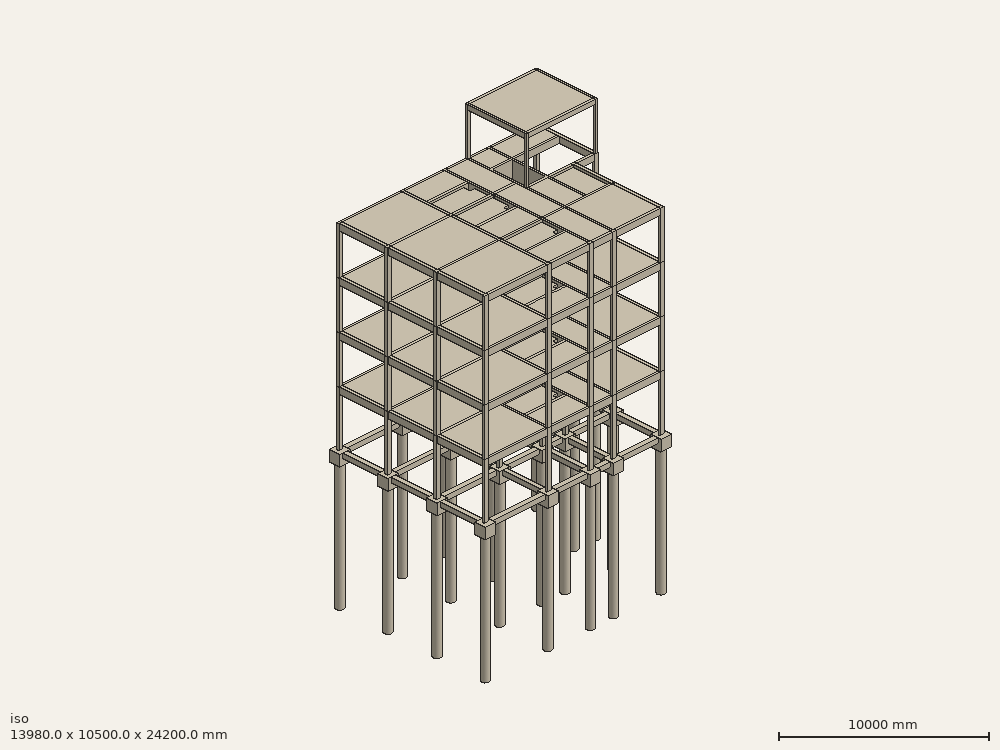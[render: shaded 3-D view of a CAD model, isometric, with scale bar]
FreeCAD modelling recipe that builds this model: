
FCSTD DOCUMENT  (FreeCAD 0.19R24276 (Git))
Label: 2021-02-09 Piloto estructural Metodo 2
License: All rights reserved
objects: Part::FeaturePython×395, Part::Part2DObjectPython×33, App::FeaturePython×28, App::GeometryPython×26, App::DocumentObjectGroup×7, TechDraw::DrawSVGTemplate×3, TechDraw::DrawPage×3, TechDraw::DrawViewAnnotation×2, TechDraw::DrawViewArch×2, Spreadsheet::Sheet×1, App::MaterialObjectPython×1, App::DocumentObjectGroupPython×1, TechDraw::DrawViewPart×1
note: 456 computed .brp shape members not serialized (recipe doc carries the construction recipe); baked Part::Feature solids carry a one-line shape summary decoded from their .brp

FEATURE [Part::FeaturePython] Axis  label="Vertical"  # WARN: FeaturePython — macro-defined, semantics opaque (R4)
  Angles = [0,0,0,0,0,0,0]
  Distances = [1930,4230,2850,1550,1450,1770,1430]
  Length = 11000
  Placement = pos=(0,-500,0) rot=(0,0,1;0rad)
FEATURE [Part::FeaturePython] Axis002  label="Horizontal larga"  # WARN: FeaturePython — macro-defined, semantics opaque (R4)
  Angles = [0,0,0,0,0,0]
  Distances = [100,3250,2620,670,1730,1530]
  Length = 32000
  Placement = pos=(31000,1.077e-12,0) rot=(0,0,1;1.5708rad)
FEATURE [Part::Part2DObjectPython] Rectangle001  label="Lote"  # Draft 2D object (typed FeaturePython)
  Area = 0
  ChamferSize = 0
  Columns = 1
  FilletRadius = 0
  Height = 10000
  Length = 30000
  MakeFace = false
  Rows = 1
FEATURE [Part::Part2DObjectPython] Rectangle002  # Draft 2D object (typed FeaturePython)
  Area = 0
  ChamferSize = 0
  Columns = 1
  FilletRadius = 0
  Height = 700
  Length = 700
  MakeFace = false
  Placement = pos=(14860,9550,0) rot=(0,0,1;0rad)
  Rows = 1
  expr: Height = <<Estructura>>.CabAncho
  expr: Length = <<Estructura>>.CabAncho
FEATURE [Part::Part2DObjectPython] Circle  # Draft 2D object (typed FeaturePython)
  Area = 0
  FirstAngle = 0
  LastAngle = 0
  MakeFace = false
  Placement = pos=(15210,9900,0) rot=(0,0,1;0rad)
  Radius = 250
  expr: Radius = <<Estructura>>.PilRad
FEATURE [Part::FeaturePython] Beam001  # Arch/BIM 7 (typed FeaturePython)
  Chamfer = 0
  DentHeight = 0
  DentLength = 0
  Height = 300
  HorizontalArea = 1059000
  IfcData = attributes={"GlobalId": {"name": "GlobalId", "type": "IfcGloballyUniqueId", "is_enum": false, "enum_values": []}, "Description": {"... (+498 chars omitted),+1 more (map truncated)
  IfcType = 7
  Length = 3530
  MoveBase = false
  MoveWithHost = false
  PerimeterLength = 7660
  Placement = pos=(2280,6490,-800) rot=(0,0,1;0rad)
  PredefinedType = 0
  Tag = VR (30x30)
  VerticalArea = 2298000
  Width = 300
FEATURE [Part::FeaturePython] Structure041  label="Beam002"  # Arch/BIM 7 (typed FeaturePython)
  FaceMaker = 0
  Height = 300
  HorizontalArea = 768000
  IfcData = attributes={"GlobalId": {"name": "GlobalId", "type": "IfcGloballyUniqueId", "is_enum": false, "enum_values": []}, "Description": {"... (+498 chars omitted),+1 more (map truncated)
  IfcType = 7
  Length = 2560
  MoveBase = false
  MoveWithHost = false
  Nodes = (2) [(1.2326e-31,-1.51582e-15,5.55112e-16),(2560,-1.51582e-15,5.55112e-16)]
  NodesOffset = 0
  Normal = (0,0,0)
  PerimeterLength = 5720
  Placement = pos=(1930,9550,-650) rot=(0,0,-1;1.5708rad)
  PredefinedType = 0
  Tag = VR (30x30)
  VerticalArea = 1.716e+06
  Width = 300
  expr: Height = <<Estructura>>.VRAlto
  expr: Width = <<Estructura>>.VRAncho
FEATURE [Part::FeaturePython] Structure042  label="Beam003"  # Arch/BIM 7 (typed FeaturePython)
  FaceMaker = 0
  Height = 300
  HorizontalArea = 777000
  IfcData = attributes={"GlobalId": {"name": "GlobalId", "type": "IfcGloballyUniqueId", "is_enum": false, "enum_values": []}, "Description": {"... (+498 chars omitted),+1 more (map truncated)
  IfcType = 7
  Length = 2590
  MoveBase = false
  MoveWithHost = false
  Nodes = (2) [(1.2326e-31,-1.51582e-15,5.55112e-16),(2590,-1.51582e-15,5.55112e-16)]
  NodesOffset = 0
  Normal = (0,0,0)
  PerimeterLength = 5780
  Placement = pos=(1930,6290,-650) rot=(0,0,-1;1.5708rad)
  PredefinedType = 0
  Tag = VR (30x30)
  VerticalArea = 1.734e+06
  Width = 300
FEATURE [Part::FeaturePython] Structure043  label="Beam004"  # Arch/BIM 7 (typed FeaturePython)
  FaceMaker = 0
  Height = 300
  HorizontalArea = 765000
  IfcData = attributes={"GlobalId": {"name": "GlobalId", "type": "IfcGloballyUniqueId", "is_enum": false, "enum_values": []}, "Description": {"... (+498 chars omitted),+1 more (map truncated)
  IfcType = 7
  Length = 2550
  MoveBase = false
  MoveWithHost = false
  Nodes = (2) [(1.2326e-31,-1.51582e-15,5.55112e-16),(2550,-1.51582e-15,5.55112e-16)]
  NodesOffset = 0
  Normal = (0,0,0)
  PerimeterLength = 5700
  Placement = pos=(1930,3000,-650) rot=(0,0,-1;1.5708rad)
  PredefinedType = 0
  Tag = VR (30x30)
  VerticalArea = 1.71e+06
  Width = 300
FEATURE [Part::FeaturePython] Structure044  label="Beam005"  # Arch/BIM 7 (typed FeaturePython)
  FaceMaker = 0
  Height = 300
  HorizontalArea = 768000
  IfcData = attributes={"GlobalId": {"name": "GlobalId", "type": "IfcGloballyUniqueId", "is_enum": false, "enum_values": []}, "Description": {"... (+498 chars omitted),+1 more (map truncated)
  IfcType = 7
  Length = 2560
  MoveBase = false
  MoveWithHost = false
  Nodes = (2) [(1.2326e-31,-1.51582e-15,5.55112e-16),(2560,-1.51582e-15,5.55112e-16)]
  NodesOffset = 0
  Normal = (0,0,0)
  PerimeterLength = 5720
  Placement = pos=(6160.36,9550,-650) rot=(0,0,-1;1.5708rad)
  PredefinedType = 0
  Tag = VR (30x30)
  VerticalArea = 1.716e+06
  Width = 300
FEATURE [Part::FeaturePython] Structure045  label="Beam006"  # Arch/BIM 7 (typed FeaturePython)
  FaceMaker = 0
  Height = 300
  HorizontalArea = 777000
  IfcData = attributes={"GlobalId": {"name": "GlobalId", "type": "IfcGloballyUniqueId", "is_enum": false, "enum_values": []}, "Description": {"... (+498 chars omitted),+1 more (map truncated)
  IfcType = 7
  Length = 2590
  MoveBase = false
  MoveWithHost = false
  Nodes = (2) [(1.2326e-31,-1.51582e-15,5.55112e-16),(2590,-1.51582e-15,5.55112e-16)]
  NodesOffset = 0
  Normal = (0,0,0)
  PerimeterLength = 5780
  Placement = pos=(6160.36,6290,-650) rot=(0,0,-1;1.5708rad)
  PredefinedType = 0
  Tag = VR (30x30)
  VerticalArea = 1.734e+06
  Width = 300
FEATURE [Part::FeaturePython] Structure046  label="Beam007"  # Arch/BIM 7 (typed FeaturePython)
  FaceMaker = 0
  Height = 300
  HorizontalArea = 765000
  IfcData = attributes={"GlobalId": {"name": "GlobalId", "type": "IfcGloballyUniqueId", "is_enum": false, "enum_values": []}, "Description": {"... (+498 chars omitted),+1 more (map truncated)
  IfcType = 7
  Length = 2550
  MoveBase = false
  MoveWithHost = false
  Nodes = (2) [(1.2326e-31,-1.51582e-15,5.55112e-16),(2550,-1.51582e-15,5.55112e-16)]
  NodesOffset = 0
  Normal = (0,0,0)
  PerimeterLength = 5700
  Placement = pos=(6160.36,3000,-650) rot=(0,0,-1;1.5708rad)
  PredefinedType = 0
  Tag = VR (30x30)
  VerticalArea = 1.71e+06
  Width = 300
FEATURE [Part::FeaturePython] Structure048  label="Beam009"  # Arch/BIM 7 (typed FeaturePython)
  FaceMaker = 0
  Height = 300
  HorizontalArea = 777000
  IfcData = attributes={"GlobalId": {"name": "GlobalId", "type": "IfcGloballyUniqueId", "is_enum": false, "enum_values": []}, "Description": {"... (+498 chars omitted),+1 more (map truncated)
  IfcType = 7
  Length = 2590
  MoveBase = false
  MoveWithHost = false
  Nodes = (2) [(1.2326e-31,-1.51582e-15,5.55112e-16),(2590,-1.51582e-15,5.55112e-16)]
  NodesOffset = 0
  Normal = (0,0,0)
  PerimeterLength = 5780
  Placement = pos=(9010.18,6290,-650) rot=(0,0,-1;1.5708rad)
  PredefinedType = 0
  Tag = VR (30x30)
  VerticalArea = 1.734e+06
  Width = 300
FEATURE [Part::FeaturePython] Structure049  label="Beam010"  # Arch/BIM 7 (typed FeaturePython)
  FaceMaker = 0
  Height = 300
  HorizontalArea = 765000
  IfcData = attributes={"GlobalId": {"name": "GlobalId", "type": "IfcGloballyUniqueId", "is_enum": false, "enum_values": []}, "Description": {"... (+498 chars omitted),+1 more (map truncated)
  IfcType = 7
  Length = 2550
  MoveBase = false
  MoveWithHost = false
  Nodes = (2) [(1.2326e-31,-1.51582e-15,5.55112e-16),(2550,-1.51582e-15,5.55112e-16)]
  NodesOffset = 0
  Normal = (0,0,0)
  PerimeterLength = 5700
  Placement = pos=(9010.18,3000,-650) rot=(0,0,-1;1.5708rad)
  PredefinedType = 0
  Tag = VR (30x30)
  VerticalArea = 1.71e+06
  Width = 300
FEATURE [Part::FeaturePython] Structure053  label="Beam014"  # Arch/BIM 7 (typed FeaturePython)
  FaceMaker = 0
  Height = 300
  HorizontalArea = 765000
  IfcData = attributes={"GlobalId": {"name": "GlobalId", "type": "IfcGloballyUniqueId", "is_enum": false, "enum_values": []}, "Description": {"... (+498 chars omitted),+1 more (map truncated)
  IfcType = 7
  Length = 2550
  MoveBase = false
  MoveWithHost = false
  Nodes = (2) [(1.2326e-31,-1.51582e-15,5.55112e-16),(2550,-1.51582e-15,5.55112e-16)]
  NodesOffset = 0
  Normal = (0,0,0)
  PerimeterLength = 5700
  Placement = pos=(13778.3,3000,-650) rot=(0,0,-1;1.5708rad)
  PredefinedType = 0
  Tag = VR (30x30)
  VerticalArea = 1.71e+06
  Width = 300
FEATURE [Part::FeaturePython] Structure056  label="Beam017"  # Arch/BIM 7 (typed FeaturePython)
  FaceMaker = 0
  Height = 300
  HorizontalArea = 765000
  IfcData = attributes={"GlobalId": {"name": "GlobalId", "type": "IfcGloballyUniqueId", "is_enum": false, "enum_values": []}, "Description": {"... (+498 chars omitted),+1 more (map truncated)
  IfcType = 7
  Length = 2550
  MoveBase = false
  MoveWithHost = false
  Nodes = (2) [(1.2326e-31,-1.51582e-15,5.55112e-16),(2550,-1.51582e-15,5.55112e-16)]
  NodesOffset = 0
  Normal = (0,0,0)
  PerimeterLength = 5700
  Placement = pos=(10560,3000,-650) rot=(0,0,-1;1.5708rad)
  PredefinedType = 0
  Tag = VR (30x30)
  VerticalArea = 1.71e+06
  Width = 300
FEATURE [Part::FeaturePython] Structure059  label="Beam020"  # Arch/BIM 7 (typed FeaturePython)
  FaceMaker = 0
  Height = 300
  HorizontalArea = 645000
  IfcData = attributes={"GlobalId": {"name": "GlobalId", "type": "IfcGloballyUniqueId", "is_enum": false, "enum_values": []}, "Description": {"... (+498 chars omitted),+1 more (map truncated)
  IfcType = 7
  Length = 2150
  MoveBase = false
  MoveWithHost = false
  Nodes = (2) [(1.2326e-31,-1.51582e-15,5.55112e-16),(2150,-1.51582e-15,5.55112e-16)]
  NodesOffset = 0
  Normal = (0,0,0)
  PerimeterLength = 4900
  Placement = pos=(6510,9900,-650) rot=(0,0,1;0rad)
  PredefinedType = 0
  Tag = VR (30x30)
  VerticalArea = 1.47e+06
  Width = 300
FEATURE [Part::FeaturePython] Structure060  label="Beam021"  # Arch/BIM 7 (typed FeaturePython)
  FaceMaker = 0
  Height = 300
  HorizontalArea = 690000
  IfcData = attributes={"GlobalId": {"name": "GlobalId", "type": "IfcGloballyUniqueId", "is_enum": false, "enum_values": []}, "Description": {"... (+498 chars omitted),+1 more (map truncated)
  IfcType = 7
  Length = 2300
  MoveBase = false
  MoveWithHost = false
  Nodes = (2) [(1.2326e-31,-1.51582e-15,5.55112e-16),(2300,-1.51582e-15,5.55112e-16)]
  NodesOffset = 0
  Normal = (0,0,0)
  PerimeterLength = 5200
  Placement = pos=(9360,9900,-650) rot=(0,0,1;0rad)
  PredefinedType = 0
  Tag = VR (30x30)
  VerticalArea = 1.56e+06
  Width = 300
FEATURE [Part::FeaturePython] Structure061  label="Beam022"  # Arch/BIM 7 (typed FeaturePython)
  FaceMaker = 0
  Height = 300
  HorizontalArea = 750000
  IfcData = attributes={"GlobalId": {"name": "GlobalId", "type": "IfcGloballyUniqueId", "is_enum": false, "enum_values": []}, "Description": {"... (+498 chars omitted),+1 more (map truncated)
  IfcType = 7
  Length = 2500
  MoveBase = false
  MoveWithHost = false
  Nodes = (2) [(1.2326e-31,-1.51582e-15,5.55112e-16),(2500,-1.51582e-15,5.55112e-16)]
  NodesOffset = 0
  Normal = (0,0,0)
  PerimeterLength = 5600
  Placement = pos=(12360,9900,-650) rot=(0,0,1;0rad)
  PredefinedType = 0
  Tag = VR (30x30)
  VerticalArea = 1680000
  Width = 300
FEATURE [Part::FeaturePython] Structure064  label="Beam025"  # Arch/BIM 7 (typed FeaturePython)
  FaceMaker = 0
  Height = 300
  HorizontalArea = 645000
  IfcData = attributes={"GlobalId": {"name": "GlobalId", "type": "IfcGloballyUniqueId", "is_enum": false, "enum_values": []}, "Description": {"... (+498 chars omitted),+1 more (map truncated)
  IfcType = 7
  Length = 2150
  MoveBase = false
  MoveWithHost = false
  Nodes = (2) [(1.2326e-31,-1.51582e-15,5.55112e-16),(2150,-1.51582e-15,5.55112e-16)]
  NodesOffset = 0
  Normal = (0,0,0)
  PerimeterLength = 4900
  Placement = pos=(6510,6640,-650) rot=(0,0,1;0rad)
  PredefinedType = 0
  Tag = VR (30x30)
  VerticalArea = 1.47e+06
  Width = 300
FEATURE [Part::FeaturePython] Structure065  label="Beam026"  # Arch/BIM 7 (typed FeaturePython)
  FaceMaker = 0
  Height = 300
  HorizontalArea = 768000
  IfcData = attributes={"GlobalId": {"name": "GlobalId", "type": "IfcGloballyUniqueId", "is_enum": false, "enum_values": []}, "Description": {"... (+498 chars omitted),+1 more (map truncated)
  IfcType = 7
  Length = 2560
  MoveBase = false
  MoveWithHost = false
  Nodes = (2) [(1.2326e-31,-1.51582e-15,5.55112e-16),(2560,-1.51582e-15,5.55112e-16)]
  NodesOffset = 0
  Normal = (0,0,0)
  PerimeterLength = 5720
  Placement = pos=(9010,6990,-650) rot=(0,0,1;1.5708rad)
  PredefinedType = 0
  Tag = VR (30x30)
  VerticalArea = 1.716e+06
  Width = 300
FEATURE [Part::FeaturePython] Structure066  label="Beam027"  # Arch/BIM 7 (typed FeaturePython)
  FaceMaker = 0
  Height = 300
  HorizontalArea = 1.059e+06
  IfcData = attributes={"GlobalId": {"name": "GlobalId", "type": "IfcGloballyUniqueId", "is_enum": false, "enum_values": []}, "Description": {"... (+498 chars omitted),+1 more (map truncated)
  IfcType = 7
  Length = 3530
  MoveBase = false
  MoveWithHost = false
  Nodes = (2) [(1.2326e-31,-1.51582e-15,5.55112e-16),(3530,-1.51582e-15,5.55112e-16)]
  NodesOffset = 0
  Normal = (0,0,0)
  PerimeterLength = 7660
  Placement = pos=(2280,3350,-650) rot=(0,0,1;0rad)
  PredefinedType = 0
  Tag = VR (30x30)
  VerticalArea = 2.298e+06
  Width = 300
FEATURE [Part::FeaturePython] Structure067  label="Beam028"  # Arch/BIM 7 (typed FeaturePython)
  FaceMaker = 0
  Height = 300
  HorizontalArea = 645000
  IfcData = attributes={"GlobalId": {"name": "GlobalId", "type": "IfcGloballyUniqueId", "is_enum": false, "enum_values": []}, "Description": {"... (+498 chars omitted),+1 more (map truncated)
  IfcType = 7
  Length = 2150
  MoveBase = false
  MoveWithHost = false
  Nodes = (2) [(1.2326e-31,-1.51582e-15,5.55112e-16),(2150,-1.51582e-15,5.55112e-16)]
  NodesOffset = 0
  Normal = (0,0,0)
  PerimeterLength = 4900
  Placement = pos=(6510,3350,-650) rot=(0,0,1;0rad)
  PredefinedType = 0
  Tag = VR (30x30)
  VerticalArea = 1.47e+06
  Width = 300
FEATURE [Part::FeaturePython] Structure068  label="Beam029"  # Arch/BIM 7 (typed FeaturePython)
  FaceMaker = 0
  Height = 300
  HorizontalArea = 1.059e+06
  IfcData = attributes={"GlobalId": {"name": "GlobalId", "type": "IfcGloballyUniqueId", "is_enum": false, "enum_values": []}, "Description": {"... (+498 chars omitted),+1 more (map truncated)
  IfcType = 7
  Length = 3530
  MoveBase = false
  MoveWithHost = false
  Nodes = (2) [(1.2326e-31,-1.51582e-15,5.55112e-16),(3530,-1.51582e-15,5.55112e-16)]
  NodesOffset = 0
  Normal = (0,0,0)
  PerimeterLength = 7660
  Placement = pos=(2280,100,-650) rot=(0,0,1;0rad)
  PredefinedType = 0
  Tag = VR (30x30)
  VerticalArea = 2.298e+06
  Width = 300
FEATURE [Part::FeaturePython] Structure069  label="Beam030"  # Arch/BIM 7 (typed FeaturePython)
  FaceMaker = 0
  Height = 300
  HorizontalArea = 645000
  IfcData = attributes={"GlobalId": {"name": "GlobalId", "type": "IfcGloballyUniqueId", "is_enum": false, "enum_values": []}, "Description": {"... (+498 chars omitted),+1 more (map truncated)
  IfcType = 7
  Length = 2150
  MoveBase = false
  MoveWithHost = false
  Nodes = (2) [(1.2326e-31,-1.51582e-15,5.55112e-16),(2150,-1.51582e-15,5.55112e-16)]
  NodesOffset = 0
  Normal = (0,0,0)
  PerimeterLength = 4900
  Placement = pos=(6510,100,-650) rot=(0,0,1;0rad)
  PredefinedType = 0
  Tag = VR (30x30)
  VerticalArea = 1.47e+06
  Width = 300
FEATURE [Part::FeaturePython] Structure070  label="Beam031"  # Arch/BIM 7 (typed FeaturePython)
  FaceMaker = 0
  Height = 300
  HorizontalArea = 255000
  IfcData = attributes={"GlobalId": {"name": "GlobalId", "type": "IfcGloballyUniqueId", "is_enum": false, "enum_values": []}, "Description": {"... (+498 chars omitted),+1 more (map truncated)
  IfcType = 7
  Length = 850
  MoveBase = false
  MoveWithHost = false
  Nodes = (2) [(1.2326e-31,-1.51582e-15,5.55112e-16),(850,-1.51582e-15,5.55112e-16)]
  NodesOffset = 0
  Normal = (0,0,0)
  PerimeterLength = 2300
  Placement = pos=(9360,100,-650) rot=(0,0,1;0rad)
  PredefinedType = 0
  Tag = VR (30x30)
  VerticalArea = 690000
  Width = 300
FEATURE [Part::FeaturePython] Structure071  label="Beam032"  # Arch/BIM 7 (typed FeaturePython)
  FaceMaker = 0
  Height = 300
  HorizontalArea = 756000
  IfcData = attributes={"GlobalId": {"name": "GlobalId", "type": "IfcGloballyUniqueId", "is_enum": false, "enum_values": []}, "Description": {"... (+498 chars omitted),+1 more (map truncated)
  IfcType = 7
  Length = 2520
  MoveBase = false
  MoveWithHost = false
  Nodes = (2) [(1.2326e-31,-1.51582e-15,5.55112e-16),(2520,-1.51582e-15,5.55112e-16)]
  NodesOffset = 0
  Normal = (0,0,0)
  PerimeterLength = 5640
  Placement = pos=(10910,100,-650) rot=(0,0,1;0rad)
  PredefinedType = 0
  Tag = VR (30x30)
  VerticalArea = 1.692e+06
  Width = 300
FEATURE [Part::FeaturePython] Structure072  label="Beam033"  # Arch/BIM 7 (typed FeaturePython)
  FaceMaker = 0
  Height = 300
  HorizontalArea = 255000
  IfcData = attributes={"GlobalId": {"name": "GlobalId", "type": "IfcGloballyUniqueId", "is_enum": false, "enum_values": []}, "Description": {"... (+498 chars omitted),+1 more (map truncated)
  IfcType = 7
  Length = 850
  MoveBase = false
  MoveWithHost = false
  Nodes = (2) [(1.2326e-31,-1.51582e-15,5.55112e-16),(850,-1.51582e-15,5.55112e-16)]
  NodesOffset = 0
  Normal = (0,0,0)
  PerimeterLength = 2300
  Placement = pos=(9360,3350,-650) rot=(0,0,1;0rad)
  PredefinedType = 0
  Tag = VR (30x30)
  VerticalArea = 690000
  Width = 300
FEATURE [Part::FeaturePython] Structure073  label="Beam034"  # Arch/BIM 7 (typed FeaturePython)
  FaceMaker = 0
  Height = 300
  HorizontalArea = 756000
  IfcData = attributes={"GlobalId": {"name": "GlobalId", "type": "IfcGloballyUniqueId", "is_enum": false, "enum_values": []}, "Description": {"... (+498 chars omitted),+1 more (map truncated)
  IfcType = 7
  Length = 2520
  MoveBase = false
  MoveWithHost = false
  Nodes = (2) [(1.2326e-31,-1.51582e-15,5.55112e-16),(2520,-1.51582e-15,5.55112e-16)]
  NodesOffset = 0
  Normal = (0,0,0)
  PerimeterLength = 5640
  Placement = pos=(10910,3350,-650) rot=(0,0,1;0rad)
  PredefinedType = 0
  Tag = VR (30x30)
  VerticalArea = 1.692e+06
  Width = 300
FEATURE [Part::FeaturePython] Structure074  label="Beam035"  # Arch/BIM 7 (typed FeaturePython)
  FaceMaker = 0
  Height = 300
  HorizontalArea = 969000
  IfcData = attributes={"GlobalId": {"name": "GlobalId", "type": "IfcGloballyUniqueId", "is_enum": false, "enum_values": []}, "Description": {"... (+498 chars omitted),+1 more (map truncated)
  IfcType = 7
  Length = 3230
  MoveBase = false
  MoveWithHost = false
  Nodes = (2) [(1.2326e-31,-1.51582e-15,5.55112e-16),(3230,-1.51582e-15,5.55112e-16)]
  NodesOffset = 0
  Normal = (0,0,0)
  PerimeterLength = 7060
  Placement = pos=(15210,9550,-650) rot=(0,0,-1;1.5708rad)
  PredefinedType = 0
  Tag = VR (30x30)
  VerticalArea = 2.118e+06
  Width = 300
FEATURE [Part::FeaturePython] Structure075  label="Beam036"  # Arch/BIM 7 (typed FeaturePython)
  FaceMaker = 0
  Height = 300
  HorizontalArea = 576000
  IfcData = attributes={"GlobalId": {"name": "GlobalId", "type": "IfcGloballyUniqueId", "is_enum": false, "enum_values": []}, "Description": {"... (+498 chars omitted),+1 more (map truncated)
  IfcType = 7
  Length = 1920
  MoveBase = false
  MoveWithHost = false
  Nodes = (2) [(1.2326e-31,-1.51582e-15,5.55112e-16),(1920,-1.51582e-15,5.55112e-16)]
  NodesOffset = 0
  Normal = (0,0,0)
  PerimeterLength = 4440
  Placement = pos=(13780,3700,-650) rot=(0,0,1;1.5708rad)
  PredefinedType = 0
  Tag = VR (30x30)
  VerticalArea = 1332000
  Width = 300
FEATURE [Part::FeaturePython] Structure076  label="Beam037"  # Arch/BIM 7 (typed FeaturePython)
  FaceMaker = 0
  Height = 300
  HorizontalArea = 219000
  IfcData = attributes={"GlobalId": {"name": "GlobalId", "type": "IfcGloballyUniqueId", "is_enum": false, "enum_values": []}, "Description": {"... (+498 chars omitted),+1 more (map truncated)
  IfcType = 7
  Length = 730
  MoveBase = false
  MoveWithHost = false
  Nodes = (2) [(1.2326e-31,-1.51582e-15,5.55112e-16),(730,-1.51582e-15,5.55112e-16)]
  NodesOffset = 0
  Normal = (0,0,0)
  PerimeterLength = 2060
  Placement = pos=(14130,5970,-650) rot=(0,0,1;0rad)
  PredefinedType = 0
  Tag = VR (30x30)
  VerticalArea = 618000
  Width = 300
FEATURE [Part::FeaturePython] Structure077  label="Beam038"  # Arch/BIM 7 (typed FeaturePython)
  FaceMaker = 0
  Height = 300
  HorizontalArea = 681000
  IfcData = attributes={"GlobalId": {"name": "GlobalId", "type": "IfcGloballyUniqueId", "is_enum": false, "enum_values": []}, "Description": {"... (+498 chars omitted),+1 more (map truncated)
  IfcType = 7
  Length = 2270
  MoveBase = false
  MoveWithHost = false
  Nodes = (2) [(1.2326e-31,-1.51582e-15,5.55112e-16),(2270,-1.51582e-15,5.55112e-16)]
  NodesOffset = 0
  Normal = (0,0,0)
  PerimeterLength = 5140
  Placement = pos=(10560,3700,-650) rot=(0,0,1;1.5708rad)
  PredefinedType = 0
  Tag = VR (30x30)
  VerticalArea = 1.542e+06
  Width = 300
FEATURE [Part::FeaturePython] Structure078  label="Beam039"  # Arch/BIM 7 (typed FeaturePython)
  FaceMaker = 0
  Height = 300
  HorizontalArea = 414000
  IfcData = attributes={"GlobalId": {"name": "GlobalId", "type": "IfcGloballyUniqueId", "is_enum": false, "enum_values": []}, "Description": {"... (+498 chars omitted),+1 more (map truncated)
  IfcType = 7
  Length = 1380
  MoveBase = false
  MoveWithHost = false
  Nodes = (2) [(1.2326e-31,-1.51582e-15,5.55112e-16),(1380,-1.51582e-15,5.55112e-16)]
  NodesOffset = 0
  Normal = (0,0,0)
  PerimeterLength = 3360
  Placement = pos=(10560,9750,-650) rot=(0,0,-1;1.5708rad)
  PredefinedType = 0
  Tag = VR (30x30)
  VerticalArea = 1008000
  Width = 300
FEATURE [Part::FeaturePython] Structure079  label="Beam040"  # Arch/BIM 7 (typed FeaturePython)
  FaceMaker = 0
  Height = 300
  HorizontalArea = 354000
  IfcData = attributes={"GlobalId": {"name": "GlobalId", "type": "IfcGloballyUniqueId", "is_enum": false, "enum_values": []}, "Description": {"... (+498 chars omitted),+1 more (map truncated)
  IfcType = 7
  Length = 1180
  MoveBase = false
  MoveWithHost = false
  Nodes = (2) [(1.2326e-31,-1.51582e-15,5.55112e-16),(1180,-1.51582e-15,5.55112e-16)]
  NodesOffset = 0
  Normal = (0,0,0)
  PerimeterLength = 2960
  Placement = pos=(12010,9550,-650) rot=(0,0,-1;1.5708rad)
  PredefinedType = 0
  Tag = VR (30x30)
  VerticalArea = 888000
  Width = 300
FEATURE [Part::FeaturePython] Structure080  label="Beam041"  # Arch/BIM 7 (typed FeaturePython)
  FaceMaker = 0
  Height = 300
  HorizontalArea = 426000
  IfcData = attributes={"GlobalId": {"name": "GlobalId", "type": "IfcGloballyUniqueId", "is_enum": false, "enum_values": []}, "Description": {"... (+498 chars omitted),+1 more (map truncated)
  IfcType = 7
  Length = 1420
  MoveBase = false
  MoveWithHost = false
  Nodes = (2) [(1.2326e-31,-1.51582e-15,5.55112e-16),(1420,-1.51582e-15,5.55112e-16)]
  NodesOffset = 0
  Normal = (0,0,0)
  PerimeterLength = 3440
  Placement = pos=(13430,5970,-650) rot=(0,0,1;3.14159rad)
  PredefinedType = 0
  Tag = VR (30x30)
  VerticalArea = 1.032e+06
  Width = 300
FEATURE [Part::Part2DObjectPython] Rectangle  # Draft 2D object (typed FeaturePython)
  Area = 0
  ChamferSize = 0
  Columns = 1
  FilletRadius = 0
  Height = 2550
  Length = 1600
  MakeFace = false
  Placement = pos=(10485,5895,0) rot=(0,0,1;0rad)
  Rows = 1
FEATURE [Spreadsheet::Sheet] Spreadsheet  label="Estructura"
  cells = A1=MODELO ESTRUCTURAL; A2=Descripcion; B2=Alias; C2=Valor; D2=Unidad; A3=Cabezal Ancho; B3=CabAncho; C3(CabAncho)=700; D3=mm; A4=Cabezal Espesor; B4=CabEsp; C4(CabEsp)=700; D4=mm; A5=Pilote Radio; B5=PilRad; C5(PilRad)=250; D5=mm; A6=Pilote Profundidad; B6=PilProf; C6(PilProf)=8000; D6=mm; A7=Viga Riostra Ancho; B7=VRAncho; C7(VRAncho)=300; D7=mm; A8=Viga Riostra Alto; B8=VRAlto; C8(VRAlto)=300; D8=mm
FEATURE [Part::FeaturePython] Beam  # Arch/BIM 7 (typed FeaturePython)
  Chamfer = 0
  DentHeight = 0
  DentLength = 0
  Height = 300
  HorizontalArea = 1059000
  IfcData = attributes={"GlobalId": {"name": "GlobalId", "type": "IfcGloballyUniqueId", "is_enum": false, "enum_values": []}, "Description": {"... (+498 chars omitted),+1 more (map truncated)
  IfcType = 7
  Length = 3530
  MoveBase = false
  MoveWithHost = false
  PerimeterLength = 7660
  Placement = pos=(2280,9750,-800) rot=(0,0,1;0rad)
  PredefinedType = 0
  Tag = VR (30x30)
  VerticalArea = 2298000
  Width = 300
FEATURE [Part::Part2DObjectPython] Rectangle003  # Draft 2D object (typed FeaturePython)
  Area = 0
  ChamferSize = 0
  Columns = 1
  FilletRadius = 0
  Height = 2550
  Length = 1600
  MakeFace = false
  Placement = pos=(10485,5895,0) rot=(0,0,1;0rad)
  Rows = 1
FEATURE [Part::FeaturePython] Structure142  label="V15x40 V133"  # Arch/BIM 7 (typed FeaturePython)
  FaceMaker = 0
  Height = 400
  HorizontalArea = 597000
  IfcData = attributes={"GlobalId": {"name": "GlobalId", "type": "IfcGloballyUniqueId", "is_enum": false, "enum_values": []}, "Description": {"... (+475 chars omitted),+1 more (map truncated)
  IfcType = 7
  Length = 3980
  MoveBase = false
  MoveWithHost = false
  Nodes = (2) [(-1.72563e-31,-1.42109e-15,-7.77156e-16),(3980,-1.42109e-15,-7.77156e-16)]
  NodesOffset = 0
  Normal = (0,0,0)
  PerimeterLength = 8260
  Placement = pos=(2055,9900,5800) rot=(0,0,1;0rad)
  PredefinedType = 0
  VerticalArea = 3.304e+06
  Width = 150
FEATURE [Part::FeaturePython] Structure143  label="V15x40 V134"  # Arch/BIM 7 (typed FeaturePython)
  FaceMaker = 0
  Height = 400
  HorizontalArea = 390000
  IfcData = attributes={"GlobalId": {"name": "GlobalId", "type": "IfcGloballyUniqueId", "is_enum": false, "enum_values": []}, "Description": {"... (+475 chars omitted),+1 more (map truncated)
  IfcType = 7
  Length = 2600
  MoveBase = false
  MoveWithHost = false
  Nodes = (2) [(-1.72563e-31,-1.42109e-15,-7.77156e-16),(2600,-1.42109e-15,-7.77156e-16)]
  NodesOffset = 0
  Normal = (0,0,0)
  PerimeterLength = 5500
  Placement = pos=(6285,9900,5800) rot=(0,0,1;0rad)
  PredefinedType = 0
  VerticalArea = 2200000
  Width = 150
FEATURE [Part::FeaturePython] Structure144  label="V15x40 V135"  # Arch/BIM 7 (typed FeaturePython)
  FaceMaker = 0
  Height = 400
  HorizontalArea = 412500
  IfcData = attributes={"GlobalId": {"name": "GlobalId", "type": "IfcGloballyUniqueId", "is_enum": false, "enum_values": []}, "Description": {"... (+475 chars omitted),+1 more (map truncated)
  IfcType = 7
  Length = 2750
  MoveBase = false
  MoveWithHost = false
  Nodes = (2) [(-1.72563e-31,-1.42109e-15,-7.77156e-16),(2750,-1.42109e-15,-7.77156e-16)]
  NodesOffset = 0
  Normal = (0,0,0)
  PerimeterLength = 5800
  Placement = pos=(9135,9900,5800) rot=(0,0,1;0rad)
  PredefinedType = 0
  VerticalArea = 2320000
  Width = 150
FEATURE [Part::FeaturePython] Structure145  label="V15x40 V136"  # Arch/BIM 7 (typed FeaturePython)
  FaceMaker = 0
  Height = 400
  HorizontalArea = 442500
  IfcData = attributes={"GlobalId": {"name": "GlobalId", "type": "IfcGloballyUniqueId", "is_enum": false, "enum_values": []}, "Description": {"... (+475 chars omitted),+1 more (map truncated)
  IfcType = 7
  Length = 2950
  MoveBase = false
  MoveWithHost = false
  Nodes = (2) [(-1.72563e-31,-1.42109e-15,-7.77156e-16),(2950,-1.42109e-15,-7.77156e-16)]
  NodesOffset = 0
  Normal = (0,0,0)
  PerimeterLength = 6200
  Placement = pos=(12135,9900,5800) rot=(0,0,1;0rad)
  PredefinedType = 0
  VerticalArea = 2.48e+06
  Width = 150
FEATURE [Part::FeaturePython] Structure146  label="V15x40 V137"  # Arch/BIM 7 (typed FeaturePython)
  FaceMaker = 0
  Height = 400
  HorizontalArea = 453750
  IfcData = attributes={"GlobalId": {"name": "GlobalId", "type": "IfcGloballyUniqueId", "is_enum": false, "enum_values": []}, "Description": {"... (+475 chars omitted),+1 more (map truncated)
  IfcType = 7
  Length = 3025
  MoveBase = false
  MoveWithHost = false
  Nodes = (2) [(-1.72563e-31,-1.42109e-15,-7.77156e-16),(3025,-1.42109e-15,-7.77156e-16)]
  NodesOffset = 0
  Normal = (0,0,0)
  PerimeterLength = 6350
  Placement = pos=(12085,8370,5800) rot=(0,0,1;0rad)
  PredefinedType = 0
  VerticalArea = 2.54e+06
  Width = 150
FEATURE [Part::FeaturePython] Structure147  label="V15x40 V138"  # Arch/BIM 7 (typed FeaturePython)
  FaceMaker = 0
  Height = 400
  HorizontalArea = 597000
  IfcData = attributes={"GlobalId": {"name": "GlobalId", "type": "IfcGloballyUniqueId", "is_enum": false, "enum_values": []}, "Description": {"... (+475 chars omitted),+1 more (map truncated)
  IfcType = 7
  Length = 3980
  MoveBase = false
  MoveWithHost = false
  Nodes = (2) [(-1.72563e-31,-1.42109e-15,-7.77156e-16),(3980,-1.42109e-15,-7.77156e-16)]
  NodesOffset = 0
  Normal = (0,0,0)
  PerimeterLength = 8260
  Placement = pos=(2055,6640,5800) rot=(0,0,1;0rad)
  PredefinedType = 0
  VerticalArea = 3.304e+06
  Width = 150
FEATURE [Part::FeaturePython] Structure148  label="V15x40 V139"  # Arch/BIM 7 (typed FeaturePython)
  FaceMaker = 0
  Height = 400
  HorizontalArea = 397500
  IfcData = attributes={"GlobalId": {"name": "GlobalId", "type": "IfcGloballyUniqueId", "is_enum": false, "enum_values": []}, "Description": {"... (+475 chars omitted),+1 more (map truncated)
  IfcType = 7
  Length = 2650
  MoveBase = false
  MoveWithHost = false
  Nodes = (2) [(-1.72563e-31,-1.42109e-15,-7.77156e-16),(2650,-1.42109e-15,-7.77156e-16)]
  NodesOffset = 0
  Normal = (0,0,0)
  PerimeterLength = 5600
  Placement = pos=(6285,6640,5800) rot=(0,0,1;0rad)
  PredefinedType = 0
  VerticalArea = 2240000
  Width = 150
FEATURE [Part::FeaturePython] Structure149  label="V15x40 V140"  # Arch/BIM 7 (typed FeaturePython)
  FaceMaker = 0
  Height = 400
  HorizontalArea = 210000
  IfcData = attributes={"GlobalId": {"name": "GlobalId", "type": "IfcGloballyUniqueId", "is_enum": false, "enum_values": []}, "Description": {"... (+475 chars omitted),+1 more (map truncated)
  IfcType = 7
  Length = 1400
  MoveBase = false
  MoveWithHost = false
  Nodes = (2) [(-1.72563e-31,-1.42109e-15,-7.77156e-16),(1400,-1.42109e-15,-7.77156e-16)]
  NodesOffset = 0
  Normal = (0,0,0)
  PerimeterLength = 3100
  Placement = pos=(9085,6640,5800) rot=(0,0,1;0rad)
  PredefinedType = 0
  VerticalArea = 1240000
  Width = 150
FEATURE [Part::FeaturePython] Structure150  label="V15x40 V141"  # Arch/BIM 7 (typed FeaturePython)
  FaceMaker = 0
  Height = 400
  HorizontalArea = 235500
  IfcData = attributes={"GlobalId": {"name": "GlobalId", "type": "IfcGloballyUniqueId", "is_enum": false, "enum_values": []}, "Description": {"... (+475 chars omitted),+1 more (map truncated)
  IfcType = 7
  Length = 1570
  MoveBase = false
  MoveWithHost = false
  Nodes = (2) [(-1.72563e-31,-1.42109e-15,-7.77156e-16),(1570,-1.42109e-15,-7.77156e-16)]
  NodesOffset = 0
  Normal = (0,0,0)
  PerimeterLength = 3440
  Placement = pos=(13655,5970,5800) rot=(0,0,1;3.14159rad)
  PredefinedType = 0
  VerticalArea = 1.376e+06
  Width = 150
FEATURE [Part::FeaturePython] Structure151  label="V15x40 V142"  # Arch/BIM 7 (typed FeaturePython)
  FaceMaker = 0
  Height = 400
  HorizontalArea = 177000
  IfcData = attributes={"GlobalId": {"name": "GlobalId", "type": "IfcGloballyUniqueId", "is_enum": false, "enum_values": []}, "Description": {"... (+475 chars omitted),+1 more (map truncated)
  IfcType = 7
  Length = 1180
  MoveBase = false
  MoveWithHost = false
  Nodes = (2) [(-1.72563e-31,-1.42109e-15,-7.77156e-16),(1180,-1.42109e-15,-7.77156e-16)]
  NodesOffset = 0
  Normal = (0,0,0)
  PerimeterLength = 2660
  Placement = pos=(13905,5970,5800) rot=(0,0,1;0rad)
  PredefinedType = 0
  VerticalArea = 1064000
  Width = 150
FEATURE [Part::FeaturePython] Structure152  label="V15x40 V143"  # Arch/BIM 7 (typed FeaturePython)
  FaceMaker = 0
  Height = 400
  HorizontalArea = 597000
  IfcData = attributes={"GlobalId": {"name": "GlobalId", "type": "IfcGloballyUniqueId", "is_enum": false, "enum_values": []}, "Description": {"... (+475 chars omitted),+1 more (map truncated)
  IfcType = 7
  Length = 3980
  MoveBase = false
  MoveWithHost = false
  Nodes = (2) [(-1.72563e-31,-1.42109e-15,-7.77156e-16),(3980,-1.42109e-15,-7.77156e-16)]
  NodesOffset = 0
  Normal = (0,0,0)
  PerimeterLength = 8260
  Placement = pos=(2055,3350,5800) rot=(0,0,1;0rad)
  PredefinedType = 0
  VerticalArea = 3.304e+06
  Width = 150
FEATURE [Part::FeaturePython] Structure153  label="V15x40 V144"  # Arch/BIM 7 (typed FeaturePython)
  FaceMaker = 0
  Height = 400
  HorizontalArea = 397500
  IfcData = attributes={"GlobalId": {"name": "GlobalId", "type": "IfcGloballyUniqueId", "is_enum": false, "enum_values": []}, "Description": {"... (+475 chars omitted),+1 more (map truncated)
  IfcType = 7
  Length = 2650
  MoveBase = false
  MoveWithHost = false
  Nodes = (2) [(-1.72563e-31,-1.42109e-15,-7.77156e-16),(2650,-1.42109e-15,-7.77156e-16)]
  NodesOffset = 0
  Normal = (0,0,0)
  PerimeterLength = 5600
  Placement = pos=(6285,3350,5800) rot=(0,0,1;0rad)
  PredefinedType = 0
  VerticalArea = 2240000
  Width = 150
FEATURE [Part::FeaturePython] Structure154  label="V15x40 V145"  # Arch/BIM 7 (typed FeaturePython)
  FaceMaker = 0
  Height = 400
  HorizontalArea = 210000
  IfcData = attributes={"GlobalId": {"name": "GlobalId", "type": "IfcGloballyUniqueId", "is_enum": false, "enum_values": []}, "Description": {"... (+475 chars omitted),+1 more (map truncated)
  IfcType = 7
  Length = 1400
  MoveBase = false
  MoveWithHost = false
  Nodes = (2) [(-1.72563e-31,-1.42109e-15,-7.77156e-16),(1400,-1.42109e-15,-7.77156e-16)]
  NodesOffset = 0
  Normal = (0,0,0)
  PerimeterLength = 3100
  Placement = pos=(9085,3350,5800) rot=(0,0,1;0rad)
  PredefinedType = 0
  VerticalArea = 1240000
  Width = 150
FEATURE [Part::FeaturePython] Structure155  label="V15x40 V146"  # Arch/BIM 7 (typed FeaturePython)
  FaceMaker = 0
  Height = 400
  HorizontalArea = 460500
  IfcData = attributes={"GlobalId": {"name": "GlobalId", "type": "IfcGloballyUniqueId", "is_enum": false, "enum_values": []}, "Description": {"... (+475 chars omitted),+1 more (map truncated)
  IfcType = 7
  Length = 3070
  MoveBase = false
  MoveWithHost = false
  Nodes = (2) [(-1.72563e-31,-1.42109e-15,-7.77156e-16),(3070,-1.42109e-15,-7.77156e-16)]
  NodesOffset = 0
  Normal = (0,0,0)
  PerimeterLength = 6440
  Placement = pos=(10635,3350,5800) rot=(0,0,1;0rad)
  PredefinedType = 0
  VerticalArea = 2.576e+06
  Width = 150
FEATURE [Part::FeaturePython] Structure156  label="V15x40 V147"  # Arch/BIM 7 (typed FeaturePython)
  FaceMaker = 0
  Height = 400
  HorizontalArea = 597000
  IfcData = attributes={"GlobalId": {"name": "GlobalId", "type": "IfcGloballyUniqueId", "is_enum": false, "enum_values": []}, "Description": {"... (+475 chars omitted),+1 more (map truncated)
  IfcType = 7
  Length = 3980
  MoveBase = false
  MoveWithHost = false
  Nodes = (2) [(-1.72563e-31,-1.42109e-15,-7.77156e-16),(3980,-1.42109e-15,-7.77156e-16)]
  NodesOffset = 0
  Normal = (0,0,0)
  PerimeterLength = 8260
  Placement = pos=(2055,100,5800) rot=(0,0,1;0rad)
  PredefinedType = 0
  VerticalArea = 3.304e+06
  Width = 150
FEATURE [Part::FeaturePython] Structure157  label="V15x40 V148"  # Arch/BIM 7 (typed FeaturePython)
  FaceMaker = 0
  Height = 400
  HorizontalArea = 390000
  IfcData = attributes={"GlobalId": {"name": "GlobalId", "type": "IfcGloballyUniqueId", "is_enum": false, "enum_values": []}, "Description": {"... (+475 chars omitted),+1 more (map truncated)
  IfcType = 7
  Length = 2600
  MoveBase = false
  MoveWithHost = false
  Nodes = (2) [(-1.72563e-31,-1.42109e-15,-7.77156e-16),(2600,-1.42109e-15,-7.77156e-16)]
  NodesOffset = 0
  Normal = (0,0,0)
  PerimeterLength = 5500
  Placement = pos=(6285,100,5800) rot=(0,0,1;0rad)
  PredefinedType = 0
  VerticalArea = 2200000
  Width = 150
FEATURE [Part::FeaturePython] Structure158  label="V15x40 V149"  # Arch/BIM 7 (typed FeaturePython)
  FaceMaker = 0
  Height = 400
  HorizontalArea = 195000
  IfcData = attributes={"GlobalId": {"name": "GlobalId", "type": "IfcGloballyUniqueId", "is_enum": false, "enum_values": []}, "Description": {"... (+475 chars omitted),+1 more (map truncated)
  IfcType = 7
  Length = 1300
  MoveBase = false
  MoveWithHost = false
  Nodes = (2) [(-1.72563e-31,-1.42109e-15,-7.77156e-16),(1300,-1.42109e-15,-7.77156e-16)]
  NodesOffset = 0
  Normal = (0,0,0)
  PerimeterLength = 2900
  Placement = pos=(9135,100,5800) rot=(0,0,1;0rad)
  PredefinedType = 0
  VerticalArea = 1160000
  Width = 150
FEATURE [Part::FeaturePython] Structure159  label="V15x40 V150"  # Arch/BIM 7 (typed FeaturePython)
  FaceMaker = 0
  Height = 400
  HorizontalArea = 445500
  IfcData = attributes={"GlobalId": {"name": "GlobalId", "type": "IfcGloballyUniqueId", "is_enum": false, "enum_values": []}, "Description": {"... (+475 chars omitted),+1 more (map truncated)
  IfcType = 7
  Length = 2970
  MoveBase = false
  MoveWithHost = false
  Nodes = (2) [(-1.72563e-31,-1.42109e-15,-7.77156e-16),(2970,-1.42109e-15,-7.77156e-16)]
  NodesOffset = 0
  Normal = (0,0,0)
  PerimeterLength = 6240
  Placement = pos=(10685,100,5800) rot=(0,0,1;0rad)
  PredefinedType = 0
  VerticalArea = 2.496e+06
  Width = 150
FEATURE [Part::FeaturePython] Structure160  label="V15x40 V151"  # Arch/BIM 7 (typed FeaturePython)
  FaceMaker = 0
  Height = 400
  HorizontalArea = 465000
  IfcData = attributes={"GlobalId": {"name": "GlobalId", "type": "IfcGloballyUniqueId", "is_enum": false, "enum_values": []}, "Description": {"... (+475 chars omitted),+1 more (map truncated)
  IfcType = 7
  Length = 3100
  MoveBase = false
  MoveWithHost = false
  Nodes = (2) [(-1.72563e-31,-1.42109e-15,-7.77156e-16),(3100,-1.42109e-15,-7.77156e-16)]
  NodesOffset = 0
  Normal = (0,0,0)
  PerimeterLength = 6500
  Placement = pos=(6160,3275,5800) rot=(0,0,-1;1.5708rad)
  PredefinedType = 0
  VerticalArea = 2.6e+06
  Width = 150
FEATURE [Part::FeaturePython] Structure161  label="V15x40 V152"  # Arch/BIM 7 (typed FeaturePython)
  FaceMaker = 0
  Height = 400
  HorizontalArea = 471000
  IfcData = attributes={"GlobalId": {"name": "GlobalId", "type": "IfcGloballyUniqueId", "is_enum": false, "enum_values": []}, "Description": {"... (+475 chars omitted),+1 more (map truncated)
  IfcType = 7
  Length = 3140
  MoveBase = false
  MoveWithHost = false
  Nodes = (2) [(-1.72563e-31,-1.42109e-15,-7.77156e-16),(3140,-1.42109e-15,-7.77156e-16)]
  NodesOffset = 0
  Normal = (0,0,0)
  PerimeterLength = 6580
  Placement = pos=(6160,6565,5800) rot=(0,0,-1;1.5708rad)
  PredefinedType = 0
  VerticalArea = 2.632e+06
  Width = 150
FEATURE [Part::FeaturePython] Structure162  label="V15x40 V153"  # Arch/BIM 7 (typed FeaturePython)
  FaceMaker = 0
  Height = 400
  HorizontalArea = 466500
  IfcData = attributes={"GlobalId": {"name": "GlobalId", "type": "IfcGloballyUniqueId", "is_enum": false, "enum_values": []}, "Description": {"... (+475 chars omitted),+1 more (map truncated)
  IfcType = 7
  Length = 3110
  MoveBase = false
  MoveWithHost = false
  Nodes = (2) [(-1.72563e-31,-1.42109e-15,-7.77156e-16),(3110,-1.42109e-15,-7.77156e-16)]
  NodesOffset = 0
  Normal = (0,0,0)
  PerimeterLength = 6520
  Placement = pos=(6160,9825,5800) rot=(0,0,-1;1.5708rad)
  PredefinedType = 0
  VerticalArea = 2.608e+06
  Width = 150
FEATURE [Part::FeaturePython] Structure163  label="V15x40 V154"  # Arch/BIM 7 (typed FeaturePython)
  FaceMaker = 0
  Height = 400
  HorizontalArea = 457500
  IfcData = attributes={"GlobalId": {"name": "GlobalId", "type": "IfcGloballyUniqueId", "is_enum": false, "enum_values": []}, "Description": {"... (+475 chars omitted),+1 more (map truncated)
  IfcType = 7
  Length = 3050
  MoveBase = false
  MoveWithHost = false
  Nodes = (2) [(-1.72563e-31,-1.42109e-15,-7.77156e-16),(3050,-1.42109e-15,-7.77156e-16)]
  NodesOffset = 0
  Normal = (0,0,0)
  PerimeterLength = 6400
  Placement = pos=(9010,3225,5800) rot=(0,0,-1;1.5708rad)
  PredefinedType = 0
  VerticalArea = 2.56e+06
  Width = 150
FEATURE [Part::FeaturePython] Structure164  label="V15x40 V155"  # Arch/BIM 7 (typed FeaturePython)
  FaceMaker = 0
  Height = 400
  HorizontalArea = 456000
  IfcData = attributes={"GlobalId": {"name": "GlobalId", "type": "IfcGloballyUniqueId", "is_enum": false, "enum_values": []}, "Description": {"... (+475 chars omitted),+1 more (map truncated)
  IfcType = 7
  Length = 3040
  MoveBase = false
  MoveWithHost = false
  Nodes = (2) [(-1.72563e-31,-1.42109e-15,-7.77156e-16),(3040,-1.42109e-15,-7.77156e-16)]
  NodesOffset = 0
  Normal = (0,0,0)
  PerimeterLength = 6380
  Placement = pos=(9010,6515,5800) rot=(0,0,-1;1.5708rad)
  PredefinedType = 0
  VerticalArea = 2.552e+06
  Width = 150
FEATURE [Part::FeaturePython] Structure165  label="V15x40 V156"  # Arch/BIM 7 (typed FeaturePython)
  FaceMaker = 0
  Height = 400
  HorizontalArea = 459000
  IfcData = attributes={"GlobalId": {"name": "GlobalId", "type": "IfcGloballyUniqueId", "is_enum": false, "enum_values": []}, "Description": {"... (+475 chars omitted),+1 more (map truncated)
  IfcType = 7
  Length = 3060
  MoveBase = false
  MoveWithHost = false
  Nodes = (2) [(-1.72563e-31,-1.42109e-15,-7.77156e-16),(3060,-1.42109e-15,-7.77156e-16)]
  NodesOffset = 0
  Normal = (0,0,0)
  PerimeterLength = 6420
  Placement = pos=(9010,9825,5800) rot=(0,0,-1;1.5708rad)
  PredefinedType = 0
  VerticalArea = 2.568e+06
  Width = 150
FEATURE [Part::FeaturePython] Structure166  label="V15x40 V157"  # Arch/BIM 7 (typed FeaturePython)
  FaceMaker = 0
  Height = 400
  HorizontalArea = 457500
  IfcData = attributes={"GlobalId": {"name": "GlobalId", "type": "IfcGloballyUniqueId", "is_enum": false, "enum_values": []}, "Description": {"... (+475 chars omitted),+1 more (map truncated)
  IfcType = 7
  Length = 3050
  MoveBase = false
  MoveWithHost = false
  Nodes = (2) [(-1.72563e-31,-1.42109e-15,-7.77156e-16),(3050,-1.42109e-15,-7.77156e-16)]
  NodesOffset = 0
  Normal = (0,0,0)
  PerimeterLength = 6400
  Placement = pos=(10560,3225,5800) rot=(0,0,-1;1.5708rad)
  PredefinedType = 0
  VerticalArea = 2.56e+06
  Width = 150
FEATURE [Part::FeaturePython] Structure167  label="V15x40 V158"  # Arch/BIM 7 (typed FeaturePython)
  FaceMaker = 0
  Height = 400
  HorizontalArea = 363000
  IfcData = attributes={"GlobalId": {"name": "GlobalId", "type": "IfcGloballyUniqueId", "is_enum": false, "enum_values": []}, "Description": {"... (+475 chars omitted),+1 more (map truncated)
  IfcType = 7
  Length = 2420
  MoveBase = false
  MoveWithHost = false
  Nodes = (2) [(-1.72563e-31,-1.42109e-15,-7.77156e-16),(2420,-1.42109e-15,-7.77156e-16)]
  NodesOffset = 0
  Normal = (0,0,0)
  PerimeterLength = 5140
  Placement = pos=(10560,3475,5800) rot=(0,0,1;1.5708rad)
  PredefinedType = 0
  VerticalArea = 2056000
  Width = 150
FEATURE [Part::FeaturePython] Structure168  label="V15x40 V159"  # Arch/BIM 7 (typed FeaturePython)
  FaceMaker = 0
  Height = 400
  HorizontalArea = 207000
  IfcData = attributes={"GlobalId": {"name": "GlobalId", "type": "IfcGloballyUniqueId", "is_enum": false, "enum_values": []}, "Description": {"... (+475 chars omitted),+1 more (map truncated)
  IfcType = 7
  Length = 1380
  MoveBase = false
  MoveWithHost = false
  Nodes = (2) [(-1.72563e-31,-1.42109e-15,-7.77156e-16),(1380,-1.42109e-15,-7.77156e-16)]
  NodesOffset = 0
  Normal = (0,0,0)
  PerimeterLength = 3060
  Placement = pos=(10560,8445,5800) rot=(0,0,1;1.5708rad)
  PredefinedType = 0
  VerticalArea = 1224000
  Width = 150
FEATURE [Part::FeaturePython] Structure169  label="V15x40 V160"  # Arch/BIM 7 (typed FeaturePython)
  FaceMaker = 0
  Height = 400
  HorizontalArea = 207000
  IfcData = attributes={"GlobalId": {"name": "GlobalId", "type": "IfcGloballyUniqueId", "is_enum": false, "enum_values": []}, "Description": {"... (+475 chars omitted),+1 more (map truncated)
  IfcType = 7
  Length = 1380
  MoveBase = false
  MoveWithHost = false
  Nodes = (2) [(-1.72563e-31,-1.42109e-15,-7.77156e-16),(1380,-1.42109e-15,-7.77156e-16)]
  NodesOffset = 0
  Normal = (0,0,0)
  PerimeterLength = 3060
  Placement = pos=(12010,9825,5800) rot=(0,0,-1;1.5708rad)
  PredefinedType = 0
  VerticalArea = 1224000
  Width = 150
FEATURE [Part::FeaturePython] Structure170  label="V20x40 V136"  # Arch/BIM 7 (typed FeaturePython)
  FaceMaker = 0
  Height = 400
  HorizontalArea = 615000
  IfcData = attributes={"GlobalId": {"name": "GlobalId", "type": "IfcGloballyUniqueId", "is_enum": false, "enum_values": []}, "Description": {"... (+475 chars omitted),+1 more (map truncated)
  IfcType = 7
  Length = 3075
  MoveBase = false
  MoveWithHost = false
  Nodes = (2) [(-1.72563e-31,0,-7.77156e-16),(3075,0,-7.77156e-16)]
  NodesOffset = 0
  Normal = (0,0,0)
  PerimeterLength = 6550
  Placement = pos=(1930,3250,5800) rot=(0,0,-1;1.5708rad)
  PredefinedType = 0
  VerticalArea = 2.62e+06
  Width = 200
FEATURE [Part::FeaturePython] Structure171  label="V20x40 V137"  # Arch/BIM 7 (typed FeaturePython)
  FaceMaker = 0
  Height = 400
  HorizontalArea = 618000
  IfcData = attributes={"GlobalId": {"name": "GlobalId", "type": "IfcGloballyUniqueId", "is_enum": false, "enum_values": []}, "Description": {"... (+475 chars omitted),+1 more (map truncated)
  IfcType = 7
  Length = 3090
  MoveBase = false
  MoveWithHost = false
  Nodes = (2) [(-1.72563e-31,0,-7.77156e-16),(3090,0,-7.77156e-16)]
  NodesOffset = 0
  Normal = (0,0,0)
  PerimeterLength = 6580
  Placement = pos=(1930,6540,5800) rot=(0,0,-1;1.5708rad)
  PredefinedType = 0
  VerticalArea = 2.632e+06
  Width = 200
FEATURE [Part::FeaturePython] Structure172  label="V20x40 V138"  # Arch/BIM 7 (typed FeaturePython)
  FaceMaker = 0
  Height = 400
  HorizontalArea = 617000
  IfcData = attributes={"GlobalId": {"name": "GlobalId", "type": "IfcGloballyUniqueId", "is_enum": false, "enum_values": []}, "Description": {"... (+475 chars omitted),+1 more (map truncated)
  IfcType = 7
  Length = 3085
  MoveBase = false
  MoveWithHost = false
  Nodes = (2) [(-1.72563e-31,0,-7.77156e-16),(3085,0,-7.77156e-16)]
  NodesOffset = 0
  Normal = (0,0,0)
  PerimeterLength = 6570
  Placement = pos=(1930,9825,5800) rot=(0,0,-1;1.5708rad)
  PredefinedType = 0
  VerticalArea = 2.628e+06
  Width = 200
FEATURE [Part::FeaturePython] Structure173  label="V20x40 V139"  # Arch/BIM 7 (typed FeaturePython)
  FaceMaker = 0
  Height = 400
  HorizontalArea = 635000
  IfcData = attributes={"GlobalId": {"name": "GlobalId", "type": "IfcGloballyUniqueId", "is_enum": false, "enum_values": []}, "Description": {"... (+475 chars omitted),+1 more (map truncated)
  IfcType = 7
  Length = 3175
  MoveBase = false
  MoveWithHost = false
  Nodes = (2) [(-1.72563e-31,0,-7.77156e-16),(3175,0,-7.77156e-16)]
  NodesOffset = 0
  Normal = (0,0,0)
  PerimeterLength = 6750
  Placement = pos=(13780,175,5800) rot=(0,0,1;1.5708rad)
  PredefinedType = 0
  VerticalArea = 2.7e+06
  Width = 200
FEATURE [Part::FeaturePython] Structure174  label="V20x40 V140"  # Arch/BIM 7 (typed FeaturePython)
  FaceMaker = 0
  Height = 400
  HorizontalArea = 509000
  IfcData = attributes={"GlobalId": {"name": "GlobalId", "type": "IfcGloballyUniqueId", "is_enum": false, "enum_values": []}, "Description": {"... (+475 chars omitted),+1 more (map truncated)
  IfcType = 7
  Length = 2545
  MoveBase = false
  MoveWithHost = false
  Nodes = (2) [(-1.72563e-31,0,-7.77156e-16),(2545,0,-7.77156e-16)]
  NodesOffset = 0
  Normal = (0,0,0)
  PerimeterLength = 5490
  Placement = pos=(13780,3350,5800) rot=(0,0,1;1.5708rad)
  PredefinedType = 0
  VerticalArea = 2196000
  Width = 200
FEATURE [Part::FeaturePython] Structure175  label="V20x40 V141"  # Arch/BIM 7 (typed FeaturePython)
  FaceMaker = 0
  Height = 400
  HorizontalArea = 756000
  IfcData = attributes={"GlobalId": {"name": "GlobalId", "type": "IfcGloballyUniqueId", "is_enum": false, "enum_values": []}, "Description": {"... (+475 chars omitted),+1 more (map truncated)
  IfcType = 7
  Length = 3780
  MoveBase = false
  MoveWithHost = false
  Nodes = (2) [(-1.72563e-31,0,-7.77156e-16),(3780,0,-7.77156e-16)]
  NodesOffset = 0
  Normal = (0,0,0)
  PerimeterLength = 7960
  Placement = pos=(15210,6045,5800) rot=(0,0,1;1.5708rad)
  PredefinedType = 0
  VerticalArea = 3.184e+06
  Width = 200
FEATURE [Part::FeaturePython] Structure176  label="25x15 C026"  # Arch/BIM 24 (typed FeaturePython)
  FaceMaker = 0
  Height = 3000
  HorizontalArea = 37500
  IfcData = attributes={"GlobalId": {"name": "GlobalId", "type": "IfcGloballyUniqueId", "is_enum": false, "enum_values": []}, "Description": {"... (+438 chars omitted),+1 more (map truncated)
  IfcType = 24
  Length = 250
  MoveBase = false
  MoveWithHost = false
  Nodes = (2) [(-1.05471e-15,1.36424e-15,0),(-1.05471e-15,1.36424e-15,3000)]
  NodesOffset = 0
  Normal = (0,0,0)
  PerimeterLength = 800
  Placement = pos=(1930,9900,3000) rot=(0,0,1;0rad)
  PredefinedType = 0
  VerticalArea = 2400000
  Width = 150
FEATURE [Part::FeaturePython] Structure177  label="25x15 C027"  # Arch/BIM 172 (typed FeaturePython)
  FaceMaker = 0
  Height = 3000
  HorizontalArea = 37500
  IfcData = attributes={"GlobalId": {"name": "GlobalId", "type": "IfcGloballyUniqueId", "is_enum": false, "enum_values": []}, "Description": {"... (+484 chars omitted),+1 more (map truncated)
  IfcType = 172
  Length = 250
  MoveBase = false
  MoveWithHost = false
  Nodes = (2) [(-1.05471e-15,1.36424e-15,0),(-1.05471e-15,1.36424e-15,3000)]
  NodesOffset = 0
  Normal = (0,0,0)
  PerimeterLength = 800
  Placement = pos=(1930,100,3000) rot=(0,0,1;0rad)
  PredefinedType = 0
  VerticalArea = 2400000
  Width = 150
FEATURE [Part::FeaturePython] Structure178  label="25x20 C008"  # Arch/BIM 24 (typed FeaturePython)
  FaceMaker = 0
  Height = 3000
  HorizontalArea = 50000
  IfcData = attributes={"GlobalId": {"name": "GlobalId", "type": "IfcGloballyUniqueId", "is_enum": false, "enum_values": []}, "Description": {"... (+438 chars omitted),+1 more (map truncated)
  IfcType = 24
  Length = 250
  MoveBase = false
  MoveWithHost = false
  Nodes = (2) [(-1.05471e-15,-1.81899e-15,0),(-1.05471e-15,-1.81899e-15,3000)]
  NodesOffset = 0
  Normal = (0,0,0)
  PerimeterLength = 900
  Placement = pos=(1930,6640,3000) rot=(0,0,1;0rad)
  PredefinedType = 0
  VerticalArea = 2700000
  Width = 200
FEATURE [Part::FeaturePython] Structure180  label="25x15 C028"  # Arch/BIM 24 (typed FeaturePython)
  FaceMaker = 0
  Height = 3000
  HorizontalArea = 37500
  IfcData = attributes={"GlobalId": {"name": "GlobalId", "type": "IfcGloballyUniqueId", "is_enum": false, "enum_values": []}, "Description": {"... (+438 chars omitted),+1 more (map truncated)
  IfcType = 24
  Length = 250
  MoveBase = false
  MoveWithHost = false
  Nodes = (2) [(-1.05471e-15,1.36424e-15,0),(-1.05471e-15,1.36424e-15,3000)]
  NodesOffset = 0
  Normal = (0,0,0)
  PerimeterLength = 800
  Placement = pos=(6160,6640,3000) rot=(0,0,1;0rad)
  PredefinedType = 0
  VerticalArea = 2400000
  Width = 150
FEATURE [Part::FeaturePython] Structure181  label="25x15 C029"  # Arch/BIM 24 (typed FeaturePython)
  FaceMaker = 0
  Height = 3000
  HorizontalArea = 37500
  IfcData = attributes={"GlobalId": {"name": "GlobalId", "type": "IfcGloballyUniqueId", "is_enum": false, "enum_values": []}, "Description": {"... (+438 chars omitted),+1 more (map truncated)
  IfcType = 24
  Length = 250
  MoveBase = false
  MoveWithHost = false
  Nodes = (2) [(-1.05471e-15,1.36424e-15,0),(-1.05471e-15,1.36424e-15,3000)]
  NodesOffset = 0
  Normal = (0,0,0)
  PerimeterLength = 800
  Placement = pos=(6160,3350,3000) rot=(0,0,1;0rad)
  PredefinedType = 0
  VerticalArea = 2400000
  Width = 150
FEATURE [Part::FeaturePython] Structure182  label="25x15 C030"  # Arch/BIM 24 (typed FeaturePython)
  FaceMaker = 0
  Height = 3000
  HorizontalArea = 37500
  IfcData = attributes={"GlobalId": {"name": "GlobalId", "type": "IfcGloballyUniqueId", "is_enum": false, "enum_values": []}, "Description": {"... (+438 chars omitted),+1 more (map truncated)
  IfcType = 24
  Length = 250
  MoveBase = false
  MoveWithHost = false
  Nodes = (2) [(-1.05471e-15,1.36424e-15,0),(-1.05471e-15,1.36424e-15,3000)]
  NodesOffset = 0
  Normal = (0,0,0)
  PerimeterLength = 800
  Placement = pos=(6160,100,3000) rot=(0,0,1;0rad)
  PredefinedType = 0
  VerticalArea = 2400000
  Width = 150
FEATURE [Part::FeaturePython] Structure183  label="25x15 C031"  # Arch/BIM 24 (typed FeaturePython)
  FaceMaker = 0
  Height = 3000
  HorizontalArea = 37500
  IfcData = attributes={"GlobalId": {"name": "GlobalId", "type": "IfcGloballyUniqueId", "is_enum": false, "enum_values": []}, "Description": {"... (+438 chars omitted),+1 more (map truncated)
  IfcType = 24
  Length = 250
  MoveBase = false
  MoveWithHost = false
  Nodes = (2) [(-1.05471e-15,1.36424e-15,0),(-1.05471e-15,1.36424e-15,3000)]
  NodesOffset = 0
  Normal = (0,0,0)
  PerimeterLength = 800
  Placement = pos=(9010,100,3000) rot=(0,0,1;0rad)
  PredefinedType = 0
  VerticalArea = 2400000
  Width = 150
FEATURE [Part::FeaturePython] Structure184  label="25x15 C032"  # Arch/BIM 24 (typed FeaturePython)
  FaceMaker = 0
  Height = 3000
  HorizontalArea = 37500
  IfcData = attributes={"GlobalId": {"name": "GlobalId", "type": "IfcGloballyUniqueId", "is_enum": false, "enum_values": []}, "Description": {"... (+438 chars omitted),+1 more (map truncated)
  IfcType = 24
  Length = 250
  MoveBase = false
  MoveWithHost = false
  Nodes = (2) [(-1.05471e-15,1.36424e-15,0),(-1.05471e-15,1.36424e-15,3000)]
  NodesOffset = 0
  Normal = (0,0,0)
  PerimeterLength = 800
  Placement = pos=(10560,100,3000) rot=(0,0,1;0rad)
  PredefinedType = 0
  VerticalArea = 2400000
  Width = 150
FEATURE [Part::FeaturePython] Structure185  label="25x15 C033"  # Arch/BIM 24 (typed FeaturePython)
  FaceMaker = 0
  Height = 3000
  HorizontalArea = 37500
  IfcData = attributes={"GlobalId": {"name": "GlobalId", "type": "IfcGloballyUniqueId", "is_enum": false, "enum_values": []}, "Description": {"... (+438 chars omitted),+1 more (map truncated)
  IfcType = 24
  Length = 250
  MoveBase = false
  MoveWithHost = false
  Nodes = (2) [(-1.05471e-15,1.36424e-15,0),(-1.05471e-15,1.36424e-15,3000)]
  NodesOffset = 0
  Normal = (0,0,0)
  PerimeterLength = 800
  Placement = pos=(13780,100,3000) rot=(0,0,1;0rad)
  PredefinedType = 0
  VerticalArea = 2400000
  Width = 150
FEATURE [Part::FeaturePython] Structure186  label="25x15 C034"  # Arch/BIM 24 (typed FeaturePython)
  FaceMaker = 0
  Height = 3000
  HorizontalArea = 37500
  IfcData = attributes={"GlobalId": {"name": "GlobalId", "type": "IfcGloballyUniqueId", "is_enum": false, "enum_values": []}, "Description": {"... (+438 chars omitted),+1 more (map truncated)
  IfcType = 24
  Length = 250
  MoveBase = false
  MoveWithHost = false
  Nodes = (2) [(-1.05471e-15,1.36424e-15,0),(-1.05471e-15,1.36424e-15,3000)]
  NodesOffset = 0
  Normal = (0,0,0)
  PerimeterLength = 800
  Placement = pos=(15210,5970,3000) rot=(0,0,1;0rad)
  PredefinedType = 0
  VerticalArea = 2400000
  Width = 150
FEATURE [Part::FeaturePython] Structure187  label="25x15 C035"  # Arch/BIM 24 (typed FeaturePython)
  FaceMaker = 0
  Height = 3000
  HorizontalArea = 37500
  IfcData = attributes={"GlobalId": {"name": "GlobalId", "type": "IfcGloballyUniqueId", "is_enum": false, "enum_values": []}, "Description": {"... (+438 chars omitted),+1 more (map truncated)
  IfcType = 24
  Length = 250
  MoveBase = false
  MoveWithHost = false
  Nodes = (2) [(-1.05471e-15,1.36424e-15,0),(-1.05471e-15,1.36424e-15,3000)]
  NodesOffset = 0
  Normal = (0,0,0)
  PerimeterLength = 800
  Placement = pos=(13780,5970,3000) rot=(0,0,1;0rad)
  PredefinedType = 0
  VerticalArea = 2400000
  Width = 150
FEATURE [Part::FeaturePython] Structure188  label="25x15 C036"  # Arch/BIM 172 (typed FeaturePython)
  FaceMaker = 0
  Height = 3000
  HorizontalArea = 37500
  IfcData = attributes={"GlobalId": {"name": "GlobalId", "type": "IfcGloballyUniqueId", "is_enum": false, "enum_values": []}, "Description": {"... (+484 chars omitted),+1 more (map truncated)
  IfcType = 172
  Length = 250
  MoveBase = false
  MoveWithHost = false
  Nodes = (2) [(-1.05471e-15,1.36424e-15,0),(-1.05471e-15,1.36424e-15,3000)]
  NodesOffset = 0
  Normal = (0,0,0)
  PerimeterLength = 800
  Placement = pos=(1930,9900,3000) rot=(0,0,1;0rad)
  PredefinedType = 0
  VerticalArea = 2400000
  Width = 150
FEATURE [Part::FeaturePython] Structure189  label="25x15 C037"  # Arch/BIM 172 (typed FeaturePython)
  FaceMaker = 0
  Height = 3000
  HorizontalArea = 37500
  IfcData = attributes={"GlobalId": {"name": "GlobalId", "type": "IfcGloballyUniqueId", "is_enum": false, "enum_values": []}, "Description": {"... (+484 chars omitted),+1 more (map truncated)
  IfcType = 172
  Length = 250
  MoveBase = false
  MoveWithHost = false
  Nodes = (2) [(-1.05471e-15,1.36424e-15,0),(-1.05471e-15,1.36424e-15,3000)]
  NodesOffset = 0
  Normal = (0,0,0)
  PerimeterLength = 800
  Placement = pos=(9010,6640,3000) rot=(0,0,1;1.5708rad)
  PredefinedType = 0
  VerticalArea = 2400000
  Width = 150
FEATURE [Part::FeaturePython] Structure190  label="25x15 C038"  # Arch/BIM 172 (typed FeaturePython)
  FaceMaker = 0
  Height = 3000
  HorizontalArea = 37500
  IfcData = attributes={"GlobalId": {"name": "GlobalId", "type": "IfcGloballyUniqueId", "is_enum": false, "enum_values": []}, "Description": {"... (+484 chars omitted),+1 more (map truncated)
  IfcType = 172
  Length = 250
  MoveBase = false
  MoveWithHost = false
  Nodes = (2) [(-1.05471e-15,1.36424e-15,0),(-1.05471e-15,1.36424e-15,3000)]
  NodesOffset = 0
  Normal = (0,0,0)
  PerimeterLength = 800
  Placement = pos=(9010,3350,3000) rot=(0,0,1;1.5708rad)
  PredefinedType = 0
  VerticalArea = 2400000
  Width = 150
FEATURE [Part::FeaturePython] Structure191  label="25x15 C039"  # Arch/BIM 172 (typed FeaturePython)
  FaceMaker = 0
  Height = 3000
  HorizontalArea = 37500
  IfcData = attributes={"GlobalId": {"name": "GlobalId", "type": "IfcGloballyUniqueId", "is_enum": false, "enum_values": []}, "Description": {"... (+484 chars omitted),+1 more (map truncated)
  IfcType = 172
  Length = 250
  MoveBase = false
  MoveWithHost = false
  Nodes = (2) [(-1.05471e-15,1.36424e-15,0),(-1.05471e-15,1.36424e-15,3000)]
  NodesOffset = 0
  Normal = (0,0,0)
  PerimeterLength = 800
  Placement = pos=(10560,3350,3000) rot=(0,0,1;1.5708rad)
  PredefinedType = 0
  VerticalArea = 2400000
  Width = 150
FEATURE [Part::FeaturePython] Structure192  label="25x15 C040"  # Arch/BIM 172 (typed FeaturePython)
  FaceMaker = 0
  Height = 3000
  HorizontalArea = 37500
  IfcData = attributes={"GlobalId": {"name": "GlobalId", "type": "IfcGloballyUniqueId", "is_enum": false, "enum_values": []}, "Description": {"... (+484 chars omitted),+1 more (map truncated)
  IfcType = 172
  Length = 250
  MoveBase = false
  MoveWithHost = false
  Nodes = (2) [(-1.05471e-15,1.36424e-15,0),(-1.05471e-15,1.36424e-15,3000)]
  NodesOffset = 0
  Normal = (0,0,0)
  PerimeterLength = 800
  Placement = pos=(13780,3350,3000) rot=(0,0,1;1.5708rad)
  PredefinedType = 0
  VerticalArea = 2400000
  Width = 150
FEATURE [Part::FeaturePython] Structure193  label="25x15 C041"  # Arch/BIM 172 (typed FeaturePython)
  FaceMaker = 0
  Height = 3000
  HorizontalArea = 37500
  IfcData = attributes={"GlobalId": {"name": "GlobalId", "type": "IfcGloballyUniqueId", "is_enum": false, "enum_values": []}, "Description": {"... (+484 chars omitted),+1 more (map truncated)
  IfcType = 172
  Length = 250
  MoveBase = false
  MoveWithHost = false
  Nodes = (2) [(-1.05471e-15,1.36424e-15,0),(-1.05471e-15,1.36424e-15,3000)]
  NodesOffset = 0
  Normal = (0,0,0)
  PerimeterLength = 800
  Placement = pos=(9010,9900,3000) rot=(0,0,1;0rad)
  PredefinedType = 0
  VerticalArea = 2400000
  Width = 150
FEATURE [Part::FeaturePython] Structure194  label="25x15 C042"  # Arch/BIM 172 (typed FeaturePython)
  FaceMaker = 0
  Height = 3000
  HorizontalArea = 37500
  IfcData = attributes={"GlobalId": {"name": "GlobalId", "type": "IfcGloballyUniqueId", "is_enum": false, "enum_values": []}, "Description": {"... (+484 chars omitted),+1 more (map truncated)
  IfcType = 172
  Length = 250
  MoveBase = false
  MoveWithHost = false
  Nodes = (2) [(-1.05471e-15,1.36424e-15,0),(-1.05471e-15,1.36424e-15,3000)]
  NodesOffset = 0
  Normal = (0,0,0)
  PerimeterLength = 800
  Placement = pos=(6160,9900,3000) rot=(0,0,1;0rad)
  PredefinedType = 0
  VerticalArea = 2400000
  Width = 150
FEATURE [Part::FeaturePython] Structure195  label="25x15 C043"  # Arch/BIM 172 (typed FeaturePython)
  FaceMaker = 0
  Height = 3000
  HorizontalArea = 37500
  IfcData = attributes={"GlobalId": {"name": "GlobalId", "type": "IfcGloballyUniqueId", "is_enum": false, "enum_values": []}, "Description": {"... (+484 chars omitted),+1 more (map truncated)
  IfcType = 172
  Length = 250
  MoveBase = false
  MoveWithHost = false
  Nodes = (2) [(-1.05471e-15,1.36424e-15,0),(-1.05471e-15,1.36424e-15,3000)]
  NodesOffset = 0
  Normal = (0,0,0)
  PerimeterLength = 800
  Placement = pos=(12010,9900,3000) rot=(0,0,1;0rad)
  PredefinedType = 0
  VerticalArea = 2400000
  Width = 150
FEATURE [Part::FeaturePython] Structure196  label="25x15 C044"  # Arch/BIM 172 (typed FeaturePython)
  FaceMaker = 0
  Height = 3000
  HorizontalArea = 37500
  IfcData = attributes={"GlobalId": {"name": "GlobalId", "type": "IfcGloballyUniqueId", "is_enum": false, "enum_values": []}, "Description": {"... (+484 chars omitted),+1 more (map truncated)
  IfcType = 172
  Length = 250
  MoveBase = false
  MoveWithHost = false
  Nodes = (2) [(-1.05471e-15,1.36424e-15,0),(-1.05471e-15,1.36424e-15,3000)]
  NodesOffset = 0
  Normal = (0,0,0)
  PerimeterLength = 800
  Placement = pos=(15210,9900,3000) rot=(0,0,1;0rad)
  PredefinedType = 0
  VerticalArea = 2400000
  Width = 150
FEATURE [Part::FeaturePython] Structure179  label="25x20 C009"  # Arch/BIM 172 (typed FeaturePython)
  FaceMaker = 0
  Height = 3000
  HorizontalArea = 50000
  IfcData = attributes={"GlobalId": {"name": "GlobalId", "type": "IfcGloballyUniqueId", "is_enum": false, "enum_values": []}, "Description": {"... (+484 chars omitted),+1 more (map truncated)
  IfcType = 172
  Length = 250
  MoveBase = false
  MoveWithHost = false
  Nodes = (2) [(-1.05471e-15,-1.81899e-15,0),(-1.05471e-15,-1.81899e-15,3000)]
  NodesOffset = 0
  Normal = (0,0,0)
  PerimeterLength = 900
  Placement = pos=(1930,3350,3000) rot=(0,0,1;0rad)
  PredefinedType = 0
  VerticalArea = 2700000
  Width = 200
FEATURE [App::GeometryPython] BuildingPart012  label="Columnas P1"  # Arch/BIM 172 (typed FeaturePython)
  Area = 0
  Group = -> [Structure176,Structure177,Structure180,Structure181,Structure182,Structure183,Structure184,Structure185,Structure186,Structure187,Structure188,Structure189,Structure190,Structure191,Structure192,Structure193,Structure194,Structure195,Structure196,Structure178,Structure179]
  Height = 0
  HeightPropagate = true
  IfcData = attributes={"GlobalId": {"name": "GlobalId", "type": "IfcGloballyUniqueId", "is_enum": false, "enum_values": []}, "Description": {"... (+484 chars omitted),+1 more (map truncated)
  IfcType = 172
  LevelOffset = 0
  PredefinedType = 0
FEATURE [Part::FeaturePython] Wall002  label="Tabique Ascensor P1"  # Arch/BIM 166 (typed FeaturePython)
  Align = 1
  Area = 24900000
  Base = -> Rectangle003
  BlockHeight = 0
  BlockLength = 0
  CountBroken = 0
  CountEntire = 0
  Face = 0
  Height = 3000
  HorizontalArea = 1155000
  IfcData = attributes={"GlobalId": {"name": "GlobalId", "type": "IfcGloballyUniqueId", "is_enum": false, "enum_values": []}, "Description": {"... (+533 chars omitted),+1 more (map truncated)
  IfcType = 166
  Joint = 0
  Length = 8300
  MakeBlocks = false
  MoveBase = false
  MoveWithHost = false
  Normal = (0,0,0)
  OffsetFirst = 0
  OffsetSecond = 0
  PerimeterLength = 8300
  Placement = pos=(0,0,3000) rot=(0,0,1;0rad)
  PredefinedType = 0
  VerticalArea = 46200000
  Width = 150
FEATURE [Part::Part2DObjectPython] Rectangle004  # Draft 2D object (typed FeaturePython)
  Area = 12611050
  ChamferSize = 0
  Columns = 1
  FilletRadius = 0
  Height = 3110
  Length = 4055
  MakeFace = true
  Placement = pos=(2030,6715,3000) rot=(0,0,1;0rad)
  Rows = 1
FEATURE [Part::Part2DObjectPython] Rectangle005  # Draft 2D object (typed FeaturePython)
  Area = 12732700
  ChamferSize = 0
  Columns = 1
  FilletRadius = 0
  Height = 3140
  Length = 4055
  MakeFace = true
  Placement = pos=(2030,3425,3000) rot=(0,0,1;0rad)
  Rows = 1
FEATURE [Part::Part2DObjectPython] Rectangle006  # Draft 2D object (typed FeaturePython)
  Area = 1.25705e+07
  ChamferSize = 0
  Columns = 1
  FilletRadius = 0
  Height = 3100
  Length = 4055
  MakeFace = true
  Placement = pos=(2030,175,3000) rot=(0,0,1;0rad)
  Rows = 1
FEATURE [Part::Part2DObjectPython] Rectangle008  # Draft 2D object (typed FeaturePython)
  Area = 4354000
  ChamferSize = 0
  Columns = 1
  FilletRadius = 0
  Height = 3110
  Length = 1400
  MakeFace = true
  Placement = pos=(9085,6715,3000) rot=(0,0,1;0rad)
  Rows = 1
FEATURE [Part::Part2DObjectPython] Rectangle009  # Draft 2D object (typed FeaturePython)
  Area = 1.794e+06
  ChamferSize = 0
  Columns = 1
  FilletRadius = 0
  Height = 1380
  Length = 1300
  MakeFace = true
  Placement = pos=(10635,8445,3000) rot=(0,0,1;0rad)
  Rows = 1
FEATURE [Part::Part2DObjectPython] Rectangle011  # Draft 2D object (typed FeaturePython)
  Area = 4396000
  ChamferSize = 0
  Columns = 1
  FilletRadius = 0
  Height = 3140
  Length = 1400
  MakeFace = true
  Placement = pos=(9085,3425,3000) rot=(0,0,1;0rad)
  Rows = 1
FEATURE [Part::Part2DObjectPython] Rectangle013  # Draft 2D object (typed FeaturePython)
  Area = 4.34e+06
  ChamferSize = 0
  Columns = 1
  FilletRadius = 0
  Height = 3100
  Length = 1400
  MakeFace = true
  Placement = pos=(9085,175,3000) rot=(0,0,1;0rad)
  Rows = 1
FEATURE [Part::Part2DObjectPython] Rectangle014  # Draft 2D object (typed FeaturePython)
  Area = 3928500
  ChamferSize = 0
  Columns = 1
  FilletRadius = 0
  Height = 1455
  Length = 2700
  MakeFace = true
  Placement = pos=(6235,8370,3000) rot=(0,0,1;0rad)
  Rows = 1
FEATURE [Part::Part2DObjectPython] Rectangle015  # Draft 2D object (typed FeaturePython)
  Area = 4.0365e+06
  ChamferSize = 0
  Columns = 1
  FilletRadius = 0
  Height = 1495
  Length = 2700
  MakeFace = true
  Placement = pos=(6235,3425,3000) rot=(0,0,1;0rad)
  Rows = 1
FEATURE [Part::Part2DObjectPython] Rectangle016  # Draft 2D object (typed FeaturePython)
  Area = 3.915e+06
  ChamferSize = 0
  Columns = 1
  FilletRadius = 0
  Height = 1450
  Length = 2700
  MakeFace = true
  Placement = pos=(6235,175,3000) rot=(0,0,1;0rad)
  Rows = 1
FEATURE [Part::Part2DObjectPython] Wire  # Draft 2D object (typed FeaturePython)
  Area = 3.9285e+06
  ChamferSize = 0
  Closed = true
  End = (8935,6715,3000)
  FilletRadius = 0
  Length = 8410
  MakeFace = true
  Placement = pos=(6235,6715,3000) rot=(0,0,1;0rad)
  Points = (6) [(0,0,0),(0,1505,0),(2400,1505,0),(2400,1055,0),(2700,1055,0),(2700,9.09495e-13,0)]
  Start = (6235,6715,3000)
  Subdivisions = 0
FEATURE [Part::Part2DObjectPython] Wire001  # Draft 2D object (typed FeaturePython)
  Area = 3.90134e+06
  ChamferSize = 0
  Closed = true
  End = (6235,5070,3000)
  FilletRadius = 0
  Length = 8389.89
  MakeFace = true
  Placement = pos=(6235,6565,3000) rot=(0,0,1;0rad)
  Points = (6) [(0,0,0),(2700,0,0),(2700,-1044.89,0),(2400,-1044.89,0),(2400,-1494.89,0),(0,-1495,0)]
  Start = (6235,6565,3000)
  Subdivisions = 0
FEATURE [Part::Part2DObjectPython] Wire002  # Draft 2D object (typed FeaturePython)
  Area = 3.91484e+06
  ChamferSize = 0
  Closed = true
  End = (6235,1775,3000)
  FilletRadius = 0
  Length = 8399.89
  MakeFace = true
  Placement = pos=(6235,3275,3000) rot=(0,0,1;0rad)
  Points = (6) [(0,0,0),(2700,-4.54747e-13,0),(2700,-1049.89,0),(2400,-1049.89,0),(2400,-1499.89,0),(0,-1500,0)]
  Start = (6235,3275,3000)
  Subdivisions = 0
FEATURE [Part::Part2DObjectPython] Rectangle017  # Draft 2D object (typed FeaturePython)
  Area = 4174500
  ChamferSize = 0
  Columns = 1
  FilletRadius = 0
  Height = 1380
  Length = 3025
  MakeFace = true
  Placement = pos=(12085,8445,3000) rot=(0,0,1;0rad)
  Rows = 1
FEATURE [Part::Part2DObjectPython] Rectangle018  # Draft 2D object (typed FeaturePython)
  Area = 3.211e+06
  ChamferSize = 0
  Columns = 1
  FilletRadius = 0
  Height = 2470
  Length = 1300
  MakeFace = true
  Placement = pos=(10635,3425,3000) rot=(0,0,1;0rad)
  Rows = 1
FEATURE [Part::Part2DObjectPython] Rectangle019  # Draft 2D object (typed FeaturePython)
  Area = 3.93965e+06
  ChamferSize = 0
  Columns = 1
  FilletRadius = 0
  Height = 2470
  Length = 1595
  MakeFace = true
  Placement = pos=(12085,3425,3000) rot=(0,0,1;0rad)
  Rows = 1
FEATURE [Part::Part2DObjectPython] Rectangle020  # Draft 2D object (typed FeaturePython)
  Area = 9439500
  ChamferSize = 0
  Columns = 1
  FilletRadius = 0
  Height = 3100
  Length = 3045
  MakeFace = true
  Placement = pos=(10635,175,3000) rot=(0,0,1;0rad)
  Rows = 1
FEATURE [Part::FeaturePython] Structure219  label="L118"  # Arch/BIM 172 (typed FeaturePython)
  Base = -> Rectangle004
  FaceMaker = 0
  Height = 150
  HorizontalArea = 12611050
  IfcData = attributes={"GlobalId": {"name": "GlobalId", "type": "IfcGloballyUniqueId", "is_enum": false, "enum_values": []}, "Description": {"... (+484 chars omitted),+1 more (map truncated)
  IfcType = 172
  Length = 0
  MoveBase = false
  MoveWithHost = false
  Nodes = (2) [(4057.5,8270,3000),(4057.5,8270,2850)]
  NodesOffset = 0
  Normal = (0,0,-1)
  PerimeterLength = 14330
  Placement = pos=(0,0,3000) rot=(0,0,1;0rad)
  PredefinedType = 0
  VerticalArea = 2149500
  Width = 150
FEATURE [Part::FeaturePython] Structure220  label="L119"  # Arch/BIM 172 (typed FeaturePython)
  Base = -> Rectangle005
  FaceMaker = 0
  Height = 150
  HorizontalArea = 12732700
  IfcData = attributes={"GlobalId": {"name": "GlobalId", "type": "IfcGloballyUniqueId", "is_enum": false, "enum_values": []}, "Description": {"... (+484 chars omitted),+1 more (map truncated)
  IfcType = 172
  Length = 0
  MoveBase = false
  MoveWithHost = false
  Nodes = (2) [(4057.5,4995,3000),(4057.5,4995,2850)]
  NodesOffset = 0
  Normal = (0,0,-1)
  PerimeterLength = 14390
  Placement = pos=(0,0,3000) rot=(0,0,1;0rad)
  PredefinedType = 0
  VerticalArea = 2158500
  Width = 150
FEATURE [Part::FeaturePython] Structure221  label="L120"  # Arch/BIM 172 (typed FeaturePython)
  Base = -> Rectangle006
  FaceMaker = 0
  Height = 150
  HorizontalArea = 1.25705e+07
  IfcData = attributes={"GlobalId": {"name": "GlobalId", "type": "IfcGloballyUniqueId", "is_enum": false, "enum_values": []}, "Description": {"... (+484 chars omitted),+1 more (map truncated)
  IfcType = 172
  Length = 0
  MoveBase = false
  MoveWithHost = false
  Nodes = (2) [(4057.5,1725,3000),(4057.5,1725,2850)]
  NodesOffset = 0
  Normal = (0,0,-1)
  PerimeterLength = 14310
  Placement = pos=(0,0,3000) rot=(0,0,1;0rad)
  PredefinedType = 0
  VerticalArea = 2146500
  Width = 150
FEATURE [Part::FeaturePython] Structure222  label="V15x40 V102a001"  # Arch/BIM 7 (typed FeaturePython)
  FaceMaker = 0
  Height = 400
  HorizontalArea = 405000
  IfcData = attributes={"GlobalId": {"name": "GlobalId", "type": "IfcGloballyUniqueId", "is_enum": false, "enum_values": []}, "Description": {"... (+475 chars omitted),+1 more (map truncated)
  IfcType = 7
  Length = 2700
  MoveBase = false
  MoveWithHost = false
  Nodes = (2) [(-1.72563e-31,-1.42109e-15,-7.77156e-16),(2700,-1.42109e-15,-7.77156e-16)]
  NodesOffset = 0
  Normal = (0,0,0)
  PerimeterLength = 5700
  Placement = pos=(8935,8295,5800) rot=(0,0,1;3.14159rad)
  PredefinedType = 0
  VerticalArea = 2.28e+06
  Width = 150
FEATURE [Part::FeaturePython] Structure223  label="V15x40 V107a001"  # Arch/BIM 7 (typed FeaturePython)
  FaceMaker = 0
  Height = 400
  HorizontalArea = 405000
  IfcData = attributes={"GlobalId": {"name": "GlobalId", "type": "IfcGloballyUniqueId", "is_enum": false, "enum_values": []}, "Description": {"... (+475 chars omitted),+1 more (map truncated)
  IfcType = 7
  Length = 2700
  MoveBase = false
  MoveWithHost = false
  Nodes = (2) [(-1.72563e-31,-1.42109e-15,-7.77156e-16),(2700,-1.42109e-15,-7.77156e-16)]
  NodesOffset = 0
  Normal = (0,0,0)
  PerimeterLength = 5700
  Placement = pos=(8935,4995,5800) rot=(0,0,1;3.14159rad)
  PredefinedType = 0
  VerticalArea = 2.28e+06
  Width = 150
FEATURE [Part::FeaturePython] Structure224  label="V15x40 V112a001"  # Arch/BIM 7 (typed FeaturePython)
  FaceMaker = 0
  Height = 400
  HorizontalArea = 405000
  IfcData = attributes={"GlobalId": {"name": "GlobalId", "type": "IfcGloballyUniqueId", "is_enum": false, "enum_values": []}, "Description": {"... (+475 chars omitted),+1 more (map truncated)
  IfcType = 7
  Length = 2700
  MoveBase = false
  MoveWithHost = false
  Nodes = (2) [(-1.72563e-31,-1.42109e-15,-7.77156e-16),(2700,-1.42109e-15,-7.77156e-16)]
  NodesOffset = 0
  Normal = (0,0,0)
  PerimeterLength = 5700
  Placement = pos=(8935,1700,5800) rot=(0,0,1;3.14159rad)
  PredefinedType = 0
  VerticalArea = 2.28e+06
  Width = 150
FEATURE [Part::FeaturePython] Structure225  label="V15x40 V130a001"  # Arch/BIM 7 (typed FeaturePython)
  FaceMaker = 0
  Height = 400
  HorizontalArea = 370500
  IfcData = attributes={"GlobalId": {"name": "GlobalId", "type": "IfcGloballyUniqueId", "is_enum": false, "enum_values": []}, "Description": {"... (+475 chars omitted),+1 more (map truncated)
  IfcType = 7
  Length = 2470
  MoveBase = false
  MoveWithHost = false
  Nodes = (2) [(-1.72563e-31,-1.42109e-15,-7.77156e-16),(2470,-1.42109e-15,-7.77156e-16)]
  NodesOffset = 0
  Normal = (0,0,0)
  PerimeterLength = 5240
  Placement = pos=(12010,3425,5800) rot=(0,0,1;1.5708rad)
  PredefinedType = 0
  VerticalArea = 2096000
  Width = 150
FEATURE [App::GeometryPython] BuildingPart011  label="Vigas sobre P1"  # Arch/BIM 172 (typed FeaturePython)
  Area = 0
  Group = -> [Structure222,Structure223,Structure224,Structure225,Structure142,Structure143,Structure144,Structure145,Structure146,Structure147,Structure148,Structure149,Structure150,Structure151,Structure152,Structure153,Structure154,Structure155,Structure156,Structure157,Structure158,Structure159,Structure160,Structure161,Structure162,Structure163,Structure164,Structure165,Structure166,Structure167,+8 more]
  Height = 0
  HeightPropagate = true
  IfcData = attributes={"GlobalId": {"name": "GlobalId", "type": "IfcGloballyUniqueId", "is_enum": false, "enum_values": []}, "Description": {"... (+484 chars omitted),+1 more (map truncated)
  IfcType = 172
  LevelOffset = 0
  PredefinedType = 0
FEATURE [Part::FeaturePython] Structure226  label="L121"  # Arch/BIM 172 (typed FeaturePython)
  Base = -> Rectangle014
  FaceMaker = 0
  Height = 150
  HorizontalArea = 3928500
  IfcData = attributes={"GlobalId": {"name": "GlobalId", "type": "IfcGloballyUniqueId", "is_enum": false, "enum_values": []}, "Description": {"... (+484 chars omitted),+1 more (map truncated)
  IfcType = 172
  Length = 0
  MoveBase = false
  MoveWithHost = false
  Nodes = (2) [(7585,9097.5,3000),(7585,9097.5,2850)]
  NodesOffset = 0
  Normal = (0,0,-1)
  PerimeterLength = 8310
  Placement = pos=(0,0,3000) rot=(0,0,1;0rad)
  PredefinedType = 0
  VerticalArea = 1246500
  Width = 150
FEATURE [Part::FeaturePython] Structure227  label="L122"  # Arch/BIM 172 (typed FeaturePython)
  Base = -> Wire
  FaceMaker = 0
  Height = 150
  HorizontalArea = 3.9285e+06
  IfcData = attributes={"GlobalId": {"name": "GlobalId", "type": "IfcGloballyUniqueId", "is_enum": false, "enum_values": []}, "Description": {"... (+484 chars omitted),+1 more (map truncated)
  IfcType = 172
  Length = 0
  MoveBase = false
  MoveWithHost = false
  Nodes = (2) [(7543.76,7449.37,3000),(7543.76,7449.37,2850)]
  NodesOffset = 0
  Normal = (0,0,-1)
  PerimeterLength = 8410
  Placement = pos=(0,0,2850) rot=(0,0,1;0rad)
  PredefinedType = 0
  VerticalArea = 1261500
  Width = 150
FEATURE [Part::FeaturePython] Structure228  label="L123"  # Arch/BIM 172 (typed FeaturePython)
  Base = -> Wire001
  FaceMaker = 0
  Height = 150
  HorizontalArea = 3.90134e+06
  IfcData = attributes={"GlobalId": {"name": "GlobalId", "type": "IfcGloballyUniqueId", "is_enum": false, "enum_values": []}, "Description": {"... (+484 chars omitted),+1 more (map truncated)
  IfcType = 172
  Length = 0
  MoveBase = false
  MoveWithHost = false
  Nodes = (2) [(7543.46,5835.61,3000),(7543.46,5835.61,2850)]
  NodesOffset = 0
  Normal = (0,0,-1)
  PerimeterLength = 8389.89
  Placement = pos=(0,0,2850) rot=(0,0,1;0rad)
  PredefinedType = 0
  VerticalArea = 1.25848e+06
  Width = 150
FEATURE [Part::FeaturePython] Structure229  label="L124"  # Arch/BIM 172 (typed FeaturePython)
  Base = -> Rectangle015
  FaceMaker = 0
  Height = 150
  HorizontalArea = 4.0365e+06
  IfcData = attributes={"GlobalId": {"name": "GlobalId", "type": "IfcGloballyUniqueId", "is_enum": false, "enum_values": []}, "Description": {"... (+484 chars omitted),+1 more (map truncated)
  IfcType = 172
  Length = 0
  MoveBase = false
  MoveWithHost = false
  Nodes = (2) [(7585,4172.5,3000),(7585,4172.5,2850)]
  NodesOffset = 0
  Normal = (0,0,-1)
  PerimeterLength = 8390
  Placement = pos=(0,0,3000) rot=(0,0,1;0rad)
  PredefinedType = 0
  VerticalArea = 1258500
  Width = 150
FEATURE [Part::FeaturePython] Structure230  label="L125"  # Arch/BIM 172 (typed FeaturePython)
  Base = -> Wire002
  FaceMaker = 0
  Height = 150
  HorizontalArea = 3.91484e+06
  IfcData = attributes={"GlobalId": {"name": "GlobalId", "type": "IfcGloballyUniqueId", "is_enum": false, "enum_values": []}, "Description": {"... (+484 chars omitted),+1 more (map truncated)
  IfcType = 172
  Length = 0
  MoveBase = false
  MoveWithHost = false
  Nodes = (2) [(7543.6,2543.13,3000),(7543.6,2543.13,2850)]
  NodesOffset = 0
  Normal = (0,0,-1)
  PerimeterLength = 8399.89
  Placement = pos=(0,0,2850) rot=(0,0,1;0rad)
  PredefinedType = 0
  VerticalArea = 1.25998e+06
  Width = 150
FEATURE [Part::FeaturePython] Structure231  label="L126"  # Arch/BIM 172 (typed FeaturePython)
  Base = -> Rectangle016
  FaceMaker = 0
  Height = 150
  HorizontalArea = 3.915e+06
  IfcData = attributes={"GlobalId": {"name": "GlobalId", "type": "IfcGloballyUniqueId", "is_enum": false, "enum_values": []}, "Description": {"... (+484 chars omitted),+1 more (map truncated)
  IfcType = 172
  Length = 0
  MoveBase = false
  MoveWithHost = false
  Nodes = (2) [(7585,900,3000),(7585,900,2850)]
  NodesOffset = 0
  Normal = (0,0,-1)
  PerimeterLength = 8300
  Placement = pos=(0,0,3000) rot=(0,0,1;0rad)
  PredefinedType = 0
  VerticalArea = 1.245e+06
  Width = 150
FEATURE [Part::FeaturePython] Structure232  label="L127"  # Arch/BIM 172 (typed FeaturePython)
  Base = -> Rectangle008
  FaceMaker = 0
  Height = 150
  HorizontalArea = 4354000
  IfcData = attributes={"GlobalId": {"name": "GlobalId", "type": "IfcGloballyUniqueId", "is_enum": false, "enum_values": []}, "Description": {"... (+484 chars omitted),+1 more (map truncated)
  IfcType = 172
  Length = 0
  MoveBase = false
  MoveWithHost = false
  Nodes = (2) [(9785,8270,3000),(9785,8270,2850)]
  NodesOffset = 0
  Normal = (0,0,-1)
  PerimeterLength = 9020
  Placement = pos=(0,0,3000) rot=(0,0,1;0rad)
  PredefinedType = 0
  VerticalArea = 1353000
  Width = 150
FEATURE [Part::FeaturePython] Structure233  label="L128"  # Arch/BIM 172 (typed FeaturePython)
  Base = -> Rectangle011
  FaceMaker = 0
  Height = 150
  HorizontalArea = 4396000
  IfcData = attributes={"GlobalId": {"name": "GlobalId", "type": "IfcGloballyUniqueId", "is_enum": false, "enum_values": []}, "Description": {"... (+484 chars omitted),+1 more (map truncated)
  IfcType = 172
  Length = 0
  MoveBase = false
  MoveWithHost = false
  Nodes = (2) [(9785,4995,3000),(9785,4995,2850)]
  NodesOffset = 0
  Normal = (0,0,-1)
  PerimeterLength = 9080
  Placement = pos=(0,0,3000) rot=(0,0,1;0rad)
  PredefinedType = 0
  VerticalArea = 1362000
  Width = 150
FEATURE [Part::FeaturePython] Structure234  label="L129"  # Arch/BIM 172 (typed FeaturePython)
  Base = -> Rectangle013
  FaceMaker = 0
  Height = 150
  HorizontalArea = 4.34e+06
  IfcData = attributes={"GlobalId": {"name": "GlobalId", "type": "IfcGloballyUniqueId", "is_enum": false, "enum_values": []}, "Description": {"... (+484 chars omitted),+1 more (map truncated)
  IfcType = 172
  Length = 0
  MoveBase = false
  MoveWithHost = false
  Nodes = (2) [(9785,1725,3000),(9785,1725,2850)]
  NodesOffset = 0
  Normal = (0,0,-1)
  PerimeterLength = 9000
  Placement = pos=(0,0,3000) rot=(0,0,1;0rad)
  PredefinedType = 0
  VerticalArea = 1350000
  Width = 150
FEATURE [Part::FeaturePython] Structure235  label="L130"  # Arch/BIM 172 (typed FeaturePython)
  Base = -> Rectangle009
  FaceMaker = 0
  Height = 150
  HorizontalArea = 1.794e+06
  IfcData = attributes={"GlobalId": {"name": "GlobalId", "type": "IfcGloballyUniqueId", "is_enum": false, "enum_values": []}, "Description": {"... (+484 chars omitted),+1 more (map truncated)
  IfcType = 172
  Length = 0
  MoveBase = false
  MoveWithHost = false
  Nodes = (2) [(11285,9135,3000),(11285,9135,2850)]
  NodesOffset = 0
  Normal = (0,0,-1)
  PerimeterLength = 5360
  Placement = pos=(0,0,3000) rot=(0,0,1;0rad)
  PredefinedType = 0
  VerticalArea = 804000
  Width = 150
FEATURE [Part::FeaturePython] Structure236  label="L131"  # Arch/BIM 172 (typed FeaturePython)
  Base = -> Rectangle018
  FaceMaker = 0
  Height = 150
  HorizontalArea = 3.211e+06
  IfcData = attributes={"GlobalId": {"name": "GlobalId", "type": "IfcGloballyUniqueId", "is_enum": false, "enum_values": []}, "Description": {"... (+484 chars omitted),+1 more (map truncated)
  IfcType = 172
  Length = 0
  MoveBase = false
  MoveWithHost = false
  Nodes = (2) [(11285,4660,3000),(11285,4660,2850)]
  NodesOffset = 0
  Normal = (0,0,-1)
  PerimeterLength = 7540
  Placement = pos=(0,0,3000) rot=(0,0,1;0rad)
  PredefinedType = 0
  VerticalArea = 1.131e+06
  Width = 150
FEATURE [Part::FeaturePython] Structure237  label="L132"  # Arch/BIM 172 (typed FeaturePython)
  Base = -> Rectangle020
  FaceMaker = 0
  Height = 150
  HorizontalArea = 9439500
  IfcData = attributes={"GlobalId": {"name": "GlobalId", "type": "IfcGloballyUniqueId", "is_enum": false, "enum_values": []}, "Description": {"... (+484 chars omitted),+1 more (map truncated)
  IfcType = 172
  Length = 0
  MoveBase = false
  MoveWithHost = false
  Nodes = (2) [(12157.5,1725,3000),(12157.5,1725,2850)]
  NodesOffset = 0
  Normal = (0,0,-1)
  PerimeterLength = 12290
  Placement = pos=(0,0,3000) rot=(0,0,1;0rad)
  PredefinedType = 0
  VerticalArea = 1843500
  Width = 150
FEATURE [Part::FeaturePython] Structure238  label="L133"  # Arch/BIM 172 (typed FeaturePython)
  Base = -> Rectangle019
  FaceMaker = 0
  Height = 150
  HorizontalArea = 3.93965e+06
  IfcData = attributes={"GlobalId": {"name": "GlobalId", "type": "IfcGloballyUniqueId", "is_enum": false, "enum_values": []}, "Description": {"... (+484 chars omitted),+1 more (map truncated)
  IfcType = 172
  Length = 0
  MoveBase = false
  MoveWithHost = false
  Nodes = (2) [(12882.5,4660,3000),(12882.5,4660,2850)]
  NodesOffset = 0
  Normal = (0,0,-1)
  PerimeterLength = 8130
  Placement = pos=(0,0,2850) rot=(0,0,1;0rad)
  PredefinedType = 0
  VerticalArea = 1.2195e+06
  Width = 150
FEATURE [Part::FeaturePython] Structure239  label="L134"  # Arch/BIM 172 (typed FeaturePython)
  Base = -> Rectangle017
  FaceMaker = 0
  Height = 150
  HorizontalArea = 4174500
  IfcData = attributes={"GlobalId": {"name": "GlobalId", "type": "IfcGloballyUniqueId", "is_enum": false, "enum_values": []}, "Description": {"... (+484 chars omitted),+1 more (map truncated)
  IfcType = 172
  Length = 0
  MoveBase = false
  MoveWithHost = false
  Nodes = (2) [(13597.5,9135,3000),(13597.5,9135,2850)]
  NodesOffset = 0
  Normal = (0,0,-1)
  PerimeterLength = 8810
  Placement = pos=(0,0,3000) rot=(0,0,1;0rad)
  PredefinedType = 0
  VerticalArea = 1321500
  Width = 150
FEATURE [App::GeometryPython] BuildingPart015  label="Losas sobre P1"  # Arch/BIM 172 (typed FeaturePython)
  Area = 0
  Group = -> [Structure219,Structure220,Structure221,Structure226,Structure227,Structure228,Structure229,Structure230,Structure231,Structure232,Structure233,Structure234,Structure235,Structure236,Structure237,Structure238,Structure239]
  Height = 0
  HeightPropagate = true
  IfcData = attributes={"GlobalId": {"name": "GlobalId", "type": "IfcGloballyUniqueId", "is_enum": false, "enum_values": []}, "Description": {"... (+484 chars omitted),+1 more (map truncated)
  IfcType = 172
  LevelOffset = 0
  PredefinedType = 0
FEATURE [App::GeometryPython] BuildingPart003  label="Piso 1"  # Arch/BIM 172 (typed FeaturePython)
  Area = 24900000
  Group = -> [BuildingPart012,BuildingPart015,Wall002,BuildingPart011]
  Height = 0
  HeightPropagate = true
  IfcData = attributes={"GlobalId": {"name": "GlobalId", "type": "IfcGloballyUniqueId", "is_enum": false, "enum_values": []}, "Description": {"... (+484 chars omitted),+1 more (map truncated)
  IfcType = 172
  LevelOffset = 0
  Placement = pos=(0,0,3000) rot=(0,0,1;0rad)
  PredefinedType = 0
FEATURE [Part::FeaturePython] Structure240  label="25x15 C045"  # Arch/BIM 24 (typed FeaturePython)
  FaceMaker = 0
  Height = 3000
  HorizontalArea = 37500
  IfcData = attributes={"GlobalId": {"name": "GlobalId", "type": "IfcGloballyUniqueId", "is_enum": false, "enum_values": []}, "Description": {"... (+438 chars omitted),+1 more (map truncated)
  IfcType = 24
  Length = 250
  MoveBase = false
  MoveWithHost = false
  Nodes = (2) [(-1.05471e-15,1.36424e-15,0),(-1.05471e-15,1.36424e-15,3000)]
  NodesOffset = 0
  Normal = (0,0,0)
  PerimeterLength = 800
  Placement = pos=(1930,9900,6000) rot=(0,0,1;0rad)
  PredefinedType = 0
  VerticalArea = 2400000
  Width = 150
FEATURE [Part::FeaturePython] Structure241  label="25x15 C046"  # Arch/BIM 172 (typed FeaturePython)
  FaceMaker = 0
  Height = 3000
  HorizontalArea = 37500
  IfcData = attributes={"GlobalId": {"name": "GlobalId", "type": "IfcGloballyUniqueId", "is_enum": false, "enum_values": []}, "Description": {"... (+484 chars omitted),+1 more (map truncated)
  IfcType = 172
  Length = 250
  MoveBase = false
  MoveWithHost = false
  Nodes = (2) [(-1.05471e-15,1.36424e-15,0),(-1.05471e-15,1.36424e-15,3000)]
  NodesOffset = 0
  Normal = (0,0,0)
  PerimeterLength = 800
  Placement = pos=(1930,100,6000) rot=(0,0,1;0rad)
  PredefinedType = 0
  VerticalArea = 2400000
  Width = 150
FEATURE [Part::FeaturePython] Structure242  label="25x20 C010"  # Arch/BIM 24 (typed FeaturePython)
  FaceMaker = 0
  Height = 3000
  HorizontalArea = 50000
  IfcData = attributes={"GlobalId": {"name": "GlobalId", "type": "IfcGloballyUniqueId", "is_enum": false, "enum_values": []}, "Description": {"... (+438 chars omitted),+1 more (map truncated)
  IfcType = 24
  Length = 250
  MoveBase = false
  MoveWithHost = false
  Nodes = (2) [(-1.05471e-15,-1.81899e-15,0),(-1.05471e-15,-1.81899e-15,3000)]
  NodesOffset = 0
  Normal = (0,0,0)
  PerimeterLength = 900
  Placement = pos=(1930,6640,6000) rot=(0,0,1;0rad)
  PredefinedType = 0
  VerticalArea = 2700000
  Width = 200
FEATURE [Part::FeaturePython] Structure243  label="25x20 C011"  # Arch/BIM 172 (typed FeaturePython)
  FaceMaker = 0
  Height = 3000
  HorizontalArea = 50000
  IfcData = attributes={"GlobalId": {"name": "GlobalId", "type": "IfcGloballyUniqueId", "is_enum": false, "enum_values": []}, "Description": {"... (+484 chars omitted),+1 more (map truncated)
  IfcType = 172
  Length = 250
  MoveBase = false
  MoveWithHost = false
  Nodes = (2) [(-1.05471e-15,-1.81899e-15,0),(-1.05471e-15,-1.81899e-15,3000)]
  NodesOffset = 0
  Normal = (0,0,0)
  PerimeterLength = 900
  Placement = pos=(1930,3350,6000) rot=(0,0,1;0rad)
  PredefinedType = 0
  VerticalArea = 2700000
  Width = 200
FEATURE [Part::FeaturePython] Structure244  label="25x15 C047"  # Arch/BIM 24 (typed FeaturePython)
  FaceMaker = 0
  Height = 3000
  HorizontalArea = 37500
  IfcData = attributes={"GlobalId": {"name": "GlobalId", "type": "IfcGloballyUniqueId", "is_enum": false, "enum_values": []}, "Description": {"... (+438 chars omitted),+1 more (map truncated)
  IfcType = 24
  Length = 250
  MoveBase = false
  MoveWithHost = false
  Nodes = (2) [(-1.05471e-15,1.36424e-15,0),(-1.05471e-15,1.36424e-15,3000)]
  NodesOffset = 0
  Normal = (0,0,0)
  PerimeterLength = 800
  Placement = pos=(6160,6640,6000) rot=(0,0,1;0rad)
  PredefinedType = 0
  VerticalArea = 2400000
  Width = 150
FEATURE [Part::FeaturePython] Structure245  label="25x15 C048"  # Arch/BIM 24 (typed FeaturePython)
  FaceMaker = 0
  Height = 3000
  HorizontalArea = 37500
  IfcData = attributes={"GlobalId": {"name": "GlobalId", "type": "IfcGloballyUniqueId", "is_enum": false, "enum_values": []}, "Description": {"... (+438 chars omitted),+1 more (map truncated)
  IfcType = 24
  Length = 250
  MoveBase = false
  MoveWithHost = false
  Nodes = (2) [(-1.05471e-15,1.36424e-15,0),(-1.05471e-15,1.36424e-15,3000)]
  NodesOffset = 0
  Normal = (0,0,0)
  PerimeterLength = 800
  Placement = pos=(6160,3350,6000) rot=(0,0,1;0rad)
  PredefinedType = 0
  VerticalArea = 2400000
  Width = 150
FEATURE [Part::FeaturePython] Structure246  label="25x15 C049"  # Arch/BIM 24 (typed FeaturePython)
  FaceMaker = 0
  Height = 3000
  HorizontalArea = 37500
  IfcData = attributes={"GlobalId": {"name": "GlobalId", "type": "IfcGloballyUniqueId", "is_enum": false, "enum_values": []}, "Description": {"... (+438 chars omitted),+1 more (map truncated)
  IfcType = 24
  Length = 250
  MoveBase = false
  MoveWithHost = false
  Nodes = (2) [(-1.05471e-15,1.36424e-15,0),(-1.05471e-15,1.36424e-15,3000)]
  NodesOffset = 0
  Normal = (0,0,0)
  PerimeterLength = 800
  Placement = pos=(6160,100,6000) rot=(0,0,1;0rad)
  PredefinedType = 0
  VerticalArea = 2400000
  Width = 150
FEATURE [Part::FeaturePython] Structure247  label="25x15 C050"  # Arch/BIM 24 (typed FeaturePython)
  FaceMaker = 0
  Height = 3000
  HorizontalArea = 37500
  IfcData = attributes={"GlobalId": {"name": "GlobalId", "type": "IfcGloballyUniqueId", "is_enum": false, "enum_values": []}, "Description": {"... (+438 chars omitted),+1 more (map truncated)
  IfcType = 24
  Length = 250
  MoveBase = false
  MoveWithHost = false
  Nodes = (2) [(-1.05471e-15,1.36424e-15,0),(-1.05471e-15,1.36424e-15,3000)]
  NodesOffset = 0
  Normal = (0,0,0)
  PerimeterLength = 800
  Placement = pos=(9010,100,6000) rot=(0,0,1;0rad)
  PredefinedType = 0
  VerticalArea = 2400000
  Width = 150
FEATURE [Part::FeaturePython] Structure248  label="25x15 C051"  # Arch/BIM 24 (typed FeaturePython)
  FaceMaker = 0
  Height = 3000
  HorizontalArea = 37500
  IfcData = attributes={"GlobalId": {"name": "GlobalId", "type": "IfcGloballyUniqueId", "is_enum": false, "enum_values": []}, "Description": {"... (+438 chars omitted),+1 more (map truncated)
  IfcType = 24
  Length = 250
  MoveBase = false
  MoveWithHost = false
  Nodes = (2) [(-1.05471e-15,1.36424e-15,0),(-1.05471e-15,1.36424e-15,3000)]
  NodesOffset = 0
  Normal = (0,0,0)
  PerimeterLength = 800
  Placement = pos=(10560,100,6000) rot=(0,0,1;0rad)
  PredefinedType = 0
  VerticalArea = 2400000
  Width = 150
FEATURE [Part::FeaturePython] Structure249  label="25x15 C052"  # Arch/BIM 24 (typed FeaturePython)
  FaceMaker = 0
  Height = 3000
  HorizontalArea = 37500
  IfcData = attributes={"GlobalId": {"name": "GlobalId", "type": "IfcGloballyUniqueId", "is_enum": false, "enum_values": []}, "Description": {"... (+438 chars omitted),+1 more (map truncated)
  IfcType = 24
  Length = 250
  MoveBase = false
  MoveWithHost = false
  Nodes = (2) [(-1.05471e-15,1.36424e-15,0),(-1.05471e-15,1.36424e-15,3000)]
  NodesOffset = 0
  Normal = (0,0,0)
  PerimeterLength = 800
  Placement = pos=(13780,100,6000) rot=(0,0,1;0rad)
  PredefinedType = 0
  VerticalArea = 2400000
  Width = 150
FEATURE [Part::FeaturePython] Structure250  label="25x15 C053"  # Arch/BIM 24 (typed FeaturePython)
  FaceMaker = 0
  Height = 3000
  HorizontalArea = 37500
  IfcData = attributes={"GlobalId": {"name": "GlobalId", "type": "IfcGloballyUniqueId", "is_enum": false, "enum_values": []}, "Description": {"... (+438 chars omitted),+1 more (map truncated)
  IfcType = 24
  Length = 250
  MoveBase = false
  MoveWithHost = false
  Nodes = (2) [(-1.05471e-15,1.36424e-15,0),(-1.05471e-15,1.36424e-15,3000)]
  NodesOffset = 0
  Normal = (0,0,0)
  PerimeterLength = 800
  Placement = pos=(15210,5970,6000) rot=(0,0,1;0rad)
  PredefinedType = 0
  VerticalArea = 2400000
  Width = 150
FEATURE [Part::FeaturePython] Structure251  label="25x15 C054"  # Arch/BIM 24 (typed FeaturePython)
  FaceMaker = 0
  Height = 3000
  HorizontalArea = 37500
  IfcData = attributes={"GlobalId": {"name": "GlobalId", "type": "IfcGloballyUniqueId", "is_enum": false, "enum_values": []}, "Description": {"... (+438 chars omitted),+1 more (map truncated)
  IfcType = 24
  Length = 250
  MoveBase = false
  MoveWithHost = false
  Nodes = (2) [(-1.05471e-15,1.36424e-15,0),(-1.05471e-15,1.36424e-15,3000)]
  NodesOffset = 0
  Normal = (0,0,0)
  PerimeterLength = 800
  Placement = pos=(13780,5970,6000) rot=(0,0,1;0rad)
  PredefinedType = 0
  VerticalArea = 2400000
  Width = 150
FEATURE [Part::FeaturePython] Structure252  label="25x15 C055"  # Arch/BIM 172 (typed FeaturePython)
  FaceMaker = 0
  Height = 3000
  HorizontalArea = 37500
  IfcData = attributes={"GlobalId": {"name": "GlobalId", "type": "IfcGloballyUniqueId", "is_enum": false, "enum_values": []}, "Description": {"... (+484 chars omitted),+1 more (map truncated)
  IfcType = 172
  Length = 250
  MoveBase = false
  MoveWithHost = false
  Nodes = (2) [(-1.05471e-15,1.36424e-15,0),(-1.05471e-15,1.36424e-15,3000)]
  NodesOffset = 0
  Normal = (0,0,0)
  PerimeterLength = 800
  Placement = pos=(1930,9900,6000) rot=(0,0,1;0rad)
  PredefinedType = 0
  VerticalArea = 2400000
  Width = 150
FEATURE [Part::FeaturePython] Structure253  label="25x15 C056"  # Arch/BIM 172 (typed FeaturePython)
  FaceMaker = 0
  Height = 3000
  HorizontalArea = 37500
  IfcData = attributes={"GlobalId": {"name": "GlobalId", "type": "IfcGloballyUniqueId", "is_enum": false, "enum_values": []}, "Description": {"... (+484 chars omitted),+1 more (map truncated)
  IfcType = 172
  Length = 250
  MoveBase = false
  MoveWithHost = false
  Nodes = (2) [(-1.05471e-15,1.36424e-15,0),(-1.05471e-15,1.36424e-15,3000)]
  NodesOffset = 0
  Normal = (0,0,0)
  PerimeterLength = 800
  Placement = pos=(9010,6640,6000) rot=(0,0,1;1.5708rad)
  PredefinedType = 0
  VerticalArea = 2400000
  Width = 150
FEATURE [Part::FeaturePython] Structure254  label="25x15 C057"  # Arch/BIM 172 (typed FeaturePython)
  FaceMaker = 0
  Height = 3000
  HorizontalArea = 37500
  IfcData = attributes={"GlobalId": {"name": "GlobalId", "type": "IfcGloballyUniqueId", "is_enum": false, "enum_values": []}, "Description": {"... (+484 chars omitted),+1 more (map truncated)
  IfcType = 172
  Length = 250
  MoveBase = false
  MoveWithHost = false
  Nodes = (2) [(-1.05471e-15,1.36424e-15,0),(-1.05471e-15,1.36424e-15,3000)]
  NodesOffset = 0
  Normal = (0,0,0)
  PerimeterLength = 800
  Placement = pos=(9010,3350,6000) rot=(0,0,1;1.5708rad)
  PredefinedType = 0
  VerticalArea = 2400000
  Width = 150
FEATURE [Part::FeaturePython] Structure255  label="25x15 C058"  # Arch/BIM 172 (typed FeaturePython)
  FaceMaker = 0
  Height = 3000
  HorizontalArea = 37500
  IfcData = attributes={"GlobalId": {"name": "GlobalId", "type": "IfcGloballyUniqueId", "is_enum": false, "enum_values": []}, "Description": {"... (+484 chars omitted),+1 more (map truncated)
  IfcType = 172
  Length = 250
  MoveBase = false
  MoveWithHost = false
  Nodes = (2) [(-1.05471e-15,1.36424e-15,0),(-1.05471e-15,1.36424e-15,3000)]
  NodesOffset = 0
  Normal = (0,0,0)
  PerimeterLength = 800
  Placement = pos=(10560,3350,6000) rot=(0,0,1;1.5708rad)
  PredefinedType = 0
  VerticalArea = 2400000
  Width = 150
FEATURE [Part::FeaturePython] Structure256  label="25x15 C059"  # Arch/BIM 172 (typed FeaturePython)
  FaceMaker = 0
  Height = 3000
  HorizontalArea = 37500
  IfcData = attributes={"GlobalId": {"name": "GlobalId", "type": "IfcGloballyUniqueId", "is_enum": false, "enum_values": []}, "Description": {"... (+484 chars omitted),+1 more (map truncated)
  IfcType = 172
  Length = 250
  MoveBase = false
  MoveWithHost = false
  Nodes = (2) [(-1.05471e-15,1.36424e-15,0),(-1.05471e-15,1.36424e-15,3000)]
  NodesOffset = 0
  Normal = (0,0,0)
  PerimeterLength = 800
  Placement = pos=(13780,3350,6000) rot=(0,0,1;1.5708rad)
  PredefinedType = 0
  VerticalArea = 2400000
  Width = 150
FEATURE [Part::FeaturePython] Structure257  label="25x15 C060"  # Arch/BIM 172 (typed FeaturePython)
  FaceMaker = 0
  Height = 3000
  HorizontalArea = 37500
  IfcData = attributes={"GlobalId": {"name": "GlobalId", "type": "IfcGloballyUniqueId", "is_enum": false, "enum_values": []}, "Description": {"... (+484 chars omitted),+1 more (map truncated)
  IfcType = 172
  Length = 250
  MoveBase = false
  MoveWithHost = false
  Nodes = (2) [(-1.05471e-15,1.36424e-15,0),(-1.05471e-15,1.36424e-15,3000)]
  NodesOffset = 0
  Normal = (0,0,0)
  PerimeterLength = 800
  Placement = pos=(9010,9900,6000) rot=(0,0,1;0rad)
  PredefinedType = 0
  VerticalArea = 2400000
  Width = 150
FEATURE [Part::FeaturePython] Structure258  label="25x15 C061"  # Arch/BIM 172 (typed FeaturePython)
  FaceMaker = 0
  Height = 3000
  HorizontalArea = 37500
  IfcData = attributes={"GlobalId": {"name": "GlobalId", "type": "IfcGloballyUniqueId", "is_enum": false, "enum_values": []}, "Description": {"... (+484 chars omitted),+1 more (map truncated)
  IfcType = 172
  Length = 250
  MoveBase = false
  MoveWithHost = false
  Nodes = (2) [(-1.05471e-15,1.36424e-15,0),(-1.05471e-15,1.36424e-15,3000)]
  NodesOffset = 0
  Normal = (0,0,0)
  PerimeterLength = 800
  Placement = pos=(6160,9900,6000) rot=(0,0,1;0rad)
  PredefinedType = 0
  VerticalArea = 2400000
  Width = 150
FEATURE [Part::FeaturePython] Structure259  label="25x15 C062"  # Arch/BIM 172 (typed FeaturePython)
  FaceMaker = 0
  Height = 3000
  HorizontalArea = 37500
  IfcData = attributes={"GlobalId": {"name": "GlobalId", "type": "IfcGloballyUniqueId", "is_enum": false, "enum_values": []}, "Description": {"... (+484 chars omitted),+1 more (map truncated)
  IfcType = 172
  Length = 250
  MoveBase = false
  MoveWithHost = false
  Nodes = (2) [(-1.05471e-15,1.36424e-15,0),(-1.05471e-15,1.36424e-15,3000)]
  NodesOffset = 0
  Normal = (0,0,0)
  PerimeterLength = 800
  Placement = pos=(12010,9900,6000) rot=(0,0,1;0rad)
  PredefinedType = 0
  VerticalArea = 2400000
  Width = 150
FEATURE [Part::FeaturePython] Structure260  label="25x15 C063"  # Arch/BIM 172 (typed FeaturePython)
  FaceMaker = 0
  Height = 3000
  HorizontalArea = 37500
  IfcData = attributes={"GlobalId": {"name": "GlobalId", "type": "IfcGloballyUniqueId", "is_enum": false, "enum_values": []}, "Description": {"... (+484 chars omitted),+1 more (map truncated)
  IfcType = 172
  Length = 250
  MoveBase = false
  MoveWithHost = false
  Nodes = (2) [(-1.05471e-15,1.36424e-15,0),(-1.05471e-15,1.36424e-15,3000)]
  NodesOffset = 0
  Normal = (0,0,0)
  PerimeterLength = 800
  Placement = pos=(15210,9900,6000) rot=(0,0,1;0rad)
  PredefinedType = 0
  VerticalArea = 2400000
  Width = 150
FEATURE [App::GeometryPython] BuildingPart016  label="Columnas P2"  # Arch/BIM 172 (typed FeaturePython)
  Area = 0
  Group = -> [Structure240,Structure241,Structure244,Structure245,Structure246,Structure247,Structure248,Structure249,Structure250,Structure251,Structure252,Structure253,Structure254,Structure255,Structure256,Structure257,Structure258,Structure259,Structure260,Structure242,Structure243]
  Height = 0
  HeightPropagate = true
  IfcData = attributes={"GlobalId": {"name": "GlobalId", "type": "IfcGloballyUniqueId", "is_enum": false, "enum_values": []}, "Description": {"... (+484 chars omitted),+1 more (map truncated)
  IfcType = 172
  LevelOffset = 0
  PredefinedType = 0
FEATURE [Part::FeaturePython] Wall003  label="Tabique Ascensor P2"  # Arch/BIM 166 (typed FeaturePython)
  Align = 1
  Area = 24900000
  Base = -> Rectangle003
  BlockHeight = 0
  BlockLength = 0
  CountBroken = 0
  CountEntire = 0
  Face = 0
  Height = 3000
  HorizontalArea = 1155000
  IfcData = attributes={"GlobalId": {"name": "GlobalId", "type": "IfcGloballyUniqueId", "is_enum": false, "enum_values": []}, "Description": {"... (+533 chars omitted),+1 more (map truncated)
  IfcType = 166
  Joint = 0
  Length = 8300
  MakeBlocks = false
  MoveBase = false
  MoveWithHost = false
  Normal = (0,0,0)
  OffsetFirst = 0
  OffsetSecond = 0
  PerimeterLength = 8300
  Placement = pos=(0,0,6000) rot=(0,0,1;0rad)
  PredefinedType = 0
  VerticalArea = 46200000
  Width = 150
FEATURE [Part::FeaturePython] Structure261  label="V15x40 V161"  # Arch/BIM 7 (typed FeaturePython)
  FaceMaker = 0
  Height = 400
  HorizontalArea = 597000
  IfcData = attributes={"GlobalId": {"name": "GlobalId", "type": "IfcGloballyUniqueId", "is_enum": false, "enum_values": []}, "Description": {"... (+475 chars omitted),+1 more (map truncated)
  IfcType = 7
  Length = 3980
  MoveBase = false
  MoveWithHost = false
  Nodes = (2) [(-1.72563e-31,-1.42109e-15,-7.77156e-16),(3980,-1.42109e-15,-7.77156e-16)]
  NodesOffset = 0
  Normal = (0,0,0)
  PerimeterLength = 8260
  Placement = pos=(2055,9900,8800) rot=(0,0,1;0rad)
  PredefinedType = 0
  VerticalArea = 3.304e+06
  Width = 150
FEATURE [Part::FeaturePython] Structure262  label="V15x40 V162"  # Arch/BIM 7 (typed FeaturePython)
  FaceMaker = 0
  Height = 400
  HorizontalArea = 390000
  IfcData = attributes={"GlobalId": {"name": "GlobalId", "type": "IfcGloballyUniqueId", "is_enum": false, "enum_values": []}, "Description": {"... (+475 chars omitted),+1 more (map truncated)
  IfcType = 7
  Length = 2600
  MoveBase = false
  MoveWithHost = false
  Nodes = (2) [(-1.72563e-31,-1.42109e-15,-7.77156e-16),(2600,-1.42109e-15,-7.77156e-16)]
  NodesOffset = 0
  Normal = (0,0,0)
  PerimeterLength = 5500
  Placement = pos=(6285,9900,8800) rot=(0,0,1;0rad)
  PredefinedType = 0
  VerticalArea = 2200000
  Width = 150
FEATURE [Part::FeaturePython] Structure263  label="V15x40 V163"  # Arch/BIM 7 (typed FeaturePython)
  FaceMaker = 0
  Height = 400
  HorizontalArea = 412500
  IfcData = attributes={"GlobalId": {"name": "GlobalId", "type": "IfcGloballyUniqueId", "is_enum": false, "enum_values": []}, "Description": {"... (+475 chars omitted),+1 more (map truncated)
  IfcType = 7
  Length = 2750
  MoveBase = false
  MoveWithHost = false
  Nodes = (2) [(-1.72563e-31,-1.42109e-15,-7.77156e-16),(2750,-1.42109e-15,-7.77156e-16)]
  NodesOffset = 0
  Normal = (0,0,0)
  PerimeterLength = 5800
  Placement = pos=(9135,9900,8800) rot=(0,0,1;0rad)
  PredefinedType = 0
  VerticalArea = 2320000
  Width = 150
FEATURE [Part::FeaturePython] Structure264  label="V15x40 V164"  # Arch/BIM 7 (typed FeaturePython)
  FaceMaker = 0
  Height = 400
  HorizontalArea = 442500
  IfcData = attributes={"GlobalId": {"name": "GlobalId", "type": "IfcGloballyUniqueId", "is_enum": false, "enum_values": []}, "Description": {"... (+475 chars omitted),+1 more (map truncated)
  IfcType = 7
  Length = 2950
  MoveBase = false
  MoveWithHost = false
  Nodes = (2) [(-1.72563e-31,-1.42109e-15,-7.77156e-16),(2950,-1.42109e-15,-7.77156e-16)]
  NodesOffset = 0
  Normal = (0,0,0)
  PerimeterLength = 6200
  Placement = pos=(12135,9900,8800) rot=(0,0,1;0rad)
  PredefinedType = 0
  VerticalArea = 2.48e+06
  Width = 150
FEATURE [Part::FeaturePython] Structure265  label="V15x40 V165"  # Arch/BIM 7 (typed FeaturePython)
  FaceMaker = 0
  Height = 400
  HorizontalArea = 453750
  IfcData = attributes={"GlobalId": {"name": "GlobalId", "type": "IfcGloballyUniqueId", "is_enum": false, "enum_values": []}, "Description": {"... (+475 chars omitted),+1 more (map truncated)
  IfcType = 7
  Length = 3025
  MoveBase = false
  MoveWithHost = false
  Nodes = (2) [(-1.72563e-31,-1.42109e-15,-7.77156e-16),(3025,-1.42109e-15,-7.77156e-16)]
  NodesOffset = 0
  Normal = (0,0,0)
  PerimeterLength = 6350
  Placement = pos=(12085,8370,8800) rot=(0,0,1;0rad)
  PredefinedType = 0
  VerticalArea = 2.54e+06
  Width = 150
FEATURE [Part::FeaturePython] Structure266  label="V15x40 V166"  # Arch/BIM 7 (typed FeaturePython)
  FaceMaker = 0
  Height = 400
  HorizontalArea = 597000
  IfcData = attributes={"GlobalId": {"name": "GlobalId", "type": "IfcGloballyUniqueId", "is_enum": false, "enum_values": []}, "Description": {"... (+475 chars omitted),+1 more (map truncated)
  IfcType = 7
  Length = 3980
  MoveBase = false
  MoveWithHost = false
  Nodes = (2) [(-1.72563e-31,-1.42109e-15,-7.77156e-16),(3980,-1.42109e-15,-7.77156e-16)]
  NodesOffset = 0
  Normal = (0,0,0)
  PerimeterLength = 8260
  Placement = pos=(2055,6640,8800) rot=(0,0,1;0rad)
  PredefinedType = 0
  VerticalArea = 3.304e+06
  Width = 150
FEATURE [Part::FeaturePython] Structure267  label="V15x40 V167"  # Arch/BIM 7 (typed FeaturePython)
  FaceMaker = 0
  Height = 400
  HorizontalArea = 397500
  IfcData = attributes={"GlobalId": {"name": "GlobalId", "type": "IfcGloballyUniqueId", "is_enum": false, "enum_values": []}, "Description": {"... (+475 chars omitted),+1 more (map truncated)
  IfcType = 7
  Length = 2650
  MoveBase = false
  MoveWithHost = false
  Nodes = (2) [(-1.72563e-31,-1.42109e-15,-7.77156e-16),(2650,-1.42109e-15,-7.77156e-16)]
  NodesOffset = 0
  Normal = (0,0,0)
  PerimeterLength = 5600
  Placement = pos=(6285,6640,8800) rot=(0,0,1;0rad)
  PredefinedType = 0
  VerticalArea = 2240000
  Width = 150
FEATURE [Part::FeaturePython] Structure268  label="V15x40 V168"  # Arch/BIM 7 (typed FeaturePython)
  FaceMaker = 0
  Height = 400
  HorizontalArea = 210000
  IfcData = attributes={"GlobalId": {"name": "GlobalId", "type": "IfcGloballyUniqueId", "is_enum": false, "enum_values": []}, "Description": {"... (+475 chars omitted),+1 more (map truncated)
  IfcType = 7
  Length = 1400
  MoveBase = false
  MoveWithHost = false
  Nodes = (2) [(-1.72563e-31,-1.42109e-15,-7.77156e-16),(1400,-1.42109e-15,-7.77156e-16)]
  NodesOffset = 0
  Normal = (0,0,0)
  PerimeterLength = 3100
  Placement = pos=(9085,6640,8800) rot=(0,0,1;0rad)
  PredefinedType = 0
  VerticalArea = 1240000
  Width = 150
FEATURE [Part::FeaturePython] Structure269  label="V15x40 V169"  # Arch/BIM 7 (typed FeaturePython)
  FaceMaker = 0
  Height = 400
  HorizontalArea = 235500
  IfcData = attributes={"GlobalId": {"name": "GlobalId", "type": "IfcGloballyUniqueId", "is_enum": false, "enum_values": []}, "Description": {"... (+475 chars omitted),+1 more (map truncated)
  IfcType = 7
  Length = 1570
  MoveBase = false
  MoveWithHost = false
  Nodes = (2) [(-1.72563e-31,-1.42109e-15,-7.77156e-16),(1570,-1.42109e-15,-7.77156e-16)]
  NodesOffset = 0
  Normal = (0,0,0)
  PerimeterLength = 3440
  Placement = pos=(13655,5970,8800) rot=(0,0,1;3.14159rad)
  PredefinedType = 0
  VerticalArea = 1.376e+06
  Width = 150
FEATURE [Part::FeaturePython] Structure270  label="V15x40 V170"  # Arch/BIM 7 (typed FeaturePython)
  FaceMaker = 0
  Height = 400
  HorizontalArea = 177000
  IfcData = attributes={"GlobalId": {"name": "GlobalId", "type": "IfcGloballyUniqueId", "is_enum": false, "enum_values": []}, "Description": {"... (+475 chars omitted),+1 more (map truncated)
  IfcType = 7
  Length = 1180
  MoveBase = false
  MoveWithHost = false
  Nodes = (2) [(-1.72563e-31,-1.42109e-15,-7.77156e-16),(1180,-1.42109e-15,-7.77156e-16)]
  NodesOffset = 0
  Normal = (0,0,0)
  PerimeterLength = 2660
  Placement = pos=(13905,5970,8800) rot=(0,0,1;0rad)
  PredefinedType = 0
  VerticalArea = 1064000
  Width = 150
FEATURE [Part::FeaturePython] Structure271  label="V15x40 V171"  # Arch/BIM 7 (typed FeaturePython)
  FaceMaker = 0
  Height = 400
  HorizontalArea = 597000
  IfcData = attributes={"GlobalId": {"name": "GlobalId", "type": "IfcGloballyUniqueId", "is_enum": false, "enum_values": []}, "Description": {"... (+475 chars omitted),+1 more (map truncated)
  IfcType = 7
  Length = 3980
  MoveBase = false
  MoveWithHost = false
  Nodes = (2) [(-1.72563e-31,-1.42109e-15,-7.77156e-16),(3980,-1.42109e-15,-7.77156e-16)]
  NodesOffset = 0
  Normal = (0,0,0)
  PerimeterLength = 8260
  Placement = pos=(2055,3350,8800) rot=(0,0,1;0rad)
  PredefinedType = 0
  VerticalArea = 3.304e+06
  Width = 150
FEATURE [Part::FeaturePython] Structure272  label="V15x40 V172"  # Arch/BIM 7 (typed FeaturePython)
  FaceMaker = 0
  Height = 400
  HorizontalArea = 397500
  IfcData = attributes={"GlobalId": {"name": "GlobalId", "type": "IfcGloballyUniqueId", "is_enum": false, "enum_values": []}, "Description": {"... (+475 chars omitted),+1 more (map truncated)
  IfcType = 7
  Length = 2650
  MoveBase = false
  MoveWithHost = false
  Nodes = (2) [(-1.72563e-31,-1.42109e-15,-7.77156e-16),(2650,-1.42109e-15,-7.77156e-16)]
  NodesOffset = 0
  Normal = (0,0,0)
  PerimeterLength = 5600
  Placement = pos=(6285,3350,8800) rot=(0,0,1;0rad)
  PredefinedType = 0
  VerticalArea = 2240000
  Width = 150
FEATURE [Part::FeaturePython] Structure273  label="V15x40 V173"  # Arch/BIM 7 (typed FeaturePython)
  FaceMaker = 0
  Height = 400
  HorizontalArea = 210000
  IfcData = attributes={"GlobalId": {"name": "GlobalId", "type": "IfcGloballyUniqueId", "is_enum": false, "enum_values": []}, "Description": {"... (+475 chars omitted),+1 more (map truncated)
  IfcType = 7
  Length = 1400
  MoveBase = false
  MoveWithHost = false
  Nodes = (2) [(-1.72563e-31,-1.42109e-15,-7.77156e-16),(1400,-1.42109e-15,-7.77156e-16)]
  NodesOffset = 0
  Normal = (0,0,0)
  PerimeterLength = 3100
  Placement = pos=(9085,3350,8800) rot=(0,0,1;0rad)
  PredefinedType = 0
  VerticalArea = 1240000
  Width = 150
FEATURE [Part::FeaturePython] Structure274  label="V15x40 V174"  # Arch/BIM 7 (typed FeaturePython)
  FaceMaker = 0
  Height = 400
  HorizontalArea = 460500
  IfcData = attributes={"GlobalId": {"name": "GlobalId", "type": "IfcGloballyUniqueId", "is_enum": false, "enum_values": []}, "Description": {"... (+475 chars omitted),+1 more (map truncated)
  IfcType = 7
  Length = 3070
  MoveBase = false
  MoveWithHost = false
  Nodes = (2) [(-1.72563e-31,-1.42109e-15,-7.77156e-16),(3070,-1.42109e-15,-7.77156e-16)]
  NodesOffset = 0
  Normal = (0,0,0)
  PerimeterLength = 6440
  Placement = pos=(10635,3350,8800) rot=(0,0,1;0rad)
  PredefinedType = 0
  VerticalArea = 2.576e+06
  Width = 150
FEATURE [Part::FeaturePython] Structure275  label="V15x40 V175"  # Arch/BIM 7 (typed FeaturePython)
  FaceMaker = 0
  Height = 400
  HorizontalArea = 597000
  IfcData = attributes={"GlobalId": {"name": "GlobalId", "type": "IfcGloballyUniqueId", "is_enum": false, "enum_values": []}, "Description": {"... (+475 chars omitted),+1 more (map truncated)
  IfcType = 7
  Length = 3980
  MoveBase = false
  MoveWithHost = false
  Nodes = (2) [(-1.72563e-31,-1.42109e-15,-7.77156e-16),(3980,-1.42109e-15,-7.77156e-16)]
  NodesOffset = 0
  Normal = (0,0,0)
  PerimeterLength = 8260
  Placement = pos=(2055,100,8800) rot=(0,0,1;0rad)
  PredefinedType = 0
  VerticalArea = 3.304e+06
  Width = 150
FEATURE [Part::FeaturePython] Structure276  label="V15x40 V176"  # Arch/BIM 7 (typed FeaturePython)
  FaceMaker = 0
  Height = 400
  HorizontalArea = 390000
  IfcData = attributes={"GlobalId": {"name": "GlobalId", "type": "IfcGloballyUniqueId", "is_enum": false, "enum_values": []}, "Description": {"... (+475 chars omitted),+1 more (map truncated)
  IfcType = 7
  Length = 2600
  MoveBase = false
  MoveWithHost = false
  Nodes = (2) [(-1.72563e-31,-1.42109e-15,-7.77156e-16),(2600,-1.42109e-15,-7.77156e-16)]
  NodesOffset = 0
  Normal = (0,0,0)
  PerimeterLength = 5500
  Placement = pos=(6285,100,8800) rot=(0,0,1;0rad)
  PredefinedType = 0
  VerticalArea = 2200000
  Width = 150
FEATURE [Part::FeaturePython] Structure277  label="V15x40 V177"  # Arch/BIM 7 (typed FeaturePython)
  FaceMaker = 0
  Height = 400
  HorizontalArea = 195000
  IfcData = attributes={"GlobalId": {"name": "GlobalId", "type": "IfcGloballyUniqueId", "is_enum": false, "enum_values": []}, "Description": {"... (+475 chars omitted),+1 more (map truncated)
  IfcType = 7
  Length = 1300
  MoveBase = false
  MoveWithHost = false
  Nodes = (2) [(-1.72563e-31,-1.42109e-15,-7.77156e-16),(1300,-1.42109e-15,-7.77156e-16)]
  NodesOffset = 0
  Normal = (0,0,0)
  PerimeterLength = 2900
  Placement = pos=(9135,100,8800) rot=(0,0,1;0rad)
  PredefinedType = 0
  VerticalArea = 1160000
  Width = 150
FEATURE [Part::FeaturePython] Structure278  label="V15x40 V178"  # Arch/BIM 7 (typed FeaturePython)
  FaceMaker = 0
  Height = 400
  HorizontalArea = 445500
  IfcData = attributes={"GlobalId": {"name": "GlobalId", "type": "IfcGloballyUniqueId", "is_enum": false, "enum_values": []}, "Description": {"... (+475 chars omitted),+1 more (map truncated)
  IfcType = 7
  Length = 2970
  MoveBase = false
  MoveWithHost = false
  Nodes = (2) [(-1.72563e-31,-1.42109e-15,-7.77156e-16),(2970,-1.42109e-15,-7.77156e-16)]
  NodesOffset = 0
  Normal = (0,0,0)
  PerimeterLength = 6240
  Placement = pos=(10685,100,8800) rot=(0,0,1;0rad)
  PredefinedType = 0
  VerticalArea = 2.496e+06
  Width = 150
FEATURE [Part::FeaturePython] Structure279  label="V15x40 V179"  # Arch/BIM 7 (typed FeaturePython)
  FaceMaker = 0
  Height = 400
  HorizontalArea = 465000
  IfcData = attributes={"GlobalId": {"name": "GlobalId", "type": "IfcGloballyUniqueId", "is_enum": false, "enum_values": []}, "Description": {"... (+475 chars omitted),+1 more (map truncated)
  IfcType = 7
  Length = 3100
  MoveBase = false
  MoveWithHost = false
  Nodes = (2) [(-1.72563e-31,-1.42109e-15,-7.77156e-16),(3100,-1.42109e-15,-7.77156e-16)]
  NodesOffset = 0
  Normal = (0,0,0)
  PerimeterLength = 6500
  Placement = pos=(6160,3275,8800) rot=(0,0,-1;1.5708rad)
  PredefinedType = 0
  VerticalArea = 2.6e+06
  Width = 150
FEATURE [Part::FeaturePython] Structure280  label="V15x40 V180"  # Arch/BIM 7 (typed FeaturePython)
  FaceMaker = 0
  Height = 400
  HorizontalArea = 471000
  IfcData = attributes={"GlobalId": {"name": "GlobalId", "type": "IfcGloballyUniqueId", "is_enum": false, "enum_values": []}, "Description": {"... (+475 chars omitted),+1 more (map truncated)
  IfcType = 7
  Length = 3140
  MoveBase = false
  MoveWithHost = false
  Nodes = (2) [(-1.72563e-31,-1.42109e-15,-7.77156e-16),(3140,-1.42109e-15,-7.77156e-16)]
  NodesOffset = 0
  Normal = (0,0,0)
  PerimeterLength = 6580
  Placement = pos=(6160,6565,8800) rot=(0,0,-1;1.5708rad)
  PredefinedType = 0
  VerticalArea = 2.632e+06
  Width = 150
FEATURE [Part::FeaturePython] Structure281  label="V15x40 V181"  # Arch/BIM 7 (typed FeaturePython)
  FaceMaker = 0
  Height = 400
  HorizontalArea = 466500
  IfcData = attributes={"GlobalId": {"name": "GlobalId", "type": "IfcGloballyUniqueId", "is_enum": false, "enum_values": []}, "Description": {"... (+475 chars omitted),+1 more (map truncated)
  IfcType = 7
  Length = 3110
  MoveBase = false
  MoveWithHost = false
  Nodes = (2) [(-1.72563e-31,-1.42109e-15,-7.77156e-16),(3110,-1.42109e-15,-7.77156e-16)]
  NodesOffset = 0
  Normal = (0,0,0)
  PerimeterLength = 6520
  Placement = pos=(6160,9825,8800) rot=(0,0,-1;1.5708rad)
  PredefinedType = 0
  VerticalArea = 2.608e+06
  Width = 150
FEATURE [Part::FeaturePython] Structure282  label="V15x40 V182"  # Arch/BIM 7 (typed FeaturePython)
  FaceMaker = 0
  Height = 400
  HorizontalArea = 457500
  IfcData = attributes={"GlobalId": {"name": "GlobalId", "type": "IfcGloballyUniqueId", "is_enum": false, "enum_values": []}, "Description": {"... (+475 chars omitted),+1 more (map truncated)
  IfcType = 7
  Length = 3050
  MoveBase = false
  MoveWithHost = false
  Nodes = (2) [(-1.72563e-31,-1.42109e-15,-7.77156e-16),(3050,-1.42109e-15,-7.77156e-16)]
  NodesOffset = 0
  Normal = (0,0,0)
  PerimeterLength = 6400
  Placement = pos=(9010,3225,8800) rot=(0,0,-1;1.5708rad)
  PredefinedType = 0
  VerticalArea = 2.56e+06
  Width = 150
FEATURE [Part::FeaturePython] Structure283  label="V15x40 V183"  # Arch/BIM 7 (typed FeaturePython)
  FaceMaker = 0
  Height = 400
  HorizontalArea = 456000
  IfcData = attributes={"GlobalId": {"name": "GlobalId", "type": "IfcGloballyUniqueId", "is_enum": false, "enum_values": []}, "Description": {"... (+475 chars omitted),+1 more (map truncated)
  IfcType = 7
  Length = 3040
  MoveBase = false
  MoveWithHost = false
  Nodes = (2) [(-1.72563e-31,-1.42109e-15,-7.77156e-16),(3040,-1.42109e-15,-7.77156e-16)]
  NodesOffset = 0
  Normal = (0,0,0)
  PerimeterLength = 6380
  Placement = pos=(9010,6515,8800) rot=(0,0,-1;1.5708rad)
  PredefinedType = 0
  VerticalArea = 2.552e+06
  Width = 150
FEATURE [Part::FeaturePython] Structure284  label="V15x40 V184"  # Arch/BIM 7 (typed FeaturePython)
  FaceMaker = 0
  Height = 400
  HorizontalArea = 459000
  IfcData = attributes={"GlobalId": {"name": "GlobalId", "type": "IfcGloballyUniqueId", "is_enum": false, "enum_values": []}, "Description": {"... (+475 chars omitted),+1 more (map truncated)
  IfcType = 7
  Length = 3060
  MoveBase = false
  MoveWithHost = false
  Nodes = (2) [(-1.72563e-31,-1.42109e-15,-7.77156e-16),(3060,-1.42109e-15,-7.77156e-16)]
  NodesOffset = 0
  Normal = (0,0,0)
  PerimeterLength = 6420
  Placement = pos=(9010,9825,8800) rot=(0,0,-1;1.5708rad)
  PredefinedType = 0
  VerticalArea = 2.568e+06
  Width = 150
FEATURE [Part::FeaturePython] Structure285  label="V15x40 V185"  # Arch/BIM 7 (typed FeaturePython)
  FaceMaker = 0
  Height = 400
  HorizontalArea = 457500
  IfcData = attributes={"GlobalId": {"name": "GlobalId", "type": "IfcGloballyUniqueId", "is_enum": false, "enum_values": []}, "Description": {"... (+475 chars omitted),+1 more (map truncated)
  IfcType = 7
  Length = 3050
  MoveBase = false
  MoveWithHost = false
  Nodes = (2) [(-1.72563e-31,-1.42109e-15,-7.77156e-16),(3050,-1.42109e-15,-7.77156e-16)]
  NodesOffset = 0
  Normal = (0,0,0)
  PerimeterLength = 6400
  Placement = pos=(10560,3225,8800) rot=(0,0,-1;1.5708rad)
  PredefinedType = 0
  VerticalArea = 2.56e+06
  Width = 150
FEATURE [Part::FeaturePython] Structure286  label="V15x40 V186"  # Arch/BIM 7 (typed FeaturePython)
  FaceMaker = 0
  Height = 400
  HorizontalArea = 363000
  IfcData = attributes={"GlobalId": {"name": "GlobalId", "type": "IfcGloballyUniqueId", "is_enum": false, "enum_values": []}, "Description": {"... (+475 chars omitted),+1 more (map truncated)
  IfcType = 7
  Length = 2420
  MoveBase = false
  MoveWithHost = false
  Nodes = (2) [(-1.72563e-31,-1.42109e-15,-7.77156e-16),(2420,-1.42109e-15,-7.77156e-16)]
  NodesOffset = 0
  Normal = (0,0,0)
  PerimeterLength = 5140
  Placement = pos=(10560,3475,8800) rot=(0,0,1;1.5708rad)
  PredefinedType = 0
  VerticalArea = 2056000
  Width = 150
FEATURE [Part::FeaturePython] Structure287  label="V15x40 V187"  # Arch/BIM 7 (typed FeaturePython)
  FaceMaker = 0
  Height = 400
  HorizontalArea = 207000
  IfcData = attributes={"GlobalId": {"name": "GlobalId", "type": "IfcGloballyUniqueId", "is_enum": false, "enum_values": []}, "Description": {"... (+475 chars omitted),+1 more (map truncated)
  IfcType = 7
  Length = 1380
  MoveBase = false
  MoveWithHost = false
  Nodes = (2) [(-1.72563e-31,-1.42109e-15,-7.77156e-16),(1380,-1.42109e-15,-7.77156e-16)]
  NodesOffset = 0
  Normal = (0,0,0)
  PerimeterLength = 3060
  Placement = pos=(10560,8445,8800) rot=(0,0,1;1.5708rad)
  PredefinedType = 0
  VerticalArea = 1224000
  Width = 150
FEATURE [Part::FeaturePython] Structure288  label="V15x40 V188"  # Arch/BIM 7 (typed FeaturePython)
  FaceMaker = 0
  Height = 400
  HorizontalArea = 207000
  IfcData = attributes={"GlobalId": {"name": "GlobalId", "type": "IfcGloballyUniqueId", "is_enum": false, "enum_values": []}, "Description": {"... (+475 chars omitted),+1 more (map truncated)
  IfcType = 7
  Length = 1380
  MoveBase = false
  MoveWithHost = false
  Nodes = (2) [(-1.72563e-31,-1.42109e-15,-7.77156e-16),(1380,-1.42109e-15,-7.77156e-16)]
  NodesOffset = 0
  Normal = (0,0,0)
  PerimeterLength = 3060
  Placement = pos=(12010,9825,8800) rot=(0,0,-1;1.5708rad)
  PredefinedType = 0
  VerticalArea = 1224000
  Width = 150
FEATURE [Part::FeaturePython] Structure289  label="V20x40 V142"  # Arch/BIM 7 (typed FeaturePython)
  FaceMaker = 0
  Height = 400
  HorizontalArea = 615000
  IfcData = attributes={"GlobalId": {"name": "GlobalId", "type": "IfcGloballyUniqueId", "is_enum": false, "enum_values": []}, "Description": {"... (+475 chars omitted),+1 more (map truncated)
  IfcType = 7
  Length = 3075
  MoveBase = false
  MoveWithHost = false
  Nodes = (2) [(-1.72563e-31,0,-7.77156e-16),(3075,0,-7.77156e-16)]
  NodesOffset = 0
  Normal = (0,0,0)
  PerimeterLength = 6550
  Placement = pos=(1930,3250,8800) rot=(0,0,-1;1.5708rad)
  PredefinedType = 0
  VerticalArea = 2.62e+06
  Width = 200
FEATURE [Part::FeaturePython] Structure290  label="V20x40 V143"  # Arch/BIM 7 (typed FeaturePython)
  FaceMaker = 0
  Height = 400
  HorizontalArea = 618000
  IfcData = attributes={"GlobalId": {"name": "GlobalId", "type": "IfcGloballyUniqueId", "is_enum": false, "enum_values": []}, "Description": {"... (+475 chars omitted),+1 more (map truncated)
  IfcType = 7
  Length = 3090
  MoveBase = false
  MoveWithHost = false
  Nodes = (2) [(-1.72563e-31,0,-7.77156e-16),(3090,0,-7.77156e-16)]
  NodesOffset = 0
  Normal = (0,0,0)
  PerimeterLength = 6580
  Placement = pos=(1930,6540,8800) rot=(0,0,-1;1.5708rad)
  PredefinedType = 0
  VerticalArea = 2.632e+06
  Width = 200
FEATURE [Part::FeaturePython] Structure291  label="V20x40 V144"  # Arch/BIM 7 (typed FeaturePython)
  FaceMaker = 0
  Height = 400
  HorizontalArea = 617000
  IfcData = attributes={"GlobalId": {"name": "GlobalId", "type": "IfcGloballyUniqueId", "is_enum": false, "enum_values": []}, "Description": {"... (+475 chars omitted),+1 more (map truncated)
  IfcType = 7
  Length = 3085
  MoveBase = false
  MoveWithHost = false
  Nodes = (2) [(-1.72563e-31,0,-7.77156e-16),(3085,0,-7.77156e-16)]
  NodesOffset = 0
  Normal = (0,0,0)
  PerimeterLength = 6570
  Placement = pos=(1930,9825,8800) rot=(0,0,-1;1.5708rad)
  PredefinedType = 0
  VerticalArea = 2.628e+06
  Width = 200
FEATURE [Part::FeaturePython] Structure292  label="V20x40 V145"  # Arch/BIM 7 (typed FeaturePython)
  FaceMaker = 0
  Height = 400
  HorizontalArea = 635000
  IfcData = attributes={"GlobalId": {"name": "GlobalId", "type": "IfcGloballyUniqueId", "is_enum": false, "enum_values": []}, "Description": {"... (+475 chars omitted),+1 more (map truncated)
  IfcType = 7
  Length = 3175
  MoveBase = false
  MoveWithHost = false
  Nodes = (2) [(-1.72563e-31,0,-7.77156e-16),(3175,0,-7.77156e-16)]
  NodesOffset = 0
  Normal = (0,0,0)
  PerimeterLength = 6750
  Placement = pos=(13780,175,8800) rot=(0,0,1;1.5708rad)
  PredefinedType = 0
  VerticalArea = 2.7e+06
  Width = 200
FEATURE [Part::FeaturePython] Structure293  label="V20x40 V146"  # Arch/BIM 7 (typed FeaturePython)
  FaceMaker = 0
  Height = 400
  HorizontalArea = 509000
  IfcData = attributes={"GlobalId": {"name": "GlobalId", "type": "IfcGloballyUniqueId", "is_enum": false, "enum_values": []}, "Description": {"... (+475 chars omitted),+1 more (map truncated)
  IfcType = 7
  Length = 2545
  MoveBase = false
  MoveWithHost = false
  Nodes = (2) [(-1.72563e-31,0,-7.77156e-16),(2545,0,-7.77156e-16)]
  NodesOffset = 0
  Normal = (0,0,0)
  PerimeterLength = 5490
  Placement = pos=(13780,3350,8800) rot=(0,0,1;1.5708rad)
  PredefinedType = 0
  VerticalArea = 2196000
  Width = 200
FEATURE [Part::FeaturePython] Structure294  label="V20x40 V147"  # Arch/BIM 7 (typed FeaturePython)
  FaceMaker = 0
  Height = 400
  HorizontalArea = 756000
  IfcData = attributes={"GlobalId": {"name": "GlobalId", "type": "IfcGloballyUniqueId", "is_enum": false, "enum_values": []}, "Description": {"... (+475 chars omitted),+1 more (map truncated)
  IfcType = 7
  Length = 3780
  MoveBase = false
  MoveWithHost = false
  Nodes = (2) [(-1.72563e-31,0,-7.77156e-16),(3780,0,-7.77156e-16)]
  NodesOffset = 0
  Normal = (0,0,0)
  PerimeterLength = 7960
  Placement = pos=(15210,6045,8800) rot=(0,0,1;1.5708rad)
  PredefinedType = 0
  VerticalArea = 3.184e+06
  Width = 200
FEATURE [Part::FeaturePython] Structure295  label="L135"  # Arch/BIM 172 (typed FeaturePython)
  Base = -> Rectangle004
  FaceMaker = 0
  Height = 150
  HorizontalArea = 12611050
  IfcData = attributes={"GlobalId": {"name": "GlobalId", "type": "IfcGloballyUniqueId", "is_enum": false, "enum_values": []}, "Description": {"... (+484 chars omitted),+1 more (map truncated)
  IfcType = 172
  Length = 0
  MoveBase = false
  MoveWithHost = false
  Nodes = (2) [(4057.5,8270,3000),(4057.5,8270,2850)]
  NodesOffset = 0
  Normal = (0,0,-1)
  PerimeterLength = 14330
  Placement = pos=(0,0,6000) rot=(0,0,1;0rad)
  PredefinedType = 0
  VerticalArea = 2149500
  Width = 150
FEATURE [Part::FeaturePython] Structure296  label="L136"  # Arch/BIM 172 (typed FeaturePython)
  Base = -> Rectangle005
  FaceMaker = 0
  Height = 150
  HorizontalArea = 12732700
  IfcData = attributes={"GlobalId": {"name": "GlobalId", "type": "IfcGloballyUniqueId", "is_enum": false, "enum_values": []}, "Description": {"... (+484 chars omitted),+1 more (map truncated)
  IfcType = 172
  Length = 0
  MoveBase = false
  MoveWithHost = false
  Nodes = (2) [(4057.5,4995,3000),(4057.5,4995,2850)]
  NodesOffset = 0
  Normal = (0,0,-1)
  PerimeterLength = 14390
  Placement = pos=(0,0,6000) rot=(0,0,1;0rad)
  PredefinedType = 0
  VerticalArea = 2158500
  Width = 150
FEATURE [Part::FeaturePython] Structure297  label="L137"  # Arch/BIM 172 (typed FeaturePython)
  Base = -> Rectangle006
  FaceMaker = 0
  Height = 150
  HorizontalArea = 1.25705e+07
  IfcData = attributes={"GlobalId": {"name": "GlobalId", "type": "IfcGloballyUniqueId", "is_enum": false, "enum_values": []}, "Description": {"... (+484 chars omitted),+1 more (map truncated)
  IfcType = 172
  Length = 0
  MoveBase = false
  MoveWithHost = false
  Nodes = (2) [(4057.5,1725,3000),(4057.5,1725,2850)]
  NodesOffset = 0
  Normal = (0,0,-1)
  PerimeterLength = 14310
  Placement = pos=(0,0,6000) rot=(0,0,1;0rad)
  PredefinedType = 0
  VerticalArea = 2146500
  Width = 150
FEATURE [Part::FeaturePython] Structure298  label="V15x40 V102a002"  # Arch/BIM 7 (typed FeaturePython)
  FaceMaker = 0
  Height = 400
  HorizontalArea = 405000
  IfcData = attributes={"GlobalId": {"name": "GlobalId", "type": "IfcGloballyUniqueId", "is_enum": false, "enum_values": []}, "Description": {"... (+475 chars omitted),+1 more (map truncated)
  IfcType = 7
  Length = 2700
  MoveBase = false
  MoveWithHost = false
  Nodes = (2) [(-1.72563e-31,-1.42109e-15,-7.77156e-16),(2700,-1.42109e-15,-7.77156e-16)]
  NodesOffset = 0
  Normal = (0,0,0)
  PerimeterLength = 5700
  Placement = pos=(8935,8295,8800) rot=(0,0,1;3.14159rad)
  PredefinedType = 0
  VerticalArea = 2.28e+06
  Width = 150
FEATURE [Part::FeaturePython] Structure299  label="V15x40 V107a002"  # Arch/BIM 7 (typed FeaturePython)
  FaceMaker = 0
  Height = 400
  HorizontalArea = 405000
  IfcData = attributes={"GlobalId": {"name": "GlobalId", "type": "IfcGloballyUniqueId", "is_enum": false, "enum_values": []}, "Description": {"... (+475 chars omitted),+1 more (map truncated)
  IfcType = 7
  Length = 2700
  MoveBase = false
  MoveWithHost = false
  Nodes = (2) [(-1.72563e-31,-1.42109e-15,-7.77156e-16),(2700,-1.42109e-15,-7.77156e-16)]
  NodesOffset = 0
  Normal = (0,0,0)
  PerimeterLength = 5700
  Placement = pos=(8935,4995,8800) rot=(0,0,1;3.14159rad)
  PredefinedType = 0
  VerticalArea = 2.28e+06
  Width = 150
FEATURE [Part::FeaturePython] Structure300  label="V15x40 V112a002"  # Arch/BIM 7 (typed FeaturePython)
  FaceMaker = 0
  Height = 400
  HorizontalArea = 405000
  IfcData = attributes={"GlobalId": {"name": "GlobalId", "type": "IfcGloballyUniqueId", "is_enum": false, "enum_values": []}, "Description": {"... (+475 chars omitted),+1 more (map truncated)
  IfcType = 7
  Length = 2700
  MoveBase = false
  MoveWithHost = false
  Nodes = (2) [(-1.72563e-31,-1.42109e-15,-7.77156e-16),(2700,-1.42109e-15,-7.77156e-16)]
  NodesOffset = 0
  Normal = (0,0,0)
  PerimeterLength = 5700
  Placement = pos=(8935,1700,8800) rot=(0,0,1;3.14159rad)
  PredefinedType = 0
  VerticalArea = 2.28e+06
  Width = 150
FEATURE [Part::FeaturePython] Structure301  label="V15x40 V130a002"  # Arch/BIM 7 (typed FeaturePython)
  FaceMaker = 0
  Height = 400
  HorizontalArea = 370500
  IfcData = attributes={"GlobalId": {"name": "GlobalId", "type": "IfcGloballyUniqueId", "is_enum": false, "enum_values": []}, "Description": {"... (+475 chars omitted),+1 more (map truncated)
  IfcType = 7
  Length = 2470
  MoveBase = false
  MoveWithHost = false
  Nodes = (2) [(-1.72563e-31,-1.42109e-15,-7.77156e-16),(2470,-1.42109e-15,-7.77156e-16)]
  NodesOffset = 0
  Normal = (0,0,0)
  PerimeterLength = 5240
  Placement = pos=(12010,3425,8800) rot=(0,0,1;1.5708rad)
  PredefinedType = 0
  VerticalArea = 2096000
  Width = 150
FEATURE [App::GeometryPython] BuildingPart017  label="Vigas sobre P2"  # Arch/BIM 172 (typed FeaturePython)
  Area = 0
  Group = -> [Structure298,Structure299,Structure300,Structure301,Structure261,Structure262,Structure263,Structure264,Structure265,Structure266,Structure267,Structure268,Structure269,Structure270,Structure271,Structure272,Structure273,Structure274,Structure275,Structure276,Structure277,Structure278,Structure279,Structure280,Structure281,Structure282,Structure283,Structure284,Structure285,Structure286,+8 more]
  Height = 0
  HeightPropagate = true
  IfcData = attributes={"GlobalId": {"name": "GlobalId", "type": "IfcGloballyUniqueId", "is_enum": false, "enum_values": []}, "Description": {"... (+484 chars omitted),+1 more (map truncated)
  IfcType = 172
  LevelOffset = 0
  PredefinedType = 0
FEATURE [Part::FeaturePython] Structure302  label="L138"  # Arch/BIM 172 (typed FeaturePython)
  Base = -> Rectangle014
  FaceMaker = 0
  Height = 150
  HorizontalArea = 3928500
  IfcData = attributes={"GlobalId": {"name": "GlobalId", "type": "IfcGloballyUniqueId", "is_enum": false, "enum_values": []}, "Description": {"... (+484 chars omitted),+1 more (map truncated)
  IfcType = 172
  Length = 0
  MoveBase = false
  MoveWithHost = false
  Nodes = (2) [(7585,9097.5,3000),(7585,9097.5,2850)]
  NodesOffset = 0
  Normal = (0,0,-1)
  PerimeterLength = 8310
  Placement = pos=(0,0,6000) rot=(0,0,1;0rad)
  PredefinedType = 0
  VerticalArea = 1246500
  Width = 150
FEATURE [Part::FeaturePython] Structure303  label="L139"  # Arch/BIM 172 (typed FeaturePython)
  Base = -> Wire
  FaceMaker = 0
  Height = 150
  HorizontalArea = 3.9285e+06
  IfcData = attributes={"GlobalId": {"name": "GlobalId", "type": "IfcGloballyUniqueId", "is_enum": false, "enum_values": []}, "Description": {"... (+484 chars omitted),+1 more (map truncated)
  IfcType = 172
  Length = 0
  MoveBase = false
  MoveWithHost = false
  Nodes = (2) [(7543.76,7449.37,3000),(7543.76,7449.37,2850)]
  NodesOffset = 0
  Normal = (0,0,-1)
  PerimeterLength = 8410
  Placement = pos=(0,0,5850) rot=(0,0,1;0rad)
  PredefinedType = 0
  VerticalArea = 1261500
  Width = 150
FEATURE [Part::FeaturePython] Structure304  label="L140"  # Arch/BIM 172 (typed FeaturePython)
  Base = -> Wire001
  FaceMaker = 0
  Height = 150
  HorizontalArea = 3.90134e+06
  IfcData = attributes={"GlobalId": {"name": "GlobalId", "type": "IfcGloballyUniqueId", "is_enum": false, "enum_values": []}, "Description": {"... (+484 chars omitted),+1 more (map truncated)
  IfcType = 172
  Length = 0
  MoveBase = false
  MoveWithHost = false
  Nodes = (2) [(7543.46,5835.61,3000),(7543.46,5835.61,2850)]
  NodesOffset = 0
  Normal = (0,0,-1)
  PerimeterLength = 8389.89
  Placement = pos=(0,0,5850) rot=(0,0,1;0rad)
  PredefinedType = 0
  VerticalArea = 1.25848e+06
  Width = 150
FEATURE [Part::FeaturePython] Structure305  label="L141"  # Arch/BIM 172 (typed FeaturePython)
  Base = -> Rectangle015
  FaceMaker = 0
  Height = 150
  HorizontalArea = 4.0365e+06
  IfcData = attributes={"GlobalId": {"name": "GlobalId", "type": "IfcGloballyUniqueId", "is_enum": false, "enum_values": []}, "Description": {"... (+484 chars omitted),+1 more (map truncated)
  IfcType = 172
  Length = 0
  MoveBase = false
  MoveWithHost = false
  Nodes = (2) [(7585,4172.5,3000),(7585,4172.5,2850)]
  NodesOffset = 0
  Normal = (0,0,-1)
  PerimeterLength = 8390
  Placement = pos=(0,0,6000) rot=(0,0,1;0rad)
  PredefinedType = 0
  VerticalArea = 1258500
  Width = 150
FEATURE [Part::FeaturePython] Structure306  label="L142"  # Arch/BIM 172 (typed FeaturePython)
  Base = -> Wire002
  FaceMaker = 0
  Height = 150
  HorizontalArea = 3.91484e+06
  IfcData = attributes={"GlobalId": {"name": "GlobalId", "type": "IfcGloballyUniqueId", "is_enum": false, "enum_values": []}, "Description": {"... (+484 chars omitted),+1 more (map truncated)
  IfcType = 172
  Length = 0
  MoveBase = false
  MoveWithHost = false
  Nodes = (2) [(7543.6,2543.13,3000),(7543.6,2543.13,2850)]
  NodesOffset = 0
  Normal = (0,0,-1)
  PerimeterLength = 8399.89
  Placement = pos=(0,0,5850) rot=(0,0,1;0rad)
  PredefinedType = 0
  VerticalArea = 1.25998e+06
  Width = 150
FEATURE [Part::FeaturePython] Structure307  label="L143"  # Arch/BIM 172 (typed FeaturePython)
  Base = -> Rectangle016
  FaceMaker = 0
  Height = 150
  HorizontalArea = 3.915e+06
  IfcData = attributes={"GlobalId": {"name": "GlobalId", "type": "IfcGloballyUniqueId", "is_enum": false, "enum_values": []}, "Description": {"... (+484 chars omitted),+1 more (map truncated)
  IfcType = 172
  Length = 0
  MoveBase = false
  MoveWithHost = false
  Nodes = (2) [(7585,900,3000),(7585,900,2850)]
  NodesOffset = 0
  Normal = (0,0,-1)
  PerimeterLength = 8300
  Placement = pos=(0,0,6000) rot=(0,0,1;0rad)
  PredefinedType = 0
  VerticalArea = 1.245e+06
  Width = 150
FEATURE [Part::FeaturePython] Structure308  label="L144"  # Arch/BIM 172 (typed FeaturePython)
  Base = -> Rectangle008
  FaceMaker = 0
  Height = 150
  HorizontalArea = 4354000
  IfcData = attributes={"GlobalId": {"name": "GlobalId", "type": "IfcGloballyUniqueId", "is_enum": false, "enum_values": []}, "Description": {"... (+484 chars omitted),+1 more (map truncated)
  IfcType = 172
  Length = 0
  MoveBase = false
  MoveWithHost = false
  Nodes = (2) [(9785,8270,3000),(9785,8270,2850)]
  NodesOffset = 0
  Normal = (0,0,-1)
  PerimeterLength = 9020
  Placement = pos=(0,0,6000) rot=(0,0,1;0rad)
  PredefinedType = 0
  VerticalArea = 1353000
  Width = 150
FEATURE [Part::FeaturePython] Structure309  label="L145"  # Arch/BIM 172 (typed FeaturePython)
  Base = -> Rectangle011
  FaceMaker = 0
  Height = 150
  HorizontalArea = 4396000
  IfcData = attributes={"GlobalId": {"name": "GlobalId", "type": "IfcGloballyUniqueId", "is_enum": false, "enum_values": []}, "Description": {"... (+484 chars omitted),+1 more (map truncated)
  IfcType = 172
  Length = 0
  MoveBase = false
  MoveWithHost = false
  Nodes = (2) [(9785,4995,3000),(9785,4995,2850)]
  NodesOffset = 0
  Normal = (0,0,-1)
  PerimeterLength = 9080
  Placement = pos=(0,0,6000) rot=(0,0,1;0rad)
  PredefinedType = 0
  VerticalArea = 1362000
  Width = 150
FEATURE [Part::FeaturePython] Structure310  label="L146"  # Arch/BIM 172 (typed FeaturePython)
  Base = -> Rectangle013
  FaceMaker = 0
  Height = 150
  HorizontalArea = 4.34e+06
  IfcData = attributes={"GlobalId": {"name": "GlobalId", "type": "IfcGloballyUniqueId", "is_enum": false, "enum_values": []}, "Description": {"... (+484 chars omitted),+1 more (map truncated)
  IfcType = 172
  Length = 0
  MoveBase = false
  MoveWithHost = false
  Nodes = (2) [(9785,1725,3000),(9785,1725,2850)]
  NodesOffset = 0
  Normal = (0,0,-1)
  PerimeterLength = 9000
  Placement = pos=(0,0,6000) rot=(0,0,1;0rad)
  PredefinedType = 0
  VerticalArea = 1350000
  Width = 150
FEATURE [Part::FeaturePython] Structure311  label="L147"  # Arch/BIM 172 (typed FeaturePython)
  Base = -> Rectangle009
  FaceMaker = 0
  Height = 150
  HorizontalArea = 1.794e+06
  IfcData = attributes={"GlobalId": {"name": "GlobalId", "type": "IfcGloballyUniqueId", "is_enum": false, "enum_values": []}, "Description": {"... (+484 chars omitted),+1 more (map truncated)
  IfcType = 172
  Length = 0
  MoveBase = false
  MoveWithHost = false
  Nodes = (2) [(11285,9135,3000),(11285,9135,2850)]
  NodesOffset = 0
  Normal = (0,0,-1)
  PerimeterLength = 5360
  Placement = pos=(0,0,6000) rot=(0,0,1;0rad)
  PredefinedType = 0
  VerticalArea = 804000
  Width = 150
FEATURE [Part::FeaturePython] Structure312  label="L148"  # Arch/BIM 172 (typed FeaturePython)
  Base = -> Rectangle018
  FaceMaker = 0
  Height = 150
  HorizontalArea = 3.211e+06
  IfcData = attributes={"GlobalId": {"name": "GlobalId", "type": "IfcGloballyUniqueId", "is_enum": false, "enum_values": []}, "Description": {"... (+484 chars omitted),+1 more (map truncated)
  IfcType = 172
  Length = 0
  MoveBase = false
  MoveWithHost = false
  Nodes = (2) [(11285,4660,3000),(11285,4660,2850)]
  NodesOffset = 0
  Normal = (0,0,-1)
  PerimeterLength = 7540
  Placement = pos=(0,0,6000) rot=(0,0,1;0rad)
  PredefinedType = 0
  VerticalArea = 1.131e+06
  Width = 150
FEATURE [Part::FeaturePython] Structure313  label="L149"  # Arch/BIM 172 (typed FeaturePython)
  Base = -> Rectangle020
  FaceMaker = 0
  Height = 150
  HorizontalArea = 9439500
  IfcData = attributes={"GlobalId": {"name": "GlobalId", "type": "IfcGloballyUniqueId", "is_enum": false, "enum_values": []}, "Description": {"... (+484 chars omitted),+1 more (map truncated)
  IfcType = 172
  Length = 0
  MoveBase = false
  MoveWithHost = false
  Nodes = (2) [(12157.5,1725,3000),(12157.5,1725,2850)]
  NodesOffset = 0
  Normal = (0,0,-1)
  PerimeterLength = 12290
  Placement = pos=(0,0,6000) rot=(0,0,1;0rad)
  PredefinedType = 0
  VerticalArea = 1843500
  Width = 150
FEATURE [Part::FeaturePython] Structure314  label="L150"  # Arch/BIM 172 (typed FeaturePython)
  Base = -> Rectangle019
  FaceMaker = 0
  Height = 150
  HorizontalArea = 3.93965e+06
  IfcData = attributes={"GlobalId": {"name": "GlobalId", "type": "IfcGloballyUniqueId", "is_enum": false, "enum_values": []}, "Description": {"... (+484 chars omitted),+1 more (map truncated)
  IfcType = 172
  Length = 0
  MoveBase = false
  MoveWithHost = false
  Nodes = (2) [(12882.5,4660,3000),(12882.5,4660,2850)]
  NodesOffset = 0
  Normal = (0,0,-1)
  PerimeterLength = 8130
  Placement = pos=(0,0,5850) rot=(0,0,1;0rad)
  PredefinedType = 0
  VerticalArea = 1.2195e+06
  Width = 150
FEATURE [Part::FeaturePython] Structure315  label="L151"  # Arch/BIM 172 (typed FeaturePython)
  Base = -> Rectangle017
  FaceMaker = 0
  Height = 150
  HorizontalArea = 4174500
  IfcData = attributes={"GlobalId": {"name": "GlobalId", "type": "IfcGloballyUniqueId", "is_enum": false, "enum_values": []}, "Description": {"... (+484 chars omitted),+1 more (map truncated)
  IfcType = 172
  Length = 0
  MoveBase = false
  MoveWithHost = false
  Nodes = (2) [(13597.5,9135,3000),(13597.5,9135,2850)]
  NodesOffset = 0
  Normal = (0,0,-1)
  PerimeterLength = 8810
  Placement = pos=(0,0,6000) rot=(0,0,1;0rad)
  PredefinedType = 0
  VerticalArea = 1321500
  Width = 150
FEATURE [App::GeometryPython] BuildingPart018  label="Losas sobre P2"  # Arch/BIM 172 (typed FeaturePython)
  Area = 0
  Group = -> [Structure295,Structure296,Structure297,Structure302,Structure303,Structure304,Structure305,Structure306,Structure307,Structure308,Structure309,Structure310,Structure311,Structure312,Structure313,Structure314,Structure315]
  Height = 0
  HeightPropagate = true
  IfcData = attributes={"GlobalId": {"name": "GlobalId", "type": "IfcGloballyUniqueId", "is_enum": false, "enum_values": []}, "Description": {"... (+484 chars omitted),+1 more (map truncated)
  IfcType = 172
  LevelOffset = 0
  PredefinedType = 0
FEATURE [App::GeometryPython] BuildingPart010  label="Piso 2"  # Arch/BIM 172 (typed FeaturePython)
  Area = 24900000
  Group = -> [BuildingPart016,BuildingPart018,Wall003,BuildingPart017]
  Height = 0
  HeightPropagate = true
  IfcData = attributes={"GlobalId": {"name": "GlobalId", "type": "IfcGloballyUniqueId", "is_enum": false, "enum_values": []}, "Description": {"... (+484 chars omitted),+1 more (map truncated)
  IfcType = 172
  LevelOffset = 0
  Placement = pos=(0,0,6000) rot=(0,0,1;0rad)
  PredefinedType = 0
FEATURE [Part::FeaturePython] Structure316  label="25x15 C064"  # Arch/BIM 24 (typed FeaturePython)
  FaceMaker = 0
  Height = 3000
  HorizontalArea = 37500
  IfcData = attributes={"GlobalId": {"name": "GlobalId", "type": "IfcGloballyUniqueId", "is_enum": false, "enum_values": []}, "Description": {"... (+438 chars omitted),+1 more (map truncated)
  IfcType = 24
  Length = 250
  MoveBase = false
  MoveWithHost = false
  Nodes = (2) [(-1.05471e-15,1.36424e-15,0),(-1.05471e-15,1.36424e-15,3000)]
  NodesOffset = 0
  Normal = (0,0,0)
  PerimeterLength = 800
  Placement = pos=(1930,9900,9000) rot=(0,0,1;0rad)
  PredefinedType = 0
  VerticalArea = 2400000
  Width = 150
FEATURE [Part::FeaturePython] Structure317  label="25x15 C065"  # Arch/BIM 172 (typed FeaturePython)
  FaceMaker = 0
  Height = 3000
  HorizontalArea = 37500
  IfcData = attributes={"GlobalId": {"name": "GlobalId", "type": "IfcGloballyUniqueId", "is_enum": false, "enum_values": []}, "Description": {"... (+484 chars omitted),+1 more (map truncated)
  IfcType = 172
  Length = 250
  MoveBase = false
  MoveWithHost = false
  Nodes = (2) [(-1.05471e-15,1.36424e-15,0),(-1.05471e-15,1.36424e-15,3000)]
  NodesOffset = 0
  Normal = (0,0,0)
  PerimeterLength = 800
  Placement = pos=(1930,100,9000) rot=(0,0,1;0rad)
  PredefinedType = 0
  VerticalArea = 2400000
  Width = 150
FEATURE [Part::FeaturePython] Structure318  label="25x15 C066"  # Arch/BIM 24 (typed FeaturePython)
  FaceMaker = 0
  Height = 3000
  HorizontalArea = 37500
  IfcData = attributes={"GlobalId": {"name": "GlobalId", "type": "IfcGloballyUniqueId", "is_enum": false, "enum_values": []}, "Description": {"... (+438 chars omitted),+1 more (map truncated)
  IfcType = 24
  Length = 250
  MoveBase = false
  MoveWithHost = false
  Nodes = (2) [(-1.05471e-15,1.36424e-15,0),(-1.05471e-15,1.36424e-15,3000)]
  NodesOffset = 0
  Normal = (0,0,0)
  PerimeterLength = 800
  Placement = pos=(6160,6640,9000) rot=(0,0,1;0rad)
  PredefinedType = 0
  VerticalArea = 2400000
  Width = 150
FEATURE [Part::FeaturePython] Structure319  label="25x15 C067"  # Arch/BIM 24 (typed FeaturePython)
  FaceMaker = 0
  Height = 3000
  HorizontalArea = 37500
  IfcData = attributes={"GlobalId": {"name": "GlobalId", "type": "IfcGloballyUniqueId", "is_enum": false, "enum_values": []}, "Description": {"... (+438 chars omitted),+1 more (map truncated)
  IfcType = 24
  Length = 250
  MoveBase = false
  MoveWithHost = false
  Nodes = (2) [(-1.05471e-15,1.36424e-15,0),(-1.05471e-15,1.36424e-15,3000)]
  NodesOffset = 0
  Normal = (0,0,0)
  PerimeterLength = 800
  Placement = pos=(6160,3350,9000) rot=(0,0,1;0rad)
  PredefinedType = 0
  VerticalArea = 2400000
  Width = 150
FEATURE [Part::FeaturePython] Structure320  label="25x15 C068"  # Arch/BIM 24 (typed FeaturePython)
  FaceMaker = 0
  Height = 3000
  HorizontalArea = 37500
  IfcData = attributes={"GlobalId": {"name": "GlobalId", "type": "IfcGloballyUniqueId", "is_enum": false, "enum_values": []}, "Description": {"... (+438 chars omitted),+1 more (map truncated)
  IfcType = 24
  Length = 250
  MoveBase = false
  MoveWithHost = false
  Nodes = (2) [(-1.05471e-15,1.36424e-15,0),(-1.05471e-15,1.36424e-15,3000)]
  NodesOffset = 0
  Normal = (0,0,0)
  PerimeterLength = 800
  Placement = pos=(6160,100,9000) rot=(0,0,1;0rad)
  PredefinedType = 0
  VerticalArea = 2400000
  Width = 150
FEATURE [Part::FeaturePython] Structure321  label="25x15 C069"  # Arch/BIM 24 (typed FeaturePython)
  FaceMaker = 0
  Height = 3000
  HorizontalArea = 37500
  IfcData = attributes={"GlobalId": {"name": "GlobalId", "type": "IfcGloballyUniqueId", "is_enum": false, "enum_values": []}, "Description": {"... (+438 chars omitted),+1 more (map truncated)
  IfcType = 24
  Length = 250
  MoveBase = false
  MoveWithHost = false
  Nodes = (2) [(-1.05471e-15,1.36424e-15,0),(-1.05471e-15,1.36424e-15,3000)]
  NodesOffset = 0
  Normal = (0,0,0)
  PerimeterLength = 800
  Placement = pos=(9010,100,9000) rot=(0,0,1;0rad)
  PredefinedType = 0
  VerticalArea = 2400000
  Width = 150
FEATURE [Part::FeaturePython] Structure322  label="25x15 C070"  # Arch/BIM 24 (typed FeaturePython)
  FaceMaker = 0
  Height = 3000
  HorizontalArea = 37500
  IfcData = attributes={"GlobalId": {"name": "GlobalId", "type": "IfcGloballyUniqueId", "is_enum": false, "enum_values": []}, "Description": {"... (+438 chars omitted),+1 more (map truncated)
  IfcType = 24
  Length = 250
  MoveBase = false
  MoveWithHost = false
  Nodes = (2) [(-1.05471e-15,1.36424e-15,0),(-1.05471e-15,1.36424e-15,3000)]
  NodesOffset = 0
  Normal = (0,0,0)
  PerimeterLength = 800
  Placement = pos=(10560,100,9000) rot=(0,0,1;0rad)
  PredefinedType = 0
  VerticalArea = 2400000
  Width = 150
FEATURE [Part::FeaturePython] Structure323  label="25x15 C071"  # Arch/BIM 24 (typed FeaturePython)
  FaceMaker = 0
  Height = 3000
  HorizontalArea = 37500
  IfcData = attributes={"GlobalId": {"name": "GlobalId", "type": "IfcGloballyUniqueId", "is_enum": false, "enum_values": []}, "Description": {"... (+438 chars omitted),+1 more (map truncated)
  IfcType = 24
  Length = 250
  MoveBase = false
  MoveWithHost = false
  Nodes = (2) [(-1.05471e-15,1.36424e-15,0),(-1.05471e-15,1.36424e-15,3000)]
  NodesOffset = 0
  Normal = (0,0,0)
  PerimeterLength = 800
  Placement = pos=(13780,100,9000) rot=(0,0,1;0rad)
  PredefinedType = 0
  VerticalArea = 2400000
  Width = 150
FEATURE [Part::FeaturePython] Structure324  label="25x15 C072"  # Arch/BIM 24 (typed FeaturePython)
  FaceMaker = 0
  Height = 3000
  HorizontalArea = 37500
  IfcData = attributes={"GlobalId": {"name": "GlobalId", "type": "IfcGloballyUniqueId", "is_enum": false, "enum_values": []}, "Description": {"... (+438 chars omitted),+1 more (map truncated)
  IfcType = 24
  Length = 250
  MoveBase = false
  MoveWithHost = false
  Nodes = (2) [(-1.05471e-15,1.36424e-15,0),(-1.05471e-15,1.36424e-15,3000)]
  NodesOffset = 0
  Normal = (0,0,0)
  PerimeterLength = 800
  Placement = pos=(15210,5970,9000) rot=(0,0,1;0rad)
  PredefinedType = 0
  VerticalArea = 2400000
  Width = 150
FEATURE [Part::FeaturePython] Structure325  label="25x15 C073"  # Arch/BIM 24 (typed FeaturePython)
  FaceMaker = 0
  Height = 3000
  HorizontalArea = 37500
  IfcData = attributes={"GlobalId": {"name": "GlobalId", "type": "IfcGloballyUniqueId", "is_enum": false, "enum_values": []}, "Description": {"... (+438 chars omitted),+1 more (map truncated)
  IfcType = 24
  Length = 250
  MoveBase = false
  MoveWithHost = false
  Nodes = (2) [(-1.05471e-15,1.36424e-15,0),(-1.05471e-15,1.36424e-15,3000)]
  NodesOffset = 0
  Normal = (0,0,0)
  PerimeterLength = 800
  Placement = pos=(13780,5970,9000) rot=(0,0,1;0rad)
  PredefinedType = 0
  VerticalArea = 2400000
  Width = 150
FEATURE [Part::FeaturePython] Structure326  label="25x15 C074"  # Arch/BIM 172 (typed FeaturePython)
  FaceMaker = 0
  Height = 3000
  HorizontalArea = 37500
  IfcData = attributes={"GlobalId": {"name": "GlobalId", "type": "IfcGloballyUniqueId", "is_enum": false, "enum_values": []}, "Description": {"... (+484 chars omitted),+1 more (map truncated)
  IfcType = 172
  Length = 250
  MoveBase = false
  MoveWithHost = false
  Nodes = (2) [(-1.05471e-15,1.36424e-15,0),(-1.05471e-15,1.36424e-15,3000)]
  NodesOffset = 0
  Normal = (0,0,0)
  PerimeterLength = 800
  Placement = pos=(1930,9900,9000) rot=(0,0,1;0rad)
  PredefinedType = 0
  VerticalArea = 2400000
  Width = 150
FEATURE [Part::FeaturePython] Structure327  label="25x15 C075"  # Arch/BIM 172 (typed FeaturePython)
  FaceMaker = 0
  Height = 3000
  HorizontalArea = 37500
  IfcData = attributes={"GlobalId": {"name": "GlobalId", "type": "IfcGloballyUniqueId", "is_enum": false, "enum_values": []}, "Description": {"... (+484 chars omitted),+1 more (map truncated)
  IfcType = 172
  Length = 250
  MoveBase = false
  MoveWithHost = false
  Nodes = (2) [(-1.05471e-15,1.36424e-15,0),(-1.05471e-15,1.36424e-15,3000)]
  NodesOffset = 0
  Normal = (0,0,0)
  PerimeterLength = 800
  Placement = pos=(9010,6640,9000) rot=(0,0,1;1.5708rad)
  PredefinedType = 0
  VerticalArea = 2400000
  Width = 150
FEATURE [Part::FeaturePython] Structure328  label="25x15 C076"  # Arch/BIM 172 (typed FeaturePython)
  FaceMaker = 0
  Height = 3000
  HorizontalArea = 37500
  IfcData = attributes={"GlobalId": {"name": "GlobalId", "type": "IfcGloballyUniqueId", "is_enum": false, "enum_values": []}, "Description": {"... (+484 chars omitted),+1 more (map truncated)
  IfcType = 172
  Length = 250
  MoveBase = false
  MoveWithHost = false
  Nodes = (2) [(-1.05471e-15,1.36424e-15,0),(-1.05471e-15,1.36424e-15,3000)]
  NodesOffset = 0
  Normal = (0,0,0)
  PerimeterLength = 800
  Placement = pos=(9010,3350,9000) rot=(0,0,1;1.5708rad)
  PredefinedType = 0
  VerticalArea = 2400000
  Width = 150
FEATURE [Part::FeaturePython] Structure329  label="25x15 C077"  # Arch/BIM 172 (typed FeaturePython)
  FaceMaker = 0
  Height = 3000
  HorizontalArea = 37500
  IfcData = attributes={"GlobalId": {"name": "GlobalId", "type": "IfcGloballyUniqueId", "is_enum": false, "enum_values": []}, "Description": {"... (+484 chars omitted),+1 more (map truncated)
  IfcType = 172
  Length = 250
  MoveBase = false
  MoveWithHost = false
  Nodes = (2) [(-1.05471e-15,1.36424e-15,0),(-1.05471e-15,1.36424e-15,3000)]
  NodesOffset = 0
  Normal = (0,0,0)
  PerimeterLength = 800
  Placement = pos=(10560,3350,9000) rot=(0,0,1;1.5708rad)
  PredefinedType = 0
  VerticalArea = 2400000
  Width = 150
FEATURE [Part::FeaturePython] Structure330  label="25x15 C078"  # Arch/BIM 172 (typed FeaturePython)
  FaceMaker = 0
  Height = 3000
  HorizontalArea = 37500
  IfcData = attributes={"GlobalId": {"name": "GlobalId", "type": "IfcGloballyUniqueId", "is_enum": false, "enum_values": []}, "Description": {"... (+484 chars omitted),+1 more (map truncated)
  IfcType = 172
  Length = 250
  MoveBase = false
  MoveWithHost = false
  Nodes = (2) [(-1.05471e-15,1.36424e-15,0),(-1.05471e-15,1.36424e-15,3000)]
  NodesOffset = 0
  Normal = (0,0,0)
  PerimeterLength = 800
  Placement = pos=(13780,3350,9000) rot=(0,0,1;1.5708rad)
  PredefinedType = 0
  VerticalArea = 2400000
  Width = 150
FEATURE [Part::FeaturePython] Structure331  label="25x15 C079"  # Arch/BIM 172 (typed FeaturePython)
  FaceMaker = 0
  Height = 3000
  HorizontalArea = 37500
  IfcData = attributes={"GlobalId": {"name": "GlobalId", "type": "IfcGloballyUniqueId", "is_enum": false, "enum_values": []}, "Description": {"... (+484 chars omitted),+1 more (map truncated)
  IfcType = 172
  Length = 250
  MoveBase = false
  MoveWithHost = false
  Nodes = (2) [(-1.05471e-15,1.36424e-15,0),(-1.05471e-15,1.36424e-15,3000)]
  NodesOffset = 0
  Normal = (0,0,0)
  PerimeterLength = 800
  Placement = pos=(9010,9900,9000) rot=(0,0,1;0rad)
  PredefinedType = 0
  VerticalArea = 2400000
  Width = 150
FEATURE [Part::FeaturePython] Structure332  label="25x15 C080"  # Arch/BIM 172 (typed FeaturePython)
  FaceMaker = 0
  Height = 3000
  HorizontalArea = 37500
  IfcData = attributes={"GlobalId": {"name": "GlobalId", "type": "IfcGloballyUniqueId", "is_enum": false, "enum_values": []}, "Description": {"... (+484 chars omitted),+1 more (map truncated)
  IfcType = 172
  Length = 250
  MoveBase = false
  MoveWithHost = false
  Nodes = (2) [(-1.05471e-15,1.36424e-15,0),(-1.05471e-15,1.36424e-15,3000)]
  NodesOffset = 0
  Normal = (0,0,0)
  PerimeterLength = 800
  Placement = pos=(6160,9900,9000) rot=(0,0,1;0rad)
  PredefinedType = 0
  VerticalArea = 2400000
  Width = 150
FEATURE [Part::FeaturePython] Structure333  label="25x15 C081"  # Arch/BIM 172 (typed FeaturePython)
  FaceMaker = 0
  Height = 3000
  HorizontalArea = 37500
  IfcData = attributes={"GlobalId": {"name": "GlobalId", "type": "IfcGloballyUniqueId", "is_enum": false, "enum_values": []}, "Description": {"... (+484 chars omitted),+1 more (map truncated)
  IfcType = 172
  Length = 250
  MoveBase = false
  MoveWithHost = false
  Nodes = (2) [(-1.05471e-15,1.36424e-15,0),(-1.05471e-15,1.36424e-15,3000)]
  NodesOffset = 0
  Normal = (0,0,0)
  PerimeterLength = 800
  Placement = pos=(12010,9900,9000) rot=(0,0,1;0rad)
  PredefinedType = 0
  VerticalArea = 2400000
  Width = 150
FEATURE [Part::FeaturePython] Structure334  label="25x15 C082"  # Arch/BIM 172 (typed FeaturePython)
  FaceMaker = 0
  Height = 3000
  HorizontalArea = 37500
  IfcData = attributes={"GlobalId": {"name": "GlobalId", "type": "IfcGloballyUniqueId", "is_enum": false, "enum_values": []}, "Description": {"... (+484 chars omitted),+1 more (map truncated)
  IfcType = 172
  Length = 250
  MoveBase = false
  MoveWithHost = false
  Nodes = (2) [(-1.05471e-15,1.36424e-15,0),(-1.05471e-15,1.36424e-15,3000)]
  NodesOffset = 0
  Normal = (0,0,0)
  PerimeterLength = 800
  Placement = pos=(15210,9900,9000) rot=(0,0,1;0rad)
  PredefinedType = 0
  VerticalArea = 2400000
  Width = 150
FEATURE [Part::FeaturePython] Structure335  label="25x20 C012"  # Arch/BIM 24 (typed FeaturePython)
  FaceMaker = 0
  Height = 3000
  HorizontalArea = 50000
  IfcData = attributes={"GlobalId": {"name": "GlobalId", "type": "IfcGloballyUniqueId", "is_enum": false, "enum_values": []}, "Description": {"... (+438 chars omitted),+1 more (map truncated)
  IfcType = 24
  Length = 250
  MoveBase = false
  MoveWithHost = false
  Nodes = (2) [(-1.05471e-15,-1.81899e-15,0),(-1.05471e-15,-1.81899e-15,3000)]
  NodesOffset = 0
  Normal = (0,0,0)
  PerimeterLength = 900
  Placement = pos=(1930,6640,9000) rot=(0,0,1;0rad)
  PredefinedType = 0
  VerticalArea = 2700000
  Width = 200
FEATURE [Part::FeaturePython] Structure336  label="25x20 C013"  # Arch/BIM 172 (typed FeaturePython)
  FaceMaker = 0
  Height = 3000
  HorizontalArea = 50000
  IfcData = attributes={"GlobalId": {"name": "GlobalId", "type": "IfcGloballyUniqueId", "is_enum": false, "enum_values": []}, "Description": {"... (+484 chars omitted),+1 more (map truncated)
  IfcType = 172
  Length = 250
  MoveBase = false
  MoveWithHost = false
  Nodes = (2) [(-1.05471e-15,-1.81899e-15,0),(-1.05471e-15,-1.81899e-15,3000)]
  NodesOffset = 0
  Normal = (0,0,0)
  PerimeterLength = 900
  Placement = pos=(1930,3350,9000) rot=(0,0,1;0rad)
  PredefinedType = 0
  VerticalArea = 2700000
  Width = 200
FEATURE [App::GeometryPython] BuildingPart020  label="Columnas sobre P3"  # Arch/BIM 172 (typed FeaturePython)
  Area = 0
  Group = -> [Structure316,Structure317,Structure318,Structure319,Structure320,Structure321,Structure322,Structure323,Structure324,Structure325,Structure326,Structure327,Structure328,Structure329,Structure330,Structure331,Structure332,Structure333,Structure334,Structure335,Structure336]
  Height = 0
  HeightPropagate = true
  IfcData = attributes={"GlobalId": {"name": "GlobalId", "type": "IfcGloballyUniqueId", "is_enum": false, "enum_values": []}, "Description": {"... (+484 chars omitted),+1 more (map truncated)
  IfcType = 172
  LevelOffset = 0
  PredefinedType = 0
FEATURE [Part::FeaturePython] Structure337  label="L152"  # Arch/BIM 172 (typed FeaturePython)
  Base = -> Rectangle004
  FaceMaker = 0
  Height = 150
  HorizontalArea = 12611050
  IfcData = attributes={"GlobalId": {"name": "GlobalId", "type": "IfcGloballyUniqueId", "is_enum": false, "enum_values": []}, "Description": {"... (+484 chars omitted),+1 more (map truncated)
  IfcType = 172
  Length = 0
  MoveBase = false
  MoveWithHost = false
  Nodes = (2) [(4057.5,8270,3000),(4057.5,8270,2850)]
  NodesOffset = 0
  Normal = (0,0,-1)
  PerimeterLength = 14330
  Placement = pos=(0,0,9000) rot=(0,0,1;0rad)
  PredefinedType = 0
  VerticalArea = 2149500
  Width = 150
FEATURE [Part::FeaturePython] Structure338  label="L153"  # Arch/BIM 172 (typed FeaturePython)
  Base = -> Rectangle005
  FaceMaker = 0
  Height = 150
  HorizontalArea = 12732700
  IfcData = attributes={"GlobalId": {"name": "GlobalId", "type": "IfcGloballyUniqueId", "is_enum": false, "enum_values": []}, "Description": {"... (+484 chars omitted),+1 more (map truncated)
  IfcType = 172
  Length = 0
  MoveBase = false
  MoveWithHost = false
  Nodes = (2) [(4057.5,4995,3000),(4057.5,4995,2850)]
  NodesOffset = 0
  Normal = (0,0,-1)
  PerimeterLength = 14390
  Placement = pos=(0,0,9000) rot=(0,0,1;0rad)
  PredefinedType = 0
  VerticalArea = 2158500
  Width = 150
FEATURE [Part::FeaturePython] Structure339  label="L154"  # Arch/BIM 172 (typed FeaturePython)
  Base = -> Rectangle006
  FaceMaker = 0
  Height = 150
  HorizontalArea = 1.25705e+07
  IfcData = attributes={"GlobalId": {"name": "GlobalId", "type": "IfcGloballyUniqueId", "is_enum": false, "enum_values": []}, "Description": {"... (+484 chars omitted),+1 more (map truncated)
  IfcType = 172
  Length = 0
  MoveBase = false
  MoveWithHost = false
  Nodes = (2) [(4057.5,1725,3000),(4057.5,1725,2850)]
  NodesOffset = 0
  Normal = (0,0,-1)
  PerimeterLength = 14310
  Placement = pos=(0,0,9000) rot=(0,0,1;0rad)
  PredefinedType = 0
  VerticalArea = 2146500
  Width = 150
FEATURE [Part::FeaturePython] Structure340  label="L155"  # Arch/BIM 172 (typed FeaturePython)
  Base = -> Rectangle014
  FaceMaker = 0
  Height = 150
  HorizontalArea = 3928500
  IfcData = attributes={"GlobalId": {"name": "GlobalId", "type": "IfcGloballyUniqueId", "is_enum": false, "enum_values": []}, "Description": {"... (+484 chars omitted),+1 more (map truncated)
  IfcType = 172
  Length = 0
  MoveBase = false
  MoveWithHost = false
  Nodes = (2) [(7585,9097.5,3000),(7585,9097.5,2850)]
  NodesOffset = 0
  Normal = (0,0,-1)
  PerimeterLength = 8310
  Placement = pos=(0,0,9000) rot=(0,0,1;0rad)
  PredefinedType = 0
  VerticalArea = 1246500
  Width = 150
FEATURE [Part::FeaturePython] Structure341  label="L156"  # Arch/BIM 172 (typed FeaturePython)
  Base = -> Wire
  FaceMaker = 0
  Height = 150
  HorizontalArea = 3.9285e+06
  IfcData = attributes={"GlobalId": {"name": "GlobalId", "type": "IfcGloballyUniqueId", "is_enum": false, "enum_values": []}, "Description": {"... (+484 chars omitted),+1 more (map truncated)
  IfcType = 172
  Length = 0
  MoveBase = false
  MoveWithHost = false
  Nodes = (2) [(7543.76,7449.37,3000),(7543.76,7449.37,2850)]
  NodesOffset = 0
  Normal = (0,0,-1)
  PerimeterLength = 8410
  Placement = pos=(0,0,8850) rot=(0,0,1;0rad)
  PredefinedType = 0
  VerticalArea = 1261500
  Width = 150
FEATURE [Part::FeaturePython] Structure342  label="L157"  # Arch/BIM 172 (typed FeaturePython)
  Base = -> Wire001
  FaceMaker = 0
  Height = 150
  HorizontalArea = 3.90134e+06
  IfcData = attributes={"GlobalId": {"name": "GlobalId", "type": "IfcGloballyUniqueId", "is_enum": false, "enum_values": []}, "Description": {"... (+484 chars omitted),+1 more (map truncated)
  IfcType = 172
  Length = 0
  MoveBase = false
  MoveWithHost = false
  Nodes = (2) [(7543.46,5835.61,3000),(7543.46,5835.61,2850)]
  NodesOffset = 0
  Normal = (0,0,-1)
  PerimeterLength = 8389.89
  Placement = pos=(0,0,8850) rot=(0,0,1;0rad)
  PredefinedType = 0
  VerticalArea = 1.25848e+06
  Width = 150
FEATURE [Part::FeaturePython] Structure343  label="L158"  # Arch/BIM 172 (typed FeaturePython)
  Base = -> Rectangle015
  FaceMaker = 0
  Height = 150
  HorizontalArea = 4.0365e+06
  IfcData = attributes={"GlobalId": {"name": "GlobalId", "type": "IfcGloballyUniqueId", "is_enum": false, "enum_values": []}, "Description": {"... (+484 chars omitted),+1 more (map truncated)
  IfcType = 172
  Length = 0
  MoveBase = false
  MoveWithHost = false
  Nodes = (2) [(7585,4172.5,3000),(7585,4172.5,2850)]
  NodesOffset = 0
  Normal = (0,0,-1)
  PerimeterLength = 8390
  Placement = pos=(0,0,9000) rot=(0,0,1;0rad)
  PredefinedType = 0
  VerticalArea = 1258500
  Width = 150
FEATURE [Part::FeaturePython] Structure344  label="L159"  # Arch/BIM 172 (typed FeaturePython)
  Base = -> Wire002
  FaceMaker = 0
  Height = 150
  HorizontalArea = 3.91484e+06
  IfcData = attributes={"GlobalId": {"name": "GlobalId", "type": "IfcGloballyUniqueId", "is_enum": false, "enum_values": []}, "Description": {"... (+484 chars omitted),+1 more (map truncated)
  IfcType = 172
  Length = 0
  MoveBase = false
  MoveWithHost = false
  Nodes = (2) [(7543.6,2543.13,3000),(7543.6,2543.13,2850)]
  NodesOffset = 0
  Normal = (0,0,-1)
  PerimeterLength = 8399.89
  Placement = pos=(0,0,8850) rot=(0,0,1;0rad)
  PredefinedType = 0
  VerticalArea = 1.25998e+06
  Width = 150
FEATURE [Part::FeaturePython] Structure345  label="L160"  # Arch/BIM 172 (typed FeaturePython)
  Base = -> Rectangle016
  FaceMaker = 0
  Height = 150
  HorizontalArea = 3.915e+06
  IfcData = attributes={"GlobalId": {"name": "GlobalId", "type": "IfcGloballyUniqueId", "is_enum": false, "enum_values": []}, "Description": {"... (+484 chars omitted),+1 more (map truncated)
  IfcType = 172
  Length = 0
  MoveBase = false
  MoveWithHost = false
  Nodes = (2) [(7585,900,3000),(7585,900,2850)]
  NodesOffset = 0
  Normal = (0,0,-1)
  PerimeterLength = 8300
  Placement = pos=(0,0,9000) rot=(0,0,1;0rad)
  PredefinedType = 0
  VerticalArea = 1.245e+06
  Width = 150
FEATURE [Part::FeaturePython] Structure346  label="L161"  # Arch/BIM 172 (typed FeaturePython)
  Base = -> Rectangle008
  FaceMaker = 0
  Height = 150
  HorizontalArea = 4354000
  IfcData = attributes={"GlobalId": {"name": "GlobalId", "type": "IfcGloballyUniqueId", "is_enum": false, "enum_values": []}, "Description": {"... (+484 chars omitted),+1 more (map truncated)
  IfcType = 172
  Length = 0
  MoveBase = false
  MoveWithHost = false
  Nodes = (2) [(9785,8270,3000),(9785,8270,2850)]
  NodesOffset = 0
  Normal = (0,0,-1)
  PerimeterLength = 9020
  Placement = pos=(0,0,9000) rot=(0,0,1;0rad)
  PredefinedType = 0
  VerticalArea = 1353000
  Width = 150
FEATURE [Part::FeaturePython] Structure347  label="L162"  # Arch/BIM 172 (typed FeaturePython)
  Base = -> Rectangle011
  FaceMaker = 0
  Height = 150
  HorizontalArea = 4396000
  IfcData = attributes={"GlobalId": {"name": "GlobalId", "type": "IfcGloballyUniqueId", "is_enum": false, "enum_values": []}, "Description": {"... (+484 chars omitted),+1 more (map truncated)
  IfcType = 172
  Length = 0
  MoveBase = false
  MoveWithHost = false
  Nodes = (2) [(9785,4995,3000),(9785,4995,2850)]
  NodesOffset = 0
  Normal = (0,0,-1)
  PerimeterLength = 9080
  Placement = pos=(0,0,9000) rot=(0,0,1;0rad)
  PredefinedType = 0
  VerticalArea = 1362000
  Width = 150
FEATURE [Part::FeaturePython] Structure348  label="L163"  # Arch/BIM 172 (typed FeaturePython)
  Base = -> Rectangle013
  FaceMaker = 0
  Height = 150
  HorizontalArea = 4.34e+06
  IfcData = attributes={"GlobalId": {"name": "GlobalId", "type": "IfcGloballyUniqueId", "is_enum": false, "enum_values": []}, "Description": {"... (+484 chars omitted),+1 more (map truncated)
  IfcType = 172
  Length = 0
  MoveBase = false
  MoveWithHost = false
  Nodes = (2) [(9785,1725,3000),(9785,1725,2850)]
  NodesOffset = 0
  Normal = (0,0,-1)
  PerimeterLength = 9000
  Placement = pos=(0,0,9000) rot=(0,0,1;0rad)
  PredefinedType = 0
  VerticalArea = 1350000
  Width = 150
FEATURE [Part::FeaturePython] Structure349  label="L164"  # Arch/BIM 172 (typed FeaturePython)
  Base = -> Rectangle009
  FaceMaker = 0
  Height = 150
  HorizontalArea = 1.794e+06
  IfcData = attributes={"GlobalId": {"name": "GlobalId", "type": "IfcGloballyUniqueId", "is_enum": false, "enum_values": []}, "Description": {"... (+484 chars omitted),+1 more (map truncated)
  IfcType = 172
  Length = 0
  MoveBase = false
  MoveWithHost = false
  Nodes = (2) [(11285,9135,3000),(11285,9135,2850)]
  NodesOffset = 0
  Normal = (0,0,-1)
  PerimeterLength = 5360
  Placement = pos=(0,0,9000) rot=(0,0,1;0rad)
  PredefinedType = 0
  VerticalArea = 804000
  Width = 150
FEATURE [Part::FeaturePython] Structure350  label="L165"  # Arch/BIM 172 (typed FeaturePython)
  Base = -> Rectangle018
  FaceMaker = 0
  Height = 150
  HorizontalArea = 3.211e+06
  IfcData = attributes={"GlobalId": {"name": "GlobalId", "type": "IfcGloballyUniqueId", "is_enum": false, "enum_values": []}, "Description": {"... (+484 chars omitted),+1 more (map truncated)
  IfcType = 172
  Length = 0
  MoveBase = false
  MoveWithHost = false
  Nodes = (2) [(11285,4660,3000),(11285,4660,2850)]
  NodesOffset = 0
  Normal = (0,0,-1)
  PerimeterLength = 7540
  Placement = pos=(0,0,9000) rot=(0,0,1;0rad)
  PredefinedType = 0
  VerticalArea = 1.131e+06
  Width = 150
FEATURE [Part::FeaturePython] Structure351  label="L166"  # Arch/BIM 172 (typed FeaturePython)
  Base = -> Rectangle020
  FaceMaker = 0
  Height = 150
  HorizontalArea = 9439500
  IfcData = attributes={"GlobalId": {"name": "GlobalId", "type": "IfcGloballyUniqueId", "is_enum": false, "enum_values": []}, "Description": {"... (+484 chars omitted),+1 more (map truncated)
  IfcType = 172
  Length = 0
  MoveBase = false
  MoveWithHost = false
  Nodes = (2) [(12157.5,1725,3000),(12157.5,1725,2850)]
  NodesOffset = 0
  Normal = (0,0,-1)
  PerimeterLength = 12290
  Placement = pos=(0,0,9000) rot=(0,0,1;0rad)
  PredefinedType = 0
  VerticalArea = 1843500
  Width = 150
FEATURE [Part::FeaturePython] Structure352  label="L167"  # Arch/BIM 172 (typed FeaturePython)
  Base = -> Rectangle019
  FaceMaker = 0
  Height = 150
  HorizontalArea = 3.93965e+06
  IfcData = attributes={"GlobalId": {"name": "GlobalId", "type": "IfcGloballyUniqueId", "is_enum": false, "enum_values": []}, "Description": {"... (+484 chars omitted),+1 more (map truncated)
  IfcType = 172
  Length = 0
  MoveBase = false
  MoveWithHost = false
  Nodes = (2) [(12882.5,4660,3000),(12882.5,4660,2850)]
  NodesOffset = 0
  Normal = (0,0,-1)
  PerimeterLength = 8130
  Placement = pos=(0,0,8850) rot=(0,0,1;0rad)
  PredefinedType = 0
  VerticalArea = 1.2195e+06
  Width = 150
FEATURE [Part::FeaturePython] Structure353  label="L168"  # Arch/BIM 172 (typed FeaturePython)
  Base = -> Rectangle017
  FaceMaker = 0
  Height = 150
  HorizontalArea = 4174500
  IfcData = attributes={"GlobalId": {"name": "GlobalId", "type": "IfcGloballyUniqueId", "is_enum": false, "enum_values": []}, "Description": {"... (+484 chars omitted),+1 more (map truncated)
  IfcType = 172
  Length = 0
  MoveBase = false
  MoveWithHost = false
  Nodes = (2) [(13597.5,9135,3000),(13597.5,9135,2850)]
  NodesOffset = 0
  Normal = (0,0,-1)
  PerimeterLength = 8810
  Placement = pos=(0,0,9000) rot=(0,0,1;0rad)
  PredefinedType = 0
  VerticalArea = 1321500
  Width = 150
FEATURE [App::GeometryPython] BuildingPart021  label="Losas sobre P3"  # Arch/BIM 172 (typed FeaturePython)
  Area = 0
  Group = -> [Structure337,Structure338,Structure339,Structure340,Structure341,Structure342,Structure343,Structure344,Structure345,Structure346,Structure347,Structure348,Structure349,Structure350,Structure351,Structure352,Structure353]
  Height = 0
  HeightPropagate = true
  IfcData = attributes={"GlobalId": {"name": "GlobalId", "type": "IfcGloballyUniqueId", "is_enum": false, "enum_values": []}, "Description": {"... (+484 chars omitted),+1 more (map truncated)
  IfcType = 172
  LevelOffset = 0
  PredefinedType = 0
FEATURE [Part::FeaturePython] Wall004  label="Tabique Ascensor P3"  # Arch/BIM 166 (typed FeaturePython)
  Align = 1
  Area = 24900000
  Base = -> Rectangle003
  BlockHeight = 0
  BlockLength = 0
  CountBroken = 0
  CountEntire = 0
  Face = 0
  Height = 3000
  HorizontalArea = 1155000
  IfcData = attributes={"GlobalId": {"name": "GlobalId", "type": "IfcGloballyUniqueId", "is_enum": false, "enum_values": []}, "Description": {"... (+533 chars omitted),+1 more (map truncated)
  IfcType = 166
  Joint = 0
  Length = 8300
  MakeBlocks = false
  MoveBase = false
  MoveWithHost = false
  Normal = (0,0,0)
  OffsetFirst = 0
  OffsetSecond = 0
  PerimeterLength = 8300
  Placement = pos=(0,0,9000) rot=(0,0,1;0rad)
  PredefinedType = 0
  VerticalArea = 46200000
  Width = 150
FEATURE [Part::FeaturePython] Structure354  label="V15x40 V102a003"  # Arch/BIM 7 (typed FeaturePython)
  FaceMaker = 0
  Height = 400
  HorizontalArea = 405000
  IfcData = attributes={"GlobalId": {"name": "GlobalId", "type": "IfcGloballyUniqueId", "is_enum": false, "enum_values": []}, "Description": {"... (+475 chars omitted),+1 more (map truncated)
  IfcType = 7
  Length = 2700
  MoveBase = false
  MoveWithHost = false
  Nodes = (2) [(-1.72563e-31,-1.42109e-15,-7.77156e-16),(2700,-1.42109e-15,-7.77156e-16)]
  NodesOffset = 0
  Normal = (0,0,0)
  PerimeterLength = 5700
  Placement = pos=(8935,8295,11800) rot=(0,0,1;3.14159rad)
  PredefinedType = 0
  VerticalArea = 2.28e+06
  Width = 150
FEATURE [Part::FeaturePython] Structure355  label="V15x40 V107a003"  # Arch/BIM 7 (typed FeaturePython)
  FaceMaker = 0
  Height = 400
  HorizontalArea = 405000
  IfcData = attributes={"GlobalId": {"name": "GlobalId", "type": "IfcGloballyUniqueId", "is_enum": false, "enum_values": []}, "Description": {"... (+475 chars omitted),+1 more (map truncated)
  IfcType = 7
  Length = 2700
  MoveBase = false
  MoveWithHost = false
  Nodes = (2) [(-1.72563e-31,-1.42109e-15,-7.77156e-16),(2700,-1.42109e-15,-7.77156e-16)]
  NodesOffset = 0
  Normal = (0,0,0)
  PerimeterLength = 5700
  Placement = pos=(8935,4995,11800) rot=(0,0,1;3.14159rad)
  PredefinedType = 0
  VerticalArea = 2.28e+06
  Width = 150
FEATURE [Part::FeaturePython] Structure356  label="V15x40 V112a003"  # Arch/BIM 7 (typed FeaturePython)
  FaceMaker = 0
  Height = 400
  HorizontalArea = 405000
  IfcData = attributes={"GlobalId": {"name": "GlobalId", "type": "IfcGloballyUniqueId", "is_enum": false, "enum_values": []}, "Description": {"... (+475 chars omitted),+1 more (map truncated)
  IfcType = 7
  Length = 2700
  MoveBase = false
  MoveWithHost = false
  Nodes = (2) [(-1.72563e-31,-1.42109e-15,-7.77156e-16),(2700,-1.42109e-15,-7.77156e-16)]
  NodesOffset = 0
  Normal = (0,0,0)
  PerimeterLength = 5700
  Placement = pos=(8935,1700,11800) rot=(0,0,1;3.14159rad)
  PredefinedType = 0
  VerticalArea = 2.28e+06
  Width = 150
FEATURE [Part::FeaturePython] Structure357  label="V15x40 V130a003"  # Arch/BIM 7 (typed FeaturePython)
  FaceMaker = 0
  Height = 400
  HorizontalArea = 370500
  IfcData = attributes={"GlobalId": {"name": "GlobalId", "type": "IfcGloballyUniqueId", "is_enum": false, "enum_values": []}, "Description": {"... (+475 chars omitted),+1 more (map truncated)
  IfcType = 7
  Length = 2470
  MoveBase = false
  MoveWithHost = false
  Nodes = (2) [(-1.72563e-31,-1.42109e-15,-7.77156e-16),(2470,-1.42109e-15,-7.77156e-16)]
  NodesOffset = 0
  Normal = (0,0,0)
  PerimeterLength = 5240
  Placement = pos=(12010,3425,11800) rot=(0,0,1;1.5708rad)
  PredefinedType = 0
  VerticalArea = 2096000
  Width = 150
FEATURE [Part::FeaturePython] Structure358  label="V15x40 V189"  # Arch/BIM 7 (typed FeaturePython)
  FaceMaker = 0
  Height = 400
  HorizontalArea = 597000
  IfcData = attributes={"GlobalId": {"name": "GlobalId", "type": "IfcGloballyUniqueId", "is_enum": false, "enum_values": []}, "Description": {"... (+475 chars omitted),+1 more (map truncated)
  IfcType = 7
  Length = 3980
  MoveBase = false
  MoveWithHost = false
  Nodes = (2) [(-1.72563e-31,-1.42109e-15,-7.77156e-16),(3980,-1.42109e-15,-7.77156e-16)]
  NodesOffset = 0
  Normal = (0,0,0)
  PerimeterLength = 8260
  Placement = pos=(2055,9900,11800) rot=(0,0,1;0rad)
  PredefinedType = 0
  VerticalArea = 3.304e+06
  Width = 150
FEATURE [Part::FeaturePython] Structure359  label="V15x40 V190"  # Arch/BIM 7 (typed FeaturePython)
  FaceMaker = 0
  Height = 400
  HorizontalArea = 390000
  IfcData = attributes={"GlobalId": {"name": "GlobalId", "type": "IfcGloballyUniqueId", "is_enum": false, "enum_values": []}, "Description": {"... (+475 chars omitted),+1 more (map truncated)
  IfcType = 7
  Length = 2600
  MoveBase = false
  MoveWithHost = false
  Nodes = (2) [(-1.72563e-31,-1.42109e-15,-7.77156e-16),(2600,-1.42109e-15,-7.77156e-16)]
  NodesOffset = 0
  Normal = (0,0,0)
  PerimeterLength = 5500
  Placement = pos=(6285,9900,11800) rot=(0,0,1;0rad)
  PredefinedType = 0
  VerticalArea = 2200000
  Width = 150
FEATURE [Part::FeaturePython] Structure360  label="V15x40 V191"  # Arch/BIM 7 (typed FeaturePython)
  FaceMaker = 0
  Height = 400
  HorizontalArea = 412500
  IfcData = attributes={"GlobalId": {"name": "GlobalId", "type": "IfcGloballyUniqueId", "is_enum": false, "enum_values": []}, "Description": {"... (+475 chars omitted),+1 more (map truncated)
  IfcType = 7
  Length = 2750
  MoveBase = false
  MoveWithHost = false
  Nodes = (2) [(-1.72563e-31,-1.42109e-15,-7.77156e-16),(2750,-1.42109e-15,-7.77156e-16)]
  NodesOffset = 0
  Normal = (0,0,0)
  PerimeterLength = 5800
  Placement = pos=(9135,9900,11800) rot=(0,0,1;0rad)
  PredefinedType = 0
  VerticalArea = 2320000
  Width = 150
FEATURE [Part::FeaturePython] Structure361  label="V15x40 V192"  # Arch/BIM 7 (typed FeaturePython)
  FaceMaker = 0
  Height = 400
  HorizontalArea = 442500
  IfcData = attributes={"GlobalId": {"name": "GlobalId", "type": "IfcGloballyUniqueId", "is_enum": false, "enum_values": []}, "Description": {"... (+475 chars omitted),+1 more (map truncated)
  IfcType = 7
  Length = 2950
  MoveBase = false
  MoveWithHost = false
  Nodes = (2) [(-1.72563e-31,-1.42109e-15,-7.77156e-16),(2950,-1.42109e-15,-7.77156e-16)]
  NodesOffset = 0
  Normal = (0,0,0)
  PerimeterLength = 6200
  Placement = pos=(12135,9900,11800) rot=(0,0,1;0rad)
  PredefinedType = 0
  VerticalArea = 2.48e+06
  Width = 150
FEATURE [Part::FeaturePython] Structure362  label="V15x40 V193"  # Arch/BIM 7 (typed FeaturePython)
  FaceMaker = 0
  Height = 400
  HorizontalArea = 453750
  IfcData = attributes={"GlobalId": {"name": "GlobalId", "type": "IfcGloballyUniqueId", "is_enum": false, "enum_values": []}, "Description": {"... (+475 chars omitted),+1 more (map truncated)
  IfcType = 7
  Length = 3025
  MoveBase = false
  MoveWithHost = false
  Nodes = (2) [(-1.72563e-31,-1.42109e-15,-7.77156e-16),(3025,-1.42109e-15,-7.77156e-16)]
  NodesOffset = 0
  Normal = (0,0,0)
  PerimeterLength = 6350
  Placement = pos=(12085,8370,11800) rot=(0,0,1;0rad)
  PredefinedType = 0
  VerticalArea = 2.54e+06
  Width = 150
FEATURE [Part::FeaturePython] Structure363  label="V15x40 V194"  # Arch/BIM 7 (typed FeaturePython)
  FaceMaker = 0
  Height = 400
  HorizontalArea = 597000
  IfcData = attributes={"GlobalId": {"name": "GlobalId", "type": "IfcGloballyUniqueId", "is_enum": false, "enum_values": []}, "Description": {"... (+475 chars omitted),+1 more (map truncated)
  IfcType = 7
  Length = 3980
  MoveBase = false
  MoveWithHost = false
  Nodes = (2) [(-1.72563e-31,-1.42109e-15,-7.77156e-16),(3980,-1.42109e-15,-7.77156e-16)]
  NodesOffset = 0
  Normal = (0,0,0)
  PerimeterLength = 8260
  Placement = pos=(2055,6640,11800) rot=(0,0,1;0rad)
  PredefinedType = 0
  VerticalArea = 3.304e+06
  Width = 150
FEATURE [Part::FeaturePython] Structure364  label="V15x40 V195"  # Arch/BIM 7 (typed FeaturePython)
  FaceMaker = 0
  Height = 400
  HorizontalArea = 397500
  IfcData = attributes={"GlobalId": {"name": "GlobalId", "type": "IfcGloballyUniqueId", "is_enum": false, "enum_values": []}, "Description": {"... (+475 chars omitted),+1 more (map truncated)
  IfcType = 7
  Length = 2650
  MoveBase = false
  MoveWithHost = false
  Nodes = (2) [(-1.72563e-31,-1.42109e-15,-7.77156e-16),(2650,-1.42109e-15,-7.77156e-16)]
  NodesOffset = 0
  Normal = (0,0,0)
  PerimeterLength = 5600
  Placement = pos=(6285,6640,11800) rot=(0,0,1;0rad)
  PredefinedType = 0
  VerticalArea = 2240000
  Width = 150
FEATURE [Part::FeaturePython] Structure365  label="V15x40 V196"  # Arch/BIM 7 (typed FeaturePython)
  FaceMaker = 0
  Height = 400
  HorizontalArea = 210000
  IfcData = attributes={"GlobalId": {"name": "GlobalId", "type": "IfcGloballyUniqueId", "is_enum": false, "enum_values": []}, "Description": {"... (+475 chars omitted),+1 more (map truncated)
  IfcType = 7
  Length = 1400
  MoveBase = false
  MoveWithHost = false
  Nodes = (2) [(-1.72563e-31,-1.42109e-15,-7.77156e-16),(1400,-1.42109e-15,-7.77156e-16)]
  NodesOffset = 0
  Normal = (0,0,0)
  PerimeterLength = 3100
  Placement = pos=(9085,6640,11800) rot=(0,0,1;0rad)
  PredefinedType = 0
  VerticalArea = 1240000
  Width = 150
FEATURE [Part::FeaturePython] Structure366  label="V15x40 V197"  # Arch/BIM 7 (typed FeaturePython)
  FaceMaker = 0
  Height = 400
  HorizontalArea = 235500
  IfcData = attributes={"GlobalId": {"name": "GlobalId", "type": "IfcGloballyUniqueId", "is_enum": false, "enum_values": []}, "Description": {"... (+475 chars omitted),+1 more (map truncated)
  IfcType = 7
  Length = 1570
  MoveBase = false
  MoveWithHost = false
  Nodes = (2) [(-1.72563e-31,-1.42109e-15,-7.77156e-16),(1570,-1.42109e-15,-7.77156e-16)]
  NodesOffset = 0
  Normal = (0,0,0)
  PerimeterLength = 3440
  Placement = pos=(13655,5970,11800) rot=(0,0,1;3.14159rad)
  PredefinedType = 0
  VerticalArea = 1.376e+06
  Width = 150
FEATURE [Part::FeaturePython] Structure367  label="V15x40 V198"  # Arch/BIM 7 (typed FeaturePython)
  FaceMaker = 0
  Height = 400
  HorizontalArea = 177000
  IfcData = attributes={"GlobalId": {"name": "GlobalId", "type": "IfcGloballyUniqueId", "is_enum": false, "enum_values": []}, "Description": {"... (+475 chars omitted),+1 more (map truncated)
  IfcType = 7
  Length = 1180
  MoveBase = false
  MoveWithHost = false
  Nodes = (2) [(-1.72563e-31,-1.42109e-15,-7.77156e-16),(1180,-1.42109e-15,-7.77156e-16)]
  NodesOffset = 0
  Normal = (0,0,0)
  PerimeterLength = 2660
  Placement = pos=(13905,5970,11800) rot=(0,0,1;0rad)
  PredefinedType = 0
  VerticalArea = 1064000
  Width = 150
FEATURE [Part::FeaturePython] Structure368  label="V15x40 V199"  # Arch/BIM 7 (typed FeaturePython)
  FaceMaker = 0
  Height = 400
  HorizontalArea = 597000
  IfcData = attributes={"GlobalId": {"name": "GlobalId", "type": "IfcGloballyUniqueId", "is_enum": false, "enum_values": []}, "Description": {"... (+475 chars omitted),+1 more (map truncated)
  IfcType = 7
  Length = 3980
  MoveBase = false
  MoveWithHost = false
  Nodes = (2) [(-1.72563e-31,-1.42109e-15,-7.77156e-16),(3980,-1.42109e-15,-7.77156e-16)]
  NodesOffset = 0
  Normal = (0,0,0)
  PerimeterLength = 8260
  Placement = pos=(2055,3350,11800) rot=(0,0,1;0rad)
  PredefinedType = 0
  VerticalArea = 3.304e+06
  Width = 150
FEATURE [Part::FeaturePython] Structure369  label="V15x40 V200"  # Arch/BIM 7 (typed FeaturePython)
  FaceMaker = 0
  Height = 400
  HorizontalArea = 397500
  IfcData = attributes={"GlobalId": {"name": "GlobalId", "type": "IfcGloballyUniqueId", "is_enum": false, "enum_values": []}, "Description": {"... (+475 chars omitted),+1 more (map truncated)
  IfcType = 7
  Length = 2650
  MoveBase = false
  MoveWithHost = false
  Nodes = (2) [(-1.72563e-31,-1.42109e-15,-7.77156e-16),(2650,-1.42109e-15,-7.77156e-16)]
  NodesOffset = 0
  Normal = (0,0,0)
  PerimeterLength = 5600
  Placement = pos=(6285,3350,11800) rot=(0,0,1;0rad)
  PredefinedType = 0
  VerticalArea = 2240000
  Width = 150
FEATURE [Part::FeaturePython] Structure370  label="V15x40 V201"  # Arch/BIM 7 (typed FeaturePython)
  FaceMaker = 0
  Height = 400
  HorizontalArea = 210000
  IfcData = attributes={"GlobalId": {"name": "GlobalId", "type": "IfcGloballyUniqueId", "is_enum": false, "enum_values": []}, "Description": {"... (+475 chars omitted),+1 more (map truncated)
  IfcType = 7
  Length = 1400
  MoveBase = false
  MoveWithHost = false
  Nodes = (2) [(-1.72563e-31,-1.42109e-15,-7.77156e-16),(1400,-1.42109e-15,-7.77156e-16)]
  NodesOffset = 0
  Normal = (0,0,0)
  PerimeterLength = 3100
  Placement = pos=(9085,3350,11800) rot=(0,0,1;0rad)
  PredefinedType = 0
  VerticalArea = 1240000
  Width = 150
FEATURE [Part::FeaturePython] Structure371  label="V15x40 V202"  # Arch/BIM 7 (typed FeaturePython)
  FaceMaker = 0
  Height = 400
  HorizontalArea = 460500
  IfcData = attributes={"GlobalId": {"name": "GlobalId", "type": "IfcGloballyUniqueId", "is_enum": false, "enum_values": []}, "Description": {"... (+475 chars omitted),+1 more (map truncated)
  IfcType = 7
  Length = 3070
  MoveBase = false
  MoveWithHost = false
  Nodes = (2) [(-1.72563e-31,-1.42109e-15,-7.77156e-16),(3070,-1.42109e-15,-7.77156e-16)]
  NodesOffset = 0
  Normal = (0,0,0)
  PerimeterLength = 6440
  Placement = pos=(10635,3350,11800) rot=(0,0,1;0rad)
  PredefinedType = 0
  VerticalArea = 2.576e+06
  Width = 150
FEATURE [Part::FeaturePython] Structure372  label="V15x40 V203"  # Arch/BIM 7 (typed FeaturePython)
  FaceMaker = 0
  Height = 400
  HorizontalArea = 597000
  IfcData = attributes={"GlobalId": {"name": "GlobalId", "type": "IfcGloballyUniqueId", "is_enum": false, "enum_values": []}, "Description": {"... (+475 chars omitted),+1 more (map truncated)
  IfcType = 7
  Length = 3980
  MoveBase = false
  MoveWithHost = false
  Nodes = (2) [(-1.72563e-31,-1.42109e-15,-7.77156e-16),(3980,-1.42109e-15,-7.77156e-16)]
  NodesOffset = 0
  Normal = (0,0,0)
  PerimeterLength = 8260
  Placement = pos=(2055,100,11800) rot=(0,0,1;0rad)
  PredefinedType = 0
  VerticalArea = 3.304e+06
  Width = 150
FEATURE [Part::FeaturePython] Structure373  label="V15x40 V204"  # Arch/BIM 7 (typed FeaturePython)
  FaceMaker = 0
  Height = 400
  HorizontalArea = 390000
  IfcData = attributes={"GlobalId": {"name": "GlobalId", "type": "IfcGloballyUniqueId", "is_enum": false, "enum_values": []}, "Description": {"... (+475 chars omitted),+1 more (map truncated)
  IfcType = 7
  Length = 2600
  MoveBase = false
  MoveWithHost = false
  Nodes = (2) [(-1.72563e-31,-1.42109e-15,-7.77156e-16),(2600,-1.42109e-15,-7.77156e-16)]
  NodesOffset = 0
  Normal = (0,0,0)
  PerimeterLength = 5500
  Placement = pos=(6285,100,11800) rot=(0,0,1;0rad)
  PredefinedType = 0
  VerticalArea = 2200000
  Width = 150
FEATURE [Part::FeaturePython] Structure374  label="V15x40 V205"  # Arch/BIM 7 (typed FeaturePython)
  FaceMaker = 0
  Height = 400
  HorizontalArea = 195000
  IfcData = attributes={"GlobalId": {"name": "GlobalId", "type": "IfcGloballyUniqueId", "is_enum": false, "enum_values": []}, "Description": {"... (+475 chars omitted),+1 more (map truncated)
  IfcType = 7
  Length = 1300
  MoveBase = false
  MoveWithHost = false
  Nodes = (2) [(-1.72563e-31,-1.42109e-15,-7.77156e-16),(1300,-1.42109e-15,-7.77156e-16)]
  NodesOffset = 0
  Normal = (0,0,0)
  PerimeterLength = 2900
  Placement = pos=(9135,100,11800) rot=(0,0,1;0rad)
  PredefinedType = 0
  VerticalArea = 1160000
  Width = 150
FEATURE [Part::FeaturePython] Structure375  label="V15x40 V206"  # Arch/BIM 7 (typed FeaturePython)
  FaceMaker = 0
  Height = 400
  HorizontalArea = 445500
  IfcData = attributes={"GlobalId": {"name": "GlobalId", "type": "IfcGloballyUniqueId", "is_enum": false, "enum_values": []}, "Description": {"... (+475 chars omitted),+1 more (map truncated)
  IfcType = 7
  Length = 2970
  MoveBase = false
  MoveWithHost = false
  Nodes = (2) [(-1.72563e-31,-1.42109e-15,-7.77156e-16),(2970,-1.42109e-15,-7.77156e-16)]
  NodesOffset = 0
  Normal = (0,0,0)
  PerimeterLength = 6240
  Placement = pos=(10685,100,11800) rot=(0,0,1;0rad)
  PredefinedType = 0
  VerticalArea = 2.496e+06
  Width = 150
FEATURE [Part::FeaturePython] Structure376  label="V15x40 V207"  # Arch/BIM 7 (typed FeaturePython)
  FaceMaker = 0
  Height = 400
  HorizontalArea = 465000
  IfcData = attributes={"GlobalId": {"name": "GlobalId", "type": "IfcGloballyUniqueId", "is_enum": false, "enum_values": []}, "Description": {"... (+475 chars omitted),+1 more (map truncated)
  IfcType = 7
  Length = 3100
  MoveBase = false
  MoveWithHost = false
  Nodes = (2) [(-1.72563e-31,-1.42109e-15,-7.77156e-16),(3100,-1.42109e-15,-7.77156e-16)]
  NodesOffset = 0
  Normal = (0,0,0)
  PerimeterLength = 6500
  Placement = pos=(6160,3275,11800) rot=(0,0,-1;1.5708rad)
  PredefinedType = 0
  VerticalArea = 2.6e+06
  Width = 150
FEATURE [Part::FeaturePython] Structure377  label="V15x40 V208"  # Arch/BIM 7 (typed FeaturePython)
  FaceMaker = 0
  Height = 400
  HorizontalArea = 471000
  IfcData = attributes={"GlobalId": {"name": "GlobalId", "type": "IfcGloballyUniqueId", "is_enum": false, "enum_values": []}, "Description": {"... (+475 chars omitted),+1 more (map truncated)
  IfcType = 7
  Length = 3140
  MoveBase = false
  MoveWithHost = false
  Nodes = (2) [(-1.72563e-31,-1.42109e-15,-7.77156e-16),(3140,-1.42109e-15,-7.77156e-16)]
  NodesOffset = 0
  Normal = (0,0,0)
  PerimeterLength = 6580
  Placement = pos=(6160,6565,11800) rot=(0,0,-1;1.5708rad)
  PredefinedType = 0
  VerticalArea = 2.632e+06
  Width = 150
FEATURE [Part::FeaturePython] Structure378  label="V15x40 V209"  # Arch/BIM 7 (typed FeaturePython)
  FaceMaker = 0
  Height = 400
  HorizontalArea = 466500
  IfcData = attributes={"GlobalId": {"name": "GlobalId", "type": "IfcGloballyUniqueId", "is_enum": false, "enum_values": []}, "Description": {"... (+475 chars omitted),+1 more (map truncated)
  IfcType = 7
  Length = 3110
  MoveBase = false
  MoveWithHost = false
  Nodes = (2) [(-1.72563e-31,-1.42109e-15,-7.77156e-16),(3110,-1.42109e-15,-7.77156e-16)]
  NodesOffset = 0
  Normal = (0,0,0)
  PerimeterLength = 6520
  Placement = pos=(6160,9825,11800) rot=(0,0,-1;1.5708rad)
  PredefinedType = 0
  VerticalArea = 2.608e+06
  Width = 150
FEATURE [Part::FeaturePython] Structure379  label="V15x40 V210"  # Arch/BIM 7 (typed FeaturePython)
  FaceMaker = 0
  Height = 400
  HorizontalArea = 457500
  IfcData = attributes={"GlobalId": {"name": "GlobalId", "type": "IfcGloballyUniqueId", "is_enum": false, "enum_values": []}, "Description": {"... (+475 chars omitted),+1 more (map truncated)
  IfcType = 7
  Length = 3050
  MoveBase = false
  MoveWithHost = false
  Nodes = (2) [(-1.72563e-31,-1.42109e-15,-7.77156e-16),(3050,-1.42109e-15,-7.77156e-16)]
  NodesOffset = 0
  Normal = (0,0,0)
  PerimeterLength = 6400
  Placement = pos=(9010,3225,11800) rot=(0,0,-1;1.5708rad)
  PredefinedType = 0
  VerticalArea = 2.56e+06
  Width = 150
FEATURE [Part::FeaturePython] Structure380  label="V15x40 V211"  # Arch/BIM 7 (typed FeaturePython)
  FaceMaker = 0
  Height = 400
  HorizontalArea = 456000
  IfcData = attributes={"GlobalId": {"name": "GlobalId", "type": "IfcGloballyUniqueId", "is_enum": false, "enum_values": []}, "Description": {"... (+475 chars omitted),+1 more (map truncated)
  IfcType = 7
  Length = 3040
  MoveBase = false
  MoveWithHost = false
  Nodes = (2) [(-1.72563e-31,-1.42109e-15,-7.77156e-16),(3040,-1.42109e-15,-7.77156e-16)]
  NodesOffset = 0
  Normal = (0,0,0)
  PerimeterLength = 6380
  Placement = pos=(9010,6515,11800) rot=(0,0,-1;1.5708rad)
  PredefinedType = 0
  VerticalArea = 2.552e+06
  Width = 150
FEATURE [Part::FeaturePython] Structure381  label="V15x40 V212"  # Arch/BIM 7 (typed FeaturePython)
  FaceMaker = 0
  Height = 400
  HorizontalArea = 459000
  IfcData = attributes={"GlobalId": {"name": "GlobalId", "type": "IfcGloballyUniqueId", "is_enum": false, "enum_values": []}, "Description": {"... (+475 chars omitted),+1 more (map truncated)
  IfcType = 7
  Length = 3060
  MoveBase = false
  MoveWithHost = false
  Nodes = (2) [(-1.72563e-31,-1.42109e-15,-7.77156e-16),(3060,-1.42109e-15,-7.77156e-16)]
  NodesOffset = 0
  Normal = (0,0,0)
  PerimeterLength = 6420
  Placement = pos=(9010,9825,11800) rot=(0,0,-1;1.5708rad)
  PredefinedType = 0
  VerticalArea = 2.568e+06
  Width = 150
FEATURE [Part::FeaturePython] Structure382  label="V15x40 V213"  # Arch/BIM 7 (typed FeaturePython)
  FaceMaker = 0
  Height = 400
  HorizontalArea = 457500
  IfcData = attributes={"GlobalId": {"name": "GlobalId", "type": "IfcGloballyUniqueId", "is_enum": false, "enum_values": []}, "Description": {"... (+475 chars omitted),+1 more (map truncated)
  IfcType = 7
  Length = 3050
  MoveBase = false
  MoveWithHost = false
  Nodes = (2) [(-1.72563e-31,-1.42109e-15,-7.77156e-16),(3050,-1.42109e-15,-7.77156e-16)]
  NodesOffset = 0
  Normal = (0,0,0)
  PerimeterLength = 6400
  Placement = pos=(10560,3225,11800) rot=(0,0,-1;1.5708rad)
  PredefinedType = 0
  VerticalArea = 2.56e+06
  Width = 150
FEATURE [Part::FeaturePython] Structure383  label="V15x40 V214"  # Arch/BIM 7 (typed FeaturePython)
  FaceMaker = 0
  Height = 400
  HorizontalArea = 363000
  IfcData = attributes={"GlobalId": {"name": "GlobalId", "type": "IfcGloballyUniqueId", "is_enum": false, "enum_values": []}, "Description": {"... (+475 chars omitted),+1 more (map truncated)
  IfcType = 7
  Length = 2420
  MoveBase = false
  MoveWithHost = false
  Nodes = (2) [(-1.72563e-31,-1.42109e-15,-7.77156e-16),(2420,-1.42109e-15,-7.77156e-16)]
  NodesOffset = 0
  Normal = (0,0,0)
  PerimeterLength = 5140
  Placement = pos=(10560,3475,11800) rot=(0,0,1;1.5708rad)
  PredefinedType = 0
  VerticalArea = 2056000
  Width = 150
FEATURE [Part::FeaturePython] Structure384  label="V15x40 V215"  # Arch/BIM 7 (typed FeaturePython)
  FaceMaker = 0
  Height = 400
  HorizontalArea = 207000
  IfcData = attributes={"GlobalId": {"name": "GlobalId", "type": "IfcGloballyUniqueId", "is_enum": false, "enum_values": []}, "Description": {"... (+475 chars omitted),+1 more (map truncated)
  IfcType = 7
  Length = 1380
  MoveBase = false
  MoveWithHost = false
  Nodes = (2) [(-1.72563e-31,-1.42109e-15,-7.77156e-16),(1380,-1.42109e-15,-7.77156e-16)]
  NodesOffset = 0
  Normal = (0,0,0)
  PerimeterLength = 3060
  Placement = pos=(10560,8445,11800) rot=(0,0,1;1.5708rad)
  PredefinedType = 0
  VerticalArea = 1224000
  Width = 150
FEATURE [Part::FeaturePython] Structure385  label="V15x40 V216"  # Arch/BIM 7 (typed FeaturePython)
  FaceMaker = 0
  Height = 400
  HorizontalArea = 207000
  IfcData = attributes={"GlobalId": {"name": "GlobalId", "type": "IfcGloballyUniqueId", "is_enum": false, "enum_values": []}, "Description": {"... (+475 chars omitted),+1 more (map truncated)
  IfcType = 7
  Length = 1380
  MoveBase = false
  MoveWithHost = false
  Nodes = (2) [(-1.72563e-31,-1.42109e-15,-7.77156e-16),(1380,-1.42109e-15,-7.77156e-16)]
  NodesOffset = 0
  Normal = (0,0,0)
  PerimeterLength = 3060
  Placement = pos=(12010,9825,11800) rot=(0,0,-1;1.5708rad)
  PredefinedType = 0
  VerticalArea = 1224000
  Width = 150
FEATURE [Part::FeaturePython] Structure386  label="V20x40 V148"  # Arch/BIM 7 (typed FeaturePython)
  FaceMaker = 0
  Height = 400
  HorizontalArea = 615000
  IfcData = attributes={"GlobalId": {"name": "GlobalId", "type": "IfcGloballyUniqueId", "is_enum": false, "enum_values": []}, "Description": {"... (+475 chars omitted),+1 more (map truncated)
  IfcType = 7
  Length = 3075
  MoveBase = false
  MoveWithHost = false
  Nodes = (2) [(-1.72563e-31,0,-7.77156e-16),(3075,0,-7.77156e-16)]
  NodesOffset = 0
  Normal = (0,0,0)
  PerimeterLength = 6550
  Placement = pos=(1930,3250,11800) rot=(0,0,-1;1.5708rad)
  PredefinedType = 0
  VerticalArea = 2.62e+06
  Width = 200
FEATURE [Part::FeaturePython] Structure387  label="V20x40 V149"  # Arch/BIM 7 (typed FeaturePython)
  FaceMaker = 0
  Height = 400
  HorizontalArea = 618000
  IfcData = attributes={"GlobalId": {"name": "GlobalId", "type": "IfcGloballyUniqueId", "is_enum": false, "enum_values": []}, "Description": {"... (+475 chars omitted),+1 more (map truncated)
  IfcType = 7
  Length = 3090
  MoveBase = false
  MoveWithHost = false
  Nodes = (2) [(-1.72563e-31,0,-7.77156e-16),(3090,0,-7.77156e-16)]
  NodesOffset = 0
  Normal = (0,0,0)
  PerimeterLength = 6580
  Placement = pos=(1930,6540,11800) rot=(0,0,-1;1.5708rad)
  PredefinedType = 0
  VerticalArea = 2.632e+06
  Width = 200
FEATURE [Part::FeaturePython] Structure388  label="V20x40 V150"  # Arch/BIM 7 (typed FeaturePython)
  FaceMaker = 0
  Height = 400
  HorizontalArea = 617000
  IfcData = attributes={"GlobalId": {"name": "GlobalId", "type": "IfcGloballyUniqueId", "is_enum": false, "enum_values": []}, "Description": {"... (+475 chars omitted),+1 more (map truncated)
  IfcType = 7
  Length = 3085
  MoveBase = false
  MoveWithHost = false
  Nodes = (2) [(-1.72563e-31,0,-7.77156e-16),(3085,0,-7.77156e-16)]
  NodesOffset = 0
  Normal = (0,0,0)
  PerimeterLength = 6570
  Placement = pos=(1930,9825,11800) rot=(0,0,-1;1.5708rad)
  PredefinedType = 0
  VerticalArea = 2.628e+06
  Width = 200
FEATURE [Part::FeaturePython] Structure389  label="V20x40 V151"  # Arch/BIM 7 (typed FeaturePython)
  FaceMaker = 0
  Height = 400
  HorizontalArea = 635000
  IfcData = attributes={"GlobalId": {"name": "GlobalId", "type": "IfcGloballyUniqueId", "is_enum": false, "enum_values": []}, "Description": {"... (+475 chars omitted),+1 more (map truncated)
  IfcType = 7
  Length = 3175
  MoveBase = false
  MoveWithHost = false
  Nodes = (2) [(-1.72563e-31,0,-7.77156e-16),(3175,0,-7.77156e-16)]
  NodesOffset = 0
  Normal = (0,0,0)
  PerimeterLength = 6750
  Placement = pos=(13780,175,11800) rot=(0,0,1;1.5708rad)
  PredefinedType = 0
  VerticalArea = 2.7e+06
  Width = 200
FEATURE [Part::FeaturePython] Structure390  label="V20x40 V152"  # Arch/BIM 7 (typed FeaturePython)
  FaceMaker = 0
  Height = 400
  HorizontalArea = 509000
  IfcData = attributes={"GlobalId": {"name": "GlobalId", "type": "IfcGloballyUniqueId", "is_enum": false, "enum_values": []}, "Description": {"... (+475 chars omitted),+1 more (map truncated)
  IfcType = 7
  Length = 2545
  MoveBase = false
  MoveWithHost = false
  Nodes = (2) [(-1.72563e-31,0,-7.77156e-16),(2545,0,-7.77156e-16)]
  NodesOffset = 0
  Normal = (0,0,0)
  PerimeterLength = 5490
  Placement = pos=(13780,3350,11800) rot=(0,0,1;1.5708rad)
  PredefinedType = 0
  VerticalArea = 2196000
  Width = 200
FEATURE [Part::FeaturePython] Structure391  label="V20x40 V153"  # Arch/BIM 7 (typed FeaturePython)
  FaceMaker = 0
  Height = 400
  HorizontalArea = 756000
  IfcData = attributes={"GlobalId": {"name": "GlobalId", "type": "IfcGloballyUniqueId", "is_enum": false, "enum_values": []}, "Description": {"... (+475 chars omitted),+1 more (map truncated)
  IfcType = 7
  Length = 3780
  MoveBase = false
  MoveWithHost = false
  Nodes = (2) [(-1.72563e-31,0,-7.77156e-16),(3780,0,-7.77156e-16)]
  NodesOffset = 0
  Normal = (0,0,0)
  PerimeterLength = 7960
  Placement = pos=(15210,6045,11800) rot=(0,0,1;1.5708rad)
  PredefinedType = 0
  VerticalArea = 3.184e+06
  Width = 200
FEATURE [App::GeometryPython] BuildingPart022  label="Vigas sobre P3"  # Arch/BIM 172 (typed FeaturePython)
  Area = 0
  Group = -> [Structure354,Structure355,Structure356,Structure357,Structure358,Structure359,Structure360,Structure361,Structure362,Structure363,Structure364,Structure365,Structure366,Structure367,Structure368,Structure369,Structure370,Structure371,Structure372,Structure373,Structure374,Structure375,Structure376,Structure377,Structure378,Structure379,Structure380,Structure381,Structure382,Structure383,+8 more]
  Height = 0
  HeightPropagate = true
  IfcData = attributes={"GlobalId": {"name": "GlobalId", "type": "IfcGloballyUniqueId", "is_enum": false, "enum_values": []}, "Description": {"... (+484 chars omitted),+1 more (map truncated)
  IfcType = 172
  LevelOffset = 0
  PredefinedType = 0
FEATURE [App::GeometryPython] BuildingPart019  label="Piso 3"  # Arch/BIM 172 (typed FeaturePython)
  Area = 24900000
  Group = -> [BuildingPart020,BuildingPart021,Wall004,BuildingPart022]
  Height = 0
  HeightPropagate = true
  IfcData = attributes={"GlobalId": {"name": "GlobalId", "type": "IfcGloballyUniqueId", "is_enum": false, "enum_values": []}, "Description": {"... (+484 chars omitted),+1 more (map truncated)
  IfcType = 172
  LevelOffset = 0
  Placement = pos=(0,0,9000) rot=(0,0,1;0rad)
  PredefinedType = 0
FEATURE [App::GeometryPython] BuildingPart024  label="Sobre Terraza"  # Arch/BIM 172 (typed FeaturePython)
  Area = 0
  Height = 0
  HeightPropagate = true
  IfcData = attributes={"GlobalId": {"name": "GlobalId", "type": "IfcGloballyUniqueId", "is_enum": false, "enum_values": []}, "Description": {"... (+484 chars omitted),+1 more (map truncated)
  IfcType = 172
  LevelOffset = 0
  PredefinedType = 0
FEATURE [Part::FeaturePython] Structure392  label="Column"  # Arch/BIM 24 (typed FeaturePython)
  FaceMaker = 0
  Height = 3000
  HorizontalArea = 22500
  IfcData = attributes={"GlobalId": {"name": "GlobalId", "type": "IfcGloballyUniqueId", "is_enum": false, "enum_values": []}, "Description": {"... (+438 chars omitted),+1 more (map truncated)
  IfcType = 24
  Length = 150
  MoveBase = false
  MoveWithHost = false
  Nodes = (2) [(2.77556e-16,7.57912e-16,0),(2.77556e-16,7.57912e-16,3000)]
  NodesOffset = 0
  Normal = (0,0,0)
  PerimeterLength = 600
  Placement = pos=(15210,9900,12000) rot=(0,0,1;0rad)
  PredefinedType = 0
  VerticalArea = 1800000
  Width = 150
FEATURE [Part::FeaturePython] Structure393  label="Column001"  # Arch/BIM 24 (typed FeaturePython)
  FaceMaker = 0
  Height = 3000
  HorizontalArea = 22500
  IfcData = attributes={"GlobalId": {"name": "GlobalId", "type": "IfcGloballyUniqueId", "is_enum": false, "enum_values": []}, "Description": {"... (+438 chars omitted),+1 more (map truncated)
  IfcType = 24
  Length = 150
  MoveBase = false
  MoveWithHost = false
  Nodes = (2) [(2.77556e-16,7.57912e-16,0),(2.77556e-16,7.57912e-16,3000)]
  NodesOffset = 0
  Normal = (0,0,0)
  PerimeterLength = 600
  Placement = pos=(10560,9900,12000) rot=(0,0,1;0rad)
  PredefinedType = 0
  VerticalArea = 1800000
  Width = 150
FEATURE [Part::FeaturePython] Structure394  label="Column002"  # Arch/BIM 24 (typed FeaturePython)
  FaceMaker = 0
  Height = 3000
  HorizontalArea = 22500
  IfcData = attributes={"GlobalId": {"name": "GlobalId", "type": "IfcGloballyUniqueId", "is_enum": false, "enum_values": []}, "Description": {"... (+438 chars omitted),+1 more (map truncated)
  IfcType = 24
  Length = 150
  MoveBase = false
  MoveWithHost = false
  Nodes = (2) [(2.77556e-16,7.57912e-16,0),(2.77556e-16,7.57912e-16,3000)]
  NodesOffset = 0
  Normal = (0,0,0)
  PerimeterLength = 600
  Placement = pos=(15210,5970,12000) rot=(0,0,1;0rad)
  PredefinedType = 0
  VerticalArea = 1800000
  Width = 150
FEATURE [Part::FeaturePython] Structure395  label="Column003"  # Arch/BIM 24 (typed FeaturePython)
  FaceMaker = 0
  Height = 3000
  HorizontalArea = 22500
  IfcData = attributes={"GlobalId": {"name": "GlobalId", "type": "IfcGloballyUniqueId", "is_enum": false, "enum_values": []}, "Description": {"... (+438 chars omitted),+1 more (map truncated)
  IfcType = 24
  Length = 150
  MoveBase = false
  MoveWithHost = false
  Nodes = (2) [(2.77556e-16,7.57912e-16,0),(2.77556e-16,7.57912e-16,3000)]
  NodesOffset = 0
  Normal = (0,0,0)
  PerimeterLength = 600
  Placement = pos=(10560,5970,12000) rot=(0,0,1;0rad)
  PredefinedType = 0
  VerticalArea = 1800000
  Width = 150
FEATURE [Part::FeaturePython] Structure396  label="Beam042"  # Arch/BIM 7 (typed FeaturePython)
  FaceMaker = 0
  Height = 300
  HorizontalArea = 675000
  IfcData = attributes={"GlobalId": {"name": "GlobalId", "type": "IfcGloballyUniqueId", "is_enum": false, "enum_values": []}, "Description": {"... (+475 chars omitted),+1 more (map truncated)
  IfcType = 7
  Length = 4500
  MoveBase = false
  MoveWithHost = false
  Nodes = (2) [(1.2326e-31,-7.57912e-16,5.55112e-16),(4500,-7.57912e-16,5.55112e-16)]
  NodesOffset = 0
  Normal = (0,0,0)
  PerimeterLength = 9300
  Placement = pos=(10635,9900,14850) rot=(0,0,1;0rad)
  PredefinedType = 0
  VerticalArea = 2790000
  Width = 150
FEATURE [Part::FeaturePython] Structure397  label="Beam043"  # Arch/BIM 7 (typed FeaturePython)
  FaceMaker = 0
  Height = 300
  HorizontalArea = 567000
  IfcData = attributes={"GlobalId": {"name": "GlobalId", "type": "IfcGloballyUniqueId", "is_enum": false, "enum_values": []}, "Description": {"... (+475 chars omitted),+1 more (map truncated)
  IfcType = 7
  Length = 3780
  MoveBase = false
  MoveWithHost = false
  Nodes = (2) [(1.2326e-31,-7.57912e-16,5.55112e-16),(3780,-7.57912e-16,5.55112e-16)]
  NodesOffset = 0
  Normal = (0,0,0)
  PerimeterLength = 7860
  Placement = pos=(15210,9825,14850) rot=(0,0,-1;1.5708rad)
  PredefinedType = 0
  VerticalArea = 2.358e+06
  Width = 150
FEATURE [Part::FeaturePython] Structure398  label="Beam044"  # Arch/BIM 7 (typed FeaturePython)
  FaceMaker = 0
  Height = 300
  HorizontalArea = 675000
  IfcData = attributes={"GlobalId": {"name": "GlobalId", "type": "IfcGloballyUniqueId", "is_enum": false, "enum_values": []}, "Description": {"... (+475 chars omitted),+1 more (map truncated)
  IfcType = 7
  Length = 4500
  MoveBase = false
  MoveWithHost = false
  Nodes = (2) [(1.2326e-31,-7.57912e-16,5.55112e-16),(4500,-7.57912e-16,5.55112e-16)]
  NodesOffset = 0
  Normal = (0,0,0)
  PerimeterLength = 9300
  Placement = pos=(15135,5970,14850) rot=(0,0,1;3.14159rad)
  PredefinedType = 0
  VerticalArea = 2790000
  Width = 150
FEATURE [Part::FeaturePython] Structure399  label="Beam045"  # Arch/BIM 7 (typed FeaturePython)
  FaceMaker = 0
  Height = 300
  HorizontalArea = 567000
  IfcData = attributes={"GlobalId": {"name": "GlobalId", "type": "IfcGloballyUniqueId", "is_enum": false, "enum_values": []}, "Description": {"... (+475 chars omitted),+1 more (map truncated)
  IfcType = 7
  Length = 3780
  MoveBase = false
  MoveWithHost = false
  Nodes = (2) [(1.2326e-31,-7.57912e-16,5.55112e-16),(3780,-7.57912e-16,5.55112e-16)]
  NodesOffset = 0
  Normal = (0,0,0)
  PerimeterLength = 7860
  Placement = pos=(10560,6045,14850) rot=(0,0,1;1.5708rad)
  PredefinedType = 0
  VerticalArea = 2.358e+06
  Width = 150
FEATURE [App::GeometryPython] BuildingPart025  label="Vigas sobre Terraza"  # Arch/BIM 172 (typed FeaturePython)
  Area = 0
  Group = -> [Structure396,Structure397,Structure398,Structure399]
  Height = 0
  HeightPropagate = true
  IfcData = attributes={"GlobalId": {"name": "GlobalId", "type": "IfcGloballyUniqueId", "is_enum": false, "enum_values": []}, "Description": {"... (+484 chars omitted),+1 more (map truncated)
  IfcType = 172
  LevelOffset = 0
  Placement = pos=(0,0,12000) rot=(0,0,1;0rad)
  PredefinedType = 0
FEATURE [App::GeometryPython] BuildingPart026  label="Columnas Terraza"  # Arch/BIM 172 (typed FeaturePython)
  Area = 0
  Group = -> [Structure392,Structure393,Structure394,Structure395]
  Height = 0
  HeightPropagate = true
  IfcData = attributes={"GlobalId": {"name": "GlobalId", "type": "IfcGloballyUniqueId", "is_enum": false, "enum_values": []}, "Description": {"... (+484 chars omitted),+1 more (map truncated)
  IfcType = 172
  LevelOffset = 0
  Placement = pos=(0,0,12000) rot=(0,0,1;0rad)
  PredefinedType = 0
FEATURE [Part::Part2DObjectPython] Rectangle021  # Draft 2D object (typed FeaturePython)
  Area = 1.701e+07
  ChamferSize = 0
  Columns = 1
  FilletRadius = 0
  Height = 3780
  Length = 4500
  MakeFace = true
  Placement = pos=(10635,6045,15000) rot=(0,0,1;0rad)
  Rows = 1
FEATURE [Part::FeaturePython] Structure400  label="Structure"  # Arch/BIM 172 (typed FeaturePython)
  Base = -> Rectangle021
  FaceMaker = 0
  Height = 150
  HorizontalArea = 1.701e+07
  IfcData = attributes={"GlobalId": {"name": "GlobalId", "type": "IfcGloballyUniqueId", "is_enum": false, "enum_values": []}, "Description": {"... (+484 chars omitted),+1 more (map truncated)
  IfcType = 172
  Length = 0
  MoveBase = false
  MoveWithHost = false
  Nodes = (2) [(12885,7935,15000),(12885,7935,14850)]
  NodesOffset = 0
  Normal = (0,0,-1)
  PerimeterLength = 16560
  PredefinedType = 0
  VerticalArea = 2484000
  Width = 150
FEATURE [App::GeometryPython] BuildingPart027  label="Losas sobre Terraza"  # Arch/BIM 172 (typed FeaturePython)
  Area = 0
  Group = -> [Structure400]
  Height = 0
  HeightPropagate = true
  IfcData = attributes={"GlobalId": {"name": "GlobalId", "type": "IfcGloballyUniqueId", "is_enum": false, "enum_values": []}, "Description": {"... (+484 chars omitted),+1 more (map truncated)
  IfcType = 172
  LevelOffset = 0
  Placement = pos=(0,0,12000) rot=(0,0,1;0rad)
  PredefinedType = 0
FEATURE [App::GeometryPython] BuildingPart023  label="Terraza"  # Arch/BIM 172 (typed FeaturePython)
  Area = 0
  Group = -> [BuildingPart026,BuildingPart025,BuildingPart027]
  Height = 0
  HeightPropagate = true
  IfcData = attributes={"GlobalId": {"name": "GlobalId", "type": "IfcGloballyUniqueId", "is_enum": false, "enum_values": []}, "Description": {"... (+484 chars omitted),+1 more (map truncated)
  IfcType = 172
  LevelOffset = 0
  Placement = pos=(0,0,12000) rot=(0,0,1;0rad)
  PredefinedType = 0
FEATURE [Part::FeaturePython] Axis004  label="Horizontal corta"  # WARN: FeaturePython — macro-defined, semantics opaque (R4)
  Angles = [0,0,0,0,0,0]
  Distances = [100,3250,2620,670,1730,1530]
  Length = 18000
  Placement = pos=(17000,1.077e-12,0) rot=(0,0,1;1.5708rad)
FEATURE [App::DocumentObjectGroup] Group  label="Rejillas"
  Group = -> [Axis002,Axis,Axis004]
FEATURE [App::MaterialObjectPython] Material  label="Hormigon Armado"  # material (typed FeaturePython)
  Description = HA
  Material = Description=HA,DiffuseColor=(0.8500000238418579, 0.8500000238418579, 0.8500000238418579),Name=Hormigon Armado,+2 more (map truncated)
  Transparency = 0
FEATURE [Part::FeaturePython] Structure  label="CAB PIL 1"  # Arch/BIM 77 (typed FeaturePython)
  Base = -> Rectangle002
  Description = Pilote rectangular
  FaceMaker = 0
  Height = 700
  HorizontalArea = 490000
  IfcData = attributes={"GlobalId": {"name": "GlobalId", "type": "IfcGloballyUniqueId", "is_enum": false, "enum_values": []}, "Description": {"... (+558 chars omitted),+1 more (map truncated)
  IfcType = 77
  Length = 0
  Material = -> Material
  MoveBase = false
  MoveWithHost = false
  Nodes = (2) [(15210,9900,0),(15210,9900,-700)]
  NodesOffset = 0
  Normal = (0,0,-1)
  PerimeterLength = 2800
  Placement = pos=(-13280,1.819e-12,-500) rot=(0,0,1;0rad)
  PredefinedType = 3
  Tag = B1 (70x70x70)
  VerticalArea = 1960000
  Width = 0
  expr: Height = <<Estructura>>.CabEsp
FEATURE [Part::FeaturePython] Structure001  label="PIL 1"  # Arch/BIM 96 (typed FeaturePython)
  Base = -> Circle
  ConstructionType = 0
  Description = Pilote circular
  FaceMaker = 0
  Height = 8000
  HorizontalArea = 196350
  IfcData = attributes={"GlobalId": {"name": "GlobalId", "type": "IfcGloballyUniqueId", "is_enum": false, "enum_values": []}, "Description": {"... (+752 chars omitted),+1 more (map truncated)
  IfcType = 96
  Length = 0
  Material = -> Material
  MoveBase = false
  MoveWithHost = false
  Nodes = (2) [(15210,9900,0),(15210,9900,-8000)]
  NodesOffset = 0
  Normal = (0,0,-1)
  PerimeterLength = 1570.8
  Placement = pos=(-13280,1.819e-12,-1200) rot=(0,0,1;0rad)
  PredefinedType = 5
  VerticalArea = 1.25664e+07
  Width = 100
  expr: Height = <<Estructura>>.PilProf
FEATURE [Part::FeaturePython] Structure002  label="CAB PIL 6"  # Arch/BIM 172 (typed FeaturePython)
  CloneOf = -> Structure
  FaceMaker = 0
  Height = 700
  HorizontalArea = 490000
  IfcData = attributes={"GlobalId": {"name": "GlobalId", "type": "IfcGloballyUniqueId", "is_enum": false, "enum_values": []}, "Description": {"... (+510 chars omitted),+1 more (map truncated)
  IfcType = 172
  Length = 0
  Material = -> Material
  MoveBase = false
  MoveWithHost = false
  Nodes = (2) [(15210,9900,0),(15210,9900,-700)]
  NodesOffset = 0
  Normal = (0,0,0)
  PerimeterLength = 2800
  Placement = pos=(-13280,-3260,-500) rot=(0,0,1;0rad)
  PredefinedType = 0
  Tag = B1 (70x70x70)
  VerticalArea = 1960000
  Width = 0
FEATURE [Part::FeaturePython] Structure003  label="PIL 6"  # Arch/BIM 172 (typed FeaturePython)
  CloneOf = -> Structure001
  FaceMaker = 0
  Height = 8000
  HorizontalArea = 196350
  IfcData = attributes={"GlobalId": {"name": "GlobalId", "type": "IfcGloballyUniqueId", "is_enum": false, "enum_values": []}, "Description": {"... (+484 chars omitted),+1 more (map truncated)
  IfcType = 172
  Length = 0
  Material = -> Material
  MoveBase = false
  MoveWithHost = false
  Nodes = (2) [(15210,9900,0),(15210,9900,-8000)]
  NodesOffset = 0
  Normal = (0,0,0)
  PerimeterLength = 1570.8
  Placement = pos=(-13280,-3260,-1200) rot=(0,0,1;0rad)
  PredefinedType = 0
  VerticalArea = 1.25664e+07
  Width = 100
FEATURE [Part::FeaturePython] Structure004  label="CAB PIL 11"  # Arch/BIM 172 (typed FeaturePython)
  CloneOf = -> Structure
  FaceMaker = 0
  Height = 700
  HorizontalArea = 490000
  IfcData = attributes={"GlobalId": {"name": "GlobalId", "type": "IfcGloballyUniqueId", "is_enum": false, "enum_values": []}, "Description": {"... (+510 chars omitted),+1 more (map truncated)
  IfcType = 172
  Length = 0
  Material = -> Material
  MoveBase = false
  MoveWithHost = false
  Nodes = (2) [(15210,9900,0),(15210,9900,-700)]
  NodesOffset = 0
  Normal = (0,0,0)
  PerimeterLength = 2800
  Placement = pos=(-13280,-6550,-500) rot=(0,0,1;0rad)
  PredefinedType = 0
  Tag = B1 (70x70x70)
  VerticalArea = 1960000
  Width = 0
FEATURE [Part::FeaturePython] Structure005  label="PIL 11"  # Arch/BIM 172 (typed FeaturePython)
  CloneOf = -> Structure001
  FaceMaker = 0
  Height = 8000
  HorizontalArea = 196350
  IfcData = attributes={"GlobalId": {"name": "GlobalId", "type": "IfcGloballyUniqueId", "is_enum": false, "enum_values": []}, "Description": {"... (+484 chars omitted),+1 more (map truncated)
  IfcType = 172
  Length = 0
  Material = -> Material
  MoveBase = false
  MoveWithHost = false
  Nodes = (2) [(15210,9900,0),(15210,9900,-8000)]
  NodesOffset = 0
  Normal = (0,0,0)
  PerimeterLength = 1570.8
  Placement = pos=(-13280,-6550,-1200) rot=(0,0,1;0rad)
  PredefinedType = 0
  VerticalArea = 1.25664e+07
  Width = 100
FEATURE [Part::FeaturePython] Structure006  label="CAB PIL 2"  # Arch/BIM 172 (typed FeaturePython)
  CloneOf = -> Structure
  Description = (70x70x70)
  FaceMaker = 0
  Height = 700
  HorizontalArea = 490000
  IfcData = attributes={"GlobalId": {"name": "GlobalId", "type": "IfcGloballyUniqueId", "is_enum": false, "enum_values": []}, "Description": {"... (+533 chars omitted),+1 more (map truncated)
  IfcType = 172
  Length = 0
  Material = -> Material
  MoveBase = false
  MoveWithHost = false
  Nodes = (2) [(15210,9900,0),(15210,9900,-700)]
  NodesOffset = 0
  Normal = (0,0,0)
  PerimeterLength = 2800
  Placement = pos=(-9050,0,-500) rot=(0,0,1;0rad)
  PredefinedType = 0
  Tag = B1 (70x70x70)
  VerticalArea = 1960000
  Width = 0
FEATURE [Part::FeaturePython] Structure007  label="PIL 2"  # Arch/BIM 172 (typed FeaturePython)
  CloneOf = -> Structure001
  FaceMaker = 0
  Height = 8000
  HorizontalArea = 196350
  IfcData = attributes={"GlobalId": {"name": "GlobalId", "type": "IfcGloballyUniqueId", "is_enum": false, "enum_values": []}, "Description": {"... (+484 chars omitted),+1 more (map truncated)
  IfcType = 172
  Length = 0
  Material = -> Material
  MoveBase = false
  MoveWithHost = false
  Nodes = (2) [(15210,9900,0),(15210,9900,-8000)]
  NodesOffset = 0
  Normal = (0,0,0)
  PerimeterLength = 1570.8
  Placement = pos=(-9050,0,-1200) rot=(0,0,1;0rad)
  PredefinedType = 0
  VerticalArea = 1.25664e+07
  Width = 100
FEATURE [Part::FeaturePython] Structure008  label="CAB PIL 3"  # Arch/BIM 172 (typed FeaturePython)
  CloneOf = -> Structure
  FaceMaker = 0
  Height = 700
  HorizontalArea = 490000
  IfcData = attributes={"GlobalId": {"name": "GlobalId", "type": "IfcGloballyUniqueId", "is_enum": false, "enum_values": []}, "Description": {"... (+510 chars omitted),+1 more (map truncated)
  IfcType = 172
  Length = 0
  Material = -> Material
  MoveBase = false
  MoveWithHost = false
  Nodes = (2) [(15210,9900,0),(15210,9900,-700)]
  NodesOffset = 0
  Normal = (0,0,0)
  PerimeterLength = 2800
  Placement = pos=(-6200,0,-500) rot=(0,0,1;0rad)
  PredefinedType = 0
  Tag = B1 (70x70x70)
  VerticalArea = 1960000
  Width = 0
FEATURE [Part::FeaturePython] Structure009  label="PIL 3"  # Arch/BIM 172 (typed FeaturePython)
  CloneOf = -> Structure001
  FaceMaker = 0
  Height = 8000
  HorizontalArea = 196350
  IfcData = attributes={"GlobalId": {"name": "GlobalId", "type": "IfcGloballyUniqueId", "is_enum": false, "enum_values": []}, "Description": {"... (+484 chars omitted),+1 more (map truncated)
  IfcType = 172
  Length = 0
  Material = -> Material
  MoveBase = false
  MoveWithHost = false
  Nodes = (2) [(15210,9900,0),(15210,9900,-8000)]
  NodesOffset = 0
  Normal = (0,0,0)
  PerimeterLength = 1570.8
  Placement = pos=(-6200,0,-1200) rot=(0,0,1;0rad)
  PredefinedType = 0
  VerticalArea = 1.25664e+07
  Width = 100
FEATURE [Part::FeaturePython] Structure010  label="CAB PIL 4"  # Arch/BIM 172 (typed FeaturePython)
  CloneOf = -> Structure
  FaceMaker = 0
  Height = 700
  HorizontalArea = 490000
  IfcData = attributes={"GlobalId": {"name": "GlobalId", "type": "IfcGloballyUniqueId", "is_enum": false, "enum_values": []}, "Description": {"... (+510 chars omitted),+1 more (map truncated)
  IfcType = 172
  Length = 0
  Material = -> Material
  MoveBase = false
  MoveWithHost = false
  Nodes = (2) [(15210,9900,0),(15210,9900,-700)]
  NodesOffset = 0
  Normal = (0,0,0)
  PerimeterLength = 2800
  Placement = pos=(-3200,0,-500) rot=(0,0,1;0rad)
  PredefinedType = 0
  Tag = B1 (70x70x70)
  VerticalArea = 1960000
  Width = 0
FEATURE [Part::FeaturePython] Structure011  label="PIL 4"  # Arch/BIM 172 (typed FeaturePython)
  CloneOf = -> Structure001
  FaceMaker = 0
  Height = 8000
  HorizontalArea = 196350
  IfcData = attributes={"GlobalId": {"name": "GlobalId", "type": "IfcGloballyUniqueId", "is_enum": false, "enum_values": []}, "Description": {"... (+484 chars omitted),+1 more (map truncated)
  IfcType = 172
  Length = 0
  Material = -> Material
  MoveBase = false
  MoveWithHost = false
  Nodes = (2) [(15210,9900,0),(15210,9900,-8000)]
  NodesOffset = 0
  Normal = (0,0,0)
  PerimeterLength = 1570.8
  Placement = pos=(-3200,0,-1200) rot=(0,0,1;0rad)
  PredefinedType = 0
  VerticalArea = 1.25664e+07
  Width = 100
FEATURE [Part::FeaturePython] Structure012  label="CAB PIL 5"  # Arch/BIM 172 (typed FeaturePython)
  CloneOf = -> Structure
  FaceMaker = 0
  Height = 700
  HorizontalArea = 490000
  IfcData = attributes={"GlobalId": {"name": "GlobalId", "type": "IfcGloballyUniqueId", "is_enum": false, "enum_values": []}, "Description": {"... (+510 chars omitted),+1 more (map truncated)
  IfcType = 172
  Length = 0
  Material = -> Material
  MoveBase = false
  MoveWithHost = false
  Nodes = (2) [(15210,9900,0),(15210,9900,-700)]
  NodesOffset = 0
  Normal = (0,0,0)
  PerimeterLength = 2800
  Placement = pos=(-9.09e-13,0,-500) rot=(0,0,1;0rad)
  PredefinedType = 0
  Tag = B1 (70x70x70)
  VerticalArea = 1960000
  Width = 0
FEATURE [Part::FeaturePython] Structure013  label="PIL 5"  # Arch/BIM 172 (typed FeaturePython)
  CloneOf = -> Structure001
  FaceMaker = 0
  Height = 8000
  HorizontalArea = 196350
  IfcData = attributes={"GlobalId": {"name": "GlobalId", "type": "IfcGloballyUniqueId", "is_enum": false, "enum_values": []}, "Description": {"... (+484 chars omitted),+1 more (map truncated)
  IfcType = 172
  Length = 0
  Material = -> Material
  MoveBase = false
  MoveWithHost = false
  Nodes = (2) [(15210,9900,0),(15210,9900,-8000)]
  NodesOffset = 0
  Normal = (0,0,0)
  PerimeterLength = 1570.8
  Placement = pos=(-9.09e-13,0,-1200) rot=(0,0,1;0rad)
  PredefinedType = 0
  VerticalArea = 1.25664e+07
  Width = 100
FEATURE [Part::FeaturePython] Structure014  label="CAB PIL 7"  # Arch/BIM 172 (typed FeaturePython)
  CloneOf = -> Structure
  FaceMaker = 0
  Height = 700
  HorizontalArea = 490000
  IfcData = attributes={"GlobalId": {"name": "GlobalId", "type": "IfcGloballyUniqueId", "is_enum": false, "enum_values": []}, "Description": {"... (+510 chars omitted),+1 more (map truncated)
  IfcType = 172
  Length = 0
  Material = -> Material
  MoveBase = false
  MoveWithHost = false
  Nodes = (2) [(15210,9900,0),(15210,9900,-700)]
  NodesOffset = 0
  Normal = (0,0,0)
  PerimeterLength = 2800
  Placement = pos=(-9050,-3260,-500) rot=(0,0,1;0rad)
  PredefinedType = 0
  Tag = B1 (70x70x70)
  VerticalArea = 1960000
  Width = 0
FEATURE [Part::FeaturePython] Structure015  label="PIL 7"  # Arch/BIM 172 (typed FeaturePython)
  CloneOf = -> Structure001
  FaceMaker = 0
  Height = 8000
  HorizontalArea = 196350
  IfcData = attributes={"GlobalId": {"name": "GlobalId", "type": "IfcGloballyUniqueId", "is_enum": false, "enum_values": []}, "Description": {"... (+484 chars omitted),+1 more (map truncated)
  IfcType = 172
  Length = 0
  Material = -> Material
  MoveBase = false
  MoveWithHost = false
  Nodes = (2) [(15210,9900,0),(15210,9900,-8000)]
  NodesOffset = 0
  Normal = (0,0,0)
  PerimeterLength = 1570.8
  Placement = pos=(-9050,-3260,-1200) rot=(0,0,1;0rad)
  PredefinedType = 0
  VerticalArea = 1.25664e+07
  Width = 100
FEATURE [Part::FeaturePython] Structure016  label="CAB PIL 8"  # Arch/BIM 172 (typed FeaturePython)
  CloneOf = -> Structure
  FaceMaker = 0
  Height = 700
  HorizontalArea = 490000
  IfcData = attributes={"GlobalId": {"name": "GlobalId", "type": "IfcGloballyUniqueId", "is_enum": false, "enum_values": []}, "Description": {"... (+510 chars omitted),+1 more (map truncated)
  IfcType = 172
  Length = 0
  Material = -> Material
  MoveBase = false
  MoveWithHost = false
  Nodes = (2) [(15210,9900,0),(15210,9900,-700)]
  NodesOffset = 0
  Normal = (0,0,0)
  PerimeterLength = 2800
  Placement = pos=(-6200,-3260,-500) rot=(0,0,1;0rad)
  PredefinedType = 0
  Tag = B1 (70x70x70)
  VerticalArea = 1960000
  Width = 0
FEATURE [Part::FeaturePython] Structure017  label="PIL 8"  # Arch/BIM 172 (typed FeaturePython)
  CloneOf = -> Structure001
  FaceMaker = 0
  Height = 8000
  HorizontalArea = 196350
  IfcData = attributes={"GlobalId": {"name": "GlobalId", "type": "IfcGloballyUniqueId", "is_enum": false, "enum_values": []}, "Description": {"... (+484 chars omitted),+1 more (map truncated)
  IfcType = 172
  Length = 0
  Material = -> Material
  MoveBase = false
  MoveWithHost = false
  Nodes = (2) [(15210,9900,0),(15210,9900,-8000)]
  NodesOffset = 0
  Normal = (0,0,0)
  PerimeterLength = 1570.8
  Placement = pos=(-6200,-3260,-1200) rot=(0,0,1;0rad)
  PredefinedType = 0
  VerticalArea = 1.25664e+07
  Width = 100
FEATURE [Part::FeaturePython] Structure018  label="CAB PIL 9"  # Arch/BIM 172 (typed FeaturePython)
  CloneOf = -> Structure
  FaceMaker = 0
  Height = 700
  HorizontalArea = 490000
  IfcData = attributes={"GlobalId": {"name": "GlobalId", "type": "IfcGloballyUniqueId", "is_enum": false, "enum_values": []}, "Description": {"... (+510 chars omitted),+1 more (map truncated)
  IfcType = 172
  Length = 0
  Material = -> Material
  MoveBase = false
  MoveWithHost = false
  Nodes = (2) [(15210,9900,0),(15210,9900,-700)]
  NodesOffset = 0
  Normal = (0,0,0)
  PerimeterLength = 2800
  Placement = pos=(-1430,-3930,-500) rot=(0,0,1;0rad)
  PredefinedType = 0
  Tag = B1 (70x70x70)
  VerticalArea = 1960000
  Width = 0
FEATURE [Part::FeaturePython] Structure019  label="PIL 9"  # Arch/BIM 172 (typed FeaturePython)
  CloneOf = -> Structure001
  FaceMaker = 0
  Height = 8000
  HorizontalArea = 196350
  IfcData = attributes={"GlobalId": {"name": "GlobalId", "type": "IfcGloballyUniqueId", "is_enum": false, "enum_values": []}, "Description": {"... (+484 chars omitted),+1 more (map truncated)
  IfcType = 172
  Length = 0
  Material = -> Material
  MoveBase = false
  MoveWithHost = false
  Nodes = (2) [(15210,9900,0),(15210,9900,-8000)]
  NodesOffset = 0
  Normal = (0,0,0)
  PerimeterLength = 1570.8
  Placement = pos=(-1430,-3930,-1200) rot=(0,0,1;0rad)
  PredefinedType = 0
  VerticalArea = 1.25664e+07
  Width = 100
FEATURE [Part::FeaturePython] Structure020  label="CAB PIL 10"  # Arch/BIM 172 (typed FeaturePython)
  CloneOf = -> Structure
  FaceMaker = 0
  Height = 700
  HorizontalArea = 490000
  IfcData = attributes={"GlobalId": {"name": "GlobalId", "type": "IfcGloballyUniqueId", "is_enum": false, "enum_values": []}, "Description": {"... (+510 chars omitted),+1 more (map truncated)
  IfcType = 172
  Length = 0
  Material = -> Material
  MoveBase = false
  MoveWithHost = false
  Nodes = (2) [(15210,9900,0),(15210,9900,-700)]
  NodesOffset = 0
  Normal = (0,0,0)
  PerimeterLength = 2800
  Placement = pos=(-9.09e-13,-3930,-500) rot=(0,0,1;0rad)
  PredefinedType = 0
  Tag = B1 (70x70x70)
  VerticalArea = 1960000
  Width = 0
FEATURE [Part::FeaturePython] Structure021  label="PIL 10"  # Arch/BIM 172 (typed FeaturePython)
  CloneOf = -> Structure001
  FaceMaker = 0
  Height = 8000
  HorizontalArea = 196350
  IfcData = attributes={"GlobalId": {"name": "GlobalId", "type": "IfcGloballyUniqueId", "is_enum": false, "enum_values": []}, "Description": {"... (+484 chars omitted),+1 more (map truncated)
  IfcType = 172
  Length = 0
  Material = -> Material
  MoveBase = false
  MoveWithHost = false
  Nodes = (2) [(15210,9900,0),(15210,9900,-8000)]
  NodesOffset = 0
  Normal = (0,0,0)
  PerimeterLength = 1570.8
  Placement = pos=(-9.09e-13,-3930,-1200) rot=(0,0,1;0rad)
  PredefinedType = 0
  VerticalArea = 1.25664e+07
  Width = 100
FEATURE [Part::FeaturePython] Structure022  label="CAB PIL 12"  # Arch/BIM 172 (typed FeaturePython)
  CloneOf = -> Structure
  FaceMaker = 0
  Height = 700
  HorizontalArea = 490000
  IfcData = attributes={"GlobalId": {"name": "GlobalId", "type": "IfcGloballyUniqueId", "is_enum": false, "enum_values": []}, "Description": {"... (+510 chars omitted),+1 more (map truncated)
  IfcType = 172
  Length = 0
  Material = -> Material
  MoveBase = false
  MoveWithHost = false
  Nodes = (2) [(15210,9900,0),(15210,9900,-700)]
  NodesOffset = 0
  Normal = (0,0,0)
  PerimeterLength = 2800
  Placement = pos=(-9050,-6550,-500) rot=(0,0,1;0rad)
  PredefinedType = 0
  Tag = B1 (70x70x70)
  VerticalArea = 1960000
  Width = 0
FEATURE [Part::FeaturePython] Structure023  label="PIL 12"  # Arch/BIM 172 (typed FeaturePython)
  CloneOf = -> Structure001
  FaceMaker = 0
  Height = 8000
  HorizontalArea = 196350
  IfcData = attributes={"GlobalId": {"name": "GlobalId", "type": "IfcGloballyUniqueId", "is_enum": false, "enum_values": []}, "Description": {"... (+484 chars omitted),+1 more (map truncated)
  IfcType = 172
  Length = 0
  Material = -> Material
  MoveBase = false
  MoveWithHost = false
  Nodes = (2) [(15210,9900,0),(15210,9900,-8000)]
  NodesOffset = 0
  Normal = (0,0,0)
  PerimeterLength = 1570.8
  Placement = pos=(-9050,-6550,-1200) rot=(0,0,1;0rad)
  PredefinedType = 0
  VerticalArea = 1.25664e+07
  Width = 100
FEATURE [Part::FeaturePython] Structure024  label="CAB PIL 13"  # Arch/BIM 172 (typed FeaturePython)
  CloneOf = -> Structure
  FaceMaker = 0
  Height = 700
  HorizontalArea = 490000
  IfcData = attributes={"GlobalId": {"name": "GlobalId", "type": "IfcGloballyUniqueId", "is_enum": false, "enum_values": []}, "Description": {"... (+510 chars omitted),+1 more (map truncated)
  IfcType = 172
  Length = 0
  Material = -> Material
  MoveBase = false
  MoveWithHost = false
  Nodes = (2) [(15210,9900,0),(15210,9900,-700)]
  NodesOffset = 0
  Normal = (0,0,0)
  PerimeterLength = 2800
  Placement = pos=(-6200,-6550,-500) rot=(0,0,1;0rad)
  PredefinedType = 0
  Tag = B1 (70x70x70)
  VerticalArea = 1960000
  Width = 0
FEATURE [Part::FeaturePython] Structure025  label="PIL 13"  # Arch/BIM 172 (typed FeaturePython)
  CloneOf = -> Structure001
  FaceMaker = 0
  Height = 8000
  HorizontalArea = 196350
  IfcData = attributes={"GlobalId": {"name": "GlobalId", "type": "IfcGloballyUniqueId", "is_enum": false, "enum_values": []}, "Description": {"... (+484 chars omitted),+1 more (map truncated)
  IfcType = 172
  Length = 0
  Material = -> Material
  MoveBase = false
  MoveWithHost = false
  Nodes = (2) [(15210,9900,0),(15210,9900,-8000)]
  NodesOffset = 0
  Normal = (0,0,0)
  PerimeterLength = 1570.8
  Placement = pos=(-6200,-6550,-1200) rot=(0,0,1;0rad)
  PredefinedType = 0
  VerticalArea = 1.25664e+07
  Width = 100
FEATURE [Part::FeaturePython] Structure026  label="CAB PIL 14"  # Arch/BIM 172 (typed FeaturePython)
  CloneOf = -> Structure
  FaceMaker = 0
  Height = 700
  HorizontalArea = 490000
  IfcData = attributes={"GlobalId": {"name": "GlobalId", "type": "IfcGloballyUniqueId", "is_enum": false, "enum_values": []}, "Description": {"... (+510 chars omitted),+1 more (map truncated)
  IfcType = 172
  Length = 0
  Material = -> Material
  MoveBase = false
  MoveWithHost = false
  Nodes = (2) [(15210,9900,0),(15210,9900,-700)]
  NodesOffset = 0
  Normal = (0,0,0)
  PerimeterLength = 2800
  Placement = pos=(-4650,-6550,-500) rot=(0,0,1;0rad)
  PredefinedType = 0
  Tag = B1 (70x70x70)
  VerticalArea = 1960000
  Width = 0
FEATURE [Part::FeaturePython] Structure027  label="PIL 14"  # Arch/BIM 172 (typed FeaturePython)
  CloneOf = -> Structure001
  FaceMaker = 0
  Height = 8000
  HorizontalArea = 196350
  IfcData = attributes={"GlobalId": {"name": "GlobalId", "type": "IfcGloballyUniqueId", "is_enum": false, "enum_values": []}, "Description": {"... (+484 chars omitted),+1 more (map truncated)
  IfcType = 172
  Length = 0
  Material = -> Material
  MoveBase = false
  MoveWithHost = false
  Nodes = (2) [(15210,9900,0),(15210,9900,-8000)]
  NodesOffset = 0
  Normal = (0,0,0)
  PerimeterLength = 1570.8
  Placement = pos=(-4650,-6550,-1200) rot=(0,0,1;0rad)
  PredefinedType = 0
  VerticalArea = 1.25664e+07
  Width = 100
FEATURE [Part::FeaturePython] Structure028  label="PIL 15"  # Arch/BIM 172 (typed FeaturePython)
  CloneOf = -> Structure001
  FaceMaker = 0
  Height = 8000
  HorizontalArea = 196350
  IfcData = attributes={"GlobalId": {"name": "GlobalId", "type": "IfcGloballyUniqueId", "is_enum": false, "enum_values": []}, "Description": {"... (+484 chars omitted),+1 more (map truncated)
  IfcType = 172
  Length = 0
  Material = -> Material
  MoveBase = false
  MoveWithHost = false
  Nodes = (2) [(15210,9900,0),(15210,9900,-8000)]
  NodesOffset = 0
  Normal = (0,0,0)
  PerimeterLength = 1570.8
  Placement = pos=(-1430,-6550,-1200) rot=(0,0,1;0rad)
  PredefinedType = 0
  VerticalArea = 1.25664e+07
  Width = 100
FEATURE [Part::FeaturePython] Structure029  label="CAB PIL 15"  # Arch/BIM 172 (typed FeaturePython)
  CloneOf = -> Structure
  FaceMaker = 0
  Height = 700
  HorizontalArea = 490000
  IfcData = attributes={"GlobalId": {"name": "GlobalId", "type": "IfcGloballyUniqueId", "is_enum": false, "enum_values": []}, "Description": {"... (+510 chars omitted),+1 more (map truncated)
  IfcType = 172
  Length = 0
  Material = -> Material
  MoveBase = false
  MoveWithHost = false
  Nodes = (2) [(15210,9900,0),(15210,9900,-700)]
  NodesOffset = 0
  Normal = (0,0,0)
  PerimeterLength = 2800
  Placement = pos=(-1430,-6550,-500) rot=(0,0,1;0rad)
  PredefinedType = 0
  Tag = B1 (70x70x70)
  VerticalArea = 1960000
  Width = 0
FEATURE [Part::FeaturePython] Structure030  label="CAB PIL 16"  # Arch/BIM 172 (typed FeaturePython)
  CloneOf = -> Structure
  FaceMaker = 0
  Height = 700
  HorizontalArea = 490000
  IfcData = attributes={"GlobalId": {"name": "GlobalId", "type": "IfcGloballyUniqueId", "is_enum": false, "enum_values": []}, "Description": {"... (+510 chars omitted),+1 more (map truncated)
  IfcType = 172
  Length = 0
  Material = -> Material
  MoveBase = false
  MoveWithHost = false
  Nodes = (2) [(15210,9900,0),(15210,9900,-700)]
  NodesOffset = 0
  Normal = (0,0,0)
  PerimeterLength = 2800
  Placement = pos=(-13280,-9800,-500) rot=(0,0,1;0rad)
  PredefinedType = 0
  Tag = B1 (70x70x70)
  VerticalArea = 1960000
  Width = 0
FEATURE [Part::FeaturePython] Structure031  label="PIL 16"  # Arch/BIM 172 (typed FeaturePython)
  CloneOf = -> Structure001
  FaceMaker = 0
  Height = 8000
  HorizontalArea = 196350
  IfcData = attributes={"GlobalId": {"name": "GlobalId", "type": "IfcGloballyUniqueId", "is_enum": false, "enum_values": []}, "Description": {"... (+484 chars omitted),+1 more (map truncated)
  IfcType = 172
  Length = 0
  Material = -> Material
  MoveBase = false
  MoveWithHost = false
  Nodes = (2) [(15210,9900,0),(15210,9900,-8000)]
  NodesOffset = 0
  Normal = (0,0,0)
  PerimeterLength = 1570.8
  Placement = pos=(-13280,-9800,-1200) rot=(0,0,1;0rad)
  PredefinedType = 0
  VerticalArea = 1.25664e+07
  Width = 100
FEATURE [Part::FeaturePython] Structure032  label="CAB PIL 17"  # Arch/BIM 172 (typed FeaturePython)
  CloneOf = -> Structure
  FaceMaker = 0
  Height = 700
  HorizontalArea = 490000
  IfcData = attributes={"GlobalId": {"name": "GlobalId", "type": "IfcGloballyUniqueId", "is_enum": false, "enum_values": []}, "Description": {"... (+510 chars omitted),+1 more (map truncated)
  IfcType = 172
  Length = 0
  Material = -> Material
  MoveBase = false
  MoveWithHost = false
  Nodes = (2) [(15210,9900,0),(15210,9900,-700)]
  NodesOffset = 0
  Normal = (0,0,0)
  PerimeterLength = 2800
  Placement = pos=(-9050,-9800,-500) rot=(0,0,1;0rad)
  PredefinedType = 0
  Tag = B1 (70x70x70)
  VerticalArea = 1960000
  Width = 0
FEATURE [Part::FeaturePython] Structure033  label="PIL 17"  # Arch/BIM 172 (typed FeaturePython)
  CloneOf = -> Structure001
  FaceMaker = 0
  Height = 8000
  HorizontalArea = 196350
  IfcData = attributes={"GlobalId": {"name": "GlobalId", "type": "IfcGloballyUniqueId", "is_enum": false, "enum_values": []}, "Description": {"... (+484 chars omitted),+1 more (map truncated)
  IfcType = 172
  Length = 0
  Material = -> Material
  MoveBase = false
  MoveWithHost = false
  Nodes = (2) [(15210,9900,0),(15210,9900,-8000)]
  NodesOffset = 0
  Normal = (0,0,0)
  PerimeterLength = 1570.8
  Placement = pos=(-9050,-9800,-1200) rot=(0,0,1;0rad)
  PredefinedType = 0
  VerticalArea = 1.25664e+07
  Width = 100
FEATURE [Part::FeaturePython] Structure034  label="CAB PIL 18"  # Arch/BIM 172 (typed FeaturePython)
  CloneOf = -> Structure
  FaceMaker = 0
  Height = 700
  HorizontalArea = 490000
  IfcData = attributes={"GlobalId": {"name": "GlobalId", "type": "IfcGloballyUniqueId", "is_enum": false, "enum_values": []}, "Description": {"... (+510 chars omitted),+1 more (map truncated)
  IfcType = 172
  Length = 0
  Material = -> Material
  MoveBase = false
  MoveWithHost = false
  Nodes = (2) [(15210,9900,0),(15210,9900,-700)]
  NodesOffset = 0
  Normal = (0,0,0)
  PerimeterLength = 2800
  Placement = pos=(-6200,-9800,-500) rot=(0,0,1;0rad)
  PredefinedType = 0
  Tag = B1 (70x70x70)
  VerticalArea = 1960000
  Width = 0
FEATURE [Part::FeaturePython] Structure035  label="PIL 18"  # Arch/BIM 172 (typed FeaturePython)
  CloneOf = -> Structure001
  FaceMaker = 0
  Height = 8000
  HorizontalArea = 196350
  IfcData = attributes={"GlobalId": {"name": "GlobalId", "type": "IfcGloballyUniqueId", "is_enum": false, "enum_values": []}, "Description": {"... (+484 chars omitted),+1 more (map truncated)
  IfcType = 172
  Length = 0
  Material = -> Material
  MoveBase = false
  MoveWithHost = false
  Nodes = (2) [(15210,9900,0),(15210,9900,-8000)]
  NodesOffset = 0
  Normal = (0,0,0)
  PerimeterLength = 1570.8
  Placement = pos=(-6200,-9800,-1200) rot=(0,0,1;0rad)
  PredefinedType = 0
  VerticalArea = 1.25664e+07
  Width = 100
FEATURE [Part::FeaturePython] Structure036  label="CAB PIL 19"  # Arch/BIM 172 (typed FeaturePython)
  CloneOf = -> Structure
  FaceMaker = 0
  Height = 700
  HorizontalArea = 490000
  IfcData = attributes={"GlobalId": {"name": "GlobalId", "type": "IfcGloballyUniqueId", "is_enum": false, "enum_values": []}, "Description": {"... (+510 chars omitted),+1 more (map truncated)
  IfcType = 172
  Length = 0
  Material = -> Material
  MoveBase = false
  MoveWithHost = false
  Nodes = (2) [(15210,9900,0),(15210,9900,-700)]
  NodesOffset = 0
  Normal = (0,0,0)
  PerimeterLength = 2800
  Placement = pos=(-4650,-9800,-500) rot=(0,0,1;0rad)
  PredefinedType = 0
  Tag = B1 (70x70x70)
  VerticalArea = 1960000
  Width = 0
FEATURE [Part::FeaturePython] Structure037  label="PIL 19"  # Arch/BIM 172 (typed FeaturePython)
  CloneOf = -> Structure001
  FaceMaker = 0
  Height = 8000
  HorizontalArea = 196350
  IfcData = attributes={"GlobalId": {"name": "GlobalId", "type": "IfcGloballyUniqueId", "is_enum": false, "enum_values": []}, "Description": {"... (+484 chars omitted),+1 more (map truncated)
  IfcType = 172
  Length = 0
  Material = -> Material
  MoveBase = false
  MoveWithHost = false
  Nodes = (2) [(15210,9900,0),(15210,9900,-8000)]
  NodesOffset = 0
  Normal = (0,0,0)
  PerimeterLength = 1570.8
  Placement = pos=(-4650,-9800,-1200) rot=(0,0,1;0rad)
  PredefinedType = 0
  VerticalArea = 1.25664e+07
  Width = 100
FEATURE [Part::FeaturePython] Structure038  label="CAB PIL 20"  # Arch/BIM 172 (typed FeaturePython)
  CloneOf = -> Structure
  FaceMaker = 0
  Height = 700
  HorizontalArea = 490000
  IfcData = attributes={"GlobalId": {"name": "GlobalId", "type": "IfcGloballyUniqueId", "is_enum": false, "enum_values": []}, "Description": {"... (+510 chars omitted),+1 more (map truncated)
  IfcType = 172
  Length = 0
  Material = -> Material
  MoveBase = false
  MoveWithHost = false
  Nodes = (2) [(15210,9900,0),(15210,9900,-700)]
  NodesOffset = 0
  Normal = (0,0,0)
  PerimeterLength = 2800
  Placement = pos=(-1430,-9800,-500) rot=(0,0,1;0rad)
  PredefinedType = 0
  Tag = B1 (70x70x70)
  VerticalArea = 1960000
  Width = 0
FEATURE [Part::FeaturePython] Structure039  label="PIL 20"  # Arch/BIM 172 (typed FeaturePython)
  CloneOf = -> Structure001
  FaceMaker = 0
  Height = 8000
  HorizontalArea = 196350
  IfcData = attributes={"GlobalId": {"name": "GlobalId", "type": "IfcGloballyUniqueId", "is_enum": false, "enum_values": []}, "Description": {"... (+484 chars omitted),+1 more (map truncated)
  IfcType = 172
  Length = 0
  Material = -> Material
  MoveBase = false
  MoveWithHost = false
  Nodes = (2) [(15210,9900,0),(15210,9900,-8000)]
  NodesOffset = 0
  Normal = (0,0,0)
  PerimeterLength = 1570.8
  Placement = pos=(-1430,-9800,-1200) rot=(0,0,1;0rad)
  PredefinedType = 0
  VerticalArea = 1.25664e+07
  Width = 100
FEATURE [Part::FeaturePython] Structure040  label="L01"  # Arch/BIM 172 (typed FeaturePython)
  FaceMaker = 0
  Height = 250
  HorizontalArea = 9230000
  IfcData = attributes={"GlobalId": {"name": "GlobalId", "type": "IfcGloballyUniqueId", "is_enum": false, "enum_values": []}, "Description": {"... (+512 chars omitted),+1 more (map truncated)
  IfcType = 172
  Length = 0
  Material = -> Material
  MoveBase = false
  MoveWithHost = false
  Nodes = (2) [(18300,6875,0),(18300,6875,-250)]
  NodesOffset = 0
  Normal = (0,0,-1)
  PerimeterLength = 12300
  Placement = pos=(-7015,295,-1000) rot=(0,0,1;0rad)
  PredefinedType = 0
  Tag = L01 (Esp 25 cm)
  VerticalArea = 3075000
  Width = 100
FEATURE [Part::FeaturePython] Structure081  label="25x15 C1"  # Arch/BIM 24 (typed FeaturePython)
  FaceMaker = 0
  Height = 3500
  HorizontalArea = 37500
  IfcData = attributes={"GlobalId": {"name": "GlobalId", "type": "IfcGloballyUniqueId", "is_enum": false, "enum_values": []}, "Description": {"... (+462 chars omitted),+1 more (map truncated)
  IfcType = 24
  Length = 250
  Material = -> Material
  MoveBase = false
  MoveWithHost = false
  Nodes = (2) [(-1.05471e-15,1.36424e-15,0),(-1.05471e-15,1.36424e-15,3500)]
  NodesOffset = 0
  Normal = (0,0,0)
  PerimeterLength = 800
  Placement = pos=(1930,9900,-500) rot=(0,0,1;0rad)
  PredefinedType = 0
  Tag = C01 (25x15)
  VerticalArea = 2.8e+06
  Width = 150
FEATURE [Part::FeaturePython] Structure084  label="25x15 C004"  # Arch/BIM 172 (typed FeaturePython)
  CloneOf = -> Structure081
  FaceMaker = 0
  Height = 3500
  HorizontalArea = 37500
  IfcData = attributes={"GlobalId": {"name": "GlobalId", "type": "IfcGloballyUniqueId", "is_enum": false, "enum_values": []}, "Description": {"... (+508 chars omitted),+1 more (map truncated)
  IfcType = 172
  Length = 250
  Material = -> Material
  MoveBase = false
  MoveWithHost = false
  Nodes = (2) [(-1.05471e-15,1.36424e-15,0),(-1.05471e-15,1.36424e-15,3500)]
  NodesOffset = 0
  Normal = (0,0,0)
  PerimeterLength = 800
  Placement = pos=(1930,100,-500) rot=(0,0,1;0rad)
  PredefinedType = 0
  Tag = C01 (25x15)
  VerticalArea = 2.8e+06
  Width = 150
FEATURE [Part::FeaturePython] Structure085  label="25x20 C6"  # Arch/BIM 24 (typed FeaturePython)
  FaceMaker = 0
  Height = 3500
  HorizontalArea = 50000
  IfcData = attributes={"GlobalId": {"name": "GlobalId", "type": "IfcGloballyUniqueId", "is_enum": false, "enum_values": []}, "Description": {"... (+462 chars omitted),+1 more (map truncated)
  IfcType = 24
  Length = 250
  Material = -> Material
  MoveBase = false
  MoveWithHost = false
  Nodes = (2) [(-1.05471e-15,-1.81899e-15,0),(-1.05471e-15,-1.81899e-15,3500)]
  NodesOffset = 0
  Normal = (0,0,0)
  PerimeterLength = 900
  Placement = pos=(1930,6640,-500) rot=(0,0,1;0rad)
  PredefinedType = 0
  Tag = C02 (25x20)
  VerticalArea = 3.15e+06
  Width = 200
FEATURE [Part::FeaturePython] Structure086  label="25x20 C007"  # Arch/BIM 172 (typed FeaturePython)
  CloneOf = -> Structure085
  FaceMaker = 0
  Height = 3500
  HorizontalArea = 50000
  IfcData = attributes={"GlobalId": {"name": "GlobalId", "type": "IfcGloballyUniqueId", "is_enum": false, "enum_values": []}, "Description": {"... (+508 chars omitted),+1 more (map truncated)
  IfcType = 172
  Length = 250
  Material = -> Material
  MoveBase = false
  MoveWithHost = false
  Nodes = (2) [(-1.05471e-15,-1.81899e-15,0),(-1.05471e-15,-1.81899e-15,3500)]
  NodesOffset = 0
  Normal = (0,0,0)
  PerimeterLength = 900
  Placement = pos=(1930,3350,-500) rot=(0,0,1;0rad)
  PredefinedType = 0
  Tag = C02 (25x20)
  VerticalArea = 3.15e+06
  Width = 200
FEATURE [Part::FeaturePython] Structure088  label="25x15 C005"  # Arch/BIM 24 (typed FeaturePython)
  FaceMaker = 0
  Height = 3500
  HorizontalArea = 37500
  IfcData = attributes={"GlobalId": {"name": "GlobalId", "type": "IfcGloballyUniqueId", "is_enum": false, "enum_values": []}, "Description": {"... (+462 chars omitted),+1 more (map truncated)
  IfcType = 24
  Length = 250
  Material = -> Material
  MoveBase = false
  MoveWithHost = false
  Nodes = (2) [(-1.05471e-15,1.36424e-15,0),(-1.05471e-15,1.36424e-15,3500)]
  NodesOffset = 0
  Normal = (0,0,0)
  PerimeterLength = 800
  Placement = pos=(6160,6640,-500) rot=(0,0,1;0rad)
  PredefinedType = 0
  Tag = C01 (25x15)
  VerticalArea = 2.8e+06
  Width = 150
FEATURE [Part::FeaturePython] Structure089  label="25x15 C006"  # Arch/BIM 24 (typed FeaturePython)
  FaceMaker = 0
  Height = 3500
  HorizontalArea = 37500
  IfcData = attributes={"GlobalId": {"name": "GlobalId", "type": "IfcGloballyUniqueId", "is_enum": false, "enum_values": []}, "Description": {"... (+462 chars omitted),+1 more (map truncated)
  IfcType = 24
  Length = 250
  Material = -> Material
  MoveBase = false
  MoveWithHost = false
  Nodes = (2) [(-1.05471e-15,1.36424e-15,0),(-1.05471e-15,1.36424e-15,3500)]
  NodesOffset = 0
  Normal = (0,0,0)
  PerimeterLength = 800
  Placement = pos=(6160,3350,-500) rot=(0,0,1;0rad)
  PredefinedType = 0
  Tag = C01 (25x15)
  VerticalArea = 2.8e+06
  Width = 150
FEATURE [Part::FeaturePython] Structure090  label="25x15 C007"  # Arch/BIM 24 (typed FeaturePython)
  FaceMaker = 0
  Height = 3500
  HorizontalArea = 37500
  IfcData = attributes={"GlobalId": {"name": "GlobalId", "type": "IfcGloballyUniqueId", "is_enum": false, "enum_values": []}, "Description": {"... (+462 chars omitted),+1 more (map truncated)
  IfcType = 24
  Length = 250
  Material = -> Material
  MoveBase = false
  MoveWithHost = false
  Nodes = (2) [(-1.05471e-15,1.36424e-15,0),(-1.05471e-15,1.36424e-15,3500)]
  NodesOffset = 0
  Normal = (0,0,0)
  PerimeterLength = 800
  Placement = pos=(6160,100,-500) rot=(0,0,1;0rad)
  PredefinedType = 0
  Tag = C01 (25x15)
  VerticalArea = 2.8e+06
  Width = 150
FEATURE [Part::FeaturePython] Structure091  label="25x15 C008"  # Arch/BIM 24 (typed FeaturePython)
  FaceMaker = 0
  Height = 3500
  HorizontalArea = 37500
  IfcData = attributes={"GlobalId": {"name": "GlobalId", "type": "IfcGloballyUniqueId", "is_enum": false, "enum_values": []}, "Description": {"... (+462 chars omitted),+1 more (map truncated)
  IfcType = 24
  Length = 250
  Material = -> Material
  MoveBase = false
  MoveWithHost = false
  Nodes = (2) [(-1.05471e-15,1.36424e-15,0),(-1.05471e-15,1.36424e-15,3500)]
  NodesOffset = 0
  Normal = (0,0,0)
  PerimeterLength = 800
  Placement = pos=(9010,100,-500) rot=(0,0,1;0rad)
  PredefinedType = 0
  Tag = C01 (25x15)
  VerticalArea = 2.8e+06
  Width = 150
FEATURE [Part::FeaturePython] Structure092  label="25x15 C009"  # Arch/BIM 24 (typed FeaturePython)
  FaceMaker = 0
  Height = 3500
  HorizontalArea = 37500
  IfcData = attributes={"GlobalId": {"name": "GlobalId", "type": "IfcGloballyUniqueId", "is_enum": false, "enum_values": []}, "Description": {"... (+462 chars omitted),+1 more (map truncated)
  IfcType = 24
  Length = 250
  Material = -> Material
  MoveBase = false
  MoveWithHost = false
  Nodes = (2) [(-1.05471e-15,1.36424e-15,0),(-1.05471e-15,1.36424e-15,3500)]
  NodesOffset = 0
  Normal = (0,0,0)
  PerimeterLength = 800
  Placement = pos=(10560,100,-500) rot=(0,0,1;0rad)
  PredefinedType = 0
  Tag = C01 (25x15)
  VerticalArea = 2.8e+06
  Width = 150
FEATURE [Part::FeaturePython] Structure093  label="25x15 C010"  # Arch/BIM 24 (typed FeaturePython)
  FaceMaker = 0
  Height = 3500
  HorizontalArea = 37500
  IfcData = attributes={"GlobalId": {"name": "GlobalId", "type": "IfcGloballyUniqueId", "is_enum": false, "enum_values": []}, "Description": {"... (+462 chars omitted),+1 more (map truncated)
  IfcType = 24
  Length = 250
  Material = -> Material
  MoveBase = false
  MoveWithHost = false
  Nodes = (2) [(-1.05471e-15,1.36424e-15,0),(-1.05471e-15,1.36424e-15,3500)]
  NodesOffset = 0
  Normal = (0,0,0)
  PerimeterLength = 800
  Placement = pos=(13780,100,-500) rot=(0,0,1;0rad)
  PredefinedType = 0
  Tag = C01 (25x15)
  VerticalArea = 2.8e+06
  Width = 150
FEATURE [Part::FeaturePython] Structure097  label="25x15 C014"  # Arch/BIM 24 (typed FeaturePython)
  FaceMaker = 0
  Height = 3500
  HorizontalArea = 37500
  IfcData = attributes={"GlobalId": {"name": "GlobalId", "type": "IfcGloballyUniqueId", "is_enum": false, "enum_values": []}, "Description": {"... (+462 chars omitted),+1 more (map truncated)
  IfcType = 24
  Length = 250
  Material = -> Material
  MoveBase = false
  MoveWithHost = false
  Nodes = (2) [(-1.05471e-15,1.36424e-15,0),(-1.05471e-15,1.36424e-15,3500)]
  NodesOffset = 0
  Normal = (0,0,0)
  PerimeterLength = 800
  Placement = pos=(15210,5970,-500) rot=(0,0,1;0rad)
  PredefinedType = 0
  Tag = C01 (25x15)
  VerticalArea = 2.8e+06
  Width = 150
FEATURE [Part::FeaturePython] Structure098  label="25x15 C015"  # Arch/BIM 24 (typed FeaturePython)
  FaceMaker = 0
  Height = 3500
  HorizontalArea = 37500
  IfcData = attributes={"GlobalId": {"name": "GlobalId", "type": "IfcGloballyUniqueId", "is_enum": false, "enum_values": []}, "Description": {"... (+462 chars omitted),+1 more (map truncated)
  IfcType = 24
  Length = 250
  Material = -> Material
  MoveBase = false
  MoveWithHost = false
  Nodes = (2) [(-1.05471e-15,1.36424e-15,0),(-1.05471e-15,1.36424e-15,3500)]
  NodesOffset = 0
  Normal = (0,0,0)
  PerimeterLength = 800
  Placement = pos=(13780,5970,-500) rot=(0,0,1;0rad)
  PredefinedType = 0
  Tag = C01 (25x15)
  VerticalArea = 2.8e+06
  Width = 150
FEATURE [Part::FeaturePython] Wall  label="Tabique Ascensor"  # Arch/BIM 166 (typed FeaturePython)
  Align = 1
  Area = 8300000
  Base = -> Rectangle
  BlockHeight = 0
  BlockLength = 0
  CountBroken = 0
  CountEntire = 0
  Face = 0
  Height = 1000
  HorizontalArea = 1155000
  IfcData = attributes={"GlobalId": {"name": "GlobalId", "type": "IfcGloballyUniqueId", "is_enum": false, "enum_values": []}, "Description": {"... (+561 chars omitted),+1 more (map truncated)
  IfcType = 166
  Joint = 0
  Length = 8300
  MakeBlocks = false
  Material = -> Material
  MoveBase = false
  MoveWithHost = false
  Normal = (0,0,0)
  OffsetFirst = 0
  OffsetSecond = 0
  PerimeterLength = 8300
  Placement = pos=(0,0,-1000) rot=(0,0,1;0rad)
  PredefinedType = 0
  Tag = M01 (Esp 15 cm)
  VerticalArea = 15400000
  Width = 150
FEATURE [App::GeometryPython] BuildingPart006  label="Pilotes"  # Arch/BIM 172 (typed FeaturePython)
  Area = 0
  Group = -> [Structure001,Structure021,Structure005,Structure023,Structure025,Structure027,Structure028,Structure031,Structure033,Structure035,Structure037,Structure007,Structure039,Structure009,Structure011,Structure013,Structure003,Structure015,Structure017,Structure019]
  Height = 0
  HeightPropagate = true
  IfcData = attributes={"GlobalId": {"name": "GlobalId", "type": "IfcGloballyUniqueId", "is_enum": false, "enum_values": []}, "Description": {"... (+484 chars omitted),+1 more (map truncated)
  IfcType = 172
  LevelOffset = 0
  Placement = pos=(0,0,500) rot=(0,0,1;0rad)
  PredefinedType = 0
FEATURE [App::GeometryPython] BuildingPart007  label="Cabezales Pilotes"  # Arch/BIM 172 (typed FeaturePython)
  Area = 0
  Group = -> [Structure,Structure020,Structure004,Structure022,Structure024,Structure026,Structure029,Structure030,Structure032,Structure034,Structure036,Structure006,Structure038,Structure008,Structure010,Structure012,Structure002,Structure014,Structure016,Structure018]
  Height = 0
  HeightPropagate = true
  IfcData = attributes={"GlobalId": {"name": "GlobalId", "type": "IfcGloballyUniqueId", "is_enum": false, "enum_values": []}, "Description": {"... (+484 chars omitted),+1 more (map truncated)
  IfcType = 172
  LevelOffset = 0
  Placement = pos=(0,0,500) rot=(0,0,1;0rad)
  PredefinedType = 0
FEATURE [App::GeometryPython] BuildingPart008  label="Losa fundacion"  # Arch/BIM 172 (typed FeaturePython)
  Area = 0
  Group = -> [Structure040]
  Height = 0
  HeightPropagate = true
  IfcData = attributes={"GlobalId": {"name": "GlobalId", "type": "IfcGloballyUniqueId", "is_enum": false, "enum_values": []}, "Description": {"... (+484 chars omitted),+1 more (map truncated)
  IfcType = 172
  LevelOffset = 0
  Placement = pos=(0,0,500) rot=(0,0,1;0rad)
  PredefinedType = 0
FEATURE [Part::FeaturePython] Structure099  label="25x15 C016"  # Arch/BIM 172 (typed FeaturePython)
  CloneOf = -> Structure081
  FaceMaker = 0
  Height = 3500
  HorizontalArea = 37500
  IfcData = attributes={"GlobalId": {"name": "GlobalId", "type": "IfcGloballyUniqueId", "is_enum": false, "enum_values": []}, "Description": {"... (+508 chars omitted),+1 more (map truncated)
  IfcType = 172
  Length = 250
  Material = -> Material
  MoveBase = false
  MoveWithHost = false
  Nodes = (2) [(-1.05471e-15,1.36424e-15,0),(-1.05471e-15,1.36424e-15,3500)]
  NodesOffset = 0
  Normal = (0,0,0)
  PerimeterLength = 800
  Placement = pos=(1930,9900,-500) rot=(0,0,1;0rad)
  PredefinedType = 0
  Tag = C01 (25x15)
  VerticalArea = 2.8e+06
  Width = 150
FEATURE [Part::FeaturePython] Structure100  label="25x15 C017"  # Arch/BIM 172 (typed FeaturePython)
  CloneOf = -> Structure081
  FaceMaker = 0
  Height = 3500
  HorizontalArea = 37500
  IfcData = attributes={"GlobalId": {"name": "GlobalId", "type": "IfcGloballyUniqueId", "is_enum": false, "enum_values": []}, "Description": {"... (+508 chars omitted),+1 more (map truncated)
  IfcType = 172
  Length = 250
  Material = -> Material
  MoveBase = false
  MoveWithHost = false
  Nodes = (2) [(-1.05471e-15,1.36424e-15,0),(-1.05471e-15,1.36424e-15,3500)]
  NodesOffset = 0
  Normal = (0,0,0)
  PerimeterLength = 800
  Placement = pos=(9010,6640,-500) rot=(0,0,1;1.5708rad)
  PredefinedType = 0
  Tag = C01 (25x15)
  VerticalArea = 2.8e+06
  Width = 150
FEATURE [Part::FeaturePython] Structure101  label="25x15 C018"  # Arch/BIM 172 (typed FeaturePython)
  CloneOf = -> Structure081
  FaceMaker = 0
  Height = 3500
  HorizontalArea = 37500
  IfcData = attributes={"GlobalId": {"name": "GlobalId", "type": "IfcGloballyUniqueId", "is_enum": false, "enum_values": []}, "Description": {"... (+508 chars omitted),+1 more (map truncated)
  IfcType = 172
  Length = 250
  Material = -> Material
  MoveBase = false
  MoveWithHost = false
  Nodes = (2) [(-1.05471e-15,1.36424e-15,0),(-1.05471e-15,1.36424e-15,3500)]
  NodesOffset = 0
  Normal = (0,0,0)
  PerimeterLength = 800
  Placement = pos=(9010,3350,-500) rot=(0,0,1;1.5708rad)
  PredefinedType = 0
  Tag = C01 (25x15)
  VerticalArea = 2.8e+06
  Width = 150
FEATURE [Part::FeaturePython] Structure102  label="25x15 C019"  # Arch/BIM 172 (typed FeaturePython)
  CloneOf = -> Structure081
  FaceMaker = 0
  Height = 3500
  HorizontalArea = 37500
  IfcData = attributes={"GlobalId": {"name": "GlobalId", "type": "IfcGloballyUniqueId", "is_enum": false, "enum_values": []}, "Description": {"... (+508 chars omitted),+1 more (map truncated)
  IfcType = 172
  Length = 250
  Material = -> Material
  MoveBase = false
  MoveWithHost = false
  Nodes = (2) [(-1.05471e-15,1.36424e-15,0),(-1.05471e-15,1.36424e-15,3500)]
  NodesOffset = 0
  Normal = (0,0,0)
  PerimeterLength = 800
  Placement = pos=(10560,3350,-500) rot=(0,0,1;1.5708rad)
  PredefinedType = 0
  Tag = C01 (25x15)
  VerticalArea = 2.8e+06
  Width = 150
FEATURE [Part::FeaturePython] Structure103  label="25x15 C020"  # Arch/BIM 172 (typed FeaturePython)
  CloneOf = -> Structure081
  FaceMaker = 0
  Height = 3500
  HorizontalArea = 37500
  IfcData = attributes={"GlobalId": {"name": "GlobalId", "type": "IfcGloballyUniqueId", "is_enum": false, "enum_values": []}, "Description": {"... (+508 chars omitted),+1 more (map truncated)
  IfcType = 172
  Length = 250
  Material = -> Material
  MoveBase = false
  MoveWithHost = false
  Nodes = (2) [(-1.05471e-15,1.36424e-15,0),(-1.05471e-15,1.36424e-15,3500)]
  NodesOffset = 0
  Normal = (0,0,0)
  PerimeterLength = 800
  Placement = pos=(13780,3350,-500) rot=(0,0,1;1.5708rad)
  PredefinedType = 0
  Tag = C01 (25x15)
  VerticalArea = 2.8e+06
  Width = 150
FEATURE [Part::FeaturePython] Structure104  label="25x15 C003"  # Arch/BIM 172 (typed FeaturePython)
  CloneOf = -> Structure081
  FaceMaker = 0
  Height = 3500
  HorizontalArea = 37500
  IfcData = attributes={"GlobalId": {"name": "GlobalId", "type": "IfcGloballyUniqueId", "is_enum": false, "enum_values": []}, "Description": {"... (+508 chars omitted),+1 more (map truncated)
  IfcType = 172
  Length = 250
  Material = -> Material
  MoveBase = false
  MoveWithHost = false
  Nodes = (2) [(-1.05471e-15,1.36424e-15,0),(-1.05471e-15,1.36424e-15,3500)]
  NodesOffset = 0
  Normal = (0,0,0)
  PerimeterLength = 800
  Placement = pos=(9010,9900,-500) rot=(0,0,1;0rad)
  PredefinedType = 0
  Tag = C01 (25x15)
  VerticalArea = 2.8e+06
  Width = 150
FEATURE [Part::FeaturePython] Structure105  label="25x15 C002"  # Arch/BIM 172 (typed FeaturePython)
  CloneOf = -> Structure081
  FaceMaker = 0
  Height = 3500
  HorizontalArea = 37500
  IfcData = attributes={"GlobalId": {"name": "GlobalId", "type": "IfcGloballyUniqueId", "is_enum": false, "enum_values": []}, "Description": {"... (+508 chars omitted),+1 more (map truncated)
  IfcType = 172
  Length = 250
  Material = -> Material
  MoveBase = false
  MoveWithHost = false
  Nodes = (2) [(-1.05471e-15,1.36424e-15,0),(-1.05471e-15,1.36424e-15,3500)]
  NodesOffset = 0
  Normal = (0,0,0)
  PerimeterLength = 800
  Placement = pos=(6160,9900,-500) rot=(0,0,1;0rad)
  PredefinedType = 0
  Tag = C01 (25x15)
  VerticalArea = 2.8e+06
  Width = 150
FEATURE [Part::FeaturePython] Structure106  label="25x15 C025"  # Arch/BIM 172 (typed FeaturePython)
  CloneOf = -> Structure081
  FaceMaker = 0
  Height = 3500
  HorizontalArea = 37500
  IfcData = attributes={"GlobalId": {"name": "GlobalId", "type": "IfcGloballyUniqueId", "is_enum": false, "enum_values": []}, "Description": {"... (+508 chars omitted),+1 more (map truncated)
  IfcType = 172
  Length = 250
  Material = -> Material
  MoveBase = false
  MoveWithHost = false
  Nodes = (2) [(-1.05471e-15,1.36424e-15,0),(-1.05471e-15,1.36424e-15,3500)]
  NodesOffset = 0
  Normal = (0,0,0)
  PerimeterLength = 800
  Placement = pos=(12010,9900,-500) rot=(0,0,1;0rad)
  PredefinedType = 0
  Tag = C01 (25x15)
  VerticalArea = 2.8e+06
  Width = 150
FEATURE [Part::FeaturePython] Structure107  label="25x15 C024"  # Arch/BIM 172 (typed FeaturePython)
  CloneOf = -> Structure081
  FaceMaker = 0
  Height = 3500
  HorizontalArea = 37500
  IfcData = attributes={"GlobalId": {"name": "GlobalId", "type": "IfcGloballyUniqueId", "is_enum": false, "enum_values": []}, "Description": {"... (+508 chars omitted),+1 more (map truncated)
  IfcType = 172
  Length = 250
  Material = -> Material
  MoveBase = false
  MoveWithHost = false
  Nodes = (2) [(-1.05471e-15,1.36424e-15,0),(-1.05471e-15,1.36424e-15,3500)]
  NodesOffset = 0
  Normal = (0,0,0)
  PerimeterLength = 800
  Placement = pos=(15210,9900,-500) rot=(0,0,1;0rad)
  PredefinedType = 0
  Tag = C01 (25x15)
  VerticalArea = 2.8e+06
  Width = 150
FEATURE [Part::FeaturePython] Wall001  label="Tabique Ascensor PB"  # Arch/BIM 166 (typed FeaturePython)
  Align = 1
  Area = 24900000
  Base = -> Rectangle003
  BlockHeight = 0
  BlockLength = 0
  CountBroken = 0
  CountEntire = 0
  Face = 0
  Height = 3000
  HorizontalArea = 1155000
  IfcData = attributes={"GlobalId": {"name": "GlobalId", "type": "IfcGloballyUniqueId", "is_enum": false, "enum_values": []}, "Description": {"... (+533 chars omitted),+1 more (map truncated)
  IfcType = 166
  Joint = 0
  Length = 8300
  MakeBlocks = false
  Material = -> Material
  MoveBase = false
  MoveWithHost = false
  Normal = (0,0,0)
  OffsetFirst = 0
  OffsetSecond = 0
  PerimeterLength = 8300
  PredefinedType = 0
  VerticalArea = 46200000
  Width = 150
FEATURE [Part::FeaturePython] Structure108  label="V20x40 V122"  # Arch/BIM 7 (typed FeaturePython)
  FaceMaker = 0
  Height = 400
  HorizontalArea = 617000
  IfcData = attributes={"GlobalId": {"name": "GlobalId", "type": "IfcGloballyUniqueId", "is_enum": false, "enum_values": []}, "Description": {"... (+475 chars omitted),+1 more (map truncated)
  IfcType = 7
  Length = 3085
  Material = -> Material
  MoveBase = false
  MoveWithHost = false
  Nodes = (2) [(-1.72563e-31,0,-7.77156e-16),(3085,0,-7.77156e-16)]
  NodesOffset = 0
  Normal = (0,0,0)
  PerimeterLength = 6570
  Placement = pos=(1930,9825,2800) rot=(0,0,-1;1.5708rad)
  PredefinedType = 0
  VerticalArea = 2.628e+06
  Width = 200
FEATURE [Part::FeaturePython] Structure109  label="V15x40 V101"  # Arch/BIM 7 (typed FeaturePython)
  FaceMaker = 0
  Height = 400
  HorizontalArea = 597000
  IfcData = attributes={"GlobalId": {"name": "GlobalId", "type": "IfcGloballyUniqueId", "is_enum": false, "enum_values": []}, "Description": {"... (+500 chars omitted),+1 more (map truncated)
  IfcType = 7
  Length = 3980
  Material = -> Material
  MoveBase = false
  MoveWithHost = false
  Nodes = (2) [(-1.72563e-31,-1.42109e-15,-7.77156e-16),(3980,-1.42109e-15,-7.77156e-16)]
  NodesOffset = 0
  Normal = (0,0,0)
  PerimeterLength = 8260
  Placement = pos=(2055,9900,2800) rot=(0,0,1;0rad)
  PredefinedType = 0
  Tag = V101 (15x40)
  VerticalArea = 3.304e+06
  Width = 150
FEATURE [Part::FeaturePython] Structure110  label="V20x40 V121"  # Arch/BIM 7 (typed FeaturePython)
  FaceMaker = 0
  Height = 400
  HorizontalArea = 618000
  IfcData = attributes={"GlobalId": {"name": "GlobalId", "type": "IfcGloballyUniqueId", "is_enum": false, "enum_values": []}, "Description": {"... (+475 chars omitted),+1 more (map truncated)
  IfcType = 7
  Length = 3090
  Material = -> Material
  MoveBase = false
  MoveWithHost = false
  Nodes = (2) [(-1.72563e-31,0,-7.77156e-16),(3090,0,-7.77156e-16)]
  NodesOffset = 0
  Normal = (0,0,0)
  PerimeterLength = 6580
  Placement = pos=(1930,6540,2800) rot=(0,0,-1;1.5708rad)
  PredefinedType = 0
  VerticalArea = 2.632e+06
  Width = 200
FEATURE [Part::FeaturePython] Structure111  label="V20x40 V120"  # Arch/BIM 7 (typed FeaturePython)
  FaceMaker = 0
  Height = 400
  HorizontalArea = 615000
  IfcData = attributes={"GlobalId": {"name": "GlobalId", "type": "IfcGloballyUniqueId", "is_enum": false, "enum_values": []}, "Description": {"... (+475 chars omitted),+1 more (map truncated)
  IfcType = 7
  Length = 3075
  Material = -> Material
  MoveBase = false
  MoveWithHost = false
  Nodes = (2) [(-1.72563e-31,0,-7.77156e-16),(3075,0,-7.77156e-16)]
  NodesOffset = 0
  Normal = (0,0,0)
  PerimeterLength = 6550
  Placement = pos=(1930,3250,2800) rot=(0,0,-1;1.5708rad)
  PredefinedType = 0
  VerticalArea = 2.62e+06
  Width = 200
FEATURE [Part::FeaturePython] Structure112  label="V15x40 V106"  # Arch/BIM 7 (typed FeaturePython)
  FaceMaker = 0
  Height = 400
  HorizontalArea = 597000
  IfcData = attributes={"GlobalId": {"name": "GlobalId", "type": "IfcGloballyUniqueId", "is_enum": false, "enum_values": []}, "Description": {"... (+475 chars omitted),+1 more (map truncated)
  IfcType = 7
  Length = 3980
  Material = -> Material
  MoveBase = false
  MoveWithHost = false
  Nodes = (2) [(-1.72563e-31,-1.42109e-15,-7.77156e-16),(3980,-1.42109e-15,-7.77156e-16)]
  NodesOffset = 0
  Normal = (0,0,0)
  PerimeterLength = 8260
  Placement = pos=(2055,6640,2800) rot=(0,0,1;0rad)
  PredefinedType = 0
  VerticalArea = 3.304e+06
  Width = 150
FEATURE [Part::FeaturePython] Structure113  label="V15x40 V111"  # Arch/BIM 7 (typed FeaturePython)
  FaceMaker = 0
  Height = 400
  HorizontalArea = 597000
  IfcData = attributes={"GlobalId": {"name": "GlobalId", "type": "IfcGloballyUniqueId", "is_enum": false, "enum_values": []}, "Description": {"... (+475 chars omitted),+1 more (map truncated)
  IfcType = 7
  Length = 3980
  Material = -> Material
  MoveBase = false
  MoveWithHost = false
  Nodes = (2) [(-1.72563e-31,-1.42109e-15,-7.77156e-16),(3980,-1.42109e-15,-7.77156e-16)]
  NodesOffset = 0
  Normal = (0,0,0)
  PerimeterLength = 8260
  Placement = pos=(2055,3350,2800) rot=(0,0,1;0rad)
  PredefinedType = 0
  VerticalArea = 3.304e+06
  Width = 150
FEATURE [Part::FeaturePython] Structure114  label="V15x40 V116"  # Arch/BIM 7 (typed FeaturePython)
  FaceMaker = 0
  Height = 400
  HorizontalArea = 597000
  IfcData = attributes={"GlobalId": {"name": "GlobalId", "type": "IfcGloballyUniqueId", "is_enum": false, "enum_values": []}, "Description": {"... (+495 chars omitted),+1 more (map truncated)
  IfcType = 7
  Length = 3980
  Material = -> Material
  MoveBase = false
  MoveWithHost = false
  Nodes = (2) [(-1.72563e-31,-1.42109e-15,-7.77156e-16),(3980,-1.42109e-15,-7.77156e-16)]
  NodesOffset = 0
  Normal = (0,0,0)
  PerimeterLength = 8260
  Placement = pos=(2055,100,2800) rot=(0,0,1;0rad)
  PredefinedType = 0
  Tag = (15x40)
  VerticalArea = 3.304e+06
  Width = 150
FEATURE [Part::FeaturePython] Structure115  label="V15x40 V102"  # Arch/BIM 7 (typed FeaturePython)
  FaceMaker = 0
  Height = 400
  HorizontalArea = 390000
  IfcData = attributes={"GlobalId": {"name": "GlobalId", "type": "IfcGloballyUniqueId", "is_enum": false, "enum_values": []}, "Description": {"... (+475 chars omitted),+1 more (map truncated)
  IfcType = 7
  Length = 2600
  Material = -> Material
  MoveBase = false
  MoveWithHost = false
  Nodes = (2) [(-1.72563e-31,-1.42109e-15,-7.77156e-16),(2600,-1.42109e-15,-7.77156e-16)]
  NodesOffset = 0
  Normal = (0,0,0)
  PerimeterLength = 5500
  Placement = pos=(6285,9900,2800) rot=(0,0,1;0rad)
  PredefinedType = 0
  VerticalArea = 2200000
  Width = 150
FEATURE [Part::FeaturePython] Structure116  label="V15x40 V107"  # Arch/BIM 7 (typed FeaturePython)
  FaceMaker = 0
  Height = 400
  HorizontalArea = 397500
  IfcData = attributes={"GlobalId": {"name": "GlobalId", "type": "IfcGloballyUniqueId", "is_enum": false, "enum_values": []}, "Description": {"... (+475 chars omitted),+1 more (map truncated)
  IfcType = 7
  Length = 2650
  Material = -> Material
  MoveBase = false
  MoveWithHost = false
  Nodes = (2) [(-1.72563e-31,-1.42109e-15,-7.77156e-16),(2650,-1.42109e-15,-7.77156e-16)]
  NodesOffset = 0
  Normal = (0,0,0)
  PerimeterLength = 5600
  Placement = pos=(6285,6640,2800) rot=(0,0,1;0rad)
  PredefinedType = 0
  VerticalArea = 2240000
  Width = 150
FEATURE [Part::FeaturePython] Structure117  label="V15x40 V112"  # Arch/BIM 7 (typed FeaturePython)
  FaceMaker = 0
  Height = 400
  HorizontalArea = 397500
  IfcData = attributes={"GlobalId": {"name": "GlobalId", "type": "IfcGloballyUniqueId", "is_enum": false, "enum_values": []}, "Description": {"... (+475 chars omitted),+1 more (map truncated)
  IfcType = 7
  Length = 2650
  Material = -> Material
  MoveBase = false
  MoveWithHost = false
  Nodes = (2) [(-1.72563e-31,-1.42109e-15,-7.77156e-16),(2650,-1.42109e-15,-7.77156e-16)]
  NodesOffset = 0
  Normal = (0,0,0)
  PerimeterLength = 5600
  Placement = pos=(6285,3350,2800) rot=(0,0,1;0rad)
  PredefinedType = 0
  VerticalArea = 2240000
  Width = 150
FEATURE [Part::FeaturePython] Structure118  label="V15x40 V117"  # Arch/BIM 7 (typed FeaturePython)
  FaceMaker = 0
  Height = 400
  HorizontalArea = 390000
  IfcData = attributes={"GlobalId": {"name": "GlobalId", "type": "IfcGloballyUniqueId", "is_enum": false, "enum_values": []}, "Description": {"... (+475 chars omitted),+1 more (map truncated)
  IfcType = 7
  Length = 2600
  Material = -> Material
  MoveBase = false
  MoveWithHost = false
  Nodes = (2) [(-1.72563e-31,-1.42109e-15,-7.77156e-16),(2600,-1.42109e-15,-7.77156e-16)]
  NodesOffset = 0
  Normal = (0,0,0)
  PerimeterLength = 5500
  Placement = pos=(6285,100,2800) rot=(0,0,1;0rad)
  PredefinedType = 0
  VerticalArea = 2200000
  Width = 150
FEATURE [Part::FeaturePython] Structure119  label="V15x40 V103"  # Arch/BIM 7 (typed FeaturePython)
  FaceMaker = 0
  Height = 400
  HorizontalArea = 412500
  IfcData = attributes={"GlobalId": {"name": "GlobalId", "type": "IfcGloballyUniqueId", "is_enum": false, "enum_values": []}, "Description": {"... (+475 chars omitted),+1 more (map truncated)
  IfcType = 7
  Length = 2750
  Material = -> Material
  MoveBase = false
  MoveWithHost = false
  Nodes = (2) [(-1.72563e-31,-1.42109e-15,-7.77156e-16),(2750,-1.42109e-15,-7.77156e-16)]
  NodesOffset = 0
  Normal = (0,0,0)
  PerimeterLength = 5800
  Placement = pos=(9135,9900,2800) rot=(0,0,1;0rad)
  PredefinedType = 0
  VerticalArea = 2320000
  Width = 150
FEATURE [Part::FeaturePython] Structure120  label="V15x40 V104"  # Arch/BIM 7 (typed FeaturePython)
  FaceMaker = 0
  Height = 400
  HorizontalArea = 442500
  IfcData = attributes={"GlobalId": {"name": "GlobalId", "type": "IfcGloballyUniqueId", "is_enum": false, "enum_values": []}, "Description": {"... (+475 chars omitted),+1 more (map truncated)
  IfcType = 7
  Length = 2950
  Material = -> Material
  MoveBase = false
  MoveWithHost = false
  Nodes = (2) [(-1.72563e-31,-1.42109e-15,-7.77156e-16),(2950,-1.42109e-15,-7.77156e-16)]
  NodesOffset = 0
  Normal = (0,0,0)
  PerimeterLength = 6200
  Placement = pos=(12135,9900,2800) rot=(0,0,1;0rad)
  PredefinedType = 0
  VerticalArea = 2.48e+06
  Width = 150
FEATURE [Part::FeaturePython] Structure121  label="V15x40 V108"  # Arch/BIM 7 (typed FeaturePython)
  FaceMaker = 0
  Height = 400
  HorizontalArea = 210000
  IfcData = attributes={"GlobalId": {"name": "GlobalId", "type": "IfcGloballyUniqueId", "is_enum": false, "enum_values": []}, "Description": {"... (+475 chars omitted),+1 more (map truncated)
  IfcType = 7
  Length = 1400
  Material = -> Material
  MoveBase = false
  MoveWithHost = false
  Nodes = (2) [(-1.72563e-31,-1.42109e-15,-7.77156e-16),(1400,-1.42109e-15,-7.77156e-16)]
  NodesOffset = 0
  Normal = (0,0,0)
  PerimeterLength = 3100
  Placement = pos=(9085,6640,2800) rot=(0,0,1;0rad)
  PredefinedType = 0
  VerticalArea = 1240000
  Width = 150
FEATURE [Part::FeaturePython] Structure122  label="V15x40 V113"  # Arch/BIM 7 (typed FeaturePython)
  FaceMaker = 0
  Height = 400
  HorizontalArea = 210000
  IfcData = attributes={"GlobalId": {"name": "GlobalId", "type": "IfcGloballyUniqueId", "is_enum": false, "enum_values": []}, "Description": {"... (+475 chars omitted),+1 more (map truncated)
  IfcType = 7
  Length = 1400
  Material = -> Material
  MoveBase = false
  MoveWithHost = false
  Nodes = (2) [(-1.72563e-31,-1.42109e-15,-7.77156e-16),(1400,-1.42109e-15,-7.77156e-16)]
  NodesOffset = 0
  Normal = (0,0,0)
  PerimeterLength = 3100
  Placement = pos=(9085,3350,2800) rot=(0,0,1;0rad)
  PredefinedType = 0
  VerticalArea = 1240000
  Width = 150
FEATURE [Part::FeaturePython] Structure123  label="V15x40 V118"  # Arch/BIM 7 (typed FeaturePython)
  FaceMaker = 0
  Height = 400
  HorizontalArea = 195000
  IfcData = attributes={"GlobalId": {"name": "GlobalId", "type": "IfcGloballyUniqueId", "is_enum": false, "enum_values": []}, "Description": {"... (+475 chars omitted),+1 more (map truncated)
  IfcType = 7
  Length = 1300
  Material = -> Material
  MoveBase = false
  MoveWithHost = false
  Nodes = (2) [(-1.72563e-31,-1.42109e-15,-7.77156e-16),(1300,-1.42109e-15,-7.77156e-16)]
  NodesOffset = 0
  Normal = (0,0,0)
  PerimeterLength = 2900
  Placement = pos=(9135,100,2800) rot=(0,0,1;0rad)
  PredefinedType = 0
  VerticalArea = 1160000
  Width = 150
FEATURE [Part::FeaturePython] Structure124  label="V15x40 V119"  # Arch/BIM 7 (typed FeaturePython)
  FaceMaker = 0
  Height = 400
  HorizontalArea = 445500
  IfcData = attributes={"GlobalId": {"name": "GlobalId", "type": "IfcGloballyUniqueId", "is_enum": false, "enum_values": []}, "Description": {"... (+475 chars omitted),+1 more (map truncated)
  IfcType = 7
  Length = 2970
  Material = -> Material
  MoveBase = false
  MoveWithHost = false
  Nodes = (2) [(-1.72563e-31,-1.42109e-15,-7.77156e-16),(2970,-1.42109e-15,-7.77156e-16)]
  NodesOffset = 0
  Normal = (0,0,0)
  PerimeterLength = 6240
  Placement = pos=(10685,100,2800) rot=(0,0,1;0rad)
  PredefinedType = 0
  VerticalArea = 2.496e+06
  Width = 150
FEATURE [Part::FeaturePython] Structure125  label="V15x40 V115"  # Arch/BIM 7 (typed FeaturePython)
  FaceMaker = 0
  Height = 400
  HorizontalArea = 460500
  IfcData = attributes={"GlobalId": {"name": "GlobalId", "type": "IfcGloballyUniqueId", "is_enum": false, "enum_values": []}, "Description": {"... (+475 chars omitted),+1 more (map truncated)
  IfcType = 7
  Length = 3070
  Material = -> Material
  MoveBase = false
  MoveWithHost = false
  Nodes = (2) [(-1.72563e-31,-1.42109e-15,-7.77156e-16),(3070,-1.42109e-15,-7.77156e-16)]
  NodesOffset = 0
  Normal = (0,0,0)
  PerimeterLength = 6440
  Placement = pos=(10635,3350,2800) rot=(0,0,1;0rad)
  PredefinedType = 0
  VerticalArea = 2.576e+06
  Width = 150
FEATURE [Part::FeaturePython] Structure126  label="V20x40 V133"  # Arch/BIM 7 (typed FeaturePython)
  FaceMaker = 0
  Height = 400
  HorizontalArea = 635000
  IfcData = attributes={"GlobalId": {"name": "GlobalId", "type": "IfcGloballyUniqueId", "is_enum": false, "enum_values": []}, "Description": {"... (+475 chars omitted),+1 more (map truncated)
  IfcType = 7
  Length = 3175
  Material = -> Material
  MoveBase = false
  MoveWithHost = false
  Nodes = (2) [(-1.72563e-31,0,-7.77156e-16),(3175,0,-7.77156e-16)]
  NodesOffset = 0
  Normal = (0,0,0)
  PerimeterLength = 6750
  Placement = pos=(13780,175,2800) rot=(0,0,1;1.5708rad)
  PredefinedType = 0
  VerticalArea = 2.7e+06
  Width = 200
FEATURE [Part::FeaturePython] Structure127  label="V20x40 V134"  # Arch/BIM 7 (typed FeaturePython)
  FaceMaker = 0
  Height = 400
  HorizontalArea = 509000
  IfcData = attributes={"GlobalId": {"name": "GlobalId", "type": "IfcGloballyUniqueId", "is_enum": false, "enum_values": []}, "Description": {"... (+475 chars omitted),+1 more (map truncated)
  IfcType = 7
  Length = 2545
  Material = -> Material
  MoveBase = false
  MoveWithHost = false
  Nodes = (2) [(-1.72563e-31,0,-7.77156e-16),(2545,0,-7.77156e-16)]
  NodesOffset = 0
  Normal = (0,0,0)
  PerimeterLength = 5490
  Placement = pos=(13780,3350,2800) rot=(0,0,1;1.5708rad)
  PredefinedType = 0
  VerticalArea = 2196000
  Width = 200
FEATURE [Part::FeaturePython] Structure128  label="V20x40 V135"  # Arch/BIM 7 (typed FeaturePython)
  FaceMaker = 0
  Height = 400
  HorizontalArea = 756000
  IfcData = attributes={"GlobalId": {"name": "GlobalId", "type": "IfcGloballyUniqueId", "is_enum": false, "enum_values": []}, "Description": {"... (+475 chars omitted),+1 more (map truncated)
  IfcType = 7
  Length = 3780
  Material = -> Material
  MoveBase = false
  MoveWithHost = false
  Nodes = (2) [(-1.72563e-31,0,-7.77156e-16),(3780,0,-7.77156e-16)]
  NodesOffset = 0
  Normal = (0,0,0)
  PerimeterLength = 7960
  Placement = pos=(15210,6045,2800) rot=(0,0,1;1.5708rad)
  PredefinedType = 0
  VerticalArea = 3.184e+06
  Width = 200
FEATURE [Part::FeaturePython] Structure129  label="V15x40 V109"  # Arch/BIM 7 (typed FeaturePython)
  FaceMaker = 0
  Height = 400
  HorizontalArea = 235500
  IfcData = attributes={"GlobalId": {"name": "GlobalId", "type": "IfcGloballyUniqueId", "is_enum": false, "enum_values": []}, "Description": {"... (+475 chars omitted),+1 more (map truncated)
  IfcType = 7
  Length = 1570
  Material = -> Material
  MoveBase = false
  MoveWithHost = false
  Nodes = (2) [(-1.72563e-31,-1.42109e-15,-7.77156e-16),(1570,-1.42109e-15,-7.77156e-16)]
  NodesOffset = 0
  Normal = (0,0,0)
  PerimeterLength = 3440
  Placement = pos=(13655,5970,2800) rot=(0,0,1;3.14159rad)
  PredefinedType = 0
  VerticalArea = 1.376e+06
  Width = 150
FEATURE [Part::FeaturePython] Structure130  label="V15x40 V110"  # Arch/BIM 7 (typed FeaturePython)
  FaceMaker = 0
  Height = 400
  HorizontalArea = 177000
  IfcData = attributes={"GlobalId": {"name": "GlobalId", "type": "IfcGloballyUniqueId", "is_enum": false, "enum_values": []}, "Description": {"... (+475 chars omitted),+1 more (map truncated)
  IfcType = 7
  Length = 1180
  Material = -> Material
  MoveBase = false
  MoveWithHost = false
  Nodes = (2) [(-1.72563e-31,-1.42109e-15,-7.77156e-16),(1180,-1.42109e-15,-7.77156e-16)]
  NodesOffset = 0
  Normal = (0,0,0)
  PerimeterLength = 2660
  Placement = pos=(13905,5970,2800) rot=(0,0,1;0rad)
  PredefinedType = 0
  VerticalArea = 1064000
  Width = 150
FEATURE [Part::FeaturePython] Structure131  label="V15x40 V125"  # Arch/BIM 7 (typed FeaturePython)
  FaceMaker = 0
  Height = 400
  HorizontalArea = 466500
  IfcData = attributes={"GlobalId": {"name": "GlobalId", "type": "IfcGloballyUniqueId", "is_enum": false, "enum_values": []}, "Description": {"... (+475 chars omitted),+1 more (map truncated)
  IfcType = 7
  Length = 3110
  Material = -> Material
  MoveBase = false
  MoveWithHost = false
  Nodes = (2) [(-1.72563e-31,-1.42109e-15,-7.77156e-16),(3110,-1.42109e-15,-7.77156e-16)]
  NodesOffset = 0
  Normal = (0,0,0)
  PerimeterLength = 6520
  Placement = pos=(6160,9825,2800) rot=(0,0,-1;1.5708rad)
  PredefinedType = 0
  VerticalArea = 2.608e+06
  Width = 150
FEATURE [Part::FeaturePython] Structure132  label="V15x40 V124"  # Arch/BIM 7 (typed FeaturePython)
  FaceMaker = 0
  Height = 400
  HorizontalArea = 471000
  IfcData = attributes={"GlobalId": {"name": "GlobalId", "type": "IfcGloballyUniqueId", "is_enum": false, "enum_values": []}, "Description": {"... (+475 chars omitted),+1 more (map truncated)
  IfcType = 7
  Length = 3140
  Material = -> Material
  MoveBase = false
  MoveWithHost = false
  Nodes = (2) [(-1.72563e-31,-1.42109e-15,-7.77156e-16),(3140,-1.42109e-15,-7.77156e-16)]
  NodesOffset = 0
  Normal = (0,0,0)
  PerimeterLength = 6580
  Placement = pos=(6160,6565,2800) rot=(0,0,-1;1.5708rad)
  PredefinedType = 0
  VerticalArea = 2.632e+06
  Width = 150
FEATURE [Part::FeaturePython] Structure133  label="V15x40 V123"  # Arch/BIM 7 (typed FeaturePython)
  FaceMaker = 0
  Height = 400
  HorizontalArea = 465000
  IfcData = attributes={"GlobalId": {"name": "GlobalId", "type": "IfcGloballyUniqueId", "is_enum": false, "enum_values": []}, "Description": {"... (+475 chars omitted),+1 more (map truncated)
  IfcType = 7
  Length = 3100
  Material = -> Material
  MoveBase = false
  MoveWithHost = false
  Nodes = (2) [(-1.72563e-31,-1.42109e-15,-7.77156e-16),(3100,-1.42109e-15,-7.77156e-16)]
  NodesOffset = 0
  Normal = (0,0,0)
  PerimeterLength = 6500
  Placement = pos=(6160,3275,2800) rot=(0,0,-1;1.5708rad)
  PredefinedType = 0
  VerticalArea = 2.6e+06
  Width = 150
FEATURE [Part::FeaturePython] Structure134  label="V15x40 V128"  # Arch/BIM 7 (typed FeaturePython)
  FaceMaker = 0
  Height = 400
  HorizontalArea = 459000
  IfcData = attributes={"GlobalId": {"name": "GlobalId", "type": "IfcGloballyUniqueId", "is_enum": false, "enum_values": []}, "Description": {"... (+475 chars omitted),+1 more (map truncated)
  IfcType = 7
  Length = 3060
  Material = -> Material
  MoveBase = false
  MoveWithHost = false
  Nodes = (2) [(-1.72563e-31,-1.42109e-15,-7.77156e-16),(3060,-1.42109e-15,-7.77156e-16)]
  NodesOffset = 0
  Normal = (0,0,0)
  PerimeterLength = 6420
  Placement = pos=(9010,9825,2800) rot=(0,0,-1;1.5708rad)
  PredefinedType = 0
  VerticalArea = 2.568e+06
  Width = 150
FEATURE [Part::FeaturePython] Structure135  label="V15x40 V127"  # Arch/BIM 7 (typed FeaturePython)
  FaceMaker = 0
  Height = 400
  HorizontalArea = 456000
  IfcData = attributes={"GlobalId": {"name": "GlobalId", "type": "IfcGloballyUniqueId", "is_enum": false, "enum_values": []}, "Description": {"... (+475 chars omitted),+1 more (map truncated)
  IfcType = 7
  Length = 3040
  Material = -> Material
  MoveBase = false
  MoveWithHost = false
  Nodes = (2) [(-1.72563e-31,-1.42109e-15,-7.77156e-16),(3040,-1.42109e-15,-7.77156e-16)]
  NodesOffset = 0
  Normal = (0,0,0)
  PerimeterLength = 6380
  Placement = pos=(9010,6515,2800) rot=(0,0,-1;1.5708rad)
  PredefinedType = 0
  VerticalArea = 2.552e+06
  Width = 150
FEATURE [Part::FeaturePython] Structure136  label="V15x40 V126"  # Arch/BIM 7 (typed FeaturePython)
  FaceMaker = 0
  Height = 400
  HorizontalArea = 457500
  IfcData = attributes={"GlobalId": {"name": "GlobalId", "type": "IfcGloballyUniqueId", "is_enum": false, "enum_values": []}, "Description": {"... (+475 chars omitted),+1 more (map truncated)
  IfcType = 7
  Length = 3050
  Material = -> Material
  MoveBase = false
  MoveWithHost = false
  Nodes = (2) [(-1.72563e-31,-1.42109e-15,-7.77156e-16),(3050,-1.42109e-15,-7.77156e-16)]
  NodesOffset = 0
  Normal = (0,0,0)
  PerimeterLength = 6400
  Placement = pos=(9010,3225,2800) rot=(0,0,-1;1.5708rad)
  PredefinedType = 0
  VerticalArea = 2.56e+06
  Width = 150
FEATURE [Part::FeaturePython] Structure137  label="V15x40 V132"  # Arch/BIM 7 (typed FeaturePython)
  FaceMaker = 0
  Height = 400
  HorizontalArea = 207000
  IfcData = attributes={"GlobalId": {"name": "GlobalId", "type": "IfcGloballyUniqueId", "is_enum": false, "enum_values": []}, "Description": {"... (+475 chars omitted),+1 more (map truncated)
  IfcType = 7
  Length = 1380
  Material = -> Material
  MoveBase = false
  MoveWithHost = false
  Nodes = (2) [(-1.72563e-31,-1.42109e-15,-7.77156e-16),(1380,-1.42109e-15,-7.77156e-16)]
  NodesOffset = 0
  Normal = (0,0,0)
  PerimeterLength = 3060
  Placement = pos=(12010,9825,2800) rot=(0,0,-1;1.5708rad)
  PredefinedType = 0
  VerticalArea = 1224000
  Width = 150
FEATURE [Part::FeaturePython] Structure138  label="V15x40 V131"  # Arch/BIM 7 (typed FeaturePython)
  FaceMaker = 0
  Height = 400
  HorizontalArea = 207000
  IfcData = attributes={"GlobalId": {"name": "GlobalId", "type": "IfcGloballyUniqueId", "is_enum": false, "enum_values": []}, "Description": {"... (+475 chars omitted),+1 more (map truncated)
  IfcType = 7
  Length = 1380
  Material = -> Material
  MoveBase = false
  MoveWithHost = false
  Nodes = (2) [(-1.72563e-31,-1.42109e-15,-7.77156e-16),(1380,-1.42109e-15,-7.77156e-16)]
  NodesOffset = 0
  Normal = (0,0,0)
  PerimeterLength = 3060
  Placement = pos=(10560,8445,2800) rot=(0,0,1;1.5708rad)
  PredefinedType = 0
  VerticalArea = 1224000
  Width = 150
FEATURE [Part::FeaturePython] Structure139  label="V15x40 V130"  # Arch/BIM 7 (typed FeaturePython)
  FaceMaker = 0
  Height = 400
  HorizontalArea = 363000
  IfcData = attributes={"GlobalId": {"name": "GlobalId", "type": "IfcGloballyUniqueId", "is_enum": false, "enum_values": []}, "Description": {"... (+475 chars omitted),+1 more (map truncated)
  IfcType = 7
  Length = 2420
  Material = -> Material
  MoveBase = false
  MoveWithHost = false
  Nodes = (2) [(-1.72563e-31,-1.42109e-15,-7.77156e-16),(2420,-1.42109e-15,-7.77156e-16)]
  NodesOffset = 0
  Normal = (0,0,0)
  PerimeterLength = 5140
  Placement = pos=(10560,3475,2800) rot=(0,0,1;1.5708rad)
  PredefinedType = 0
  VerticalArea = 2056000
  Width = 150
FEATURE [Part::FeaturePython] Structure140  label="V15x40 V129"  # Arch/BIM 7 (typed FeaturePython)
  FaceMaker = 0
  Height = 400
  HorizontalArea = 457500
  IfcData = attributes={"GlobalId": {"name": "GlobalId", "type": "IfcGloballyUniqueId", "is_enum": false, "enum_values": []}, "Description": {"... (+475 chars omitted),+1 more (map truncated)
  IfcType = 7
  Length = 3050
  Material = -> Material
  MoveBase = false
  MoveWithHost = false
  Nodes = (2) [(-1.72563e-31,-1.42109e-15,-7.77156e-16),(3050,-1.42109e-15,-7.77156e-16)]
  NodesOffset = 0
  Normal = (0,0,0)
  PerimeterLength = 6400
  Placement = pos=(10560,3225,2800) rot=(0,0,-1;1.5708rad)
  PredefinedType = 0
  VerticalArea = 2.56e+06
  Width = 150
FEATURE [Part::FeaturePython] Structure141  label="V15x40 V105"  # Arch/BIM 7 (typed FeaturePython)
  FaceMaker = 0
  Height = 400
  HorizontalArea = 453750
  IfcData = attributes={"GlobalId": {"name": "GlobalId", "type": "IfcGloballyUniqueId", "is_enum": false, "enum_values": []}, "Description": {"... (+475 chars omitted),+1 more (map truncated)
  IfcType = 7
  Length = 3025
  Material = -> Material
  MoveBase = false
  MoveWithHost = false
  Nodes = (2) [(-1.72563e-31,-1.42109e-15,-7.77156e-16),(3025,-1.42109e-15,-7.77156e-16)]
  NodesOffset = 0
  Normal = (0,0,0)
  PerimeterLength = 6350
  Placement = pos=(12085,8370,2800) rot=(0,0,1;0rad)
  PredefinedType = 0
  VerticalArea = 2.54e+06
  Width = 150
FEATURE [Part::FeaturePython] Structure197  label="L101"  # Arch/BIM 172 (typed FeaturePython)
  Base = -> Rectangle004
  FaceMaker = 0
  Height = 150
  HorizontalArea = 12611050
  IfcData = attributes={"GlobalId": {"name": "GlobalId", "type": "IfcGloballyUniqueId", "is_enum": false, "enum_values": []}, "Description": {"... (+484 chars omitted),+1 more (map truncated)
  IfcType = 172
  Length = 0
  Material = -> Material
  MoveBase = false
  MoveWithHost = false
  Nodes = (2) [(4057.5,8270,3000),(4057.5,8270,2850)]
  NodesOffset = 0
  Normal = (0,0,-1)
  PerimeterLength = 14330
  PredefinedType = 0
  VerticalArea = 2149500
  Width = 150
FEATURE [Part::FeaturePython] Structure198  label="L107"  # Arch/BIM 172 (typed FeaturePython)
  Base = -> Rectangle005
  FaceMaker = 0
  Height = 150
  HorizontalArea = 12732700
  IfcData = attributes={"GlobalId": {"name": "GlobalId", "type": "IfcGloballyUniqueId", "is_enum": false, "enum_values": []}, "Description": {"... (+484 chars omitted),+1 more (map truncated)
  IfcType = 172
  Length = 0
  Material = -> Material
  MoveBase = false
  MoveWithHost = false
  Nodes = (2) [(4057.5,4995,3000),(4057.5,4995,2850)]
  NodesOffset = 0
  Normal = (0,0,-1)
  PerimeterLength = 14390
  PredefinedType = 0
  VerticalArea = 2158500
  Width = 150
FEATURE [Part::FeaturePython] Structure199  label="L113"  # Arch/BIM 172 (typed FeaturePython)
  Base = -> Rectangle006
  FaceMaker = 0
  Height = 150
  HorizontalArea = 1.25705e+07
  IfcData = attributes={"GlobalId": {"name": "GlobalId", "type": "IfcGloballyUniqueId", "is_enum": false, "enum_values": []}, "Description": {"... (+484 chars omitted),+1 more (map truncated)
  IfcType = 172
  Length = 0
  Material = -> Material
  MoveBase = false
  MoveWithHost = false
  Nodes = (2) [(4057.5,1725,3000),(4057.5,1725,2850)]
  NodesOffset = 0
  Normal = (0,0,-1)
  PerimeterLength = 14310
  PredefinedType = 0
  VerticalArea = 2146500
  Width = 150
FEATURE [Part::FeaturePython] Structure200  label="V15x40 V102a"  # Arch/BIM 7 (typed FeaturePython)
  FaceMaker = 0
  Height = 400
  HorizontalArea = 405000
  IfcData = attributes={"GlobalId": {"name": "GlobalId", "type": "IfcGloballyUniqueId", "is_enum": false, "enum_values": []}, "Description": {"... (+475 chars omitted),+1 more (map truncated)
  IfcType = 7
  Length = 2700
  Material = -> Material
  MoveBase = false
  MoveWithHost = false
  Nodes = (2) [(-1.72563e-31,-1.42109e-15,-7.77156e-16),(2700,-1.42109e-15,-7.77156e-16)]
  NodesOffset = 0
  Normal = (0,0,0)
  PerimeterLength = 5700
  Placement = pos=(8935,8295,2800) rot=(0,0,1;3.14159rad)
  PredefinedType = 0
  VerticalArea = 2.28e+06
  Width = 150
FEATURE [Part::FeaturePython] Structure201  label="V15x40 V107a"  # Arch/BIM 7 (typed FeaturePython)
  FaceMaker = 0
  Height = 400
  HorizontalArea = 405000
  IfcData = attributes={"GlobalId": {"name": "GlobalId", "type": "IfcGloballyUniqueId", "is_enum": false, "enum_values": []}, "Description": {"... (+475 chars omitted),+1 more (map truncated)
  IfcType = 7
  Length = 2700
  Material = -> Material
  MoveBase = false
  MoveWithHost = false
  Nodes = (2) [(-1.72563e-31,-1.42109e-15,-7.77156e-16),(2700,-1.42109e-15,-7.77156e-16)]
  NodesOffset = 0
  Normal = (0,0,0)
  PerimeterLength = 5700
  Placement = pos=(8935,4995,2800) rot=(0,0,1;3.14159rad)
  PredefinedType = 0
  VerticalArea = 2.28e+06
  Width = 150
FEATURE [Part::FeaturePython] Structure202  label="V15x40 V112a"  # Arch/BIM 7 (typed FeaturePython)
  FaceMaker = 0
  Height = 400
  HorizontalArea = 405000
  IfcData = attributes={"GlobalId": {"name": "GlobalId", "type": "IfcGloballyUniqueId", "is_enum": false, "enum_values": []}, "Description": {"... (+475 chars omitted),+1 more (map truncated)
  IfcType = 7
  Length = 2700
  Material = -> Material
  MoveBase = false
  MoveWithHost = false
  Nodes = (2) [(-1.72563e-31,-1.42109e-15,-7.77156e-16),(2700,-1.42109e-15,-7.77156e-16)]
  NodesOffset = 0
  Normal = (0,0,0)
  PerimeterLength = 5700
  Placement = pos=(8935,1700,2800) rot=(0,0,1;3.14159rad)
  PredefinedType = 0
  VerticalArea = 2.28e+06
  Width = 150
FEATURE [Part::FeaturePython] Structure204  label="V15x40 V130a"  # Arch/BIM 7 (typed FeaturePython)
  FaceMaker = 0
  Height = 400
  HorizontalArea = 370500
  IfcData = attributes={"GlobalId": {"name": "GlobalId", "type": "IfcGloballyUniqueId", "is_enum": false, "enum_values": []}, "Description": {"... (+475 chars omitted),+1 more (map truncated)
  IfcType = 7
  Length = 2470
  Material = -> Material
  MoveBase = false
  MoveWithHost = false
  Nodes = (2) [(-1.72563e-31,-1.42109e-15,-7.77156e-16),(2470,-1.42109e-15,-7.77156e-16)]
  NodesOffset = 0
  Normal = (0,0,0)
  PerimeterLength = 5240
  Placement = pos=(12010,3425,2800) rot=(0,0,1;1.5708rad)
  PredefinedType = 0
  VerticalArea = 2096000
  Width = 150
FEATURE [App::GeometryPython] BuildingPart009  label="Vigas sobre PB"  # Arch/BIM 172 (typed FeaturePython)
  Area = 0
  Group = -> [Structure112,Structure133,Structure122,Structure131,Structure134,Structure138,Structure114,Structure116,Structure111,Structure201,Structure141,Structure113,Structure139,Structure109,Structure115,Structure200,Structure119,Structure120,Structure121,Structure129,Structure130,Structure117,Structure202,Structure125,Structure118,Structure123,Structure124,Structure132,Structure136,Structure135,+8 more]
  Height = 0
  HeightPropagate = true
  IfcData = attributes={"GlobalId": {"name": "GlobalId", "type": "IfcGloballyUniqueId", "is_enum": false, "enum_values": []}, "Description": {"... (+484 chars omitted),+1 more (map truncated)
  IfcType = 172
  LevelOffset = 0
  PredefinedType = 0
FEATURE [Part::FeaturePython] Structure205  label="L102"  # Arch/BIM 172 (typed FeaturePython)
  Base = -> Rectangle014
  FaceMaker = 0
  Height = 150
  HorizontalArea = 3928500
  IfcData = attributes={"GlobalId": {"name": "GlobalId", "type": "IfcGloballyUniqueId", "is_enum": false, "enum_values": []}, "Description": {"... (+484 chars omitted),+1 more (map truncated)
  IfcType = 172
  Length = 0
  Material = -> Material
  MoveBase = false
  MoveWithHost = false
  Nodes = (2) [(7585,9097.5,3000),(7585,9097.5,2850)]
  NodesOffset = 0
  Normal = (0,0,-1)
  PerimeterLength = 8310
  PredefinedType = 0
  VerticalArea = 1246500
  Width = 150
FEATURE [Part::FeaturePython] Structure206  label="L103"  # Arch/BIM 172 (typed FeaturePython)
  Base = -> Wire
  FaceMaker = 0
  Height = 150
  HorizontalArea = 3.9285e+06
  IfcData = attributes={"GlobalId": {"name": "GlobalId", "type": "IfcGloballyUniqueId", "is_enum": false, "enum_values": []}, "Description": {"... (+484 chars omitted),+1 more (map truncated)
  IfcType = 172
  Length = 0
  Material = -> Material
  MoveBase = false
  MoveWithHost = false
  Nodes = (2) [(7543.76,7449.37,3000),(7543.76,7449.37,2850)]
  NodesOffset = 0
  Normal = (0,0,-1)
  PerimeterLength = 8410
  Placement = pos=(0,0,-150) rot=(0,0,1;0rad)
  PredefinedType = 0
  VerticalArea = 1261500
  Width = 150
FEATURE [Part::FeaturePython] Structure207  label="L108"  # Arch/BIM 172 (typed FeaturePython)
  Base = -> Wire001
  FaceMaker = 0
  Height = 150
  HorizontalArea = 3.90134e+06
  IfcData = attributes={"GlobalId": {"name": "GlobalId", "type": "IfcGloballyUniqueId", "is_enum": false, "enum_values": []}, "Description": {"... (+484 chars omitted),+1 more (map truncated)
  IfcType = 172
  Length = 0
  Material = -> Material
  MoveBase = false
  MoveWithHost = false
  Nodes = (2) [(7543.46,5835.61,3000),(7543.46,5835.61,2850)]
  NodesOffset = 0
  Normal = (0,0,-1)
  PerimeterLength = 8389.89
  Placement = pos=(0,0,-150) rot=(0,0,1;0rad)
  PredefinedType = 0
  VerticalArea = 1.25848e+06
  Width = 150
FEATURE [Part::FeaturePython] Structure208  label="L109"  # Arch/BIM 172 (typed FeaturePython)
  Base = -> Rectangle015
  FaceMaker = 0
  Height = 150
  HorizontalArea = 4.0365e+06
  IfcData = attributes={"GlobalId": {"name": "GlobalId", "type": "IfcGloballyUniqueId", "is_enum": false, "enum_values": []}, "Description": {"... (+484 chars omitted),+1 more (map truncated)
  IfcType = 172
  Length = 0
  Material = -> Material
  MoveBase = false
  MoveWithHost = false
  Nodes = (2) [(7585,4172.5,3000),(7585,4172.5,2850)]
  NodesOffset = 0
  Normal = (0,0,-1)
  PerimeterLength = 8390
  PredefinedType = 0
  VerticalArea = 1258500
  Width = 150
FEATURE [Part::FeaturePython] Structure209  label="L114"  # Arch/BIM 172 (typed FeaturePython)
  Base = -> Wire002
  FaceMaker = 0
  Height = 150
  HorizontalArea = 3.91484e+06
  IfcData = attributes={"GlobalId": {"name": "GlobalId", "type": "IfcGloballyUniqueId", "is_enum": false, "enum_values": []}, "Description": {"... (+484 chars omitted),+1 more (map truncated)
  IfcType = 172
  Length = 0
  Material = -> Material
  MoveBase = false
  MoveWithHost = false
  Nodes = (2) [(7543.6,2543.13,3000),(7543.6,2543.13,2850)]
  NodesOffset = 0
  Normal = (0,0,-1)
  PerimeterLength = 8399.89
  Placement = pos=(0,0,-150) rot=(0,0,1;0rad)
  PredefinedType = 0
  VerticalArea = 1.25998e+06
  Width = 150
FEATURE [Part::FeaturePython] Structure210  label="L115"  # Arch/BIM 172 (typed FeaturePython)
  Base = -> Rectangle016
  FaceMaker = 0
  Height = 150
  HorizontalArea = 3.915e+06
  IfcData = attributes={"GlobalId": {"name": "GlobalId", "type": "IfcGloballyUniqueId", "is_enum": false, "enum_values": []}, "Description": {"... (+484 chars omitted),+1 more (map truncated)
  IfcType = 172
  Length = 0
  Material = -> Material
  MoveBase = false
  MoveWithHost = false
  Nodes = (2) [(7585,900,3000),(7585,900,2850)]
  NodesOffset = 0
  Normal = (0,0,-1)
  PerimeterLength = 8300
  PredefinedType = 0
  VerticalArea = 1.245e+06
  Width = 150
FEATURE [Part::FeaturePython] Structure211  label="L104"  # Arch/BIM 172 (typed FeaturePython)
  Base = -> Rectangle008
  FaceMaker = 0
  Height = 150
  HorizontalArea = 4354000
  IfcData = attributes={"GlobalId": {"name": "GlobalId", "type": "IfcGloballyUniqueId", "is_enum": false, "enum_values": []}, "Description": {"... (+484 chars omitted),+1 more (map truncated)
  IfcType = 172
  Length = 0
  Material = -> Material
  MoveBase = false
  MoveWithHost = false
  Nodes = (2) [(9785,8270,3000),(9785,8270,2850)]
  NodesOffset = 0
  Normal = (0,0,-1)
  PerimeterLength = 9020
  PredefinedType = 0
  VerticalArea = 1353000
  Width = 150
FEATURE [Part::FeaturePython] Structure212  label="L110"  # Arch/BIM 172 (typed FeaturePython)
  Base = -> Rectangle011
  FaceMaker = 0
  Height = 150
  HorizontalArea = 4396000
  IfcData = attributes={"GlobalId": {"name": "GlobalId", "type": "IfcGloballyUniqueId", "is_enum": false, "enum_values": []}, "Description": {"... (+484 chars omitted),+1 more (map truncated)
  IfcType = 172
  Length = 0
  Material = -> Material
  MoveBase = false
  MoveWithHost = false
  Nodes = (2) [(9785,4995,3000),(9785,4995,2850)]
  NodesOffset = 0
  Normal = (0,0,-1)
  PerimeterLength = 9080
  PredefinedType = 0
  VerticalArea = 1362000
  Width = 150
FEATURE [Part::FeaturePython] Structure213  label="L116"  # Arch/BIM 172 (typed FeaturePython)
  Base = -> Rectangle013
  FaceMaker = 0
  Height = 150
  HorizontalArea = 4.34e+06
  IfcData = attributes={"GlobalId": {"name": "GlobalId", "type": "IfcGloballyUniqueId", "is_enum": false, "enum_values": []}, "Description": {"... (+484 chars omitted),+1 more (map truncated)
  IfcType = 172
  Length = 0
  Material = -> Material
  MoveBase = false
  MoveWithHost = false
  Nodes = (2) [(9785,1725,3000),(9785,1725,2850)]
  NodesOffset = 0
  Normal = (0,0,-1)
  PerimeterLength = 9000
  PredefinedType = 0
  VerticalArea = 1350000
  Width = 150
FEATURE [Part::FeaturePython] Structure214  label="L105"  # Arch/BIM 172 (typed FeaturePython)
  Base = -> Rectangle009
  FaceMaker = 0
  Height = 150
  HorizontalArea = 1.794e+06
  IfcData = attributes={"GlobalId": {"name": "GlobalId", "type": "IfcGloballyUniqueId", "is_enum": false, "enum_values": []}, "Description": {"... (+484 chars omitted),+1 more (map truncated)
  IfcType = 172
  Length = 0
  Material = -> Material
  MoveBase = false
  MoveWithHost = false
  Nodes = (2) [(11285,9135,3000),(11285,9135,2850)]
  NodesOffset = 0
  Normal = (0,0,-1)
  PerimeterLength = 5360
  PredefinedType = 0
  VerticalArea = 804000
  Width = 150
FEATURE [Part::FeaturePython] Structure215  label="L111"  # Arch/BIM 172 (typed FeaturePython)
  Base = -> Rectangle018
  FaceMaker = 0
  Height = 150
  HorizontalArea = 3.211e+06
  IfcData = attributes={"GlobalId": {"name": "GlobalId", "type": "IfcGloballyUniqueId", "is_enum": false, "enum_values": []}, "Description": {"... (+484 chars omitted),+1 more (map truncated)
  IfcType = 172
  Length = 0
  Material = -> Material
  MoveBase = false
  MoveWithHost = false
  Nodes = (2) [(11285,4660,3000),(11285,4660,2850)]
  NodesOffset = 0
  Normal = (0,0,-1)
  PerimeterLength = 7540
  PredefinedType = 0
  VerticalArea = 1.131e+06
  Width = 150
FEATURE [Part::FeaturePython] Structure216  label="L117"  # Arch/BIM 172 (typed FeaturePython)
  Base = -> Rectangle020
  FaceMaker = 0
  Height = 150
  HorizontalArea = 9439500
  IfcData = attributes={"GlobalId": {"name": "GlobalId", "type": "IfcGloballyUniqueId", "is_enum": false, "enum_values": []}, "Description": {"... (+484 chars omitted),+1 more (map truncated)
  IfcType = 172
  Length = 0
  Material = -> Material
  MoveBase = false
  MoveWithHost = false
  Nodes = (2) [(12157.5,1725,3000),(12157.5,1725,2850)]
  NodesOffset = 0
  Normal = (0,0,-1)
  PerimeterLength = 12290
  PredefinedType = 0
  VerticalArea = 1843500
  Width = 150
FEATURE [Part::FeaturePython] Structure217  label="L112"  # Arch/BIM 172 (typed FeaturePython)
  Base = -> Rectangle019
  FaceMaker = 0
  Height = 150
  HorizontalArea = 3.93965e+06
  IfcData = attributes={"GlobalId": {"name": "GlobalId", "type": "IfcGloballyUniqueId", "is_enum": false, "enum_values": []}, "Description": {"... (+484 chars omitted),+1 more (map truncated)
  IfcType = 172
  Length = 0
  Material = -> Material
  MoveBase = false
  MoveWithHost = false
  Nodes = (2) [(12882.5,4660,3000),(12882.5,4660,2850)]
  NodesOffset = 0
  Normal = (0,0,-1)
  PerimeterLength = 8130
  Placement = pos=(0,0,-150) rot=(0,0,1;0rad)
  PredefinedType = 0
  VerticalArea = 1.2195e+06
  Width = 150
FEATURE [Part::FeaturePython] Structure218  label="L106"  # Arch/BIM 172 (typed FeaturePython)
  Base = -> Rectangle017
  FaceMaker = 0
  Height = 150
  HorizontalArea = 4174500
  IfcData = attributes={"GlobalId": {"name": "GlobalId", "type": "IfcGloballyUniqueId", "is_enum": false, "enum_values": []}, "Description": {"... (+484 chars omitted),+1 more (map truncated)
  IfcType = 172
  Length = 0
  Material = -> Material
  MoveBase = false
  MoveWithHost = false
  Nodes = (2) [(13597.5,9135,3000),(13597.5,9135,2850)]
  NodesOffset = 0
  Normal = (0,0,-1)
  PerimeterLength = 8810
  PredefinedType = 0
  VerticalArea = 1321500
  Width = 150
FEATURE [App::GeometryPython] BuildingPart014  label="Losas sobre PB"  # Arch/BIM 172 (typed FeaturePython)
  Area = 0
  Group = -> [Structure197,Structure205,Structure206,Structure211,Structure214,Structure218,Structure198,Structure207,Structure208,Structure212,Structure215,Structure217,Structure199,Structure209,Structure210,Structure213,Structure216]
  Height = 0
  HeightPropagate = true
  IfcData = attributes={"GlobalId": {"name": "GlobalId", "type": "IfcGloballyUniqueId", "is_enum": false, "enum_values": []}, "Description": {"... (+484 chars omitted),+1 more (map truncated)
  IfcType = 172
  LevelOffset = 0
  PredefinedType = 0
FEATURE [App::DocumentObjectGroupPython] MaterialContainer  label="Materials"  # scripted group (container) (typed FeaturePython)
  Group = -> [Material]
FEATURE [Part::FeaturePython] Structure401  label="Beam046"  # Arch/BIM 7 (typed FeaturePython)
  FaceMaker = 0
  Height = 300
  HorizontalArea = 337500
  IfcData = attributes={"GlobalId": {"name": "GlobalId", "type": "IfcGloballyUniqueId", "is_enum": false, "enum_values": []}, "Description": {"... (+498 chars omitted),+1 more (map truncated)
  IfcType = 7
  Length = 1125
  Material = -> Material
  MoveBase = false
  MoveWithHost = false
  Nodes = (2) [(1.2326e-31,-1.51582e-15,5.55112e-16),(1125,-1.51582e-15,5.55112e-16)]
  NodesOffset = 0
  Normal = (0,0,0)
  PerimeterLength = 2850
  Placement = pos=(9360,6640,-650) rot=(0,0,1;0rad)
  PredefinedType = 0
  Tag = VR (30x30)
  VerticalArea = 855000
  Width = 300
FEATURE [App::GeometryPython] BuildingPart005  label="Vigas riostras"  # Arch/BIM 172 (typed FeaturePython)
  Area = 0
  Group = -> [Beam,Beam001,Structure041,Structure042,Structure043,Structure044,Structure045,Structure046,Structure048,Structure049,Structure053,Structure056,Structure059,Structure060,Structure061,Structure064,Structure065,Structure066,Structure067,Structure068,Structure069,Structure070,Structure071,Structure072,Structure073,Structure074,Structure075,Structure076,Structure077,Structure078,Structure079,+2 more]
  Height = 0
  HeightPropagate = true
  IfcData = attributes={"GlobalId": {"name": "GlobalId", "type": "IfcGloballyUniqueId", "is_enum": false, "enum_values": []}, "Description": {"... (+484 chars omitted),+1 more (map truncated)
  IfcType = 172
  LevelOffset = 0
  Placement = pos=(0,0,500) rot=(0,0,1;0rad)
  PredefinedType = 0
FEATURE [App::GeometryPython] BuildingPart002  label="Fundaciones"  # Arch/BIM 172 (typed FeaturePython)
  Area = 8300000
  Group = -> [BuildingPart005,BuildingPart006,BuildingPart007,BuildingPart008,Wall]
  Height = 0
  HeightPropagate = true
  IfcData = attributes={"GlobalId": {"name": "GlobalId", "type": "IfcGloballyUniqueId", "is_enum": false, "enum_values": []}, "Description": {"... (+484 chars omitted),+1 more (map truncated)
  IfcType = 172
  LevelOffset = 0
  PredefinedType = 0
FEATURE [TechDraw::DrawSVGTemplate] Template008
  EditableTexts = Cliente 1=UNIVERSO BIM,Comprobado por=GORO,Dibujado por=GORO,Escala=-,Fecha=2021/01,Nombre plano 1=PORTADA,Numero Proyecto=21005,Numero plano=ES-001,+2 more (map truncated)
  Height = 297
  Orientation = 1
  Width = 420
FEATURE [TechDraw::DrawViewAnnotation] Annotation
  Font = Arial
  LineSpace = 80
  LockPosition = false
  MaxWidth = -1
  Rotation = 0
  ScaleType = 0
  Text = LISTA DE PLANOS
  TextSize = 5
  TextStyle = 0
  X = 60.7425
  Y = 271.753
FEATURE [TechDraw::DrawSVGTemplate] Template010
  EditableTexts = Cliente 1=UNIVERSO BIM,Comprobado por=GORO,Dibujado por=GORO,Escala=1:50,Fecha=23/05/2021,Nombre plano 1=ESTRUCTURA FUNDACIONES,Numero Proyecto=21005,+3 more (map truncated)
  Height = 297
  Orientation = 1
  Width = 420
FEATURE [App::FeaturePython] Dimension  # Draft dimension (typed FeaturePython)
  Diameter = false
  Dimline = (4400,10400,0)
  Direction = (0,0,0)
  Distance = 4230
  End = (6160,10500,0)
  Normal = (0,0,1)
  Start = (1930,10500,0)
FEATURE [App::FeaturePython] Dimension001  # Draft dimension (typed FeaturePython)
  Diameter = false
  Dimline = (4400,10400,0)
  Direction = (0,0,0)
  Distance = 2850
  End = (9010,10500,0)
  Normal = (0,0,1)
  Start = (6160,10500,0)
FEATURE [App::FeaturePython] Dimension002  # Draft dimension (typed FeaturePython)
  Diameter = false
  Dimline = (4400,10400,0)
  Direction = (0,0,0)
  Distance = 1550
  End = (10560,10500,0)
  Normal = (0,0,1)
  Start = (9010,10500,0)
FEATURE [App::FeaturePython] Dimension003  # Draft dimension (typed FeaturePython)
  Diameter = false
  Dimline = (4400,10400,0)
  Direction = (0,0,0)
  Distance = 1450
  End = (12010,10500,0)
  Normal = (0,0,1)
  Start = (10560,10500,0)
FEATURE [App::FeaturePython] Dimension004  # Draft dimension (typed FeaturePython)
  Diameter = false
  Dimline = (4400,10400,0)
  Direction = (0,0,0)
  Distance = 1770
  End = (13780,10500,0)
  Normal = (0,0,1)
  Start = (12010,10500,0)
FEATURE [App::FeaturePython] Dimension005  # Draft dimension (typed FeaturePython)
  Diameter = false
  Dimline = (4400,10400,0)
  Direction = (0,0,0)
  Distance = 1430
  End = (15210,10500,0)
  Normal = (0,0,1)
  Start = (13780,10500,0)
FEATURE [App::FeaturePython] Dimension006  # Draft dimension (typed FeaturePython)
  Diameter = false
  Dimline = (1200,2300,0)
  Direction = (0,0,0)
  Distance = 3250
  End = (-1000,3350,0)
  Normal = (0,0,1)
  Start = (-1000,100,0)
FEATURE [App::FeaturePython] Dimension007  # Draft dimension (typed FeaturePython)
  Diameter = false
  Dimline = (1200,2300,0)
  Direction = (0,0,0)
  Distance = 2620
  End = (-1000,5970,0)
  Normal = (0,0,1)
  Start = (-1000,3350,0)
FEATURE [App::FeaturePython] Dimension008  # Draft dimension (typed FeaturePython)
  Diameter = false
  Dimline = (1200,2300,0)
  Direction = (0,0,0)
  Distance = 670
  End = (-1000,6640,0)
  Normal = (0,0,1)
  Start = (-1000,5970,0)
FEATURE [App::FeaturePython] Dimension009  # Draft dimension (typed FeaturePython)
  Diameter = false
  Dimline = (1200,2300,0)
  Direction = (0,0,0)
  Distance = 1730
  End = (-1000,8370,0)
  Normal = (0,0,1)
  Start = (-1000,6640,0)
FEATURE [App::FeaturePython] Dimension010  # Draft dimension (typed FeaturePython)
  Diameter = false
  Dimline = (1200,2300,0)
  Direction = (0,0,0)
  Distance = 1530
  End = (-1000,9900,0)
  Normal = (0,0,1)
  Start = (-1000,8370,0)
FEATURE [App::FeaturePython] dLabel  # WARN: FeaturePython — macro-defined, semantics opaque (R4)
  CustomText = Label
  LabelType = 7
  Placement = pos=(1319.11,10406.1,0) rot=(0,0,1;0rad)
  Points = (3) [(1319.11,10406.1,0),(1519,10406.1,0),(1709.6,10113.2,0)]
  StraightDirection = 0
  StraightDistance = 199.893
  Target = -> Structure [Face5]
  TargetPoint = (1709.6,10113.2,0)
  Text = B1 (70x70x70)
FEATURE [App::FeaturePython] dLabel001  # WARN: FeaturePython — macro-defined, semantics opaque (R4)
  CustomText = Description
  LabelType = 7
  Placement = pos=(5500,9300,0) rot=(0,0,1;0rad)
  Points = (3) [(5500,9300,0),(5700,9300,0),(5950.61,9663.58,0)]
  StraightDirection = 0
  StraightDistance = 200
  Target = -> Structure006 [Face5]
  TargetPoint = (5950.61,9663.58,0)
  Text = B1 (70x70x70)
FEATURE [App::FeaturePython] dLabel002  # WARN: FeaturePython — macro-defined, semantics opaque (R4)
  CustomText = Label | Tag
  LabelType = 7
  Placement = pos=(8400,9300,0) rot=(0,0,1;0rad)
  Points = (3) [(8400,9300,0),(8600,9300,0),(8794.64,9628.11,0)]
  StraightDirection = 0
  StraightDistance = 200
  Target = -> Structure008 [Face5]
  TargetPoint = (8794.64,9628.11,0)
  Text = B1 (70x70x70)
FEATURE [App::FeaturePython] Dimension011  # Draft dimension (typed FeaturePython)
  Diameter = false
  Dimline = (12500,5100,0)
  Direction = (0,0,0)
  Distance = 2600
  End = (12585,5395,-1000)
  Normal = (0,0,1)
  Start = (9985,5395,-1000)
FEATURE [App::FeaturePython] Dimension012  # Draft dimension (typed FeaturePython)
  Diameter = false
  Dimline = (13000,7900,0)
  Direction = (0,0,0)
  Distance = 3550
  End = (12585,8945,-1000)
  Normal = (0,0,1)
  Start = (12585,5395,-1000)
FEATURE [App::FeaturePython] dLabel008  # WARN: FeaturePython — macro-defined, semantics opaque (R4)
  CustomText = Label
  LabelType = 7
  Placement = pos=(9600,7600,0) rot=(0,0,1;0rad)
  Points = (3) [(9600,7600,0),(9900,7600,0),(10258.6,7172.31,0)]
  StraightDirection = 0
  StraightDistance = 300
  Target = -> Structure040 [Face5]
  TargetPoint = (10258.6,7172.31,0)
  Text = L01 (Esp 25 cm)
FEATURE [App::FeaturePython] dLabel009  # WARN: FeaturePython — macro-defined, semantics opaque (R4)
  CustomText = Label
  LabelType = 7
  Placement = pos=(9622,8080.67,0) rot=(0,0,1;0rad)
  Points = (3) [(9622,8080.67,0),(10284.4,8080.67,0),(10526.2,7745.96,0)]
  StraightDirection = 0
  StraightDistance = 662.437
  Target = -> Wall [Face10]
  TargetPoint = (10526.2,7745.96,0)
  Text = M01 (Esp 15 cm)
FEATURE [App::FeaturePython] dLabel010  # WARN: FeaturePython — macro-defined, semantics opaque (R4)
  CustomText = Label
  LabelType = 7
  Placement = pos=(4300,7100,0) rot=(0,0,1;0rad)
  Points = (3) [(4300,7100,0),(4600,7100,0),(4765.74,6705.21,0)]
  StraightDirection = 0
  StraightDistance = 300
  Target = -> Beam001 [Face3]
  TargetPoint = (4765.74,6705.21,0)
  Text = VR (30x30)
FEATURE [App::FeaturePython] dLabel011  # WARN: FeaturePython — macro-defined, semantics opaque (R4)
  CustomText = Label
  LabelType = 7
  Placement = pos=(7622.2,7049.42,0) rot=(0,0,1;0rad)
  Points = (3) [(7622.2,7049.42,0),(7897.49,7049.42,0),(8100.78,6689.42,0)]
  StraightDirection = 0
  StraightDistance = 275.29
  Target = -> Structure064 [Face3]
  TargetPoint = (8100.78,6689.42,0)
  Text = VR (30x30)
FEATURE [App::FeaturePython] dLabel012  # WARN: FeaturePython — macro-defined, semantics opaque (R4)
  CustomText = Label
  LabelType = 7
  Placement = pos=(8447.88,3861.92,0) rot=(0,0,1;0rad)
  Points = (3) [(8447.88,3861.92,0),(8617.29,3861.92,0),(8778.22,3565.46,0)]
  StraightDirection = 0
  StraightDistance = 169.409
  Target = -> Structure024 [Face5]
  TargetPoint = (8778.22,3565.46,0)
  Text = B1 (70x70x70)
FEATURE [TechDraw::DrawSVGTemplate] Template
  EditableTexts = Cliente 1=UNIVERSO BIM,Comprobado por=GORO,Dibujado por=GORO,Escala=1:50,Fecha=23/05/2021,Nombre plano 1=ESTRUCTURA PB,Numero Proyecto=21005,+3 more (map truncated)
  Height = 297
  Orientation = 1
  Width = 420
FEATURE [App::DocumentObjectGroup] Group012  label="PB Columnas"
  Group = -> [Structure105,Structure104,Structure084,Structure088,Structure089,Structure090,Structure091,Structure092,Structure093,Structure097,Structure098,Structure099,Structure100,Structure101,Structure102,Structure103,Structure107,Structure106,Structure081,Structure086,Structure085]
FEATURE [App::GeometryPython] BuildingPart001  label="Nivel 0"  # Arch/BIM 172 (typed FeaturePython)
  Area = 24900000
  Group = -> [BuildingPart009,Group012,BuildingPart014,Wall001]
  Height = 0
  HeightPropagate = true
  IfcData = attributes={"GlobalId": {"name": "GlobalId", "type": "IfcGloballyUniqueId", "is_enum": false, "enum_values": []}, "Description": {"... (+484 chars omitted),+1 more (map truncated)
  IfcType = 172
  LevelOffset = 0
  PredefinedType = 0
FEATURE [App::GeometryPython] BuildingPart  label="Building"  # Arch/BIM 10 (typed FeaturePython)
  Area = 107900000
  BuildingType = 0
  CompositionType = 0
  ElevationOfRefHeight = 0
  ElevationOfTerrain = 0
  Group = -> [BuildingPart002,BuildingPart001,BuildingPart003,BuildingPart010,BuildingPart019,BuildingPart023,BuildingPart024]
  Height = 0
  HeightPropagate = true
  IfcData = attributes={"GlobalId": {"name": "GlobalId", "type": "IfcGloballyUniqueId", "is_enum": false, "enum_values": []}, "Description": {"... (+1010 chars omitted),+1 more (map truncated)
  IfcType = 10
  LevelOffset = 0
  LongName = Building
FEATURE [TechDraw::DrawViewPart] View  label="VIEW-Vista Portada"
  Caption = VISTA DEL PROYECTO
  CoarseView = false
  Direction = (0.473,-0.767,0.435)
  Focus = 200
  HardHidden = false
  IsoCount = 0
  IsoHidden = false
  IsoVisible = false
  LockPosition = false
  Perspective = true
  Rotation = 0
  Scale = 0.007
  ScaleType = 0
  SeamHidden = false
  SeamVisible = true
  SmoothHidden = false
  SmoothVisible = true
  Source = -> [BuildingPart]
  X = 317.281
  XDirection = (0.844,0.536,0.027)
  Y = 166.952
FEATURE [Part::Part2DObjectPython] Line  # Draft 2D object (typed FeaturePython)
  Area = 0
  ChamferSize = 0
  Closed = false
  End = (8935,8220,3000)
  FilletRadius = 0
  Length = 561.249
  MakeFace = true
  Placement = pos=(8635,7770,2850) rot=(0,0,1;0rad)
  Points = (2) [(0,0,0),(300,450,150)]
  Start = (8635,7770,2850)
  Subdivisions = 0
FEATURE [Part::Part2DObjectPython] Line001  # Draft 2D object (typed FeaturePython)
  Area = 0
  ChamferSize = 0
  Closed = false
  End = (8935,7770,2850)
  FilletRadius = 0
  Length = 540.833
  MakeFace = true
  Placement = pos=(8635,8220,2850) rot=(0,0,1;0rad)
  Points = (2) [(0,0,0),(300,-450,0)]
  Start = (8635,8220,2850)
  Subdivisions = 0
FEATURE [Part::Part2DObjectPython] Line002  # Draft 2D object (typed FeaturePython)
  Area = 0
  ChamferSize = 0
  Closed = false
  End = (8935,5070,3000)
  FilletRadius = 0
  Length = 561.334
  MakeFace = true
  Placement = pos=(8635,5520.11,2850) rot=(0,0,1;0rad)
  Points = (2) [(0,0,0),(300,-450.106,150)]
  Start = (8635,5520.11,2850)
  Subdivisions = 0
FEATURE [Part::Part2DObjectPython] Line003  # Draft 2D object (typed FeaturePython)
  Area = 0
  ChamferSize = 0
  Closed = false
  End = (8935,5520.11,2850)
  FilletRadius = 0
  Length = 540.833
  MakeFace = true
  Placement = pos=(8635,5070.11,2850) rot=(0,0,1;0rad)
  Points = (2) [(0,0,0),(300,450,0)]
  Start = (8635,5070.11,2850)
  Subdivisions = 0
FEATURE [Part::Part2DObjectPython] Line004  # Draft 2D object (typed FeaturePython)
  Area = 0
  ChamferSize = 0
  Closed = false
  End = (8935,2225.11,2850)
  FilletRadius = 0
  Length = 540.833
  MakeFace = true
  Placement = pos=(8635,1775.11,2850) rot=(0,0,1;0rad)
  Points = (2) [(0,0,0),(300,450,0)]
  Start = (8635,1775.11,2850)
  Subdivisions = 0
FEATURE [Part::Part2DObjectPython] Line005  # Draft 2D object (typed FeaturePython)
  Area = 0
  ChamferSize = 0
  Closed = false
  End = (8935,1775,3000)
  FilletRadius = 0
  Length = 561.334
  MakeFace = true
  Placement = pos=(8635,2225.11,2850) rot=(0,0,1;0rad)
  Points = (2) [(0,0,0),(300,-450.106,150)]
  Start = (8635,2225.11,2850)
  Subdivisions = 0
FEATURE [App::FeaturePython] dLabel014  # WARN: FeaturePython — macro-defined, semantics opaque (R4)
  CustomText = Label
  LabelType = 7
  Placement = pos=(4042.33,10186.4,0) rot=(0,0,1;0rad)
  Points = (3) [(4042.33,10186.4,0),(4243.45,10186.4,0),(4486.18,9891.63,0)]
  StraightDirection = 0
  StraightDistance = 201.117
  Target = -> Structure109 [Face3]
  TargetPoint = (4486.18,9891.63,0)
  Text = V101 (15x40)
FEATURE [Part::Part2DObjectPython] Line006  # Draft 2D object (typed FeaturePython)
  Area = 0
  ChamferSize = 0
  Closed = false
  End = (11935,6045,3000)
  FilletRadius = 0
  Length = 2598.56
  MakeFace = true
  Placement = pos=(10635,8295,3000) rot=(0,0,1;0rad)
  Points = (2) [(0,0,0),(1300,-2250,0)]
  Start = (10635,8295,3000)
  Subdivisions = 0
FEATURE [Part::Part2DObjectPython] Line007  # Draft 2D object (typed FeaturePython)
  Area = 0
  ChamferSize = 0
  Closed = false
  End = (10635,6045,3000)
  FilletRadius = 0
  Length = 2598.56
  MakeFace = true
  Placement = pos=(11935,8295,3000) rot=(0,0,1;0rad)
  Points = (2) [(0,0,0),(-1300,-2250,0)]
  Start = (11935,8295,3000)
  Subdivisions = 0
FEATURE [Part::Part2DObjectPython] Line008  # Draft 2D object (typed FeaturePython)
  Area = 0
  ChamferSize = 0
  Closed = false
  End = (15110,6045,3000)
  FilletRadius = 0
  Length = 3770.03
  MakeFace = true
  Placement = pos=(12085,8295,3000) rot=(0,0,1;0rad)
  Points = (2) [(0,0,0),(3025,-2250,0)]
  Start = (12085,8295,3000)
  Subdivisions = 0
FEATURE [Part::Part2DObjectPython] Line009  # Draft 2D object (typed FeaturePython)
  Area = 0
  ChamferSize = 0
  Closed = false
  End = (15110,8295,3000)
  FilletRadius = 0
  Length = 3770.03
  MakeFace = true
  Placement = pos=(12085,6045,3000) rot=(0,0,1;0rad)
  Points = (2) [(0,0,0),(3025,2250,0)]
  Start = (12085,6045,3000)
  Subdivisions = 0
FEATURE [App::FeaturePython] dLabel015  # WARN: FeaturePython — macro-defined, semantics opaque (R4)
  CustomText = Label
  LabelType = 7
  Placement = pos=(1426.97,10253.9,0) rot=(0,0,1;0rad)
  Points = (3) [(1426.97,10253.9,0),(1608.02,10253.9,0),(1881.61,9930.47,0)]
  StraightDirection = 0
  StraightDistance = 181.054
  Target = -> Structure081 [Face6]
  TargetPoint = (1881.61,9930.47,0)
  Text = C01 (25x15)
FEATURE [App::DocumentObjectGroup] Group013  label="2D-003-PB"
  Group = -> [Line,Line001,Line002,Line003,Line004,Line005,dLabel014,Line006,Line007,Line008,Line009,dLabel015]
FEATURE [App::FeaturePython] Section001  label="Section-Estructura s/PB"  # WARN: FeaturePython — macro-defined, semantics opaque (R4)
  Clip = false
  Objects = -> [BuildingPart001,Axis,Axis004,Group013]
  OnlySolids = true
  Placement = pos=(8257.5,5125,3000) rot=(0,0,1;0rad)
  UseMaterialColorForFill = false
FEATURE [TechDraw::DrawViewArch] ArchView001
  AllOn = true
  CutLineWidth = 0.5
  FillSpaces = false
  FontSize = 8
  JoinArch = false
  LineWidth = 0.25
  LockPosition = true
  RenderMode = 0
  Rotation = 0
  Scale = 0.02
  ScaleType = 2
  ShowFill = true
  ShowHidden = true
  Source = -> Section001
  Symbol = <blob: 67347 chars omitted>
  X = 220
  Y = 170
FEATURE [TechDraw::DrawPage] Page  label="ES-003-ESTRUCTURA PB"
  KeepUpdated = true
  NextBalloonIndex = 1
  ProjectionType = 0
  Template = -> Template
  Views = -> [ArchView001]
FEATURE [TechDraw::DrawViewAnnotation] Annotation001
  Font = MS Shell Dlg 2
  LineSpace = 100
  LockPosition = false
  MaxWidth = -1
  Rotation = 0
  ScaleType = 0
  Text = ES-001-PORTADA | ES-002-FUNDACIONES | ES-003-ESTRUCTURA PB
  TextSize = 3
  TextStyle = 0
  X = 64.2069
  Y = 258.988
FEATURE [TechDraw::DrawPage] Page008  label="ES-001-PORTADA"
  KeepUpdated = true
  NextBalloonIndex = 1
  ProjectionType = 0
  Template = -> Template008
  Views = -> [View,Annotation,Annotation001]
FEATURE [App::FeaturePython] dLabel016  # WARN: FeaturePython — macro-defined, semantics opaque (R4)
  CustomText = Label
  LabelType = 7
  Placement = pos=(900,7100,0) rot=(0,0,1;0rad)
  Points = (3) [(900,7100,0),(1600,7100,0),(1693.14,6821.76,0)]
  StraightDirection = 0
  StraightDistance = 700
  Target = -> Structure002 [Face5]
  TargetPoint = (1693.14,6821.76,0)
  Text = B1 (70x70x70)
FEATURE [App::FeaturePython] dLabel017  # WARN: FeaturePython — macro-defined, semantics opaque (R4)
  CustomText = Label
  LabelType = 7
  Placement = pos=(5300,7500,0) rot=(0,0,1;0rad)
  Points = (3) [(5300,7500,0),(5600,7500,0),(5932.62,6863.78,0)]
  StraightDirection = 0
  StraightDistance = 300
  Target = -> Structure014 [Face5]
  TargetPoint = (5932.62,6863.78,0)
  Text = B1 (70x70x70)
FEATURE [App::FeaturePython] dLabel018  # WARN: FeaturePython — macro-defined, semantics opaque (R4)
  CustomText = Label
  LabelType = 7
  Placement = pos=(959.206,8100,0) rot=(0,0,1;0rad)
  Points = (3) [(959.206,8100,0),(1600,8100,0),(1863.47,7811.2,0)]
  StraightDirection = 0
  StraightDistance = 640.794
  Target = -> Structure041 [Face3]
  TargetPoint = (1863.47,7811.2,0)
  Text = VR (30x30)
FEATURE [App::DocumentObjectGroup] Group009  label="2D-002-FUNDACIONES"
  Group = -> [Dimension,Dimension001,Dimension002,Dimension003,Dimension004,Dimension005,Dimension006,Dimension007,Dimension008,Dimension009,Dimension010,dLabel,dLabel001,dLabel002,Dimension011,Dimension012,dLabel008,dLabel009,dLabel010,dLabel011,dLabel012,dLabel016,dLabel017,dLabel018]
FEATURE [App::DocumentObjectGroup] Group003  label="Anotaciones"
  Group = -> [Group,Rectangle001,Group009,Group013]
FEATURE [App::FeaturePython] Section  label="Section-Fundaciones"  # WARN: FeaturePython — macro-defined, semantics opaque (R4)
  Clip = true
  Objects = -> [BuildingPart002,Axis,Axis004,BuildingPart001,Group009]
  OnlySolids = false
  Placement = pos=(7249.97,5075.73,10) rot=(0,0,1;0rad)
  UseMaterialColorForFill = false
FEATURE [App::DocumentObjectGroup] Group008  label="Secciones"
  Group = -> [Section,Section001]
FEATURE [TechDraw::DrawViewArch] ArchView  label="Fundaciones planta"
  AllOn = true
  CutLineWidth = 0.4
  FillSpaces = false
  FontSize = 8
  JoinArch = false
  LineWidth = 0.2
  LockPosition = true
  RenderMode = 0
  Rotation = 0
  Scale = 0.02
  ScaleType = 2
  ShowFill = false
  ShowHidden = false
  Source = -> Section
  Symbol = <blob: 57192 chars omitted>
  X = 220
  Y = 170
FEATURE [TechDraw::DrawPage] Page010  label="ES-002-FUNDACIONES"
  KeepUpdated = true
  NextBalloonIndex = 1
  ProjectionType = 0
  Template = -> Template010
  Views = -> [ArchView]
FEATURE [App::DocumentObjectGroup] Group007  label="PLANOS"
  Group = -> [Page008,Page010,Page]
